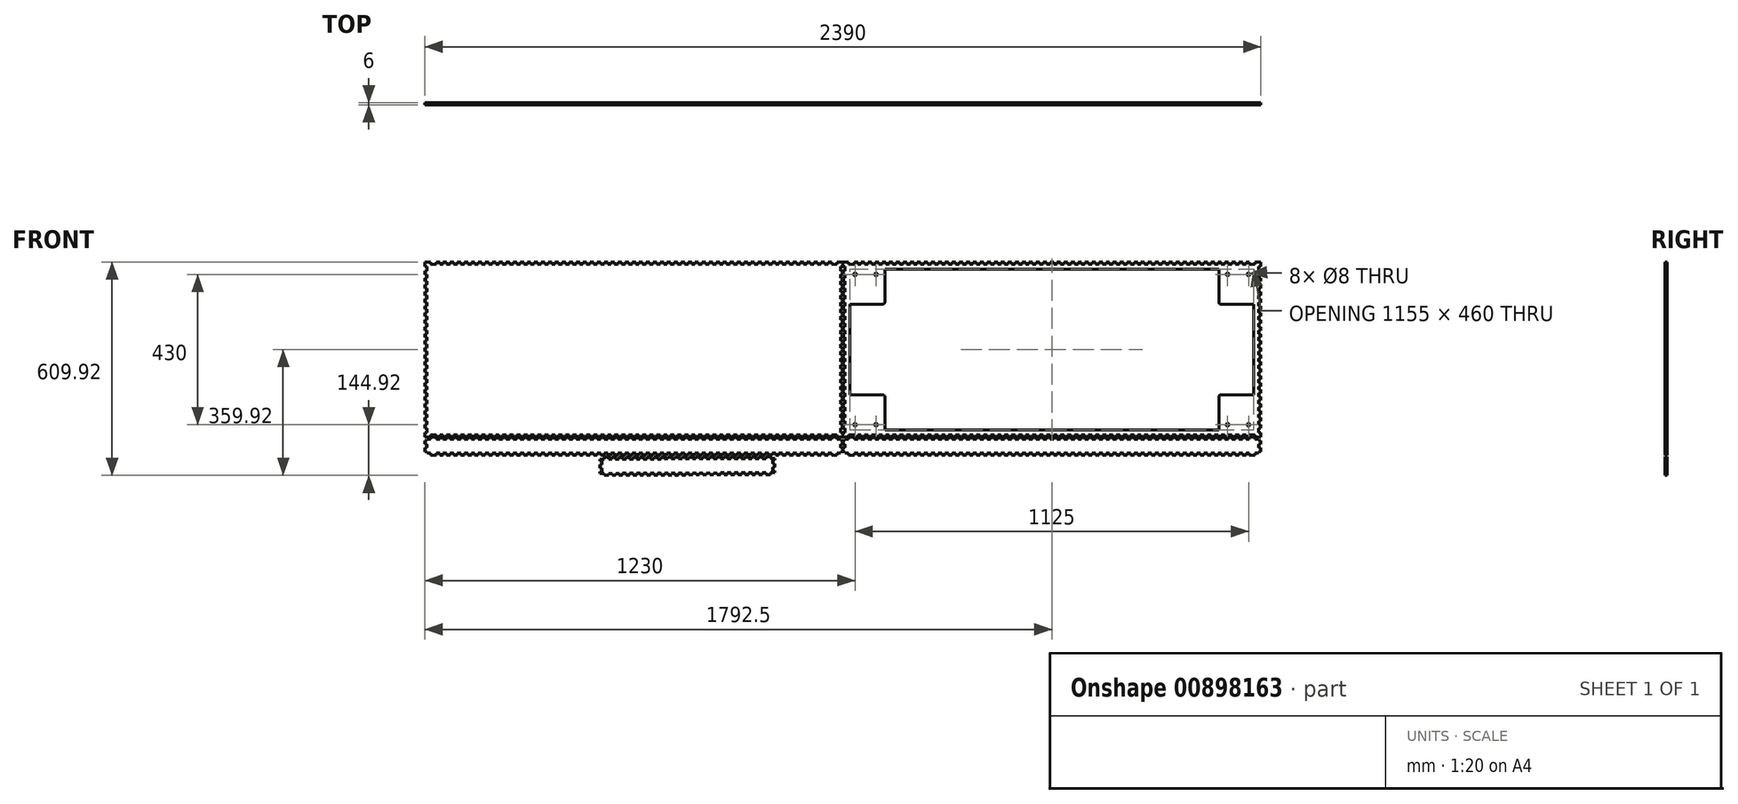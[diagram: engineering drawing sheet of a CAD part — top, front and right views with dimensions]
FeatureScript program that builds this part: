
annotation { "Feature Type Name" : "Feature", "Feature Type Description" : "" }
export const myFeature = defineFeature(function(context is Context, id is Id, definition is map)
    precondition{}
    {
        {
            var Q0;
            Q0=qCreatedBy(makeId("Front.planeOp"),FACE);
            var sketch = newSketch(context, id + "F0", { "sketchPlane" : qUnion([Q0])});
            skLineSegment(sketch, "E0", {"start": v(-1195, 306.06) * mm, "end": v(-1178.75, 306.06) * mm});
            skLineSegment(sketch, "E1", {"start": v(-1178.75, 306.06) * mm, "end": v(-1178.75, 300.06) * mm});
            skLineSegment(sketch, "E2", {"start": v(-1178.75, 300.06) * mm, "end": v(-1162.5, 300.06) * mm});
            skLineSegment(sketch, "E3", {"start": v(-1162.5, 300.06) * mm, "end": v(-1162.5, 306.06) * mm});
            skLineSegment(sketch, "E4", {"start": v(-1162.5, 306.06) * mm, "end": v(-1152.5, 306.06) * mm});
            skLineSegment(sketch, "E5", {"start": v(-1152.5, 306.06) * mm, "end": v(-1152.5, 300.06) * mm});
            skLineSegment(sketch, "E6", {"start": v(-1152.5, 300.06) * mm, "end": v(-1142.5, 300.06) * mm});
            skLineSegment(sketch, "E7", {"start": v(-1142.5, 300.06) * mm, "end": v(-1142.5, 306.06) * mm});
            skLineSegment(sketch, "E8", {"start": v(-1142.5, 306.06) * mm, "end": v(-1132.5, 306.06) * mm});
            skLineSegment(sketch, "E9", {"start": v(-1132.5, 306.06) * mm, "end": v(-1132.5, 300.06) * mm});
            skLineSegment(sketch, "E10", {"start": v(-1132.5, 300.06) * mm, "end": v(-1122.5, 300.06) * mm});
            skLineSegment(sketch, "E11", {"start": v(-1122.5, 300.06) * mm, "end": v(-1122.5, 306.06) * mm});
            skLineSegment(sketch, "E12", {"start": v(-1122.5, 306.06) * mm, "end": v(-1112.5, 306.06) * mm});
            skLineSegment(sketch, "E13", {"start": v(-1112.5, 306.06) * mm, "end": v(-1112.5, 300.06) * mm});
            skLineSegment(sketch, "E14", {"start": v(-1112.5, 300.06) * mm, "end": v(-1102.5, 300.06) * mm});
            skLineSegment(sketch, "E15", {"start": v(-1102.5, 300.06) * mm, "end": v(-1102.5, 306.06) * mm});
            skLineSegment(sketch, "E16", {"start": v(-1102.5, 306.06) * mm, "end": v(-1092.5, 306.06) * mm});
            skLineSegment(sketch, "E17", {"start": v(-1092.5, 306.06) * mm, "end": v(-1092.5, 300.06) * mm});
            skLineSegment(sketch, "E18", {"start": v(-1092.5, 300.06) * mm, "end": v(-1082.5, 300.06) * mm});
            skLineSegment(sketch, "E19", {"start": v(-1082.5, 300.06) * mm, "end": v(-1082.5, 306.06) * mm});
            skLineSegment(sketch, "E20", {"start": v(-1082.5, 306.06) * mm, "end": v(-1072.5, 306.06) * mm});
            skLineSegment(sketch, "E21", {"start": v(-1072.5, 306.06) * mm, "end": v(-1072.5, 300.06) * mm});
            skLineSegment(sketch, "E22", {"start": v(-1072.5, 300.06) * mm, "end": v(-1062.5, 300.06) * mm});
            skLineSegment(sketch, "E23", {"start": v(-1062.5, 300.06) * mm, "end": v(-1062.5, 306.06) * mm});
            skLineSegment(sketch, "E24", {"start": v(-1062.5, 306.06) * mm, "end": v(-1052.5, 306.06) * mm});
            skLineSegment(sketch, "E25", {"start": v(-1052.5, 306.06) * mm, "end": v(-1052.5, 300.06) * mm});
            skLineSegment(sketch, "E26", {"start": v(-1052.5, 300.06) * mm, "end": v(-1042.5, 300.06) * mm});
            skLineSegment(sketch, "E27", {"start": v(-1042.5, 300.06) * mm, "end": v(-1042.5, 306.06) * mm});
            skLineSegment(sketch, "E28", {"start": v(-1042.5, 306.06) * mm, "end": v(-1032.5, 306.06) * mm});
            skLineSegment(sketch, "E29", {"start": v(-1032.5, 306.06) * mm, "end": v(-1032.5, 300.06) * mm});
            skLineSegment(sketch, "E30", {"start": v(-1032.5, 300.06) * mm, "end": v(-1022.5, 300.06) * mm});
            skLineSegment(sketch, "E31", {"start": v(-1022.5, 300.06) * mm, "end": v(-1022.5, 306.06) * mm});
            skLineSegment(sketch, "E32", {"start": v(-1022.5, 306.06) * mm, "end": v(-1012.5, 306.06) * mm});
            skLineSegment(sketch, "E33", {"start": v(-1012.5, 306.06) * mm, "end": v(-1012.5, 300.06) * mm});
            skLineSegment(sketch, "E34", {"start": v(-1012.5, 300.06) * mm, "end": v(-1002.5, 300.06) * mm});
            skLineSegment(sketch, "E35", {"start": v(-1002.5, 300.06) * mm, "end": v(-1002.5, 306.06) * mm});
            skLineSegment(sketch, "E36", {"start": v(-1002.5, 306.06) * mm, "end": v(-992.5, 306.06) * mm});
            skLineSegment(sketch, "E37", {"start": v(-992.5, 306.06) * mm, "end": v(-992.5, 300.06) * mm});
            skLineSegment(sketch, "E38", {"start": v(-992.5, 300.06) * mm, "end": v(-982.5, 300.06) * mm});
            skLineSegment(sketch, "E39", {"start": v(-982.5, 300.06) * mm, "end": v(-982.5, 306.06) * mm});
            skLineSegment(sketch, "E40", {"start": v(-982.5, 306.06) * mm, "end": v(-972.5, 306.06) * mm});
            skLineSegment(sketch, "E41", {"start": v(-972.5, 306.06) * mm, "end": v(-972.5, 300.06) * mm});
            skLineSegment(sketch, "E42", {"start": v(-972.5, 300.06) * mm, "end": v(-962.5, 300.06) * mm});
            skLineSegment(sketch, "E43", {"start": v(-962.5, 300.06) * mm, "end": v(-962.5, 306.06) * mm});
            skLineSegment(sketch, "E44", {"start": v(-962.5, 306.06) * mm, "end": v(-952.5, 306.06) * mm});
            skLineSegment(sketch, "E45", {"start": v(-952.5, 306.06) * mm, "end": v(-952.5, 300.06) * mm});
            skLineSegment(sketch, "E46", {"start": v(-952.5, 300.06) * mm, "end": v(-942.5, 300.06) * mm});
            skLineSegment(sketch, "E47", {"start": v(-942.5, 300.06) * mm, "end": v(-942.5, 306.06) * mm});
            skLineSegment(sketch, "E48", {"start": v(-942.5, 306.06) * mm, "end": v(-932.5, 306.06) * mm});
            skLineSegment(sketch, "E49", {"start": v(-932.5, 306.06) * mm, "end": v(-932.5, 300.06) * mm});
            skLineSegment(sketch, "E50", {"start": v(-932.5, 300.06) * mm, "end": v(-922.5, 300.06) * mm});
            skLineSegment(sketch, "E51", {"start": v(-922.5, 300.06) * mm, "end": v(-922.5, 306.06) * mm});
            skLineSegment(sketch, "E52", {"start": v(-922.5, 306.06) * mm, "end": v(-912.5, 306.06) * mm});
            skLineSegment(sketch, "E53", {"start": v(-912.5, 306.06) * mm, "end": v(-912.5, 300.06) * mm});
            skLineSegment(sketch, "E54", {"start": v(-912.5, 300.06) * mm, "end": v(-902.5, 300.06) * mm});
            skLineSegment(sketch, "E55", {"start": v(-902.5, 300.06) * mm, "end": v(-902.5, 306.06) * mm});
            skLineSegment(sketch, "E56", {"start": v(-902.5, 306.06) * mm, "end": v(-892.5, 306.06) * mm});
            skLineSegment(sketch, "E57", {"start": v(-892.5, 306.06) * mm, "end": v(-892.5, 300.06) * mm});
            skLineSegment(sketch, "E58", {"start": v(-892.5, 300.06) * mm, "end": v(-882.5, 300.06) * mm});
            skLineSegment(sketch, "E59", {"start": v(-882.5, 300.06) * mm, "end": v(-882.5, 306.06) * mm});
            skLineSegment(sketch, "E60", {"start": v(-882.5, 306.06) * mm, "end": v(-872.5, 306.06) * mm});
            skLineSegment(sketch, "E61", {"start": v(-872.5, 306.06) * mm, "end": v(-872.5, 300.06) * mm});
            skLineSegment(sketch, "E62", {"start": v(-872.5, 300.06) * mm, "end": v(-862.5, 300.06) * mm});
            skLineSegment(sketch, "E63", {"start": v(-862.5, 300.06) * mm, "end": v(-862.5, 306.06) * mm});
            skLineSegment(sketch, "E64", {"start": v(-862.5, 306.06) * mm, "end": v(-852.5, 306.06) * mm});
            skLineSegment(sketch, "E65", {"start": v(-852.5, 306.06) * mm, "end": v(-852.5, 300.06) * mm});
            skLineSegment(sketch, "E66", {"start": v(-852.5, 300.06) * mm, "end": v(-842.5, 300.06) * mm});
            skLineSegment(sketch, "E67", {"start": v(-842.5, 300.06) * mm, "end": v(-842.5, 306.06) * mm});
            skLineSegment(sketch, "E68", {"start": v(-842.5, 306.06) * mm, "end": v(-832.5, 306.06) * mm});
            skLineSegment(sketch, "E69", {"start": v(-832.5, 306.06) * mm, "end": v(-832.5, 300.06) * mm});
            skLineSegment(sketch, "E70", {"start": v(-832.5, 300.06) * mm, "end": v(-822.5, 300.06) * mm});
            skLineSegment(sketch, "E71", {"start": v(-822.5, 300.06) * mm, "end": v(-822.5, 306.06) * mm});
            skLineSegment(sketch, "E72", {"start": v(-822.5, 306.06) * mm, "end": v(-812.5, 306.06) * mm});
            skLineSegment(sketch, "E73", {"start": v(-812.5, 306.06) * mm, "end": v(-812.5, 300.06) * mm});
            skLineSegment(sketch, "E74", {"start": v(-812.5, 300.06) * mm, "end": v(-802.5, 300.06) * mm});
            skLineSegment(sketch, "E75", {"start": v(-802.5, 300.06) * mm, "end": v(-802.5, 306.06) * mm});
            skLineSegment(sketch, "E76", {"start": v(-802.5, 306.06) * mm, "end": v(-792.5, 306.06) * mm});
            skLineSegment(sketch, "E77", {"start": v(-792.5, 306.06) * mm, "end": v(-792.5, 300.06) * mm});
            skLineSegment(sketch, "E78", {"start": v(-792.5, 300.06) * mm, "end": v(-782.5, 300.06) * mm});
            skLineSegment(sketch, "E79", {"start": v(-782.5, 300.06) * mm, "end": v(-782.5, 306.06) * mm});
            skLineSegment(sketch, "E80", {"start": v(-782.5, 306.06) * mm, "end": v(-772.5, 306.06) * mm});
            skLineSegment(sketch, "E81", {"start": v(-772.5, 306.06) * mm, "end": v(-772.5, 300.06) * mm});
            skLineSegment(sketch, "E82", {"start": v(-772.5, 300.06) * mm, "end": v(-762.5, 300.06) * mm});
            skLineSegment(sketch, "E83", {"start": v(-762.5, 300.06) * mm, "end": v(-762.5, 306.06) * mm});
            skLineSegment(sketch, "E84", {"start": v(-762.5, 306.06) * mm, "end": v(-752.5, 306.06) * mm});
            skLineSegment(sketch, "E85", {"start": v(-752.5, 306.06) * mm, "end": v(-752.5, 300.06) * mm});
            skLineSegment(sketch, "E86", {"start": v(-752.5, 300.06) * mm, "end": v(-742.5, 300.06) * mm});
            skLineSegment(sketch, "E87", {"start": v(-742.5, 300.06) * mm, "end": v(-742.5, 306.06) * mm});
            skLineSegment(sketch, "E88", {"start": v(-742.5, 306.06) * mm, "end": v(-732.5, 306.06) * mm});
            skLineSegment(sketch, "E89", {"start": v(-732.5, 306.06) * mm, "end": v(-732.5, 300.06) * mm});
            skLineSegment(sketch, "E90", {"start": v(-732.5, 300.06) * mm, "end": v(-722.5, 300.06) * mm});
            skLineSegment(sketch, "E91", {"start": v(-722.5, 300.06) * mm, "end": v(-722.5, 306.06) * mm});
            skLineSegment(sketch, "E92", {"start": v(-722.5, 306.06) * mm, "end": v(-712.5, 306.06) * mm});
            skLineSegment(sketch, "E93", {"start": v(-712.5, 306.06) * mm, "end": v(-712.5, 300.06) * mm});
            skLineSegment(sketch, "E94", {"start": v(-712.5, 300.06) * mm, "end": v(-702.5, 300.06) * mm});
            skLineSegment(sketch, "E95", {"start": v(-702.5, 300.06) * mm, "end": v(-702.5, 306.06) * mm});
            skLineSegment(sketch, "E96", {"start": v(-702.5, 306.06) * mm, "end": v(-692.5, 306.06) * mm});
            skLineSegment(sketch, "E97", {"start": v(-692.5, 306.06) * mm, "end": v(-692.5, 300.06) * mm});
            skLineSegment(sketch, "E98", {"start": v(-692.5, 300.06) * mm, "end": v(-682.5, 300.06) * mm});
            skLineSegment(sketch, "E99", {"start": v(-682.5, 300.06) * mm, "end": v(-682.5, 306.06) * mm});
            skLineSegment(sketch, "E100", {"start": v(-682.5, 306.06) * mm, "end": v(-672.5, 306.06) * mm});
            skLineSegment(sketch, "E101", {"start": v(-672.5, 306.06) * mm, "end": v(-672.5, 300.06) * mm});
            skLineSegment(sketch, "E102", {"start": v(-672.5, 300.06) * mm, "end": v(-662.5, 300.06) * mm});
            skLineSegment(sketch, "E103", {"start": v(-662.5, 300.06) * mm, "end": v(-662.5, 306.06) * mm});
            skLineSegment(sketch, "E104", {"start": v(-662.5, 306.06) * mm, "end": v(-652.5, 306.06) * mm});
            skLineSegment(sketch, "E105", {"start": v(-652.5, 306.06) * mm, "end": v(-652.5, 300.06) * mm});
            skLineSegment(sketch, "E106", {"start": v(-652.5, 300.06) * mm, "end": v(-642.5, 300.06) * mm});
            skLineSegment(sketch, "E107", {"start": v(-642.5, 300.06) * mm, "end": v(-642.5, 306.06) * mm});
            skLineSegment(sketch, "E108", {"start": v(-642.5, 306.06) * mm, "end": v(-632.5, 306.06) * mm});
            skLineSegment(sketch, "E109", {"start": v(-632.5, 306.06) * mm, "end": v(-632.5, 300.06) * mm});
            skLineSegment(sketch, "E110", {"start": v(-632.5, 300.06) * mm, "end": v(-622.5, 300.06) * mm});
            skLineSegment(sketch, "E111", {"start": v(-622.5, 300.06) * mm, "end": v(-622.5, 306.06) * mm});
            skLineSegment(sketch, "E112", {"start": v(-622.5, 306.06) * mm, "end": v(-612.5, 306.06) * mm});
            skLineSegment(sketch, "E113", {"start": v(-612.5, 306.06) * mm, "end": v(-612.5, 300.06) * mm});
            skLineSegment(sketch, "E114", {"start": v(-612.5, 300.06) * mm, "end": v(-602.5, 300.06) * mm});
            skLineSegment(sketch, "E115", {"start": v(-602.5, 300.06) * mm, "end": v(-602.5, 306.06) * mm});
            skLineSegment(sketch, "E116", {"start": v(-602.5, 306.06) * mm, "end": v(-592.5, 306.06) * mm});
            skLineSegment(sketch, "E117", {"start": v(-592.5, 306.06) * mm, "end": v(-592.5, 300.06) * mm});
            skLineSegment(sketch, "E118", {"start": v(-592.5, 300.06) * mm, "end": v(-582.5, 300.06) * mm});
            skLineSegment(sketch, "E119", {"start": v(-582.5, 300.06) * mm, "end": v(-582.5, 306.06) * mm});
            skLineSegment(sketch, "E120", {"start": v(-582.5, 306.06) * mm, "end": v(-572.5, 306.06) * mm});
            skLineSegment(sketch, "E121", {"start": v(-572.5, 306.06) * mm, "end": v(-572.5, 300.06) * mm});
            skLineSegment(sketch, "E122", {"start": v(-572.5, 300.06) * mm, "end": v(-562.5, 300.06) * mm});
            skLineSegment(sketch, "E123", {"start": v(-562.5, 300.06) * mm, "end": v(-562.5, 306.06) * mm});
            skLineSegment(sketch, "E124", {"start": v(-562.5, 306.06) * mm, "end": v(-552.5, 306.06) * mm});
            skLineSegment(sketch, "E125", {"start": v(-552.5, 306.06) * mm, "end": v(-552.5, 300.06) * mm});
            skLineSegment(sketch, "E126", {"start": v(-552.5, 300.06) * mm, "end": v(-542.5, 300.06) * mm});
            skLineSegment(sketch, "E127", {"start": v(-542.5, 300.06) * mm, "end": v(-542.5, 306.06) * mm});
            skLineSegment(sketch, "E128", {"start": v(-542.5, 306.06) * mm, "end": v(-532.5, 306.06) * mm});
            skLineSegment(sketch, "E129", {"start": v(-532.5, 306.06) * mm, "end": v(-532.5, 300.06) * mm});
            skLineSegment(sketch, "E130", {"start": v(-532.5, 300.06) * mm, "end": v(-522.5, 300.06) * mm});
            skLineSegment(sketch, "E131", {"start": v(-522.5, 300.06) * mm, "end": v(-522.5, 306.06) * mm});
            skLineSegment(sketch, "E132", {"start": v(-522.5, 306.06) * mm, "end": v(-512.5, 306.06) * mm});
            skLineSegment(sketch, "E133", {"start": v(-512.5, 306.06) * mm, "end": v(-512.5, 300.06) * mm});
            skLineSegment(sketch, "E134", {"start": v(-512.5, 300.06) * mm, "end": v(-502.5, 300.06) * mm});
            skLineSegment(sketch, "E135", {"start": v(-502.5, 300.06) * mm, "end": v(-502.5, 306.06) * mm});
            skLineSegment(sketch, "E136", {"start": v(-502.5, 306.06) * mm, "end": v(-492.5, 306.06) * mm});
            skLineSegment(sketch, "E137", {"start": v(-492.5, 306.06) * mm, "end": v(-492.5, 300.06) * mm});
            skLineSegment(sketch, "E138", {"start": v(-492.5, 300.06) * mm, "end": v(-482.5, 300.06) * mm});
            skLineSegment(sketch, "E139", {"start": v(-482.5, 300.06) * mm, "end": v(-482.5, 306.06) * mm});
            skLineSegment(sketch, "E140", {"start": v(-482.5, 306.06) * mm, "end": v(-472.5, 306.06) * mm});
            skLineSegment(sketch, "E141", {"start": v(-472.5, 306.06) * mm, "end": v(-472.5, 300.06) * mm});
            skLineSegment(sketch, "E142", {"start": v(-472.5, 300.06) * mm, "end": v(-462.5, 300.06) * mm});
            skLineSegment(sketch, "E143", {"start": v(-462.5, 300.06) * mm, "end": v(-462.5, 306.06) * mm});
            skLineSegment(sketch, "E144", {"start": v(-462.5, 306.06) * mm, "end": v(-452.5, 306.06) * mm});
            skLineSegment(sketch, "E145", {"start": v(-452.5, 306.06) * mm, "end": v(-452.5, 300.06) * mm});
            skLineSegment(sketch, "E146", {"start": v(-452.5, 300.06) * mm, "end": v(-442.5, 300.06) * mm});
            skLineSegment(sketch, "E147", {"start": v(-442.5, 300.06) * mm, "end": v(-442.5, 306.06) * mm});
            skLineSegment(sketch, "E148", {"start": v(-442.5, 306.06) * mm, "end": v(-432.5, 306.06) * mm});
            skLineSegment(sketch, "E149", {"start": v(-432.5, 306.06) * mm, "end": v(-432.5, 300.06) * mm});
            skLineSegment(sketch, "E150", {"start": v(-432.5, 300.06) * mm, "end": v(-422.5, 300.06) * mm});
            skLineSegment(sketch, "E151", {"start": v(-422.5, 300.06) * mm, "end": v(-422.5, 306.06) * mm});
            skLineSegment(sketch, "E152", {"start": v(-422.5, 306.06) * mm, "end": v(-412.5, 306.06) * mm});
            skLineSegment(sketch, "E153", {"start": v(-412.5, 306.06) * mm, "end": v(-412.5, 300.06) * mm});
            skLineSegment(sketch, "E154", {"start": v(-412.5, 300.06) * mm, "end": v(-402.5, 300.06) * mm});
            skLineSegment(sketch, "E155", {"start": v(-402.5, 300.06) * mm, "end": v(-402.5, 306.06) * mm});
            skLineSegment(sketch, "E156", {"start": v(-402.5, 306.06) * mm, "end": v(-392.5, 306.06) * mm});
            skLineSegment(sketch, "E157", {"start": v(-392.5, 306.06) * mm, "end": v(-392.5, 300.06) * mm});
            skLineSegment(sketch, "E158", {"start": v(-392.5, 300.06) * mm, "end": v(-382.5, 300.06) * mm});
            skLineSegment(sketch, "E159", {"start": v(-382.5, 300.06) * mm, "end": v(-382.5, 306.06) * mm});
            skLineSegment(sketch, "E160", {"start": v(-382.5, 306.06) * mm, "end": v(-372.5, 306.06) * mm});
            skLineSegment(sketch, "E161", {"start": v(-372.5, 306.06) * mm, "end": v(-372.5, 300.06) * mm});
            skLineSegment(sketch, "E162", {"start": v(-372.5, 300.06) * mm, "end": v(-362.5, 300.06) * mm});
            skLineSegment(sketch, "E163", {"start": v(-362.5, 300.06) * mm, "end": v(-362.5, 306.06) * mm});
            skLineSegment(sketch, "E164", {"start": v(-362.5, 306.06) * mm, "end": v(-352.5, 306.06) * mm});
            skLineSegment(sketch, "E165", {"start": v(-352.5, 306.06) * mm, "end": v(-352.5, 300.06) * mm});
            skLineSegment(sketch, "E166", {"start": v(-352.5, 300.06) * mm, "end": v(-342.5, 300.06) * mm});
            skLineSegment(sketch, "E167", {"start": v(-342.5, 300.06) * mm, "end": v(-342.5, 306.06) * mm});
            skLineSegment(sketch, "E168", {"start": v(-342.5, 306.06) * mm, "end": v(-332.5, 306.06) * mm});
            skLineSegment(sketch, "E169", {"start": v(-332.5, 306.06) * mm, "end": v(-332.5, 300.06) * mm});
            skLineSegment(sketch, "E170", {"start": v(-332.5, 300.06) * mm, "end": v(-322.5, 300.06) * mm});
            skLineSegment(sketch, "E171", {"start": v(-322.5, 300.06) * mm, "end": v(-322.5, 306.06) * mm});
            skLineSegment(sketch, "E172", {"start": v(-322.5, 306.06) * mm, "end": v(-312.5, 306.06) * mm});
            skLineSegment(sketch, "E173", {"start": v(-312.5, 306.06) * mm, "end": v(-312.5, 300.06) * mm});
            skLineSegment(sketch, "E174", {"start": v(-312.5, 300.06) * mm, "end": v(-302.5, 300.06) * mm});
            skLineSegment(sketch, "E175", {"start": v(-302.5, 300.06) * mm, "end": v(-302.5, 306.06) * mm});
            skLineSegment(sketch, "E176", {"start": v(-302.5, 306.06) * mm, "end": v(-292.5, 306.06) * mm});
            skLineSegment(sketch, "E177", {"start": v(-292.5, 306.06) * mm, "end": v(-292.5, 300.06) * mm});
            skLineSegment(sketch, "E178", {"start": v(-292.5, 300.06) * mm, "end": v(-282.5, 300.06) * mm});
            skLineSegment(sketch, "E179", {"start": v(-282.5, 300.06) * mm, "end": v(-282.5, 306.06) * mm});
            skLineSegment(sketch, "E180", {"start": v(-282.5, 306.06) * mm, "end": v(-272.5, 306.06) * mm});
            skLineSegment(sketch, "E181", {"start": v(-272.5, 306.06) * mm, "end": v(-272.5, 300.06) * mm});
            skLineSegment(sketch, "E182", {"start": v(-272.5, 300.06) * mm, "end": v(-262.5, 300.06) * mm});
            skLineSegment(sketch, "E183", {"start": v(-262.5, 300.06) * mm, "end": v(-262.5, 306.06) * mm});
            skLineSegment(sketch, "E184", {"start": v(-262.5, 306.06) * mm, "end": v(-252.5, 306.06) * mm});
            skLineSegment(sketch, "E185", {"start": v(-252.5, 306.06) * mm, "end": v(-252.5, 300.06) * mm});
            skLineSegment(sketch, "E186", {"start": v(-252.5, 300.06) * mm, "end": v(-242.5, 300.06) * mm});
            skLineSegment(sketch, "E187", {"start": v(-242.5, 300.06) * mm, "end": v(-242.5, 306.06) * mm});
            skLineSegment(sketch, "E188", {"start": v(-242.5, 306.06) * mm, "end": v(-232.5, 306.06) * mm});
            skLineSegment(sketch, "E189", {"start": v(-232.5, 306.06) * mm, "end": v(-232.5, 300.06) * mm});
            skLineSegment(sketch, "E190", {"start": v(-232.5, 300.06) * mm, "end": v(-222.5, 300.06) * mm});
            skLineSegment(sketch, "E191", {"start": v(-222.5, 300.06) * mm, "end": v(-222.5, 306.06) * mm});
            skLineSegment(sketch, "E192", {"start": v(-222.5, 306.06) * mm, "end": v(-212.5, 306.06) * mm});
            skLineSegment(sketch, "E193", {"start": v(-212.5, 306.06) * mm, "end": v(-212.5, 300.06) * mm});
            skLineSegment(sketch, "E194", {"start": v(-212.5, 300.06) * mm, "end": v(-202.5, 300.06) * mm});
            skLineSegment(sketch, "E195", {"start": v(-202.5, 300.06) * mm, "end": v(-202.5, 306.06) * mm});
            skLineSegment(sketch, "E196", {"start": v(-202.5, 306.06) * mm, "end": v(-192.5, 306.06) * mm});
            skLineSegment(sketch, "E197", {"start": v(-192.5, 306.06) * mm, "end": v(-192.5, 300.06) * mm});
            skLineSegment(sketch, "E198", {"start": v(-192.5, 300.06) * mm, "end": v(-182.5, 300.06) * mm});
            skLineSegment(sketch, "E199", {"start": v(-182.5, 300.06) * mm, "end": v(-182.5, 306.06) * mm});
            skLineSegment(sketch, "E200", {"start": v(-182.5, 306.06) * mm, "end": v(-172.5, 306.06) * mm});
            skLineSegment(sketch, "E201", {"start": v(-172.5, 306.06) * mm, "end": v(-172.5, 300.06) * mm});
            skLineSegment(sketch, "E202", {"start": v(-172.5, 300.06) * mm, "end": v(-162.5, 300.06) * mm});
            skLineSegment(sketch, "E203", {"start": v(-162.5, 300.06) * mm, "end": v(-162.5, 306.06) * mm});
            skLineSegment(sketch, "E204", {"start": v(-162.5, 306.06) * mm, "end": v(-152.5, 306.06) * mm});
            skLineSegment(sketch, "E205", {"start": v(-152.5, 306.06) * mm, "end": v(-152.5, 300.06) * mm});
            skLineSegment(sketch, "E206", {"start": v(-152.5, 300.06) * mm, "end": v(-142.5, 300.06) * mm});
            skLineSegment(sketch, "E207", {"start": v(-142.5, 300.06) * mm, "end": v(-142.5, 306.06) * mm});
            skLineSegment(sketch, "E208", {"start": v(-142.5, 306.06) * mm, "end": v(-132.5, 306.06) * mm});
            skLineSegment(sketch, "E209", {"start": v(-132.5, 306.06) * mm, "end": v(-132.5, 300.06) * mm});
            skLineSegment(sketch, "E210", {"start": v(-132.5, 300.06) * mm, "end": v(-122.5, 300.06) * mm});
            skLineSegment(sketch, "E211", {"start": v(-122.5, 300.06) * mm, "end": v(-122.5, 306.06) * mm});
            skLineSegment(sketch, "E212", {"start": v(-122.5, 306.06) * mm, "end": v(-112.5, 306.06) * mm});
            skLineSegment(sketch, "E213", {"start": v(-112.5, 306.06) * mm, "end": v(-112.5, 300.06) * mm});
            skLineSegment(sketch, "E214", {"start": v(-112.5, 300.06) * mm, "end": v(-102.5, 300.06) * mm});
            skLineSegment(sketch, "E215", {"start": v(-102.5, 300.06) * mm, "end": v(-102.5, 306.06) * mm});
            skLineSegment(sketch, "E216", {"start": v(-102.5, 306.06) * mm, "end": v(-92.5, 306.06) * mm});
            skLineSegment(sketch, "E217", {"start": v(-92.5, 306.06) * mm, "end": v(-92.5, 300.06) * mm});
            skLineSegment(sketch, "E218", {"start": v(-92.5, 300.06) * mm, "end": v(-82.5, 300.06) * mm});
            skLineSegment(sketch, "E219", {"start": v(-82.5, 300.06) * mm, "end": v(-82.5, 306.06) * mm});
            skLineSegment(sketch, "E220", {"start": v(-82.5, 306.06) * mm, "end": v(-72.5, 306.06) * mm});
            skLineSegment(sketch, "E221", {"start": v(-72.5, 306.06) * mm, "end": v(-72.5, 300.06) * mm});
            skLineSegment(sketch, "E222", {"start": v(-72.5, 300.06) * mm, "end": v(-62.5, 300.06) * mm});
            skLineSegment(sketch, "E223", {"start": v(-62.5, 300.06) * mm, "end": v(-62.5, 306.06) * mm});
            skLineSegment(sketch, "E224", {"start": v(-62.5, 306.06) * mm, "end": v(-52.5, 306.06) * mm});
            skLineSegment(sketch, "E225", {"start": v(-52.5, 306.06) * mm, "end": v(-52.5, 300.06) * mm});
            skLineSegment(sketch, "E226", {"start": v(-52.5, 300.06) * mm, "end": v(-42.5, 300.06) * mm});
            skLineSegment(sketch, "E227", {"start": v(-42.5, 300.06) * mm, "end": v(-42.5, 306.06) * mm});
            skLineSegment(sketch, "E228", {"start": v(-42.5, 306.06) * mm, "end": v(-32.5, 306.06) * mm});
            skLineSegment(sketch, "E229", {"start": v(-32.5, 306.06) * mm, "end": v(-32.5, 300.06) * mm});
            skLineSegment(sketch, "E230", {"start": v(-32.5, 300.06) * mm, "end": v(-16.25, 300.06) * mm});
            skLineSegment(sketch, "E231", {"start": v(-16.25, 300.06) * mm, "end": v(-16.25, 306.06) * mm});
            skLineSegment(sketch, "E232", {"start": v(-16.25, 306.06) * mm, "end": v(0, 306.06) * mm});
            skLineSegment(sketch, "E233", {"start": v(0, 306.06) * mm, "end": v(0, 293.56) * mm});
            skLineSegment(sketch, "E234", {"start": v(0, 293.56) * mm, "end": v(-6, 293.56) * mm});
            skLineSegment(sketch, "E235", {"start": v(-6, 293.56) * mm, "end": v(-6, 281.06) * mm});
            skLineSegment(sketch, "E236", {"start": v(-6, 281.06) * mm, "end": v(0, 281.06) * mm});
            skLineSegment(sketch, "E237", {"start": v(0, 281.06) * mm, "end": v(0, 271.06) * mm});
            skLineSegment(sketch, "E238", {"start": v(0, 271.06) * mm, "end": v(-6, 271.06) * mm});
            skLineSegment(sketch, "E239", {"start": v(-6, 271.06) * mm, "end": v(-6, 261.06) * mm});
            skLineSegment(sketch, "E240", {"start": v(-6, 261.06) * mm, "end": v(0, 261.06) * mm});
            skLineSegment(sketch, "E241", {"start": v(0, 261.06) * mm, "end": v(0, 251.06) * mm});
            skLineSegment(sketch, "E242", {"start": v(0, 251.06) * mm, "end": v(-6, 251.06) * mm});
            skLineSegment(sketch, "E243", {"start": v(-6, 251.06) * mm, "end": v(-6, 241.06) * mm});
            skLineSegment(sketch, "E244", {"start": v(-6, 241.06) * mm, "end": v(0, 241.06) * mm});
            skLineSegment(sketch, "E245", {"start": v(0, 241.06) * mm, "end": v(0, 231.06) * mm});
            skLineSegment(sketch, "E246", {"start": v(0, 231.06) * mm, "end": v(-6, 231.06) * mm});
            skLineSegment(sketch, "E247", {"start": v(-6, 231.06) * mm, "end": v(-6, 221.06) * mm});
            skLineSegment(sketch, "E248", {"start": v(-6, 221.06) * mm, "end": v(0, 221.06) * mm});
            skLineSegment(sketch, "E249", {"start": v(0, 221.06) * mm, "end": v(0, 211.06) * mm});
            skLineSegment(sketch, "E250", {"start": v(0, 211.06) * mm, "end": v(-6, 211.06) * mm});
            skLineSegment(sketch, "E251", {"start": v(-6, 211.06) * mm, "end": v(-6, 201.06) * mm});
            skLineSegment(sketch, "E252", {"start": v(-6, 201.06) * mm, "end": v(0, 201.06) * mm});
            skLineSegment(sketch, "E253", {"start": v(0, 201.06) * mm, "end": v(0, 191.06) * mm});
            skLineSegment(sketch, "E254", {"start": v(0, 191.06) * mm, "end": v(-6, 191.06) * mm});
            skLineSegment(sketch, "E255", {"start": v(-6, 191.06) * mm, "end": v(-6, 181.06) * mm});
            skLineSegment(sketch, "E256", {"start": v(-6, 181.06) * mm, "end": v(0, 181.06) * mm});
            skLineSegment(sketch, "E257", {"start": v(0, 181.06) * mm, "end": v(0, 171.06) * mm});
            skLineSegment(sketch, "E258", {"start": v(0, 171.06) * mm, "end": v(-6, 171.06) * mm});
            skLineSegment(sketch, "E259", {"start": v(-6, 171.06) * mm, "end": v(-6, 161.06) * mm});
            skLineSegment(sketch, "E260", {"start": v(-6, 161.06) * mm, "end": v(0, 161.06) * mm});
            skLineSegment(sketch, "E261", {"start": v(0, 161.06) * mm, "end": v(0, 151.06) * mm});
            skLineSegment(sketch, "E262", {"start": v(0, 151.06) * mm, "end": v(-6, 151.06) * mm});
            skLineSegment(sketch, "E263", {"start": v(-6, 151.06) * mm, "end": v(-6, 141.06) * mm});
            skLineSegment(sketch, "E264", {"start": v(-6, 141.06) * mm, "end": v(0, 141.06) * mm});
            skLineSegment(sketch, "E265", {"start": v(0, 141.06) * mm, "end": v(0, 131.06) * mm});
            skLineSegment(sketch, "E266", {"start": v(0, 131.06) * mm, "end": v(-6, 131.06) * mm});
            skLineSegment(sketch, "E267", {"start": v(-6, 131.06) * mm, "end": v(-6, 121.06) * mm});
            skLineSegment(sketch, "E268", {"start": v(-6, 121.06) * mm, "end": v(0, 121.06) * mm});
            skLineSegment(sketch, "E269", {"start": v(0, 121.06) * mm, "end": v(0, 111.06) * mm});
            skLineSegment(sketch, "E270", {"start": v(0, 111.06) * mm, "end": v(-6, 111.06) * mm});
            skLineSegment(sketch, "E271", {"start": v(-6, 111.06) * mm, "end": v(-6, 101.06) * mm});
            skLineSegment(sketch, "E272", {"start": v(-6, 101.06) * mm, "end": v(0, 101.06) * mm});
            skLineSegment(sketch, "E273", {"start": v(0, 101.06) * mm, "end": v(0, 91.06) * mm});
            skLineSegment(sketch, "E274", {"start": v(0, 91.06) * mm, "end": v(-6, 91.06) * mm});
            skLineSegment(sketch, "E275", {"start": v(-6, 91.06) * mm, "end": v(-6, 81.06) * mm});
            skLineSegment(sketch, "E276", {"start": v(-6, 81.06) * mm, "end": v(0, 81.06) * mm});
            skLineSegment(sketch, "E277", {"start": v(0, 81.06) * mm, "end": v(0, 71.06) * mm});
            skLineSegment(sketch, "E278", {"start": v(0, 71.06) * mm, "end": v(-6, 71.06) * mm});
            skLineSegment(sketch, "E279", {"start": v(-6, 71.06) * mm, "end": v(-6, 61.06) * mm});
            skLineSegment(sketch, "E280", {"start": v(-6, 61.06) * mm, "end": v(0, 61.06) * mm});
            skLineSegment(sketch, "E281", {"start": v(0, 61.06) * mm, "end": v(0, 51.06) * mm});
            skLineSegment(sketch, "E282", {"start": v(0, 51.06) * mm, "end": v(-6, 51.06) * mm});
            skLineSegment(sketch, "E283", {"start": v(-6, 51.06) * mm, "end": v(-6, 41.06) * mm});
            skLineSegment(sketch, "E284", {"start": v(-6, 41.06) * mm, "end": v(0, 41.06) * mm});
            skLineSegment(sketch, "E285", {"start": v(0, 41.06) * mm, "end": v(0, 31.06) * mm});
            skLineSegment(sketch, "E286", {"start": v(0, 31.06) * mm, "end": v(-6, 31.06) * mm});
            skLineSegment(sketch, "E287", {"start": v(-6, 31.06) * mm, "end": v(-6, 21.06) * mm});
            skLineSegment(sketch, "E288", {"start": v(-6, 21.06) * mm, "end": v(0, 21.06) * mm});
            skLineSegment(sketch, "E289", {"start": v(0, 21.06) * mm, "end": v(0, 11.06) * mm});
            skLineSegment(sketch, "E290", {"start": v(0, 11.06) * mm, "end": v(-6, 11.06) * mm});
            skLineSegment(sketch, "E291", {"start": v(-6, 11.06) * mm, "end": v(-6, 1.06) * mm});
            skLineSegment(sketch, "E292", {"start": v(-6, 1.06) * mm, "end": v(0, 1.06) * mm});
            skLineSegment(sketch, "E293", {"start": v(0, 1.06) * mm, "end": v(0, -8.94) * mm});
            skLineSegment(sketch, "E294", {"start": v(0, -8.94) * mm, "end": v(-6, -8.94) * mm});
            skLineSegment(sketch, "E295", {"start": v(-6, -8.94) * mm, "end": v(-6, -18.94) * mm});
            skLineSegment(sketch, "E296", {"start": v(-6, -18.94) * mm, "end": v(0, -18.94) * mm});
            skLineSegment(sketch, "E297", {"start": v(0, -18.94) * mm, "end": v(0, -28.94) * mm});
            skLineSegment(sketch, "E298", {"start": v(0, -28.94) * mm, "end": v(-6, -28.94) * mm});
            skLineSegment(sketch, "E299", {"start": v(-6, -28.94) * mm, "end": v(-6, -38.94) * mm});
            skLineSegment(sketch, "E300", {"start": v(-6, -38.94) * mm, "end": v(0, -38.94) * mm});
            skLineSegment(sketch, "E301", {"start": v(0, -38.94) * mm, "end": v(0, -48.94) * mm});
            skLineSegment(sketch, "E302", {"start": v(0, -48.94) * mm, "end": v(-6, -48.94) * mm});
            skLineSegment(sketch, "E303", {"start": v(-6, -48.94) * mm, "end": v(-6, -58.94) * mm});
            skLineSegment(sketch, "E304", {"start": v(-6, -58.94) * mm, "end": v(0, -58.94) * mm});
            skLineSegment(sketch, "E305", {"start": v(0, -58.94) * mm, "end": v(0, -68.94) * mm});
            skLineSegment(sketch, "E306", {"start": v(0, -68.94) * mm, "end": v(-6, -68.94) * mm});
            skLineSegment(sketch, "E307", {"start": v(-6, -68.94) * mm, "end": v(-6, -78.94) * mm});
            skLineSegment(sketch, "E308", {"start": v(-6, -78.94) * mm, "end": v(0, -78.94) * mm});
            skLineSegment(sketch, "E309", {"start": v(0, -78.94) * mm, "end": v(0, -88.94) * mm});
            skLineSegment(sketch, "E310", {"start": v(0, -88.94) * mm, "end": v(-6, -88.94) * mm});
            skLineSegment(sketch, "E311", {"start": v(-6, -88.94) * mm, "end": v(-6, -98.94) * mm});
            skLineSegment(sketch, "E312", {"start": v(-6, -98.94) * mm, "end": v(0, -98.94) * mm});
            skLineSegment(sketch, "E313", {"start": v(0, -98.94) * mm, "end": v(0, -108.94) * mm});
            skLineSegment(sketch, "E314", {"start": v(0, -108.94) * mm, "end": v(-6, -108.94) * mm});
            skLineSegment(sketch, "E315", {"start": v(-6, -108.94) * mm, "end": v(-6, -118.94) * mm});
            skLineSegment(sketch, "E316", {"start": v(-6, -118.94) * mm, "end": v(0, -118.94) * mm});
            skLineSegment(sketch, "E317", {"start": v(0, -118.94) * mm, "end": v(0, -128.94) * mm});
            skLineSegment(sketch, "E318", {"start": v(0, -128.94) * mm, "end": v(-6, -128.94) * mm});
            skLineSegment(sketch, "E319", {"start": v(-6, -128.94) * mm, "end": v(-6, -138.94) * mm});
            skLineSegment(sketch, "E320", {"start": v(-6, -138.94) * mm, "end": v(0, -138.94) * mm});
            skLineSegment(sketch, "E321", {"start": v(0, -138.94) * mm, "end": v(0, -148.94) * mm});
            skLineSegment(sketch, "E322", {"start": v(0, -148.94) * mm, "end": v(-6, -148.94) * mm});
            skLineSegment(sketch, "E323", {"start": v(-6, -148.94) * mm, "end": v(-6, -158.94) * mm});
            skLineSegment(sketch, "E324", {"start": v(-6, -158.94) * mm, "end": v(0, -158.94) * mm});
            skLineSegment(sketch, "E325", {"start": v(0, -158.94) * mm, "end": v(0, -168.94) * mm});
            skLineSegment(sketch, "E326", {"start": v(0, -168.94) * mm, "end": v(-6, -168.94) * mm});
            skLineSegment(sketch, "E327", {"start": v(-6, -168.94) * mm, "end": v(-6, -181.44) * mm});
            skLineSegment(sketch, "E328", {"start": v(-6, -181.44) * mm, "end": v(0, -181.44) * mm});
            skLineSegment(sketch, "E329", {"start": v(0, -181.44) * mm, "end": v(0, -193.94) * mm});
            skLineSegment(sketch, "E330", {"start": v(0, -193.94) * mm, "end": v(-16.25, -193.94) * mm});
            skLineSegment(sketch, "E331", {"start": v(-16.25, -193.94) * mm, "end": v(-16.25, -187.94) * mm});
            skLineSegment(sketch, "E332", {"start": v(-16.25, -187.94) * mm, "end": v(-32.5, -187.94) * mm});
            skLineSegment(sketch, "E333", {"start": v(-32.5, -187.94) * mm, "end": v(-32.5, -193.94) * mm});
            skLineSegment(sketch, "E334", {"start": v(-32.5, -193.94) * mm, "end": v(-42.5, -193.94) * mm});
            skLineSegment(sketch, "E335", {"start": v(-42.5, -193.94) * mm, "end": v(-42.5, -187.94) * mm});
            skLineSegment(sketch, "E336", {"start": v(-42.5, -187.94) * mm, "end": v(-52.5, -187.94) * mm});
            skLineSegment(sketch, "E337", {"start": v(-52.5, -187.94) * mm, "end": v(-52.5, -193.94) * mm});
            skLineSegment(sketch, "E338", {"start": v(-52.5, -193.94) * mm, "end": v(-62.5, -193.94) * mm});
            skLineSegment(sketch, "E339", {"start": v(-62.5, -193.94) * mm, "end": v(-62.5, -187.94) * mm});
            skLineSegment(sketch, "E340", {"start": v(-62.5, -187.94) * mm, "end": v(-72.5, -187.94) * mm});
            skLineSegment(sketch, "E341", {"start": v(-72.5, -187.94) * mm, "end": v(-72.5, -193.94) * mm});
            skLineSegment(sketch, "E342", {"start": v(-72.5, -193.94) * mm, "end": v(-82.5, -193.94) * mm});
            skLineSegment(sketch, "E343", {"start": v(-82.5, -193.94) * mm, "end": v(-82.5, -187.94) * mm});
            skLineSegment(sketch, "E344", {"start": v(-82.5, -187.94) * mm, "end": v(-92.5, -187.94) * mm});
            skLineSegment(sketch, "E345", {"start": v(-92.5, -187.94) * mm, "end": v(-92.5, -193.94) * mm});
            skLineSegment(sketch, "E346", {"start": v(-92.5, -193.94) * mm, "end": v(-102.5, -193.94) * mm});
            skLineSegment(sketch, "E347", {"start": v(-102.5, -193.94) * mm, "end": v(-102.5, -187.94) * mm});
            skLineSegment(sketch, "E348", {"start": v(-102.5, -187.94) * mm, "end": v(-112.5, -187.94) * mm});
            skLineSegment(sketch, "E349", {"start": v(-112.5, -187.94) * mm, "end": v(-112.5, -193.94) * mm});
            skLineSegment(sketch, "E350", {"start": v(-112.5, -193.94) * mm, "end": v(-122.5, -193.94) * mm});
            skLineSegment(sketch, "E351", {"start": v(-122.5, -193.94) * mm, "end": v(-122.5, -187.94) * mm});
            skLineSegment(sketch, "E352", {"start": v(-122.5, -187.94) * mm, "end": v(-132.5, -187.94) * mm});
            skLineSegment(sketch, "E353", {"start": v(-132.5, -187.94) * mm, "end": v(-132.5, -193.94) * mm});
            skLineSegment(sketch, "E354", {"start": v(-132.5, -193.94) * mm, "end": v(-142.5, -193.94) * mm});
            skLineSegment(sketch, "E355", {"start": v(-142.5, -193.94) * mm, "end": v(-142.5, -187.94) * mm});
            skLineSegment(sketch, "E356", {"start": v(-142.5, -187.94) * mm, "end": v(-152.5, -187.94) * mm});
            skLineSegment(sketch, "E357", {"start": v(-152.5, -187.94) * mm, "end": v(-152.5, -193.94) * mm});
            skLineSegment(sketch, "E358", {"start": v(-152.5, -193.94) * mm, "end": v(-162.5, -193.94) * mm});
            skLineSegment(sketch, "E359", {"start": v(-162.5, -193.94) * mm, "end": v(-162.5, -187.94) * mm});
            skLineSegment(sketch, "E360", {"start": v(-162.5, -187.94) * mm, "end": v(-172.5, -187.94) * mm});
            skLineSegment(sketch, "E361", {"start": v(-172.5, -187.94) * mm, "end": v(-172.5, -193.94) * mm});
            skLineSegment(sketch, "E362", {"start": v(-172.5, -193.94) * mm, "end": v(-182.5, -193.94) * mm});
            skLineSegment(sketch, "E363", {"start": v(-182.5, -193.94) * mm, "end": v(-182.5, -187.94) * mm});
            skLineSegment(sketch, "E364", {"start": v(-182.5, -187.94) * mm, "end": v(-192.5, -187.94) * mm});
            skLineSegment(sketch, "E365", {"start": v(-192.5, -187.94) * mm, "end": v(-192.5, -193.94) * mm});
            skLineSegment(sketch, "E366", {"start": v(-192.5, -193.94) * mm, "end": v(-202.5, -193.94) * mm});
            skLineSegment(sketch, "E367", {"start": v(-202.5, -193.94) * mm, "end": v(-202.5, -187.94) * mm});
            skLineSegment(sketch, "E368", {"start": v(-202.5, -187.94) * mm, "end": v(-212.5, -187.94) * mm});
            skLineSegment(sketch, "E369", {"start": v(-212.5, -187.94) * mm, "end": v(-212.5, -193.94) * mm});
            skLineSegment(sketch, "E370", {"start": v(-212.5, -193.94) * mm, "end": v(-222.5, -193.94) * mm});
            skLineSegment(sketch, "E371", {"start": v(-222.5, -193.94) * mm, "end": v(-222.5, -187.94) * mm});
            skLineSegment(sketch, "E372", {"start": v(-222.5, -187.94) * mm, "end": v(-232.5, -187.94) * mm});
            skLineSegment(sketch, "E373", {"start": v(-232.5, -187.94) * mm, "end": v(-232.5, -193.94) * mm});
            skLineSegment(sketch, "E374", {"start": v(-232.5, -193.94) * mm, "end": v(-242.5, -193.94) * mm});
            skLineSegment(sketch, "E375", {"start": v(-242.5, -193.94) * mm, "end": v(-242.5, -187.94) * mm});
            skLineSegment(sketch, "E376", {"start": v(-242.5, -187.94) * mm, "end": v(-252.5, -187.94) * mm});
            skLineSegment(sketch, "E377", {"start": v(-252.5, -187.94) * mm, "end": v(-252.5, -193.94) * mm});
            skLineSegment(sketch, "E378", {"start": v(-252.5, -193.94) * mm, "end": v(-262.5, -193.94) * mm});
            skLineSegment(sketch, "E379", {"start": v(-262.5, -193.94) * mm, "end": v(-262.5, -187.94) * mm});
            skLineSegment(sketch, "E380", {"start": v(-262.5, -187.94) * mm, "end": v(-272.5, -187.94) * mm});
            skLineSegment(sketch, "E381", {"start": v(-272.5, -187.94) * mm, "end": v(-272.5, -193.94) * mm});
            skLineSegment(sketch, "E382", {"start": v(-272.5, -193.94) * mm, "end": v(-282.5, -193.94) * mm});
            skLineSegment(sketch, "E383", {"start": v(-282.5, -193.94) * mm, "end": v(-282.5, -187.94) * mm});
            skLineSegment(sketch, "E384", {"start": v(-282.5, -187.94) * mm, "end": v(-292.5, -187.94) * mm});
            skLineSegment(sketch, "E385", {"start": v(-292.5, -187.94) * mm, "end": v(-292.5, -193.94) * mm});
            skLineSegment(sketch, "E386", {"start": v(-292.5, -193.94) * mm, "end": v(-302.5, -193.94) * mm});
            skLineSegment(sketch, "E387", {"start": v(-302.5, -193.94) * mm, "end": v(-302.5, -187.94) * mm});
            skLineSegment(sketch, "E388", {"start": v(-302.5, -187.94) * mm, "end": v(-312.5, -187.94) * mm});
            skLineSegment(sketch, "E389", {"start": v(-312.5, -187.94) * mm, "end": v(-312.5, -193.94) * mm});
            skLineSegment(sketch, "E390", {"start": v(-312.5, -193.94) * mm, "end": v(-322.5, -193.94) * mm});
            skLineSegment(sketch, "E391", {"start": v(-322.5, -193.94) * mm, "end": v(-322.5, -187.94) * mm});
            skLineSegment(sketch, "E392", {"start": v(-322.5, -187.94) * mm, "end": v(-332.5, -187.94) * mm});
            skLineSegment(sketch, "E393", {"start": v(-332.5, -187.94) * mm, "end": v(-332.5, -193.94) * mm});
            skLineSegment(sketch, "E394", {"start": v(-332.5, -193.94) * mm, "end": v(-342.5, -193.94) * mm});
            skLineSegment(sketch, "E395", {"start": v(-342.5, -193.94) * mm, "end": v(-342.5, -187.94) * mm});
            skLineSegment(sketch, "E396", {"start": v(-342.5, -187.94) * mm, "end": v(-352.5, -187.94) * mm});
            skLineSegment(sketch, "E397", {"start": v(-352.5, -187.94) * mm, "end": v(-352.5, -193.94) * mm});
            skLineSegment(sketch, "E398", {"start": v(-352.5, -193.94) * mm, "end": v(-362.5, -193.94) * mm});
            skLineSegment(sketch, "E399", {"start": v(-362.5, -193.94) * mm, "end": v(-362.5, -187.94) * mm});
            skLineSegment(sketch, "E400", {"start": v(-362.5, -187.94) * mm, "end": v(-372.5, -187.94) * mm});
            skLineSegment(sketch, "E401", {"start": v(-372.5, -187.94) * mm, "end": v(-372.5, -193.94) * mm});
            skLineSegment(sketch, "E402", {"start": v(-372.5, -193.94) * mm, "end": v(-382.5, -193.94) * mm});
            skLineSegment(sketch, "E403", {"start": v(-382.5, -193.94) * mm, "end": v(-382.5, -187.94) * mm});
            skLineSegment(sketch, "E404", {"start": v(-382.5, -187.94) * mm, "end": v(-392.5, -187.94) * mm});
            skLineSegment(sketch, "E405", {"start": v(-392.5, -187.94) * mm, "end": v(-392.5, -193.94) * mm});
            skLineSegment(sketch, "E406", {"start": v(-392.5, -193.94) * mm, "end": v(-402.5, -193.94) * mm});
            skLineSegment(sketch, "E407", {"start": v(-402.5, -193.94) * mm, "end": v(-402.5, -187.94) * mm});
            skLineSegment(sketch, "E408", {"start": v(-402.5, -187.94) * mm, "end": v(-412.5, -187.94) * mm});
            skLineSegment(sketch, "E409", {"start": v(-412.5, -187.94) * mm, "end": v(-412.5, -193.94) * mm});
            skLineSegment(sketch, "E410", {"start": v(-412.5, -193.94) * mm, "end": v(-422.5, -193.94) * mm});
            skLineSegment(sketch, "E411", {"start": v(-422.5, -193.94) * mm, "end": v(-422.5, -187.94) * mm});
            skLineSegment(sketch, "E412", {"start": v(-422.5, -187.94) * mm, "end": v(-432.5, -187.94) * mm});
            skLineSegment(sketch, "E413", {"start": v(-432.5, -187.94) * mm, "end": v(-432.5, -193.94) * mm});
            skLineSegment(sketch, "E414", {"start": v(-432.5, -193.94) * mm, "end": v(-442.5, -193.94) * mm});
            skLineSegment(sketch, "E415", {"start": v(-442.5, -193.94) * mm, "end": v(-442.5, -187.94) * mm});
            skLineSegment(sketch, "E416", {"start": v(-442.5, -187.94) * mm, "end": v(-452.5, -187.94) * mm});
            skLineSegment(sketch, "E417", {"start": v(-452.5, -187.94) * mm, "end": v(-452.5, -193.94) * mm});
            skLineSegment(sketch, "E418", {"start": v(-452.5, -193.94) * mm, "end": v(-462.5, -193.94) * mm});
            skLineSegment(sketch, "E419", {"start": v(-462.5, -193.94) * mm, "end": v(-462.5, -187.94) * mm});
            skLineSegment(sketch, "E420", {"start": v(-462.5, -187.94) * mm, "end": v(-472.5, -187.94) * mm});
            skLineSegment(sketch, "E421", {"start": v(-472.5, -187.94) * mm, "end": v(-472.5, -193.94) * mm});
            skLineSegment(sketch, "E422", {"start": v(-472.5, -193.94) * mm, "end": v(-482.5, -193.94) * mm});
            skLineSegment(sketch, "E423", {"start": v(-482.5, -193.94) * mm, "end": v(-482.5, -187.94) * mm});
            skLineSegment(sketch, "E424", {"start": v(-482.5, -187.94) * mm, "end": v(-492.5, -187.94) * mm});
            skLineSegment(sketch, "E425", {"start": v(-492.5, -187.94) * mm, "end": v(-492.5, -193.94) * mm});
            skLineSegment(sketch, "E426", {"start": v(-492.5, -193.94) * mm, "end": v(-502.5, -193.94) * mm});
            skLineSegment(sketch, "E427", {"start": v(-502.5, -193.94) * mm, "end": v(-502.5, -187.94) * mm});
            skLineSegment(sketch, "E428", {"start": v(-502.5, -187.94) * mm, "end": v(-512.5, -187.94) * mm});
            skLineSegment(sketch, "E429", {"start": v(-512.5, -187.94) * mm, "end": v(-512.5, -193.94) * mm});
            skLineSegment(sketch, "E430", {"start": v(-512.5, -193.94) * mm, "end": v(-522.5, -193.94) * mm});
            skLineSegment(sketch, "E431", {"start": v(-522.5, -193.94) * mm, "end": v(-522.5, -187.94) * mm});
            skLineSegment(sketch, "E432", {"start": v(-522.5, -187.94) * mm, "end": v(-532.5, -187.94) * mm});
            skLineSegment(sketch, "E433", {"start": v(-532.5, -187.94) * mm, "end": v(-532.5, -193.94) * mm});
            skLineSegment(sketch, "E434", {"start": v(-532.5, -193.94) * mm, "end": v(-542.5, -193.94) * mm});
            skLineSegment(sketch, "E435", {"start": v(-542.5, -193.94) * mm, "end": v(-542.5, -187.94) * mm});
            skLineSegment(sketch, "E436", {"start": v(-542.5, -187.94) * mm, "end": v(-552.5, -187.94) * mm});
            skLineSegment(sketch, "E437", {"start": v(-552.5, -187.94) * mm, "end": v(-552.5, -193.94) * mm});
            skLineSegment(sketch, "E438", {"start": v(-552.5, -193.94) * mm, "end": v(-562.5, -193.94) * mm});
            skLineSegment(sketch, "E439", {"start": v(-562.5, -193.94) * mm, "end": v(-562.5, -187.94) * mm});
            skLineSegment(sketch, "E440", {"start": v(-562.5, -187.94) * mm, "end": v(-572.5, -187.94) * mm});
            skLineSegment(sketch, "E441", {"start": v(-572.5, -187.94) * mm, "end": v(-572.5, -193.94) * mm});
            skLineSegment(sketch, "E442", {"start": v(-572.5, -193.94) * mm, "end": v(-582.5, -193.94) * mm});
            skLineSegment(sketch, "E443", {"start": v(-582.5, -193.94) * mm, "end": v(-582.5, -187.94) * mm});
            skLineSegment(sketch, "E444", {"start": v(-582.5, -187.94) * mm, "end": v(-592.5, -187.94) * mm});
            skLineSegment(sketch, "E445", {"start": v(-592.5, -187.94) * mm, "end": v(-592.5, -193.94) * mm});
            skLineSegment(sketch, "E446", {"start": v(-592.5, -193.94) * mm, "end": v(-602.5, -193.94) * mm});
            skLineSegment(sketch, "E447", {"start": v(-602.5, -193.94) * mm, "end": v(-602.5, -187.94) * mm});
            skLineSegment(sketch, "E448", {"start": v(-602.5, -187.94) * mm, "end": v(-612.5, -187.94) * mm});
            skLineSegment(sketch, "E449", {"start": v(-612.5, -187.94) * mm, "end": v(-612.5, -193.94) * mm});
            skLineSegment(sketch, "E450", {"start": v(-612.5, -193.94) * mm, "end": v(-622.5, -193.94) * mm});
            skLineSegment(sketch, "E451", {"start": v(-622.5, -193.94) * mm, "end": v(-622.5, -187.94) * mm});
            skLineSegment(sketch, "E452", {"start": v(-622.5, -187.94) * mm, "end": v(-632.5, -187.94) * mm});
            skLineSegment(sketch, "E453", {"start": v(-632.5, -187.94) * mm, "end": v(-632.5, -193.94) * mm});
            skLineSegment(sketch, "E454", {"start": v(-632.5, -193.94) * mm, "end": v(-642.5, -193.94) * mm});
            skLineSegment(sketch, "E455", {"start": v(-642.5, -193.94) * mm, "end": v(-642.5, -187.94) * mm});
            skLineSegment(sketch, "E456", {"start": v(-642.5, -187.94) * mm, "end": v(-652.5, -187.94) * mm});
            skLineSegment(sketch, "E457", {"start": v(-652.5, -187.94) * mm, "end": v(-652.5, -193.94) * mm});
            skLineSegment(sketch, "E458", {"start": v(-652.5, -193.94) * mm, "end": v(-662.5, -193.94) * mm});
            skLineSegment(sketch, "E459", {"start": v(-662.5, -193.94) * mm, "end": v(-662.5, -187.94) * mm});
            skLineSegment(sketch, "E460", {"start": v(-662.5, -187.94) * mm, "end": v(-672.5, -187.94) * mm});
            skLineSegment(sketch, "E461", {"start": v(-672.5, -187.94) * mm, "end": v(-672.5, -193.94) * mm});
            skLineSegment(sketch, "E462", {"start": v(-672.5, -193.94) * mm, "end": v(-682.5, -193.94) * mm});
            skLineSegment(sketch, "E463", {"start": v(-682.5, -193.94) * mm, "end": v(-682.5, -187.94) * mm});
            skLineSegment(sketch, "E464", {"start": v(-682.5, -187.94) * mm, "end": v(-692.5, -187.94) * mm});
            skLineSegment(sketch, "E465", {"start": v(-692.5, -187.94) * mm, "end": v(-692.5, -193.94) * mm});
            skLineSegment(sketch, "E466", {"start": v(-692.5, -193.94) * mm, "end": v(-702.5, -193.94) * mm});
            skLineSegment(sketch, "E467", {"start": v(-702.5, -193.94) * mm, "end": v(-702.5, -187.94) * mm});
            skLineSegment(sketch, "E468", {"start": v(-702.5, -187.94) * mm, "end": v(-712.5, -187.94) * mm});
            skLineSegment(sketch, "E469", {"start": v(-712.5, -187.94) * mm, "end": v(-712.5, -193.94) * mm});
            skLineSegment(sketch, "E470", {"start": v(-712.5, -193.94) * mm, "end": v(-722.5, -193.94) * mm});
            skLineSegment(sketch, "E471", {"start": v(-722.5, -193.94) * mm, "end": v(-722.5, -187.94) * mm});
            skLineSegment(sketch, "E472", {"start": v(-722.5, -187.94) * mm, "end": v(-732.5, -187.94) * mm});
            skLineSegment(sketch, "E473", {"start": v(-732.5, -187.94) * mm, "end": v(-732.5, -193.94) * mm});
            skLineSegment(sketch, "E474", {"start": v(-732.5, -193.94) * mm, "end": v(-742.5, -193.94) * mm});
            skLineSegment(sketch, "E475", {"start": v(-742.5, -193.94) * mm, "end": v(-742.5, -187.94) * mm});
            skLineSegment(sketch, "E476", {"start": v(-742.5, -187.94) * mm, "end": v(-752.5, -187.94) * mm});
            skLineSegment(sketch, "E477", {"start": v(-752.5, -187.94) * mm, "end": v(-752.5, -193.94) * mm});
            skLineSegment(sketch, "E478", {"start": v(-752.5, -193.94) * mm, "end": v(-762.5, -193.94) * mm});
            skLineSegment(sketch, "E479", {"start": v(-762.5, -193.94) * mm, "end": v(-762.5, -187.94) * mm});
            skLineSegment(sketch, "E480", {"start": v(-762.5, -187.94) * mm, "end": v(-772.5, -187.94) * mm});
            skLineSegment(sketch, "E481", {"start": v(-772.5, -187.94) * mm, "end": v(-772.5, -193.94) * mm});
            skLineSegment(sketch, "E482", {"start": v(-772.5, -193.94) * mm, "end": v(-782.5, -193.94) * mm});
            skLineSegment(sketch, "E483", {"start": v(-782.5, -193.94) * mm, "end": v(-782.5, -187.94) * mm});
            skLineSegment(sketch, "E484", {"start": v(-782.5, -187.94) * mm, "end": v(-792.5, -187.94) * mm});
            skLineSegment(sketch, "E485", {"start": v(-792.5, -187.94) * mm, "end": v(-792.5, -193.94) * mm});
            skLineSegment(sketch, "E486", {"start": v(-792.5, -193.94) * mm, "end": v(-802.5, -193.94) * mm});
            skLineSegment(sketch, "E487", {"start": v(-802.5, -193.94) * mm, "end": v(-802.5, -187.94) * mm});
            skLineSegment(sketch, "E488", {"start": v(-802.5, -187.94) * mm, "end": v(-812.5, -187.94) * mm});
            skLineSegment(sketch, "E489", {"start": v(-812.5, -187.94) * mm, "end": v(-812.5, -193.94) * mm});
            skLineSegment(sketch, "E490", {"start": v(-812.5, -193.94) * mm, "end": v(-822.5, -193.94) * mm});
            skLineSegment(sketch, "E491", {"start": v(-822.5, -193.94) * mm, "end": v(-822.5, -187.94) * mm});
            skLineSegment(sketch, "E492", {"start": v(-822.5, -187.94) * mm, "end": v(-832.5, -187.94) * mm});
            skLineSegment(sketch, "E493", {"start": v(-832.5, -187.94) * mm, "end": v(-832.5, -193.94) * mm});
            skLineSegment(sketch, "E494", {"start": v(-832.5, -193.94) * mm, "end": v(-842.5, -193.94) * mm});
            skLineSegment(sketch, "E495", {"start": v(-842.5, -193.94) * mm, "end": v(-842.5, -187.94) * mm});
            skLineSegment(sketch, "E496", {"start": v(-842.5, -187.94) * mm, "end": v(-852.5, -187.94) * mm});
            skLineSegment(sketch, "E497", {"start": v(-852.5, -187.94) * mm, "end": v(-852.5, -193.94) * mm});
            skLineSegment(sketch, "E498", {"start": v(-852.5, -193.94) * mm, "end": v(-862.5, -193.94) * mm});
            skLineSegment(sketch, "E499", {"start": v(-862.5, -193.94) * mm, "end": v(-862.5, -187.94) * mm});
            skLineSegment(sketch, "E500", {"start": v(-862.5, -187.94) * mm, "end": v(-872.5, -187.94) * mm});
            skLineSegment(sketch, "E501", {"start": v(-872.5, -187.94) * mm, "end": v(-872.5, -193.94) * mm});
            skLineSegment(sketch, "E502", {"start": v(-872.5, -193.94) * mm, "end": v(-882.5, -193.94) * mm});
            skLineSegment(sketch, "E503", {"start": v(-882.5, -193.94) * mm, "end": v(-882.5, -187.94) * mm});
            skLineSegment(sketch, "E504", {"start": v(-882.5, -187.94) * mm, "end": v(-892.5, -187.94) * mm});
            skLineSegment(sketch, "E505", {"start": v(-892.5, -187.94) * mm, "end": v(-892.5, -193.94) * mm});
            skLineSegment(sketch, "E506", {"start": v(-892.5, -193.94) * mm, "end": v(-902.5, -193.94) * mm});
            skLineSegment(sketch, "E507", {"start": v(-902.5, -193.94) * mm, "end": v(-902.5, -187.94) * mm});
            skLineSegment(sketch, "E508", {"start": v(-902.5, -187.94) * mm, "end": v(-912.5, -187.94) * mm});
            skLineSegment(sketch, "E509", {"start": v(-912.5, -187.94) * mm, "end": v(-912.5, -193.94) * mm});
            skLineSegment(sketch, "E510", {"start": v(-912.5, -193.94) * mm, "end": v(-922.5, -193.94) * mm});
            skLineSegment(sketch, "E511", {"start": v(-922.5, -193.94) * mm, "end": v(-922.5, -187.94) * mm});
            skLineSegment(sketch, "E512", {"start": v(-922.5, -187.94) * mm, "end": v(-932.5, -187.94) * mm});
            skLineSegment(sketch, "E513", {"start": v(-932.5, -187.94) * mm, "end": v(-932.5, -193.94) * mm});
            skLineSegment(sketch, "E514", {"start": v(-932.5, -193.94) * mm, "end": v(-942.5, -193.94) * mm});
            skLineSegment(sketch, "E515", {"start": v(-942.5, -193.94) * mm, "end": v(-942.5, -187.94) * mm});
            skLineSegment(sketch, "E516", {"start": v(-942.5, -187.94) * mm, "end": v(-952.5, -187.94) * mm});
            skLineSegment(sketch, "E517", {"start": v(-952.5, -187.94) * mm, "end": v(-952.5, -193.94) * mm});
            skLineSegment(sketch, "E518", {"start": v(-952.5, -193.94) * mm, "end": v(-962.5, -193.94) * mm});
            skLineSegment(sketch, "E519", {"start": v(-962.5, -193.94) * mm, "end": v(-962.5, -187.94) * mm});
            skLineSegment(sketch, "E520", {"start": v(-962.5, -187.94) * mm, "end": v(-972.5, -187.94) * mm});
            skLineSegment(sketch, "E521", {"start": v(-972.5, -187.94) * mm, "end": v(-972.5, -193.94) * mm});
            skLineSegment(sketch, "E522", {"start": v(-972.5, -193.94) * mm, "end": v(-982.5, -193.94) * mm});
            skLineSegment(sketch, "E523", {"start": v(-982.5, -193.94) * mm, "end": v(-982.5, -187.94) * mm});
            skLineSegment(sketch, "E524", {"start": v(-982.5, -187.94) * mm, "end": v(-992.5, -187.94) * mm});
            skLineSegment(sketch, "E525", {"start": v(-992.5, -187.94) * mm, "end": v(-992.5, -193.94) * mm});
            skLineSegment(sketch, "E526", {"start": v(-992.5, -193.94) * mm, "end": v(-1002.5, -193.94) * mm});
            skLineSegment(sketch, "E527", {"start": v(-1002.5, -193.94) * mm, "end": v(-1002.5, -187.94) * mm});
            skLineSegment(sketch, "E528", {"start": v(-1002.5, -187.94) * mm, "end": v(-1012.5, -187.94) * mm});
            skLineSegment(sketch, "E529", {"start": v(-1012.5, -187.94) * mm, "end": v(-1012.5, -193.94) * mm});
            skLineSegment(sketch, "E530", {"start": v(-1012.5, -193.94) * mm, "end": v(-1022.5, -193.94) * mm});
            skLineSegment(sketch, "E531", {"start": v(-1022.5, -193.94) * mm, "end": v(-1022.5, -187.94) * mm});
            skLineSegment(sketch, "E532", {"start": v(-1022.5, -187.94) * mm, "end": v(-1032.5, -187.94) * mm});
            skLineSegment(sketch, "E533", {"start": v(-1032.5, -187.94) * mm, "end": v(-1032.5, -193.94) * mm});
            skLineSegment(sketch, "E534", {"start": v(-1032.5, -193.94) * mm, "end": v(-1042.5, -193.94) * mm});
            skLineSegment(sketch, "E535", {"start": v(-1042.5, -193.94) * mm, "end": v(-1042.5, -187.94) * mm});
            skLineSegment(sketch, "E536", {"start": v(-1042.5, -187.94) * mm, "end": v(-1052.5, -187.94) * mm});
            skLineSegment(sketch, "E537", {"start": v(-1052.5, -187.94) * mm, "end": v(-1052.5, -193.94) * mm});
            skLineSegment(sketch, "E538", {"start": v(-1052.5, -193.94) * mm, "end": v(-1062.5, -193.94) * mm});
            skLineSegment(sketch, "E539", {"start": v(-1062.5, -193.94) * mm, "end": v(-1062.5, -187.94) * mm});
            skLineSegment(sketch, "E540", {"start": v(-1062.5, -187.94) * mm, "end": v(-1072.5, -187.94) * mm});
            skLineSegment(sketch, "E541", {"start": v(-1072.5, -187.94) * mm, "end": v(-1072.5, -193.94) * mm});
            skLineSegment(sketch, "E542", {"start": v(-1072.5, -193.94) * mm, "end": v(-1082.5, -193.94) * mm});
            skLineSegment(sketch, "E543", {"start": v(-1082.5, -193.94) * mm, "end": v(-1082.5, -187.94) * mm});
            skLineSegment(sketch, "E544", {"start": v(-1082.5, -187.94) * mm, "end": v(-1092.5, -187.94) * mm});
            skLineSegment(sketch, "E545", {"start": v(-1092.5, -187.94) * mm, "end": v(-1092.5, -193.94) * mm});
            skLineSegment(sketch, "E546", {"start": v(-1092.5, -193.94) * mm, "end": v(-1102.5, -193.94) * mm});
            skLineSegment(sketch, "E547", {"start": v(-1102.5, -193.94) * mm, "end": v(-1102.5, -187.94) * mm});
            skLineSegment(sketch, "E548", {"start": v(-1102.5, -187.94) * mm, "end": v(-1112.5, -187.94) * mm});
            skLineSegment(sketch, "E549", {"start": v(-1112.5, -187.94) * mm, "end": v(-1112.5, -193.94) * mm});
            skLineSegment(sketch, "E550", {"start": v(-1112.5, -193.94) * mm, "end": v(-1122.5, -193.94) * mm});
            skLineSegment(sketch, "E551", {"start": v(-1122.5, -193.94) * mm, "end": v(-1122.5, -187.94) * mm});
            skLineSegment(sketch, "E552", {"start": v(-1122.5, -187.94) * mm, "end": v(-1132.5, -187.94) * mm});
            skLineSegment(sketch, "E553", {"start": v(-1132.5, -187.94) * mm, "end": v(-1132.5, -193.94) * mm});
            skLineSegment(sketch, "E554", {"start": v(-1132.5, -193.94) * mm, "end": v(-1142.5, -193.94) * mm});
            skLineSegment(sketch, "E555", {"start": v(-1142.5, -193.94) * mm, "end": v(-1142.5, -187.94) * mm});
            skLineSegment(sketch, "E556", {"start": v(-1142.5, -187.94) * mm, "end": v(-1152.5, -187.94) * mm});
            skLineSegment(sketch, "E557", {"start": v(-1152.5, -187.94) * mm, "end": v(-1152.5, -193.94) * mm});
            skLineSegment(sketch, "E558", {"start": v(-1152.5, -193.94) * mm, "end": v(-1162.5, -193.94) * mm});
            skLineSegment(sketch, "E559", {"start": v(-1162.5, -193.94) * mm, "end": v(-1162.5, -187.94) * mm});
            skLineSegment(sketch, "E560", {"start": v(-1162.5, -187.94) * mm, "end": v(-1178.75, -187.94) * mm});
            skLineSegment(sketch, "E561", {"start": v(-1178.75, -187.94) * mm, "end": v(-1178.75, -193.94) * mm});
            skLineSegment(sketch, "E562", {"start": v(-1178.75, -193.94) * mm, "end": v(-1195, -193.94) * mm});
            skLineSegment(sketch, "E563", {"start": v(-1195, -193.94) * mm, "end": v(-1195, -181.44) * mm});
            skLineSegment(sketch, "E564", {"start": v(-1195, -181.44) * mm, "end": v(-1189, -181.44) * mm});
            skLineSegment(sketch, "E565", {"start": v(-1189, -181.44) * mm, "end": v(-1189, -168.94) * mm});
            skLineSegment(sketch, "E566", {"start": v(-1189, -168.94) * mm, "end": v(-1195, -168.94) * mm});
            skLineSegment(sketch, "E567", {"start": v(-1195, -168.94) * mm, "end": v(-1195, -158.94) * mm});
            skLineSegment(sketch, "E568", {"start": v(-1195, -158.94) * mm, "end": v(-1189, -158.94) * mm});
            skLineSegment(sketch, "E569", {"start": v(-1189, -158.94) * mm, "end": v(-1189, -148.94) * mm});
            skLineSegment(sketch, "E570", {"start": v(-1189, -148.94) * mm, "end": v(-1195, -148.94) * mm});
            skLineSegment(sketch, "E571", {"start": v(-1195, -148.94) * mm, "end": v(-1195, -138.94) * mm});
            skLineSegment(sketch, "E572", {"start": v(-1195, -138.94) * mm, "end": v(-1189, -138.94) * mm});
            skLineSegment(sketch, "E573", {"start": v(-1189, -138.94) * mm, "end": v(-1189, -128.94) * mm});
            skLineSegment(sketch, "E574", {"start": v(-1189, -128.94) * mm, "end": v(-1195, -128.94) * mm});
            skLineSegment(sketch, "E575", {"start": v(-1195, -128.94) * mm, "end": v(-1195, -118.94) * mm});
            skLineSegment(sketch, "E576", {"start": v(-1195, -118.94) * mm, "end": v(-1189, -118.94) * mm});
            skLineSegment(sketch, "E577", {"start": v(-1189, -118.94) * mm, "end": v(-1189, -108.94) * mm});
            skLineSegment(sketch, "E578", {"start": v(-1189, -108.94) * mm, "end": v(-1195, -108.94) * mm});
            skLineSegment(sketch, "E579", {"start": v(-1195, -108.94) * mm, "end": v(-1195, -98.94) * mm});
            skLineSegment(sketch, "E580", {"start": v(-1195, -98.94) * mm, "end": v(-1189, -98.94) * mm});
            skLineSegment(sketch, "E581", {"start": v(-1189, -98.94) * mm, "end": v(-1189, -88.94) * mm});
            skLineSegment(sketch, "E582", {"start": v(-1189, -88.94) * mm, "end": v(-1195, -88.94) * mm});
            skLineSegment(sketch, "E583", {"start": v(-1195, -88.94) * mm, "end": v(-1195, -78.94) * mm});
            skLineSegment(sketch, "E584", {"start": v(-1195, -78.94) * mm, "end": v(-1189, -78.94) * mm});
            skLineSegment(sketch, "E585", {"start": v(-1189, -78.94) * mm, "end": v(-1189, -68.94) * mm});
            skLineSegment(sketch, "E586", {"start": v(-1189, -68.94) * mm, "end": v(-1195, -68.94) * mm});
            skLineSegment(sketch, "E587", {"start": v(-1195, -68.94) * mm, "end": v(-1195, -58.94) * mm});
            skLineSegment(sketch, "E588", {"start": v(-1195, -58.94) * mm, "end": v(-1189, -58.94) * mm});
            skLineSegment(sketch, "E589", {"start": v(-1189, -58.94) * mm, "end": v(-1189, -48.94) * mm});
            skLineSegment(sketch, "E590", {"start": v(-1189, -48.94) * mm, "end": v(-1195, -48.94) * mm});
            skLineSegment(sketch, "E591", {"start": v(-1195, -48.94) * mm, "end": v(-1195, -38.94) * mm});
            skLineSegment(sketch, "E592", {"start": v(-1195, -38.94) * mm, "end": v(-1189, -38.94) * mm});
            skLineSegment(sketch, "E593", {"start": v(-1189, -38.94) * mm, "end": v(-1189, -28.94) * mm});
            skLineSegment(sketch, "E594", {"start": v(-1189, -28.94) * mm, "end": v(-1195, -28.94) * mm});
            skLineSegment(sketch, "E595", {"start": v(-1195, -28.94) * mm, "end": v(-1195, -18.94) * mm});
            skLineSegment(sketch, "E596", {"start": v(-1195, -18.94) * mm, "end": v(-1189, -18.94) * mm});
            skLineSegment(sketch, "E597", {"start": v(-1189, -18.94) * mm, "end": v(-1189, -8.94) * mm});
            skLineSegment(sketch, "E598", {"start": v(-1189, -8.94) * mm, "end": v(-1195, -8.94) * mm});
            skLineSegment(sketch, "E599", {"start": v(-1195, -8.94) * mm, "end": v(-1195, 1.06) * mm});
            skLineSegment(sketch, "E600", {"start": v(-1195, 1.06) * mm, "end": v(-1189, 1.06) * mm});
            skLineSegment(sketch, "E601", {"start": v(-1189, 1.06) * mm, "end": v(-1189, 11.06) * mm});
            skLineSegment(sketch, "E602", {"start": v(-1189, 11.06) * mm, "end": v(-1195, 11.06) * mm});
            skLineSegment(sketch, "E603", {"start": v(-1195, 11.06) * mm, "end": v(-1195, 21.06) * mm});
            skLineSegment(sketch, "E604", {"start": v(-1195, 21.06) * mm, "end": v(-1189, 21.06) * mm});
            skLineSegment(sketch, "E605", {"start": v(-1189, 21.06) * mm, "end": v(-1189, 31.06) * mm});
            skLineSegment(sketch, "E606", {"start": v(-1189, 31.06) * mm, "end": v(-1195, 31.06) * mm});
            skLineSegment(sketch, "E607", {"start": v(-1195, 31.06) * mm, "end": v(-1195, 41.06) * mm});
            skLineSegment(sketch, "E608", {"start": v(-1195, 41.06) * mm, "end": v(-1189, 41.06) * mm});
            skLineSegment(sketch, "E609", {"start": v(-1189, 41.06) * mm, "end": v(-1189, 51.06) * mm});
            skLineSegment(sketch, "E610", {"start": v(-1189, 51.06) * mm, "end": v(-1195, 51.06) * mm});
            skLineSegment(sketch, "E611", {"start": v(-1195, 51.06) * mm, "end": v(-1195, 61.06) * mm});
            skLineSegment(sketch, "E612", {"start": v(-1195, 61.06) * mm, "end": v(-1189, 61.06) * mm});
            skLineSegment(sketch, "E613", {"start": v(-1189, 61.06) * mm, "end": v(-1189, 71.06) * mm});
            skLineSegment(sketch, "E614", {"start": v(-1189, 71.06) * mm, "end": v(-1195, 71.06) * mm});
            skLineSegment(sketch, "E615", {"start": v(-1195, 71.06) * mm, "end": v(-1195, 81.06) * mm});
            skLineSegment(sketch, "E616", {"start": v(-1195, 81.06) * mm, "end": v(-1189, 81.06) * mm});
            skLineSegment(sketch, "E617", {"start": v(-1189, 81.06) * mm, "end": v(-1189, 91.06) * mm});
            skLineSegment(sketch, "E618", {"start": v(-1189, 91.06) * mm, "end": v(-1195, 91.06) * mm});
            skLineSegment(sketch, "E619", {"start": v(-1195, 91.06) * mm, "end": v(-1195, 101.06) * mm});
            skLineSegment(sketch, "E620", {"start": v(-1195, 101.06) * mm, "end": v(-1189, 101.06) * mm});
            skLineSegment(sketch, "E621", {"start": v(-1189, 101.06) * mm, "end": v(-1189, 111.06) * mm});
            skLineSegment(sketch, "E622", {"start": v(-1189, 111.06) * mm, "end": v(-1195, 111.06) * mm});
            skLineSegment(sketch, "E623", {"start": v(-1195, 111.06) * mm, "end": v(-1195, 121.06) * mm});
            skLineSegment(sketch, "E624", {"start": v(-1195, 121.06) * mm, "end": v(-1189, 121.06) * mm});
            skLineSegment(sketch, "E625", {"start": v(-1189, 121.06) * mm, "end": v(-1189, 131.06) * mm});
            skLineSegment(sketch, "E626", {"start": v(-1189, 131.06) * mm, "end": v(-1195, 131.06) * mm});
            skLineSegment(sketch, "E627", {"start": v(-1195, 131.06) * mm, "end": v(-1195, 141.06) * mm});
            skLineSegment(sketch, "E628", {"start": v(-1195, 141.06) * mm, "end": v(-1189, 141.06) * mm});
            skLineSegment(sketch, "E629", {"start": v(-1189, 141.06) * mm, "end": v(-1189, 151.06) * mm});
            skLineSegment(sketch, "E630", {"start": v(-1189, 151.06) * mm, "end": v(-1195, 151.06) * mm});
            skLineSegment(sketch, "E631", {"start": v(-1195, 151.06) * mm, "end": v(-1195, 161.06) * mm});
            skLineSegment(sketch, "E632", {"start": v(-1195, 161.06) * mm, "end": v(-1189, 161.06) * mm});
            skLineSegment(sketch, "E633", {"start": v(-1189, 161.06) * mm, "end": v(-1189, 171.06) * mm});
            skLineSegment(sketch, "E634", {"start": v(-1189, 171.06) * mm, "end": v(-1195, 171.06) * mm});
            skLineSegment(sketch, "E635", {"start": v(-1195, 171.06) * mm, "end": v(-1195, 181.06) * mm});
            skLineSegment(sketch, "E636", {"start": v(-1195, 181.06) * mm, "end": v(-1189, 181.06) * mm});
            skLineSegment(sketch, "E637", {"start": v(-1189, 181.06) * mm, "end": v(-1189, 191.06) * mm});
            skLineSegment(sketch, "E638", {"start": v(-1189, 191.06) * mm, "end": v(-1195, 191.06) * mm});
            skLineSegment(sketch, "E639", {"start": v(-1195, 191.06) * mm, "end": v(-1195, 201.06) * mm});
            skLineSegment(sketch, "E640", {"start": v(-1195, 201.06) * mm, "end": v(-1189, 201.06) * mm});
            skLineSegment(sketch, "E641", {"start": v(-1189, 201.06) * mm, "end": v(-1189, 211.06) * mm});
            skLineSegment(sketch, "E642", {"start": v(-1189, 211.06) * mm, "end": v(-1195, 211.06) * mm});
            skLineSegment(sketch, "E643", {"start": v(-1195, 211.06) * mm, "end": v(-1195, 221.06) * mm});
            skLineSegment(sketch, "E644", {"start": v(-1195, 221.06) * mm, "end": v(-1189, 221.06) * mm});
            skLineSegment(sketch, "E645", {"start": v(-1189, 221.06) * mm, "end": v(-1189, 231.06) * mm});
            skLineSegment(sketch, "E646", {"start": v(-1189, 231.06) * mm, "end": v(-1195, 231.06) * mm});
            skLineSegment(sketch, "E647", {"start": v(-1195, 231.06) * mm, "end": v(-1195, 241.06) * mm});
            skLineSegment(sketch, "E648", {"start": v(-1195, 241.06) * mm, "end": v(-1189, 241.06) * mm});
            skLineSegment(sketch, "E649", {"start": v(-1189, 241.06) * mm, "end": v(-1189, 251.06) * mm});
            skLineSegment(sketch, "E650", {"start": v(-1189, 251.06) * mm, "end": v(-1195, 251.06) * mm});
            skLineSegment(sketch, "E651", {"start": v(-1195, 251.06) * mm, "end": v(-1195, 261.06) * mm});
            skLineSegment(sketch, "E652", {"start": v(-1195, 261.06) * mm, "end": v(-1189, 261.06) * mm});
            skLineSegment(sketch, "E653", {"start": v(-1189, 261.06) * mm, "end": v(-1189, 271.06) * mm});
            skLineSegment(sketch, "E654", {"start": v(-1189, 271.06) * mm, "end": v(-1195, 271.06) * mm});
            skLineSegment(sketch, "E655", {"start": v(-1195, 271.06) * mm, "end": v(-1195, 281.06) * mm});
            skLineSegment(sketch, "E656", {"start": v(-1195, 281.06) * mm, "end": v(-1189, 281.06) * mm});
            skLineSegment(sketch, "E657", {"start": v(-1189, 281.06) * mm, "end": v(-1189, 293.56) * mm});
            skLineSegment(sketch, "E658", {"start": v(-1189, 293.56) * mm, "end": v(-1195, 293.56) * mm});
            skLineSegment(sketch, "E659", {"start": v(-1195, 293.56) * mm, "end": v(-1195, 306.06) * mm});
            skLineSegment(sketch, "E660", {"start": v(0, 306.06) * mm, "end": v(16.25, 306.06) * mm});
            skLineSegment(sketch, "E661", {"start": v(16.25, 306.06) * mm, "end": v(16.25, 300.06) * mm});
            skLineSegment(sketch, "E662", {"start": v(16.25, 300.06) * mm, "end": v(32.5, 300.06) * mm});
            skLineSegment(sketch, "E663", {"start": v(32.5, 300.06) * mm, "end": v(32.5, 306.06) * mm});
            skLineSegment(sketch, "E664", {"start": v(32.5, 306.06) * mm, "end": v(42.5, 306.06) * mm});
            skLineSegment(sketch, "E665", {"start": v(42.5, 306.06) * mm, "end": v(42.5, 300.06) * mm});
            skLineSegment(sketch, "E666", {"start": v(42.5, 300.06) * mm, "end": v(52.5, 300.06) * mm});
            skLineSegment(sketch, "E667", {"start": v(52.5, 300.06) * mm, "end": v(52.5, 306.06) * mm});
            skLineSegment(sketch, "E668", {"start": v(52.5, 306.06) * mm, "end": v(62.5, 306.06) * mm});
            skLineSegment(sketch, "E669", {"start": v(62.5, 306.06) * mm, "end": v(62.5, 300.06) * mm});
            skLineSegment(sketch, "E670", {"start": v(62.5, 300.06) * mm, "end": v(72.5, 300.06) * mm});
            skLineSegment(sketch, "E671", {"start": v(72.5, 300.06) * mm, "end": v(72.5, 306.06) * mm});
            skLineSegment(sketch, "E672", {"start": v(72.5, 306.06) * mm, "end": v(82.5, 306.06) * mm});
            skLineSegment(sketch, "E673", {"start": v(82.5, 306.06) * mm, "end": v(82.5, 300.06) * mm});
            skLineSegment(sketch, "E674", {"start": v(82.5, 300.06) * mm, "end": v(92.5, 300.06) * mm});
            skLineSegment(sketch, "E675", {"start": v(92.5, 300.06) * mm, "end": v(92.5, 306.06) * mm});
            skLineSegment(sketch, "E676", {"start": v(92.5, 306.06) * mm, "end": v(102.5, 306.06) * mm});
            skLineSegment(sketch, "E677", {"start": v(102.5, 306.06) * mm, "end": v(102.5, 300.06) * mm});
            skLineSegment(sketch, "E678", {"start": v(102.5, 300.06) * mm, "end": v(112.5, 300.06) * mm});
            skLineSegment(sketch, "E679", {"start": v(112.5, 300.06) * mm, "end": v(112.5, 306.06) * mm});
            skLineSegment(sketch, "E680", {"start": v(112.5, 306.06) * mm, "end": v(122.5, 306.06) * mm});
            skLineSegment(sketch, "E681", {"start": v(122.5, 306.06) * mm, "end": v(122.5, 300.06) * mm});
            skLineSegment(sketch, "E682", {"start": v(122.5, 300.06) * mm, "end": v(132.5, 300.06) * mm});
            skLineSegment(sketch, "E683", {"start": v(132.5, 300.06) * mm, "end": v(132.5, 306.06) * mm});
            skLineSegment(sketch, "E684", {"start": v(132.5, 306.06) * mm, "end": v(142.5, 306.06) * mm});
            skLineSegment(sketch, "E685", {"start": v(142.5, 306.06) * mm, "end": v(142.5, 300.06) * mm});
            skLineSegment(sketch, "E686", {"start": v(142.5, 300.06) * mm, "end": v(152.5, 300.06) * mm});
            skLineSegment(sketch, "E687", {"start": v(152.5, 300.06) * mm, "end": v(152.5, 306.06) * mm});
            skLineSegment(sketch, "E688", {"start": v(152.5, 306.06) * mm, "end": v(162.5, 306.06) * mm});
            skLineSegment(sketch, "E689", {"start": v(162.5, 306.06) * mm, "end": v(162.5, 300.06) * mm});
            skLineSegment(sketch, "E690", {"start": v(162.5, 300.06) * mm, "end": v(172.5, 300.06) * mm});
            skLineSegment(sketch, "E691", {"start": v(172.5, 300.06) * mm, "end": v(172.5, 306.06) * mm});
            skLineSegment(sketch, "E692", {"start": v(172.5, 306.06) * mm, "end": v(182.5, 306.06) * mm});
            skLineSegment(sketch, "E693", {"start": v(182.5, 306.06) * mm, "end": v(182.5, 300.06) * mm});
            skLineSegment(sketch, "E694", {"start": v(182.5, 300.06) * mm, "end": v(192.5, 300.06) * mm});
            skLineSegment(sketch, "E695", {"start": v(192.5, 300.06) * mm, "end": v(192.5, 306.06) * mm});
            skLineSegment(sketch, "E696", {"start": v(192.5, 306.06) * mm, "end": v(202.5, 306.06) * mm});
            skLineSegment(sketch, "E697", {"start": v(202.5, 306.06) * mm, "end": v(202.5, 300.06) * mm});
            skLineSegment(sketch, "E698", {"start": v(202.5, 300.06) * mm, "end": v(212.5, 300.06) * mm});
            skLineSegment(sketch, "E699", {"start": v(212.5, 300.06) * mm, "end": v(212.5, 306.06) * mm});
            skLineSegment(sketch, "E700", {"start": v(212.5, 306.06) * mm, "end": v(222.5, 306.06) * mm});
            skLineSegment(sketch, "E701", {"start": v(222.5, 306.06) * mm, "end": v(222.5, 300.06) * mm});
            skLineSegment(sketch, "E702", {"start": v(222.5, 300.06) * mm, "end": v(232.5, 300.06) * mm});
            skLineSegment(sketch, "E703", {"start": v(232.5, 300.06) * mm, "end": v(232.5, 306.06) * mm});
            skLineSegment(sketch, "E704", {"start": v(232.5, 306.06) * mm, "end": v(242.5, 306.06) * mm});
            skLineSegment(sketch, "E705", {"start": v(242.5, 306.06) * mm, "end": v(242.5, 300.06) * mm});
            skLineSegment(sketch, "E706", {"start": v(242.5, 300.06) * mm, "end": v(252.5, 300.06) * mm});
            skLineSegment(sketch, "E707", {"start": v(252.5, 300.06) * mm, "end": v(252.5, 306.06) * mm});
            skLineSegment(sketch, "E708", {"start": v(252.5, 306.06) * mm, "end": v(262.5, 306.06) * mm});
            skLineSegment(sketch, "E709", {"start": v(262.5, 306.06) * mm, "end": v(262.5, 300.06) * mm});
            skLineSegment(sketch, "E710", {"start": v(262.5, 300.06) * mm, "end": v(272.5, 300.06) * mm});
            skLineSegment(sketch, "E711", {"start": v(272.5, 300.06) * mm, "end": v(272.5, 306.06) * mm});
            skLineSegment(sketch, "E712", {"start": v(272.5, 306.06) * mm, "end": v(282.5, 306.06) * mm});
            skLineSegment(sketch, "E713", {"start": v(282.5, 306.06) * mm, "end": v(282.5, 300.06) * mm});
            skLineSegment(sketch, "E714", {"start": v(282.5, 300.06) * mm, "end": v(292.5, 300.06) * mm});
            skLineSegment(sketch, "E715", {"start": v(292.5, 300.06) * mm, "end": v(292.5, 306.06) * mm});
            skLineSegment(sketch, "E716", {"start": v(292.5, 306.06) * mm, "end": v(302.5, 306.06) * mm});
            skLineSegment(sketch, "E717", {"start": v(302.5, 306.06) * mm, "end": v(302.5, 300.06) * mm});
            skLineSegment(sketch, "E718", {"start": v(302.5, 300.06) * mm, "end": v(312.5, 300.06) * mm});
            skLineSegment(sketch, "E719", {"start": v(312.5, 300.06) * mm, "end": v(312.5, 306.06) * mm});
            skLineSegment(sketch, "E720", {"start": v(312.5, 306.06) * mm, "end": v(322.5, 306.06) * mm});
            skLineSegment(sketch, "E721", {"start": v(322.5, 306.06) * mm, "end": v(322.5, 300.06) * mm});
            skLineSegment(sketch, "E722", {"start": v(322.5, 300.06) * mm, "end": v(332.5, 300.06) * mm});
            skLineSegment(sketch, "E723", {"start": v(332.5, 300.06) * mm, "end": v(332.5, 306.06) * mm});
            skLineSegment(sketch, "E724", {"start": v(332.5, 306.06) * mm, "end": v(342.5, 306.06) * mm});
            skLineSegment(sketch, "E725", {"start": v(342.5, 306.06) * mm, "end": v(342.5, 300.06) * mm});
            skLineSegment(sketch, "E726", {"start": v(342.5, 300.06) * mm, "end": v(352.5, 300.06) * mm});
            skLineSegment(sketch, "E727", {"start": v(352.5, 300.06) * mm, "end": v(352.5, 306.06) * mm});
            skLineSegment(sketch, "E728", {"start": v(352.5, 306.06) * mm, "end": v(362.5, 306.06) * mm});
            skLineSegment(sketch, "E729", {"start": v(362.5, 306.06) * mm, "end": v(362.5, 300.06) * mm});
            skLineSegment(sketch, "E730", {"start": v(362.5, 300.06) * mm, "end": v(372.5, 300.06) * mm});
            skLineSegment(sketch, "E731", {"start": v(372.5, 300.06) * mm, "end": v(372.5, 306.06) * mm});
            skLineSegment(sketch, "E732", {"start": v(372.5, 306.06) * mm, "end": v(382.5, 306.06) * mm});
            skLineSegment(sketch, "E733", {"start": v(382.5, 306.06) * mm, "end": v(382.5, 300.06) * mm});
            skLineSegment(sketch, "E734", {"start": v(382.5, 300.06) * mm, "end": v(392.5, 300.06) * mm});
            skLineSegment(sketch, "E735", {"start": v(392.5, 300.06) * mm, "end": v(392.5, 306.06) * mm});
            skLineSegment(sketch, "E736", {"start": v(392.5, 306.06) * mm, "end": v(402.5, 306.06) * mm});
            skLineSegment(sketch, "E737", {"start": v(402.5, 306.06) * mm, "end": v(402.5, 300.06) * mm});
            skLineSegment(sketch, "E738", {"start": v(402.5, 300.06) * mm, "end": v(412.5, 300.06) * mm});
            skLineSegment(sketch, "E739", {"start": v(412.5, 300.06) * mm, "end": v(412.5, 306.06) * mm});
            skLineSegment(sketch, "E740", {"start": v(412.5, 306.06) * mm, "end": v(422.5, 306.06) * mm});
            skLineSegment(sketch, "E741", {"start": v(422.5, 306.06) * mm, "end": v(422.5, 300.06) * mm});
            skLineSegment(sketch, "E742", {"start": v(422.5, 300.06) * mm, "end": v(432.5, 300.06) * mm});
            skLineSegment(sketch, "E743", {"start": v(432.5, 300.06) * mm, "end": v(432.5, 306.06) * mm});
            skLineSegment(sketch, "E744", {"start": v(432.5, 306.06) * mm, "end": v(442.5, 306.06) * mm});
            skLineSegment(sketch, "E745", {"start": v(442.5, 306.06) * mm, "end": v(442.5, 300.06) * mm});
            skLineSegment(sketch, "E746", {"start": v(442.5, 300.06) * mm, "end": v(452.5, 300.06) * mm});
            skLineSegment(sketch, "E747", {"start": v(452.5, 300.06) * mm, "end": v(452.5, 306.06) * mm});
            skLineSegment(sketch, "E748", {"start": v(452.5, 306.06) * mm, "end": v(462.5, 306.06) * mm});
            skLineSegment(sketch, "E749", {"start": v(462.5, 306.06) * mm, "end": v(462.5, 300.06) * mm});
            skLineSegment(sketch, "E750", {"start": v(462.5, 300.06) * mm, "end": v(472.5, 300.06) * mm});
            skLineSegment(sketch, "E751", {"start": v(472.5, 300.06) * mm, "end": v(472.5, 306.06) * mm});
            skLineSegment(sketch, "E752", {"start": v(472.5, 306.06) * mm, "end": v(482.5, 306.06) * mm});
            skLineSegment(sketch, "E753", {"start": v(482.5, 306.06) * mm, "end": v(482.5, 300.06) * mm});
            skLineSegment(sketch, "E754", {"start": v(482.5, 300.06) * mm, "end": v(492.5, 300.06) * mm});
            skLineSegment(sketch, "E755", {"start": v(492.5, 300.06) * mm, "end": v(492.5, 306.06) * mm});
            skLineSegment(sketch, "E756", {"start": v(492.5, 306.06) * mm, "end": v(502.5, 306.06) * mm});
            skLineSegment(sketch, "E757", {"start": v(502.5, 306.06) * mm, "end": v(502.5, 300.06) * mm});
            skLineSegment(sketch, "E758", {"start": v(502.5, 300.06) * mm, "end": v(512.5, 300.06) * mm});
            skLineSegment(sketch, "E759", {"start": v(512.5, 300.06) * mm, "end": v(512.5, 306.06) * mm});
            skLineSegment(sketch, "E760", {"start": v(512.5, 306.06) * mm, "end": v(522.5, 306.06) * mm});
            skLineSegment(sketch, "E761", {"start": v(522.5, 306.06) * mm, "end": v(522.5, 300.06) * mm});
            skLineSegment(sketch, "E762", {"start": v(522.5, 300.06) * mm, "end": v(532.5, 300.06) * mm});
            skLineSegment(sketch, "E763", {"start": v(532.5, 300.06) * mm, "end": v(532.5, 306.06) * mm});
            skLineSegment(sketch, "E764", {"start": v(532.5, 306.06) * mm, "end": v(542.5, 306.06) * mm});
            skLineSegment(sketch, "E765", {"start": v(542.5, 306.06) * mm, "end": v(542.5, 300.06) * mm});
            skLineSegment(sketch, "E766", {"start": v(542.5, 300.06) * mm, "end": v(552.5, 300.06) * mm});
            skLineSegment(sketch, "E767", {"start": v(552.5, 300.06) * mm, "end": v(552.5, 306.06) * mm});
            skLineSegment(sketch, "E768", {"start": v(552.5, 306.06) * mm, "end": v(562.5, 306.06) * mm});
            skLineSegment(sketch, "E769", {"start": v(562.5, 306.06) * mm, "end": v(562.5, 300.06) * mm});
            skLineSegment(sketch, "E770", {"start": v(562.5, 300.06) * mm, "end": v(572.5, 300.06) * mm});
            skLineSegment(sketch, "E771", {"start": v(572.5, 300.06) * mm, "end": v(572.5, 306.06) * mm});
            skLineSegment(sketch, "E772", {"start": v(572.5, 306.06) * mm, "end": v(582.5, 306.06) * mm});
            skLineSegment(sketch, "E773", {"start": v(582.5, 306.06) * mm, "end": v(582.5, 300.06) * mm});
            skLineSegment(sketch, "E774", {"start": v(582.5, 300.06) * mm, "end": v(592.5, 300.06) * mm});
            skLineSegment(sketch, "E775", {"start": v(592.5, 300.06) * mm, "end": v(592.5, 306.06) * mm});
            skLineSegment(sketch, "E776", {"start": v(592.5, 306.06) * mm, "end": v(602.5, 306.06) * mm});
            skLineSegment(sketch, "E777", {"start": v(602.5, 306.06) * mm, "end": v(602.5, 300.06) * mm});
            skLineSegment(sketch, "E778", {"start": v(602.5, 300.06) * mm, "end": v(612.5, 300.06) * mm});
            skLineSegment(sketch, "E779", {"start": v(612.5, 300.06) * mm, "end": v(612.5, 306.06) * mm});
            skLineSegment(sketch, "E780", {"start": v(612.5, 306.06) * mm, "end": v(622.5, 306.06) * mm});
            skLineSegment(sketch, "E781", {"start": v(622.5, 306.06) * mm, "end": v(622.5, 300.06) * mm});
            skLineSegment(sketch, "E782", {"start": v(622.5, 300.06) * mm, "end": v(632.5, 300.06) * mm});
            skLineSegment(sketch, "E783", {"start": v(632.5, 300.06) * mm, "end": v(632.5, 306.06) * mm});
            skLineSegment(sketch, "E784", {"start": v(632.5, 306.06) * mm, "end": v(642.5, 306.06) * mm});
            skLineSegment(sketch, "E785", {"start": v(642.5, 306.06) * mm, "end": v(642.5, 300.06) * mm});
            skLineSegment(sketch, "E786", {"start": v(642.5, 300.06) * mm, "end": v(652.5, 300.06) * mm});
            skLineSegment(sketch, "E787", {"start": v(652.5, 300.06) * mm, "end": v(652.5, 306.06) * mm});
            skLineSegment(sketch, "E788", {"start": v(652.5, 306.06) * mm, "end": v(662.5, 306.06) * mm});
            skLineSegment(sketch, "E789", {"start": v(662.5, 306.06) * mm, "end": v(662.5, 300.06) * mm});
            skLineSegment(sketch, "E790", {"start": v(662.5, 300.06) * mm, "end": v(672.5, 300.06) * mm});
            skLineSegment(sketch, "E791", {"start": v(672.5, 300.06) * mm, "end": v(672.5, 306.06) * mm});
            skLineSegment(sketch, "E792", {"start": v(672.5, 306.06) * mm, "end": v(682.5, 306.06) * mm});
            skLineSegment(sketch, "E793", {"start": v(682.5, 306.06) * mm, "end": v(682.5, 300.06) * mm});
            skLineSegment(sketch, "E794", {"start": v(682.5, 300.06) * mm, "end": v(692.5, 300.06) * mm});
            skLineSegment(sketch, "E795", {"start": v(692.5, 300.06) * mm, "end": v(692.5, 306.06) * mm});
            skLineSegment(sketch, "E796", {"start": v(692.5, 306.06) * mm, "end": v(702.5, 306.06) * mm});
            skLineSegment(sketch, "E797", {"start": v(702.5, 306.06) * mm, "end": v(702.5, 300.06) * mm});
            skLineSegment(sketch, "E798", {"start": v(702.5, 300.06) * mm, "end": v(712.5, 300.06) * mm});
            skLineSegment(sketch, "E799", {"start": v(712.5, 300.06) * mm, "end": v(712.5, 306.06) * mm});
            skLineSegment(sketch, "E800", {"start": v(712.5, 306.06) * mm, "end": v(722.5, 306.06) * mm});
            skLineSegment(sketch, "E801", {"start": v(722.5, 306.06) * mm, "end": v(722.5, 300.06) * mm});
            skLineSegment(sketch, "E802", {"start": v(722.5, 300.06) * mm, "end": v(732.5, 300.06) * mm});
            skLineSegment(sketch, "E803", {"start": v(732.5, 300.06) * mm, "end": v(732.5, 306.06) * mm});
            skLineSegment(sketch, "E804", {"start": v(732.5, 306.06) * mm, "end": v(742.5, 306.06) * mm});
            skLineSegment(sketch, "E805", {"start": v(742.5, 306.06) * mm, "end": v(742.5, 300.06) * mm});
            skLineSegment(sketch, "E806", {"start": v(742.5, 300.06) * mm, "end": v(752.5, 300.06) * mm});
            skLineSegment(sketch, "E807", {"start": v(752.5, 300.06) * mm, "end": v(752.5, 306.06) * mm});
            skLineSegment(sketch, "E808", {"start": v(752.5, 306.06) * mm, "end": v(762.5, 306.06) * mm});
            skLineSegment(sketch, "E809", {"start": v(762.5, 306.06) * mm, "end": v(762.5, 300.06) * mm});
            skLineSegment(sketch, "E810", {"start": v(762.5, 300.06) * mm, "end": v(772.5, 300.06) * mm});
            skLineSegment(sketch, "E811", {"start": v(772.5, 300.06) * mm, "end": v(772.5, 306.06) * mm});
            skLineSegment(sketch, "E812", {"start": v(772.5, 306.06) * mm, "end": v(782.5, 306.06) * mm});
            skLineSegment(sketch, "E813", {"start": v(782.5, 306.06) * mm, "end": v(782.5, 300.06) * mm});
            skLineSegment(sketch, "E814", {"start": v(782.5, 300.06) * mm, "end": v(792.5, 300.06) * mm});
            skLineSegment(sketch, "E815", {"start": v(792.5, 300.06) * mm, "end": v(792.5, 306.06) * mm});
            skLineSegment(sketch, "E816", {"start": v(792.5, 306.06) * mm, "end": v(802.5, 306.06) * mm});
            skLineSegment(sketch, "E817", {"start": v(802.5, 306.06) * mm, "end": v(802.5, 300.06) * mm});
            skLineSegment(sketch, "E818", {"start": v(802.5, 300.06) * mm, "end": v(812.5, 300.06) * mm});
            skLineSegment(sketch, "E819", {"start": v(812.5, 300.06) * mm, "end": v(812.5, 306.06) * mm});
            skLineSegment(sketch, "E820", {"start": v(812.5, 306.06) * mm, "end": v(822.5, 306.06) * mm});
            skLineSegment(sketch, "E821", {"start": v(822.5, 306.06) * mm, "end": v(822.5, 300.06) * mm});
            skLineSegment(sketch, "E822", {"start": v(822.5, 300.06) * mm, "end": v(832.5, 300.06) * mm});
            skLineSegment(sketch, "E823", {"start": v(832.5, 300.06) * mm, "end": v(832.5, 306.06) * mm});
            skLineSegment(sketch, "E824", {"start": v(832.5, 306.06) * mm, "end": v(842.5, 306.06) * mm});
            skLineSegment(sketch, "E825", {"start": v(842.5, 306.06) * mm, "end": v(842.5, 300.06) * mm});
            skLineSegment(sketch, "E826", {"start": v(842.5, 300.06) * mm, "end": v(852.5, 300.06) * mm});
            skLineSegment(sketch, "E827", {"start": v(852.5, 300.06) * mm, "end": v(852.5, 306.06) * mm});
            skLineSegment(sketch, "E828", {"start": v(852.5, 306.06) * mm, "end": v(862.5, 306.06) * mm});
            skLineSegment(sketch, "E829", {"start": v(862.5, 306.06) * mm, "end": v(862.5, 300.06) * mm});
            skLineSegment(sketch, "E830", {"start": v(862.5, 300.06) * mm, "end": v(872.5, 300.06) * mm});
            skLineSegment(sketch, "E831", {"start": v(872.5, 300.06) * mm, "end": v(872.5, 306.06) * mm});
            skLineSegment(sketch, "E832", {"start": v(872.5, 306.06) * mm, "end": v(882.5, 306.06) * mm});
            skLineSegment(sketch, "E833", {"start": v(882.5, 306.06) * mm, "end": v(882.5, 300.06) * mm});
            skLineSegment(sketch, "E834", {"start": v(882.5, 300.06) * mm, "end": v(892.5, 300.06) * mm});
            skLineSegment(sketch, "E835", {"start": v(892.5, 300.06) * mm, "end": v(892.5, 306.06) * mm});
            skLineSegment(sketch, "E836", {"start": v(892.5, 306.06) * mm, "end": v(902.5, 306.06) * mm});
            skLineSegment(sketch, "E837", {"start": v(902.5, 306.06) * mm, "end": v(902.5, 300.06) * mm});
            skLineSegment(sketch, "E838", {"start": v(902.5, 300.06) * mm, "end": v(912.5, 300.06) * mm});
            skLineSegment(sketch, "E839", {"start": v(912.5, 300.06) * mm, "end": v(912.5, 306.06) * mm});
            skLineSegment(sketch, "E840", {"start": v(912.5, 306.06) * mm, "end": v(922.5, 306.06) * mm});
            skLineSegment(sketch, "E841", {"start": v(922.5, 306.06) * mm, "end": v(922.5, 300.06) * mm});
            skLineSegment(sketch, "E842", {"start": v(922.5, 300.06) * mm, "end": v(932.5, 300.06) * mm});
            skLineSegment(sketch, "E843", {"start": v(932.5, 300.06) * mm, "end": v(932.5, 306.06) * mm});
            skLineSegment(sketch, "E844", {"start": v(932.5, 306.06) * mm, "end": v(942.5, 306.06) * mm});
            skLineSegment(sketch, "E845", {"start": v(942.5, 306.06) * mm, "end": v(942.5, 300.06) * mm});
            skLineSegment(sketch, "E846", {"start": v(942.5, 300.06) * mm, "end": v(952.5, 300.06) * mm});
            skLineSegment(sketch, "E847", {"start": v(952.5, 300.06) * mm, "end": v(952.5, 306.06) * mm});
            skLineSegment(sketch, "E848", {"start": v(952.5, 306.06) * mm, "end": v(962.5, 306.06) * mm});
            skLineSegment(sketch, "E849", {"start": v(962.5, 306.06) * mm, "end": v(962.5, 300.06) * mm});
            skLineSegment(sketch, "E850", {"start": v(962.5, 300.06) * mm, "end": v(972.5, 300.06) * mm});
            skLineSegment(sketch, "E851", {"start": v(972.5, 300.06) * mm, "end": v(972.5, 306.06) * mm});
            skLineSegment(sketch, "E852", {"start": v(972.5, 306.06) * mm, "end": v(982.5, 306.06) * mm});
            skLineSegment(sketch, "E853", {"start": v(982.5, 306.06) * mm, "end": v(982.5, 300.06) * mm});
            skLineSegment(sketch, "E854", {"start": v(982.5, 300.06) * mm, "end": v(992.5, 300.06) * mm});
            skLineSegment(sketch, "E855", {"start": v(992.5, 300.06) * mm, "end": v(992.5, 306.06) * mm});
            skLineSegment(sketch, "E856", {"start": v(992.5, 306.06) * mm, "end": v(1002.5, 306.06) * mm});
            skLineSegment(sketch, "E857", {"start": v(1002.5, 306.06) * mm, "end": v(1002.5, 300.06) * mm});
            skLineSegment(sketch, "E858", {"start": v(1002.5, 300.06) * mm, "end": v(1012.5, 300.06) * mm});
            skLineSegment(sketch, "E859", {"start": v(1012.5, 300.06) * mm, "end": v(1012.5, 306.06) * mm});
            skLineSegment(sketch, "E860", {"start": v(1012.5, 306.06) * mm, "end": v(1022.5, 306.06) * mm});
            skLineSegment(sketch, "E861", {"start": v(1022.5, 306.06) * mm, "end": v(1022.5, 300.06) * mm});
            skLineSegment(sketch, "E862", {"start": v(1022.5, 300.06) * mm, "end": v(1032.5, 300.06) * mm});
            skLineSegment(sketch, "E863", {"start": v(1032.5, 300.06) * mm, "end": v(1032.5, 306.06) * mm});
            skLineSegment(sketch, "E864", {"start": v(1032.5, 306.06) * mm, "end": v(1042.5, 306.06) * mm});
            skLineSegment(sketch, "E865", {"start": v(1042.5, 306.06) * mm, "end": v(1042.5, 300.06) * mm});
            skLineSegment(sketch, "E866", {"start": v(1042.5, 300.06) * mm, "end": v(1052.5, 300.06) * mm});
            skLineSegment(sketch, "E867", {"start": v(1052.5, 300.06) * mm, "end": v(1052.5, 306.06) * mm});
            skLineSegment(sketch, "E868", {"start": v(1052.5, 306.06) * mm, "end": v(1062.5, 306.06) * mm});
            skLineSegment(sketch, "E869", {"start": v(1062.5, 306.06) * mm, "end": v(1062.5, 300.06) * mm});
            skLineSegment(sketch, "E870", {"start": v(1062.5, 300.06) * mm, "end": v(1072.5, 300.06) * mm});
            skLineSegment(sketch, "E871", {"start": v(1072.5, 300.06) * mm, "end": v(1072.5, 306.06) * mm});
            skLineSegment(sketch, "E872", {"start": v(1072.5, 306.06) * mm, "end": v(1082.5, 306.06) * mm});
            skLineSegment(sketch, "E873", {"start": v(1082.5, 306.06) * mm, "end": v(1082.5, 300.06) * mm});
            skLineSegment(sketch, "E874", {"start": v(1082.5, 300.06) * mm, "end": v(1092.5, 300.06) * mm});
            skLineSegment(sketch, "E875", {"start": v(1092.5, 300.06) * mm, "end": v(1092.5, 306.06) * mm});
            skLineSegment(sketch, "E876", {"start": v(1092.5, 306.06) * mm, "end": v(1102.5, 306.06) * mm});
            skLineSegment(sketch, "E877", {"start": v(1102.5, 306.06) * mm, "end": v(1102.5, 300.06) * mm});
            skLineSegment(sketch, "E878", {"start": v(1102.5, 300.06) * mm, "end": v(1112.5, 300.06) * mm});
            skLineSegment(sketch, "E879", {"start": v(1112.5, 300.06) * mm, "end": v(1112.5, 306.06) * mm});
            skLineSegment(sketch, "E880", {"start": v(1112.5, 306.06) * mm, "end": v(1122.5, 306.06) * mm});
            skLineSegment(sketch, "E881", {"start": v(1122.5, 306.06) * mm, "end": v(1122.5, 300.06) * mm});
            skLineSegment(sketch, "E882", {"start": v(1122.5, 300.06) * mm, "end": v(1132.5, 300.06) * mm});
            skLineSegment(sketch, "E883", {"start": v(1132.5, 300.06) * mm, "end": v(1132.5, 306.06) * mm});
            skLineSegment(sketch, "E884", {"start": v(1132.5, 306.06) * mm, "end": v(1142.5, 306.06) * mm});
            skLineSegment(sketch, "E885", {"start": v(1142.5, 306.06) * mm, "end": v(1142.5, 300.06) * mm});
            skLineSegment(sketch, "E886", {"start": v(1142.5, 300.06) * mm, "end": v(1152.5, 300.06) * mm});
            skLineSegment(sketch, "E887", {"start": v(1152.5, 300.06) * mm, "end": v(1152.5, 306.06) * mm});
            skLineSegment(sketch, "E888", {"start": v(1152.5, 306.06) * mm, "end": v(1162.5, 306.06) * mm});
            skLineSegment(sketch, "E889", {"start": v(1162.5, 306.06) * mm, "end": v(1162.5, 300.06) * mm});
            skLineSegment(sketch, "E890", {"start": v(1162.5, 300.06) * mm, "end": v(1178.75, 300.06) * mm});
            skLineSegment(sketch, "E891", {"start": v(1178.75, 300.06) * mm, "end": v(1178.75, 306.06) * mm});
            skLineSegment(sketch, "E892", {"start": v(1178.75, 306.06) * mm, "end": v(1195, 306.06) * mm});
            skLineSegment(sketch, "E893", {"start": v(1195, 306.06) * mm, "end": v(1195, 293.56) * mm});
            skLineSegment(sketch, "E894", {"start": v(1195, 293.56) * mm, "end": v(1189, 293.56) * mm});
            skLineSegment(sketch, "E895", {"start": v(1189, 293.56) * mm, "end": v(1189, 281.06) * mm});
            skLineSegment(sketch, "E896", {"start": v(1189, 281.06) * mm, "end": v(1195, 281.06) * mm});
            skLineSegment(sketch, "E897", {"start": v(1195, 281.06) * mm, "end": v(1195, 271.06) * mm});
            skLineSegment(sketch, "E898", {"start": v(1195, 271.06) * mm, "end": v(1189, 271.06) * mm});
            skLineSegment(sketch, "E899", {"start": v(1189, 271.06) * mm, "end": v(1189, 261.06) * mm});
            skLineSegment(sketch, "E900", {"start": v(1189, 261.06) * mm, "end": v(1195, 261.06) * mm});
            skLineSegment(sketch, "E901", {"start": v(1195, 261.06) * mm, "end": v(1195, 251.06) * mm});
            skLineSegment(sketch, "E902", {"start": v(1195, 251.06) * mm, "end": v(1189, 251.06) * mm});
            skLineSegment(sketch, "E903", {"start": v(1189, 251.06) * mm, "end": v(1189, 241.06) * mm});
            skLineSegment(sketch, "E904", {"start": v(1189, 241.06) * mm, "end": v(1195, 241.06) * mm});
            skLineSegment(sketch, "E905", {"start": v(1195, 241.06) * mm, "end": v(1195, 231.06) * mm});
            skLineSegment(sketch, "E906", {"start": v(1195, 231.06) * mm, "end": v(1189, 231.06) * mm});
            skLineSegment(sketch, "E907", {"start": v(1189, 231.06) * mm, "end": v(1189, 221.06) * mm});
            skLineSegment(sketch, "E908", {"start": v(1189, 221.06) * mm, "end": v(1195, 221.06) * mm});
            skLineSegment(sketch, "E909", {"start": v(1195, 221.06) * mm, "end": v(1195, 211.06) * mm});
            skLineSegment(sketch, "E910", {"start": v(1195, 211.06) * mm, "end": v(1189, 211.06) * mm});
            skLineSegment(sketch, "E911", {"start": v(1189, 211.06) * mm, "end": v(1189, 201.06) * mm});
            skLineSegment(sketch, "E912", {"start": v(1189, 201.06) * mm, "end": v(1195, 201.06) * mm});
            skLineSegment(sketch, "E913", {"start": v(1195, 201.06) * mm, "end": v(1195, 191.06) * mm});
            skLineSegment(sketch, "E914", {"start": v(1195, 191.06) * mm, "end": v(1189, 191.06) * mm});
            skLineSegment(sketch, "E915", {"start": v(1189, 191.06) * mm, "end": v(1189, 181.06) * mm});
            skLineSegment(sketch, "E916", {"start": v(1189, 181.06) * mm, "end": v(1195, 181.06) * mm});
            skLineSegment(sketch, "E917", {"start": v(1195, 181.06) * mm, "end": v(1195, 171.06) * mm});
            skLineSegment(sketch, "E918", {"start": v(1195, 171.06) * mm, "end": v(1189, 171.06) * mm});
            skLineSegment(sketch, "E919", {"start": v(1189, 171.06) * mm, "end": v(1189, 161.06) * mm});
            skLineSegment(sketch, "E920", {"start": v(1189, 161.06) * mm, "end": v(1195, 161.06) * mm});
            skLineSegment(sketch, "E921", {"start": v(1195, 161.06) * mm, "end": v(1195, 151.06) * mm});
            skLineSegment(sketch, "E922", {"start": v(1195, 151.06) * mm, "end": v(1189, 151.06) * mm});
            skLineSegment(sketch, "E923", {"start": v(1189, 151.06) * mm, "end": v(1189, 141.06) * mm});
            skLineSegment(sketch, "E924", {"start": v(1189, 141.06) * mm, "end": v(1195, 141.06) * mm});
            skLineSegment(sketch, "E925", {"start": v(1195, 141.06) * mm, "end": v(1195, 131.06) * mm});
            skLineSegment(sketch, "E926", {"start": v(1195, 131.06) * mm, "end": v(1189, 131.06) * mm});
            skLineSegment(sketch, "E927", {"start": v(1189, 131.06) * mm, "end": v(1189, 121.06) * mm});
            skLineSegment(sketch, "E928", {"start": v(1189, 121.06) * mm, "end": v(1195, 121.06) * mm});
            skLineSegment(sketch, "E929", {"start": v(1195, 121.06) * mm, "end": v(1195, 111.06) * mm});
            skLineSegment(sketch, "E930", {"start": v(1195, 111.06) * mm, "end": v(1189, 111.06) * mm});
            skLineSegment(sketch, "E931", {"start": v(1189, 111.06) * mm, "end": v(1189, 101.06) * mm});
            skLineSegment(sketch, "E932", {"start": v(1189, 101.06) * mm, "end": v(1195, 101.06) * mm});
            skLineSegment(sketch, "E933", {"start": v(1195, 101.06) * mm, "end": v(1195, 91.06) * mm});
            skLineSegment(sketch, "E934", {"start": v(1195, 91.06) * mm, "end": v(1189, 91.06) * mm});
            skLineSegment(sketch, "E935", {"start": v(1189, 91.06) * mm, "end": v(1189, 81.06) * mm});
            skLineSegment(sketch, "E936", {"start": v(1189, 81.06) * mm, "end": v(1195, 81.06) * mm});
            skLineSegment(sketch, "E937", {"start": v(1195, 81.06) * mm, "end": v(1195, 71.06) * mm});
            skLineSegment(sketch, "E938", {"start": v(1195, 71.06) * mm, "end": v(1189, 71.06) * mm});
            skLineSegment(sketch, "E939", {"start": v(1189, 71.06) * mm, "end": v(1189, 61.06) * mm});
            skLineSegment(sketch, "E940", {"start": v(1189, 61.06) * mm, "end": v(1195, 61.06) * mm});
            skLineSegment(sketch, "E941", {"start": v(1195, 61.06) * mm, "end": v(1195, 51.06) * mm});
            skLineSegment(sketch, "E942", {"start": v(1195, 51.06) * mm, "end": v(1189, 51.06) * mm});
            skLineSegment(sketch, "E943", {"start": v(1189, 51.06) * mm, "end": v(1189, 41.06) * mm});
            skLineSegment(sketch, "E944", {"start": v(1189, 41.06) * mm, "end": v(1195, 41.06) * mm});
            skLineSegment(sketch, "E945", {"start": v(1195, 41.06) * mm, "end": v(1195, 31.06) * mm});
            skLineSegment(sketch, "E946", {"start": v(1195, 31.06) * mm, "end": v(1189, 31.06) * mm});
            skLineSegment(sketch, "E947", {"start": v(1189, 31.06) * mm, "end": v(1189, 21.06) * mm});
            skLineSegment(sketch, "E948", {"start": v(1189, 21.06) * mm, "end": v(1195, 21.06) * mm});
            skLineSegment(sketch, "E949", {"start": v(1195, 21.06) * mm, "end": v(1195, 11.06) * mm});
            skLineSegment(sketch, "E950", {"start": v(1195, 11.06) * mm, "end": v(1189, 11.06) * mm});
            skLineSegment(sketch, "E951", {"start": v(1189, 11.06) * mm, "end": v(1189, 1.06) * mm});
            skLineSegment(sketch, "E952", {"start": v(1189, 1.06) * mm, "end": v(1195, 1.06) * mm});
            skLineSegment(sketch, "E953", {"start": v(1195, 1.06) * mm, "end": v(1195, -8.94) * mm});
            skLineSegment(sketch, "E954", {"start": v(1195, -8.94) * mm, "end": v(1189, -8.94) * mm});
            skLineSegment(sketch, "E955", {"start": v(1189, -8.94) * mm, "end": v(1189, -18.94) * mm});
            skLineSegment(sketch, "E956", {"start": v(1189, -18.94) * mm, "end": v(1195, -18.94) * mm});
            skLineSegment(sketch, "E957", {"start": v(1195, -18.94) * mm, "end": v(1195, -28.94) * mm});
            skLineSegment(sketch, "E958", {"start": v(1195, -28.94) * mm, "end": v(1189, -28.94) * mm});
            skLineSegment(sketch, "E959", {"start": v(1189, -28.94) * mm, "end": v(1189, -38.94) * mm});
            skLineSegment(sketch, "E960", {"start": v(1189, -38.94) * mm, "end": v(1195, -38.94) * mm});
            skLineSegment(sketch, "E961", {"start": v(1195, -38.94) * mm, "end": v(1195, -48.94) * mm});
            skLineSegment(sketch, "E962", {"start": v(1195, -48.94) * mm, "end": v(1189, -48.94) * mm});
            skLineSegment(sketch, "E963", {"start": v(1189, -48.94) * mm, "end": v(1189, -58.94) * mm});
            skLineSegment(sketch, "E964", {"start": v(1189, -58.94) * mm, "end": v(1195, -58.94) * mm});
            skLineSegment(sketch, "E965", {"start": v(1195, -58.94) * mm, "end": v(1195, -68.94) * mm});
            skLineSegment(sketch, "E966", {"start": v(1195, -68.94) * mm, "end": v(1189, -68.94) * mm});
            skLineSegment(sketch, "E967", {"start": v(1189, -68.94) * mm, "end": v(1189, -78.94) * mm});
            skLineSegment(sketch, "E968", {"start": v(1189, -78.94) * mm, "end": v(1195, -78.94) * mm});
            skLineSegment(sketch, "E969", {"start": v(1195, -78.94) * mm, "end": v(1195, -88.94) * mm});
            skLineSegment(sketch, "E970", {"start": v(1195, -88.94) * mm, "end": v(1189, -88.94) * mm});
            skLineSegment(sketch, "E971", {"start": v(1189, -88.94) * mm, "end": v(1189, -98.94) * mm});
            skLineSegment(sketch, "E972", {"start": v(1189, -98.94) * mm, "end": v(1195, -98.94) * mm});
            skLineSegment(sketch, "E973", {"start": v(1195, -98.94) * mm, "end": v(1195, -108.94) * mm});
            skLineSegment(sketch, "E974", {"start": v(1195, -108.94) * mm, "end": v(1189, -108.94) * mm});
            skLineSegment(sketch, "E975", {"start": v(1189, -108.94) * mm, "end": v(1189, -118.94) * mm});
            skLineSegment(sketch, "E976", {"start": v(1189, -118.94) * mm, "end": v(1195, -118.94) * mm});
            skLineSegment(sketch, "E977", {"start": v(1195, -118.94) * mm, "end": v(1195, -128.94) * mm});
            skLineSegment(sketch, "E978", {"start": v(1195, -128.94) * mm, "end": v(1189, -128.94) * mm});
            skLineSegment(sketch, "E979", {"start": v(1189, -128.94) * mm, "end": v(1189, -138.94) * mm});
            skLineSegment(sketch, "E980", {"start": v(1189, -138.94) * mm, "end": v(1195, -138.94) * mm});
            skLineSegment(sketch, "E981", {"start": v(1195, -138.94) * mm, "end": v(1195, -148.94) * mm});
            skLineSegment(sketch, "E982", {"start": v(1195, -148.94) * mm, "end": v(1189, -148.94) * mm});
            skLineSegment(sketch, "E983", {"start": v(1189, -148.94) * mm, "end": v(1189, -158.94) * mm});
            skLineSegment(sketch, "E984", {"start": v(1189, -158.94) * mm, "end": v(1195, -158.94) * mm});
            skLineSegment(sketch, "E985", {"start": v(1195, -158.94) * mm, "end": v(1195, -168.94) * mm});
            skLineSegment(sketch, "E986", {"start": v(1195, -168.94) * mm, "end": v(1189, -168.94) * mm});
            skLineSegment(sketch, "E987", {"start": v(1189, -168.94) * mm, "end": v(1189, -181.44) * mm});
            skLineSegment(sketch, "E988", {"start": v(1189, -181.44) * mm, "end": v(1195, -181.44) * mm});
            skLineSegment(sketch, "E989", {"start": v(1195, -181.44) * mm, "end": v(1195, -193.94) * mm});
            skLineSegment(sketch, "E990", {"start": v(1195, -193.94) * mm, "end": v(1178.75, -193.94) * mm});
            skLineSegment(sketch, "E991", {"start": v(1178.75, -193.94) * mm, "end": v(1178.75, -187.94) * mm});
            skLineSegment(sketch, "E992", {"start": v(1178.75, -187.94) * mm, "end": v(1162.5, -187.94) * mm});
            skLineSegment(sketch, "E993", {"start": v(1162.5, -187.94) * mm, "end": v(1162.5, -193.94) * mm});
            skLineSegment(sketch, "E994", {"start": v(1162.5, -193.94) * mm, "end": v(1152.5, -193.94) * mm});
            skLineSegment(sketch, "E995", {"start": v(1152.5, -193.94) * mm, "end": v(1152.5, -187.94) * mm});
            skLineSegment(sketch, "E996", {"start": v(1152.5, -187.94) * mm, "end": v(1142.5, -187.94) * mm});
            skLineSegment(sketch, "E997", {"start": v(1142.5, -187.94) * mm, "end": v(1142.5, -193.94) * mm});
            skLineSegment(sketch, "E998", {"start": v(1142.5, -193.94) * mm, "end": v(1132.5, -193.94) * mm});
            skLineSegment(sketch, "E999", {"start": v(1132.5, -193.94) * mm, "end": v(1132.5, -187.94) * mm});
            skLineSegment(sketch, "E1000", {"start": v(1132.5, -187.94) * mm, "end": v(1122.5, -187.94) * mm});
            skLineSegment(sketch, "E1001", {"start": v(1122.5, -187.94) * mm, "end": v(1122.5, -193.94) * mm});
            skLineSegment(sketch, "E1002", {"start": v(1122.5, -193.94) * mm, "end": v(1112.5, -193.94) * mm});
            skLineSegment(sketch, "E1003", {"start": v(1112.5, -193.94) * mm, "end": v(1112.5, -187.94) * mm});
            skLineSegment(sketch, "E1004", {"start": v(1112.5, -187.94) * mm, "end": v(1102.5, -187.94) * mm});
            skLineSegment(sketch, "E1005", {"start": v(1102.5, -187.94) * mm, "end": v(1102.5, -193.94) * mm});
            skLineSegment(sketch, "E1006", {"start": v(1102.5, -193.94) * mm, "end": v(1092.5, -193.94) * mm});
            skLineSegment(sketch, "E1007", {"start": v(1092.5, -193.94) * mm, "end": v(1092.5, -187.94) * mm});
            skLineSegment(sketch, "E1008", {"start": v(1092.5, -187.94) * mm, "end": v(1082.5, -187.94) * mm});
            skLineSegment(sketch, "E1009", {"start": v(1082.5, -187.94) * mm, "end": v(1082.5, -193.94) * mm});
            skLineSegment(sketch, "E1010", {"start": v(1082.5, -193.94) * mm, "end": v(1072.5, -193.94) * mm});
            skLineSegment(sketch, "E1011", {"start": v(1072.5, -193.94) * mm, "end": v(1072.5, -187.94) * mm});
            skLineSegment(sketch, "E1012", {"start": v(1072.5, -187.94) * mm, "end": v(1062.5, -187.94) * mm});
            skLineSegment(sketch, "E1013", {"start": v(1062.5, -187.94) * mm, "end": v(1062.5, -193.94) * mm});
            skLineSegment(sketch, "E1014", {"start": v(1062.5, -193.94) * mm, "end": v(1052.5, -193.94) * mm});
            skLineSegment(sketch, "E1015", {"start": v(1052.5, -193.94) * mm, "end": v(1052.5, -187.94) * mm});
            skLineSegment(sketch, "E1016", {"start": v(1052.5, -187.94) * mm, "end": v(1042.5, -187.94) * mm});
            skLineSegment(sketch, "E1017", {"start": v(1042.5, -187.94) * mm, "end": v(1042.5, -193.94) * mm});
            skLineSegment(sketch, "E1018", {"start": v(1042.5, -193.94) * mm, "end": v(1032.5, -193.94) * mm});
            skLineSegment(sketch, "E1019", {"start": v(1032.5, -193.94) * mm, "end": v(1032.5, -187.94) * mm});
            skLineSegment(sketch, "E1020", {"start": v(1032.5, -187.94) * mm, "end": v(1022.5, -187.94) * mm});
            skLineSegment(sketch, "E1021", {"start": v(1022.5, -187.94) * mm, "end": v(1022.5, -193.94) * mm});
            skLineSegment(sketch, "E1022", {"start": v(1022.5, -193.94) * mm, "end": v(1012.5, -193.94) * mm});
            skLineSegment(sketch, "E1023", {"start": v(1012.5, -193.94) * mm, "end": v(1012.5, -187.94) * mm});
            skLineSegment(sketch, "E1024", {"start": v(1012.5, -187.94) * mm, "end": v(1002.5, -187.94) * mm});
            skLineSegment(sketch, "E1025", {"start": v(1002.5, -187.94) * mm, "end": v(1002.5, -193.94) * mm});
            skLineSegment(sketch, "E1026", {"start": v(1002.5, -193.94) * mm, "end": v(992.5, -193.94) * mm});
            skLineSegment(sketch, "E1027", {"start": v(992.5, -193.94) * mm, "end": v(992.5, -187.94) * mm});
            skLineSegment(sketch, "E1028", {"start": v(992.5, -187.94) * mm, "end": v(982.5, -187.94) * mm});
            skLineSegment(sketch, "E1029", {"start": v(982.5, -187.94) * mm, "end": v(982.5, -193.94) * mm});
            skLineSegment(sketch, "E1030", {"start": v(982.5, -193.94) * mm, "end": v(972.5, -193.94) * mm});
            skLineSegment(sketch, "E1031", {"start": v(972.5, -193.94) * mm, "end": v(972.5, -187.94) * mm});
            skLineSegment(sketch, "E1032", {"start": v(972.5, -187.94) * mm, "end": v(962.5, -187.94) * mm});
            skLineSegment(sketch, "E1033", {"start": v(962.5, -187.94) * mm, "end": v(962.5, -193.94) * mm});
            skLineSegment(sketch, "E1034", {"start": v(962.5, -193.94) * mm, "end": v(952.5, -193.94) * mm});
            skLineSegment(sketch, "E1035", {"start": v(952.5, -193.94) * mm, "end": v(952.5, -187.94) * mm});
            skLineSegment(sketch, "E1036", {"start": v(952.5, -187.94) * mm, "end": v(942.5, -187.94) * mm});
            skLineSegment(sketch, "E1037", {"start": v(942.5, -187.94) * mm, "end": v(942.5, -193.94) * mm});
            skLineSegment(sketch, "E1038", {"start": v(942.5, -193.94) * mm, "end": v(932.5, -193.94) * mm});
            skLineSegment(sketch, "E1039", {"start": v(932.5, -193.94) * mm, "end": v(932.5, -187.94) * mm});
            skLineSegment(sketch, "E1040", {"start": v(932.5, -187.94) * mm, "end": v(922.5, -187.94) * mm});
            skLineSegment(sketch, "E1041", {"start": v(922.5, -187.94) * mm, "end": v(922.5, -193.94) * mm});
            skLineSegment(sketch, "E1042", {"start": v(922.5, -193.94) * mm, "end": v(912.5, -193.94) * mm});
            skLineSegment(sketch, "E1043", {"start": v(912.5, -193.94) * mm, "end": v(912.5, -187.94) * mm});
            skLineSegment(sketch, "E1044", {"start": v(912.5, -187.94) * mm, "end": v(902.5, -187.94) * mm});
            skLineSegment(sketch, "E1045", {"start": v(902.5, -187.94) * mm, "end": v(902.5, -193.94) * mm});
            skLineSegment(sketch, "E1046", {"start": v(902.5, -193.94) * mm, "end": v(892.5, -193.94) * mm});
            skLineSegment(sketch, "E1047", {"start": v(892.5, -193.94) * mm, "end": v(892.5, -187.94) * mm});
            skLineSegment(sketch, "E1048", {"start": v(892.5, -187.94) * mm, "end": v(882.5, -187.94) * mm});
            skLineSegment(sketch, "E1049", {"start": v(882.5, -187.94) * mm, "end": v(882.5, -193.94) * mm});
            skLineSegment(sketch, "E1050", {"start": v(882.5, -193.94) * mm, "end": v(872.5, -193.94) * mm});
            skLineSegment(sketch, "E1051", {"start": v(872.5, -193.94) * mm, "end": v(872.5, -187.94) * mm});
            skLineSegment(sketch, "E1052", {"start": v(872.5, -187.94) * mm, "end": v(862.5, -187.94) * mm});
            skLineSegment(sketch, "E1053", {"start": v(862.5, -187.94) * mm, "end": v(862.5, -193.94) * mm});
            skLineSegment(sketch, "E1054", {"start": v(862.5, -193.94) * mm, "end": v(852.5, -193.94) * mm});
            skLineSegment(sketch, "E1055", {"start": v(852.5, -193.94) * mm, "end": v(852.5, -187.94) * mm});
            skLineSegment(sketch, "E1056", {"start": v(852.5, -187.94) * mm, "end": v(842.5, -187.94) * mm});
            skLineSegment(sketch, "E1057", {"start": v(842.5, -187.94) * mm, "end": v(842.5, -193.94) * mm});
            skLineSegment(sketch, "E1058", {"start": v(842.5, -193.94) * mm, "end": v(832.5, -193.94) * mm});
            skLineSegment(sketch, "E1059", {"start": v(832.5, -193.94) * mm, "end": v(832.5, -187.94) * mm});
            skLineSegment(sketch, "E1060", {"start": v(832.5, -187.94) * mm, "end": v(822.5, -187.94) * mm});
            skLineSegment(sketch, "E1061", {"start": v(822.5, -187.94) * mm, "end": v(822.5, -193.94) * mm});
            skLineSegment(sketch, "E1062", {"start": v(822.5, -193.94) * mm, "end": v(812.5, -193.94) * mm});
            skLineSegment(sketch, "E1063", {"start": v(812.5, -193.94) * mm, "end": v(812.5, -187.94) * mm});
            skLineSegment(sketch, "E1064", {"start": v(812.5, -187.94) * mm, "end": v(802.5, -187.94) * mm});
            skLineSegment(sketch, "E1065", {"start": v(802.5, -187.94) * mm, "end": v(802.5, -193.94) * mm});
            skLineSegment(sketch, "E1066", {"start": v(802.5, -193.94) * mm, "end": v(792.5, -193.94) * mm});
            skLineSegment(sketch, "E1067", {"start": v(792.5, -193.94) * mm, "end": v(792.5, -187.94) * mm});
            skLineSegment(sketch, "E1068", {"start": v(792.5, -187.94) * mm, "end": v(782.5, -187.94) * mm});
            skLineSegment(sketch, "E1069", {"start": v(782.5, -187.94) * mm, "end": v(782.5, -193.94) * mm});
            skLineSegment(sketch, "E1070", {"start": v(782.5, -193.94) * mm, "end": v(772.5, -193.94) * mm});
            skLineSegment(sketch, "E1071", {"start": v(772.5, -193.94) * mm, "end": v(772.5, -187.94) * mm});
            skLineSegment(sketch, "E1072", {"start": v(772.5, -187.94) * mm, "end": v(762.5, -187.94) * mm});
            skLineSegment(sketch, "E1073", {"start": v(762.5, -187.94) * mm, "end": v(762.5, -193.94) * mm});
            skLineSegment(sketch, "E1074", {"start": v(762.5, -193.94) * mm, "end": v(752.5, -193.94) * mm});
            skLineSegment(sketch, "E1075", {"start": v(752.5, -193.94) * mm, "end": v(752.5, -187.94) * mm});
            skLineSegment(sketch, "E1076", {"start": v(752.5, -187.94) * mm, "end": v(742.5, -187.94) * mm});
            skLineSegment(sketch, "E1077", {"start": v(742.5, -187.94) * mm, "end": v(742.5, -193.94) * mm});
            skLineSegment(sketch, "E1078", {"start": v(742.5, -193.94) * mm, "end": v(732.5, -193.94) * mm});
            skLineSegment(sketch, "E1079", {"start": v(732.5, -193.94) * mm, "end": v(732.5, -187.94) * mm});
            skLineSegment(sketch, "E1080", {"start": v(732.5, -187.94) * mm, "end": v(722.5, -187.94) * mm});
            skLineSegment(sketch, "E1081", {"start": v(722.5, -187.94) * mm, "end": v(722.5, -193.94) * mm});
            skLineSegment(sketch, "E1082", {"start": v(722.5, -193.94) * mm, "end": v(712.5, -193.94) * mm});
            skLineSegment(sketch, "E1083", {"start": v(712.5, -193.94) * mm, "end": v(712.5, -187.94) * mm});
            skLineSegment(sketch, "E1084", {"start": v(712.5, -187.94) * mm, "end": v(702.5, -187.94) * mm});
            skLineSegment(sketch, "E1085", {"start": v(702.5, -187.94) * mm, "end": v(702.5, -193.94) * mm});
            skLineSegment(sketch, "E1086", {"start": v(702.5, -193.94) * mm, "end": v(692.5, -193.94) * mm});
            skLineSegment(sketch, "E1087", {"start": v(692.5, -193.94) * mm, "end": v(692.5, -187.94) * mm});
            skLineSegment(sketch, "E1088", {"start": v(692.5, -187.94) * mm, "end": v(682.5, -187.94) * mm});
            skLineSegment(sketch, "E1089", {"start": v(682.5, -187.94) * mm, "end": v(682.5, -193.94) * mm});
            skLineSegment(sketch, "E1090", {"start": v(682.5, -193.94) * mm, "end": v(672.5, -193.94) * mm});
            skLineSegment(sketch, "E1091", {"start": v(672.5, -193.94) * mm, "end": v(672.5, -187.94) * mm});
            skLineSegment(sketch, "E1092", {"start": v(672.5, -187.94) * mm, "end": v(662.5, -187.94) * mm});
            skLineSegment(sketch, "E1093", {"start": v(662.5, -187.94) * mm, "end": v(662.5, -193.94) * mm});
            skLineSegment(sketch, "E1094", {"start": v(662.5, -193.94) * mm, "end": v(652.5, -193.94) * mm});
            skLineSegment(sketch, "E1095", {"start": v(652.5, -193.94) * mm, "end": v(652.5, -187.94) * mm});
            skLineSegment(sketch, "E1096", {"start": v(652.5, -187.94) * mm, "end": v(642.5, -187.94) * mm});
            skLineSegment(sketch, "E1097", {"start": v(642.5, -187.94) * mm, "end": v(642.5, -193.94) * mm});
            skLineSegment(sketch, "E1098", {"start": v(642.5, -193.94) * mm, "end": v(632.5, -193.94) * mm});
            skLineSegment(sketch, "E1099", {"start": v(632.5, -193.94) * mm, "end": v(632.5, -187.94) * mm});
            skLineSegment(sketch, "E1100", {"start": v(632.5, -187.94) * mm, "end": v(622.5, -187.94) * mm});
            skLineSegment(sketch, "E1101", {"start": v(622.5, -187.94) * mm, "end": v(622.5, -193.94) * mm});
            skLineSegment(sketch, "E1102", {"start": v(622.5, -193.94) * mm, "end": v(612.5, -193.94) * mm});
            skLineSegment(sketch, "E1103", {"start": v(612.5, -193.94) * mm, "end": v(612.5, -187.94) * mm});
            skLineSegment(sketch, "E1104", {"start": v(612.5, -187.94) * mm, "end": v(602.5, -187.94) * mm});
            skLineSegment(sketch, "E1105", {"start": v(602.5, -187.94) * mm, "end": v(602.5, -193.94) * mm});
            skLineSegment(sketch, "E1106", {"start": v(602.5, -193.94) * mm, "end": v(592.5, -193.94) * mm});
            skLineSegment(sketch, "E1107", {"start": v(592.5, -193.94) * mm, "end": v(592.5, -187.94) * mm});
            skLineSegment(sketch, "E1108", {"start": v(592.5, -187.94) * mm, "end": v(582.5, -187.94) * mm});
            skLineSegment(sketch, "E1109", {"start": v(582.5, -187.94) * mm, "end": v(582.5, -193.94) * mm});
            skLineSegment(sketch, "E1110", {"start": v(582.5, -193.94) * mm, "end": v(572.5, -193.94) * mm});
            skLineSegment(sketch, "E1111", {"start": v(572.5, -193.94) * mm, "end": v(572.5, -187.94) * mm});
            skLineSegment(sketch, "E1112", {"start": v(572.5, -187.94) * mm, "end": v(562.5, -187.94) * mm});
            skLineSegment(sketch, "E1113", {"start": v(562.5, -187.94) * mm, "end": v(562.5, -193.94) * mm});
            skLineSegment(sketch, "E1114", {"start": v(562.5, -193.94) * mm, "end": v(552.5, -193.94) * mm});
            skLineSegment(sketch, "E1115", {"start": v(552.5, -193.94) * mm, "end": v(552.5, -187.94) * mm});
            skLineSegment(sketch, "E1116", {"start": v(552.5, -187.94) * mm, "end": v(542.5, -187.94) * mm});
            skLineSegment(sketch, "E1117", {"start": v(542.5, -187.94) * mm, "end": v(542.5, -193.94) * mm});
            skLineSegment(sketch, "E1118", {"start": v(542.5, -193.94) * mm, "end": v(532.5, -193.94) * mm});
            skLineSegment(sketch, "E1119", {"start": v(532.5, -193.94) * mm, "end": v(532.5, -187.94) * mm});
            skLineSegment(sketch, "E1120", {"start": v(532.5, -187.94) * mm, "end": v(522.5, -187.94) * mm});
            skLineSegment(sketch, "E1121", {"start": v(522.5, -187.94) * mm, "end": v(522.5, -193.94) * mm});
            skLineSegment(sketch, "E1122", {"start": v(522.5, -193.94) * mm, "end": v(512.5, -193.94) * mm});
            skLineSegment(sketch, "E1123", {"start": v(512.5, -193.94) * mm, "end": v(512.5, -187.94) * mm});
            skLineSegment(sketch, "E1124", {"start": v(512.5, -187.94) * mm, "end": v(502.5, -187.94) * mm});
            skLineSegment(sketch, "E1125", {"start": v(502.5, -187.94) * mm, "end": v(502.5, -193.94) * mm});
            skLineSegment(sketch, "E1126", {"start": v(502.5, -193.94) * mm, "end": v(492.5, -193.94) * mm});
            skLineSegment(sketch, "E1127", {"start": v(492.5, -193.94) * mm, "end": v(492.5, -187.94) * mm});
            skLineSegment(sketch, "E1128", {"start": v(492.5, -187.94) * mm, "end": v(482.5, -187.94) * mm});
            skLineSegment(sketch, "E1129", {"start": v(482.5, -187.94) * mm, "end": v(482.5, -193.94) * mm});
            skLineSegment(sketch, "E1130", {"start": v(482.5, -193.94) * mm, "end": v(472.5, -193.94) * mm});
            skLineSegment(sketch, "E1131", {"start": v(472.5, -193.94) * mm, "end": v(472.5, -187.94) * mm});
            skLineSegment(sketch, "E1132", {"start": v(472.5, -187.94) * mm, "end": v(462.5, -187.94) * mm});
            skLineSegment(sketch, "E1133", {"start": v(462.5, -187.94) * mm, "end": v(462.5, -193.94) * mm});
            skLineSegment(sketch, "E1134", {"start": v(462.5, -193.94) * mm, "end": v(452.5, -193.94) * mm});
            skLineSegment(sketch, "E1135", {"start": v(452.5, -193.94) * mm, "end": v(452.5, -187.94) * mm});
            skLineSegment(sketch, "E1136", {"start": v(452.5, -187.94) * mm, "end": v(442.5, -187.94) * mm});
            skLineSegment(sketch, "E1137", {"start": v(442.5, -187.94) * mm, "end": v(442.5, -193.94) * mm});
            skLineSegment(sketch, "E1138", {"start": v(442.5, -193.94) * mm, "end": v(432.5, -193.94) * mm});
            skLineSegment(sketch, "E1139", {"start": v(432.5, -193.94) * mm, "end": v(432.5, -187.94) * mm});
            skLineSegment(sketch, "E1140", {"start": v(432.5, -187.94) * mm, "end": v(422.5, -187.94) * mm});
            skLineSegment(sketch, "E1141", {"start": v(422.5, -187.94) * mm, "end": v(422.5, -193.94) * mm});
            skLineSegment(sketch, "E1142", {"start": v(422.5, -193.94) * mm, "end": v(412.5, -193.94) * mm});
            skLineSegment(sketch, "E1143", {"start": v(412.5, -193.94) * mm, "end": v(412.5, -187.94) * mm});
            skLineSegment(sketch, "E1144", {"start": v(412.5, -187.94) * mm, "end": v(402.5, -187.94) * mm});
            skLineSegment(sketch, "E1145", {"start": v(402.5, -187.94) * mm, "end": v(402.5, -193.94) * mm});
            skLineSegment(sketch, "E1146", {"start": v(402.5, -193.94) * mm, "end": v(392.5, -193.94) * mm});
            skLineSegment(sketch, "E1147", {"start": v(392.5, -193.94) * mm, "end": v(392.5, -187.94) * mm});
            skLineSegment(sketch, "E1148", {"start": v(392.5, -187.94) * mm, "end": v(382.5, -187.94) * mm});
            skLineSegment(sketch, "E1149", {"start": v(382.5, -187.94) * mm, "end": v(382.5, -193.94) * mm});
            skLineSegment(sketch, "E1150", {"start": v(382.5, -193.94) * mm, "end": v(372.5, -193.94) * mm});
            skLineSegment(sketch, "E1151", {"start": v(372.5, -193.94) * mm, "end": v(372.5, -187.94) * mm});
            skLineSegment(sketch, "E1152", {"start": v(372.5, -187.94) * mm, "end": v(362.5, -187.94) * mm});
            skLineSegment(sketch, "E1153", {"start": v(362.5, -187.94) * mm, "end": v(362.5, -193.94) * mm});
            skLineSegment(sketch, "E1154", {"start": v(362.5, -193.94) * mm, "end": v(352.5, -193.94) * mm});
            skLineSegment(sketch, "E1155", {"start": v(352.5, -193.94) * mm, "end": v(352.5, -187.94) * mm});
            skLineSegment(sketch, "E1156", {"start": v(352.5, -187.94) * mm, "end": v(342.5, -187.94) * mm});
            skLineSegment(sketch, "E1157", {"start": v(342.5, -187.94) * mm, "end": v(342.5, -193.94) * mm});
            skLineSegment(sketch, "E1158", {"start": v(342.5, -193.94) * mm, "end": v(332.5, -193.94) * mm});
            skLineSegment(sketch, "E1159", {"start": v(332.5, -193.94) * mm, "end": v(332.5, -187.94) * mm});
            skLineSegment(sketch, "E1160", {"start": v(332.5, -187.94) * mm, "end": v(322.5, -187.94) * mm});
            skLineSegment(sketch, "E1161", {"start": v(322.5, -187.94) * mm, "end": v(322.5, -193.94) * mm});
            skLineSegment(sketch, "E1162", {"start": v(322.5, -193.94) * mm, "end": v(312.5, -193.94) * mm});
            skLineSegment(sketch, "E1163", {"start": v(312.5, -193.94) * mm, "end": v(312.5, -187.94) * mm});
            skLineSegment(sketch, "E1164", {"start": v(312.5, -187.94) * mm, "end": v(302.5, -187.94) * mm});
            skLineSegment(sketch, "E1165", {"start": v(302.5, -187.94) * mm, "end": v(302.5, -193.94) * mm});
            skLineSegment(sketch, "E1166", {"start": v(302.5, -193.94) * mm, "end": v(292.5, -193.94) * mm});
            skLineSegment(sketch, "E1167", {"start": v(292.5, -193.94) * mm, "end": v(292.5, -187.94) * mm});
            skLineSegment(sketch, "E1168", {"start": v(292.5, -187.94) * mm, "end": v(282.5, -187.94) * mm});
            skLineSegment(sketch, "E1169", {"start": v(282.5, -187.94) * mm, "end": v(282.5, -193.94) * mm});
            skLineSegment(sketch, "E1170", {"start": v(282.5, -193.94) * mm, "end": v(272.5, -193.94) * mm});
            skLineSegment(sketch, "E1171", {"start": v(272.5, -193.94) * mm, "end": v(272.5, -187.94) * mm});
            skLineSegment(sketch, "E1172", {"start": v(272.5, -187.94) * mm, "end": v(262.5, -187.94) * mm});
            skLineSegment(sketch, "E1173", {"start": v(262.5, -187.94) * mm, "end": v(262.5, -193.94) * mm});
            skLineSegment(sketch, "E1174", {"start": v(262.5, -193.94) * mm, "end": v(252.5, -193.94) * mm});
            skLineSegment(sketch, "E1175", {"start": v(252.5, -193.94) * mm, "end": v(252.5, -187.94) * mm});
            skLineSegment(sketch, "E1176", {"start": v(252.5, -187.94) * mm, "end": v(242.5, -187.94) * mm});
            skLineSegment(sketch, "E1177", {"start": v(242.5, -187.94) * mm, "end": v(242.5, -193.94) * mm});
            skLineSegment(sketch, "E1178", {"start": v(242.5, -193.94) * mm, "end": v(232.5, -193.94) * mm});
            skLineSegment(sketch, "E1179", {"start": v(232.5, -193.94) * mm, "end": v(232.5, -187.94) * mm});
            skLineSegment(sketch, "E1180", {"start": v(232.5, -187.94) * mm, "end": v(222.5, -187.94) * mm});
            skLineSegment(sketch, "E1181", {"start": v(222.5, -187.94) * mm, "end": v(222.5, -193.94) * mm});
            skLineSegment(sketch, "E1182", {"start": v(222.5, -193.94) * mm, "end": v(212.5, -193.94) * mm});
            skLineSegment(sketch, "E1183", {"start": v(212.5, -193.94) * mm, "end": v(212.5, -187.94) * mm});
            skLineSegment(sketch, "E1184", {"start": v(212.5, -187.94) * mm, "end": v(202.5, -187.94) * mm});
            skLineSegment(sketch, "E1185", {"start": v(202.5, -187.94) * mm, "end": v(202.5, -193.94) * mm});
            skLineSegment(sketch, "E1186", {"start": v(202.5, -193.94) * mm, "end": v(192.5, -193.94) * mm});
            skLineSegment(sketch, "E1187", {"start": v(192.5, -193.94) * mm, "end": v(192.5, -187.94) * mm});
            skLineSegment(sketch, "E1188", {"start": v(192.5, -187.94) * mm, "end": v(182.5, -187.94) * mm});
            skLineSegment(sketch, "E1189", {"start": v(182.5, -187.94) * mm, "end": v(182.5, -193.94) * mm});
            skLineSegment(sketch, "E1190", {"start": v(182.5, -193.94) * mm, "end": v(172.5, -193.94) * mm});
            skLineSegment(sketch, "E1191", {"start": v(172.5, -193.94) * mm, "end": v(172.5, -187.94) * mm});
            skLineSegment(sketch, "E1192", {"start": v(172.5, -187.94) * mm, "end": v(162.5, -187.94) * mm});
            skLineSegment(sketch, "E1193", {"start": v(162.5, -187.94) * mm, "end": v(162.5, -193.94) * mm});
            skLineSegment(sketch, "E1194", {"start": v(162.5, -193.94) * mm, "end": v(152.5, -193.94) * mm});
            skLineSegment(sketch, "E1195", {"start": v(152.5, -193.94) * mm, "end": v(152.5, -187.94) * mm});
            skLineSegment(sketch, "E1196", {"start": v(152.5, -187.94) * mm, "end": v(142.5, -187.94) * mm});
            skLineSegment(sketch, "E1197", {"start": v(142.5, -187.94) * mm, "end": v(142.5, -193.94) * mm});
            skLineSegment(sketch, "E1198", {"start": v(142.5, -193.94) * mm, "end": v(132.5, -193.94) * mm});
            skLineSegment(sketch, "E1199", {"start": v(132.5, -193.94) * mm, "end": v(132.5, -187.94) * mm});
            skLineSegment(sketch, "E1200", {"start": v(132.5, -187.94) * mm, "end": v(122.5, -187.94) * mm});
            skLineSegment(sketch, "E1201", {"start": v(122.5, -187.94) * mm, "end": v(122.5, -193.94) * mm});
            skLineSegment(sketch, "E1202", {"start": v(122.5, -193.94) * mm, "end": v(112.5, -193.94) * mm});
            skLineSegment(sketch, "E1203", {"start": v(112.5, -193.94) * mm, "end": v(112.5, -187.94) * mm});
            skLineSegment(sketch, "E1204", {"start": v(112.5, -187.94) * mm, "end": v(102.5, -187.94) * mm});
            skLineSegment(sketch, "E1205", {"start": v(102.5, -187.94) * mm, "end": v(102.5, -193.94) * mm});
            skLineSegment(sketch, "E1206", {"start": v(102.5, -193.94) * mm, "end": v(92.5, -193.94) * mm});
            skLineSegment(sketch, "E1207", {"start": v(92.5, -193.94) * mm, "end": v(92.5, -187.94) * mm});
            skLineSegment(sketch, "E1208", {"start": v(92.5, -187.94) * mm, "end": v(82.5, -187.94) * mm});
            skLineSegment(sketch, "E1209", {"start": v(82.5, -187.94) * mm, "end": v(82.5, -193.94) * mm});
            skLineSegment(sketch, "E1210", {"start": v(82.5, -193.94) * mm, "end": v(72.5, -193.94) * mm});
            skLineSegment(sketch, "E1211", {"start": v(72.5, -193.94) * mm, "end": v(72.5, -187.94) * mm});
            skLineSegment(sketch, "E1212", {"start": v(72.5, -187.94) * mm, "end": v(62.5, -187.94) * mm});
            skLineSegment(sketch, "E1213", {"start": v(62.5, -187.94) * mm, "end": v(62.5, -193.94) * mm});
            skLineSegment(sketch, "E1214", {"start": v(62.5, -193.94) * mm, "end": v(52.5, -193.94) * mm});
            skLineSegment(sketch, "E1215", {"start": v(52.5, -193.94) * mm, "end": v(52.5, -187.94) * mm});
            skLineSegment(sketch, "E1216", {"start": v(52.5, -187.94) * mm, "end": v(42.5, -187.94) * mm});
            skLineSegment(sketch, "E1217", {"start": v(42.5, -187.94) * mm, "end": v(42.5, -193.94) * mm});
            skLineSegment(sketch, "E1218", {"start": v(42.5, -193.94) * mm, "end": v(32.5, -193.94) * mm});
            skLineSegment(sketch, "E1219", {"start": v(32.5, -193.94) * mm, "end": v(32.5, -187.94) * mm});
            skLineSegment(sketch, "E1220", {"start": v(32.5, -187.94) * mm, "end": v(16.25, -187.94) * mm});
            skLineSegment(sketch, "E1221", {"start": v(16.25, -187.94) * mm, "end": v(16.25, -193.94) * mm});
            skLineSegment(sketch, "E1222", {"start": v(16.25, -193.94) * mm, "end": v(0, -193.94) * mm});
            skLineSegment(sketch, "E1223", {"start": v(0, -193.94) * mm, "end": v(0, -181.44) * mm});
            skLineSegment(sketch, "E1224", {"start": v(0, -181.44) * mm, "end": v(6, -181.44) * mm});
            skLineSegment(sketch, "E1225", {"start": v(6, -181.44) * mm, "end": v(6, -168.94) * mm});
            skLineSegment(sketch, "E1226", {"start": v(6, -168.94) * mm, "end": v(0, -168.94) * mm});
            skLineSegment(sketch, "E1227", {"start": v(0, -168.94) * mm, "end": v(0, -158.94) * mm});
            skLineSegment(sketch, "E1228", {"start": v(0, -158.94) * mm, "end": v(6, -158.94) * mm});
            skLineSegment(sketch, "E1229", {"start": v(6, -158.94) * mm, "end": v(6, -148.94) * mm});
            skLineSegment(sketch, "E1230", {"start": v(6, -148.94) * mm, "end": v(0, -148.94) * mm});
            skLineSegment(sketch, "E1231", {"start": v(0, -148.94) * mm, "end": v(0, -138.94) * mm});
            skLineSegment(sketch, "E1232", {"start": v(0, -138.94) * mm, "end": v(6, -138.94) * mm});
            skLineSegment(sketch, "E1233", {"start": v(6, -138.94) * mm, "end": v(6, -128.94) * mm});
            skLineSegment(sketch, "E1234", {"start": v(6, -128.94) * mm, "end": v(0, -128.94) * mm});
            skLineSegment(sketch, "E1235", {"start": v(0, -128.94) * mm, "end": v(0, -118.94) * mm});
            skLineSegment(sketch, "E1236", {"start": v(0, -118.94) * mm, "end": v(6, -118.94) * mm});
            skLineSegment(sketch, "E1237", {"start": v(6, -118.94) * mm, "end": v(6, -108.94) * mm});
            skLineSegment(sketch, "E1238", {"start": v(6, -108.94) * mm, "end": v(0, -108.94) * mm});
            skLineSegment(sketch, "E1239", {"start": v(0, -108.94) * mm, "end": v(0, -98.94) * mm});
            skLineSegment(sketch, "E1240", {"start": v(0, -98.94) * mm, "end": v(6, -98.94) * mm});
            skLineSegment(sketch, "E1241", {"start": v(6, -98.94) * mm, "end": v(6, -88.94) * mm});
            skLineSegment(sketch, "E1242", {"start": v(6, -88.94) * mm, "end": v(0, -88.94) * mm});
            skLineSegment(sketch, "E1243", {"start": v(0, -88.94) * mm, "end": v(0, -78.94) * mm});
            skLineSegment(sketch, "E1244", {"start": v(0, -78.94) * mm, "end": v(6, -78.94) * mm});
            skLineSegment(sketch, "E1245", {"start": v(6, -78.94) * mm, "end": v(6, -68.94) * mm});
            skLineSegment(sketch, "E1246", {"start": v(6, -68.94) * mm, "end": v(0, -68.94) * mm});
            skLineSegment(sketch, "E1247", {"start": v(0, -68.94) * mm, "end": v(0, -58.94) * mm});
            skLineSegment(sketch, "E1248", {"start": v(0, -58.94) * mm, "end": v(6, -58.94) * mm});
            skLineSegment(sketch, "E1249", {"start": v(6, -58.94) * mm, "end": v(6, -48.94) * mm});
            skLineSegment(sketch, "E1250", {"start": v(6, -48.94) * mm, "end": v(0, -48.94) * mm});
            skLineSegment(sketch, "E1251", {"start": v(0, -48.94) * mm, "end": v(0, -38.94) * mm});
            skLineSegment(sketch, "E1252", {"start": v(0, -38.94) * mm, "end": v(6, -38.94) * mm});
            skLineSegment(sketch, "E1253", {"start": v(6, -38.94) * mm, "end": v(6, -28.94) * mm});
            skLineSegment(sketch, "E1254", {"start": v(6, -28.94) * mm, "end": v(0, -28.94) * mm});
            skLineSegment(sketch, "E1255", {"start": v(0, -28.94) * mm, "end": v(0, -18.94) * mm});
            skLineSegment(sketch, "E1256", {"start": v(0, -18.94) * mm, "end": v(6, -18.94) * mm});
            skLineSegment(sketch, "E1257", {"start": v(6, -18.94) * mm, "end": v(6, -8.94) * mm});
            skLineSegment(sketch, "E1258", {"start": v(6, -8.94) * mm, "end": v(0, -8.94) * mm});
            skLineSegment(sketch, "E1259", {"start": v(0, -8.94) * mm, "end": v(0, 1.06) * mm});
            skLineSegment(sketch, "E1260", {"start": v(0, 1.06) * mm, "end": v(6, 1.06) * mm});
            skLineSegment(sketch, "E1261", {"start": v(6, 1.06) * mm, "end": v(6, 11.06) * mm});
            skLineSegment(sketch, "E1262", {"start": v(6, 11.06) * mm, "end": v(0, 11.06) * mm});
            skLineSegment(sketch, "E1263", {"start": v(0, 11.06) * mm, "end": v(0, 21.06) * mm});
            skLineSegment(sketch, "E1264", {"start": v(0, 21.06) * mm, "end": v(6, 21.06) * mm});
            skLineSegment(sketch, "E1265", {"start": v(6, 21.06) * mm, "end": v(6, 31.06) * mm});
            skLineSegment(sketch, "E1266", {"start": v(6, 31.06) * mm, "end": v(0, 31.06) * mm});
            skLineSegment(sketch, "E1267", {"start": v(0, 31.06) * mm, "end": v(0, 41.06) * mm});
            skLineSegment(sketch, "E1268", {"start": v(0, 41.06) * mm, "end": v(6, 41.06) * mm});
            skLineSegment(sketch, "E1269", {"start": v(6, 41.06) * mm, "end": v(6, 51.06) * mm});
            skLineSegment(sketch, "E1270", {"start": v(6, 51.06) * mm, "end": v(0, 51.06) * mm});
            skLineSegment(sketch, "E1271", {"start": v(0, 51.06) * mm, "end": v(0, 61.06) * mm});
            skLineSegment(sketch, "E1272", {"start": v(0, 61.06) * mm, "end": v(6, 61.06) * mm});
            skLineSegment(sketch, "E1273", {"start": v(6, 61.06) * mm, "end": v(6, 71.06) * mm});
            skLineSegment(sketch, "E1274", {"start": v(6, 71.06) * mm, "end": v(0, 71.06) * mm});
            skLineSegment(sketch, "E1275", {"start": v(0, 71.06) * mm, "end": v(0, 81.06) * mm});
            skLineSegment(sketch, "E1276", {"start": v(0, 81.06) * mm, "end": v(6, 81.06) * mm});
            skLineSegment(sketch, "E1277", {"start": v(6, 81.06) * mm, "end": v(6, 91.06) * mm});
            skLineSegment(sketch, "E1278", {"start": v(6, 91.06) * mm, "end": v(0, 91.06) * mm});
            skLineSegment(sketch, "E1279", {"start": v(0, 91.06) * mm, "end": v(0, 101.06) * mm});
            skLineSegment(sketch, "E1280", {"start": v(0, 101.06) * mm, "end": v(6, 101.06) * mm});
            skLineSegment(sketch, "E1281", {"start": v(6, 101.06) * mm, "end": v(6, 111.06) * mm});
            skLineSegment(sketch, "E1282", {"start": v(6, 111.06) * mm, "end": v(0, 111.06) * mm});
            skLineSegment(sketch, "E1283", {"start": v(0, 111.06) * mm, "end": v(0, 121.06) * mm});
            skLineSegment(sketch, "E1284", {"start": v(0, 121.06) * mm, "end": v(6, 121.06) * mm});
            skLineSegment(sketch, "E1285", {"start": v(6, 121.06) * mm, "end": v(6, 131.06) * mm});
            skLineSegment(sketch, "E1286", {"start": v(6, 131.06) * mm, "end": v(0, 131.06) * mm});
            skLineSegment(sketch, "E1287", {"start": v(0, 131.06) * mm, "end": v(0, 141.06) * mm});
            skLineSegment(sketch, "E1288", {"start": v(0, 141.06) * mm, "end": v(6, 141.06) * mm});
            skLineSegment(sketch, "E1289", {"start": v(6, 141.06) * mm, "end": v(6, 151.06) * mm});
            skLineSegment(sketch, "E1290", {"start": v(6, 151.06) * mm, "end": v(0, 151.06) * mm});
            skLineSegment(sketch, "E1291", {"start": v(0, 151.06) * mm, "end": v(0, 161.06) * mm});
            skLineSegment(sketch, "E1292", {"start": v(0, 161.06) * mm, "end": v(6, 161.06) * mm});
            skLineSegment(sketch, "E1293", {"start": v(6, 161.06) * mm, "end": v(6, 171.06) * mm});
            skLineSegment(sketch, "E1294", {"start": v(6, 171.06) * mm, "end": v(0, 171.06) * mm});
            skLineSegment(sketch, "E1295", {"start": v(0, 171.06) * mm, "end": v(0, 181.06) * mm});
            skLineSegment(sketch, "E1296", {"start": v(0, 181.06) * mm, "end": v(6, 181.06) * mm});
            skLineSegment(sketch, "E1297", {"start": v(6, 181.06) * mm, "end": v(6, 191.06) * mm});
            skLineSegment(sketch, "E1298", {"start": v(6, 191.06) * mm, "end": v(0, 191.06) * mm});
            skLineSegment(sketch, "E1299", {"start": v(0, 191.06) * mm, "end": v(0, 201.06) * mm});
            skLineSegment(sketch, "E1300", {"start": v(0, 201.06) * mm, "end": v(6, 201.06) * mm});
            skLineSegment(sketch, "E1301", {"start": v(6, 201.06) * mm, "end": v(6, 211.06) * mm});
            skLineSegment(sketch, "E1302", {"start": v(6, 211.06) * mm, "end": v(0, 211.06) * mm});
            skLineSegment(sketch, "E1303", {"start": v(0, 211.06) * mm, "end": v(0, 221.06) * mm});
            skLineSegment(sketch, "E1304", {"start": v(0, 221.06) * mm, "end": v(6, 221.06) * mm});
            skLineSegment(sketch, "E1305", {"start": v(6, 221.06) * mm, "end": v(6, 231.06) * mm});
            skLineSegment(sketch, "E1306", {"start": v(6, 231.06) * mm, "end": v(0, 231.06) * mm});
            skLineSegment(sketch, "E1307", {"start": v(0, 231.06) * mm, "end": v(0, 241.06) * mm});
            skLineSegment(sketch, "E1308", {"start": v(0, 241.06) * mm, "end": v(6, 241.06) * mm});
            skLineSegment(sketch, "E1309", {"start": v(6, 241.06) * mm, "end": v(6, 251.06) * mm});
            skLineSegment(sketch, "E1310", {"start": v(6, 251.06) * mm, "end": v(0, 251.06) * mm});
            skLineSegment(sketch, "E1311", {"start": v(0, 251.06) * mm, "end": v(0, 261.06) * mm});
            skLineSegment(sketch, "E1312", {"start": v(0, 261.06) * mm, "end": v(6, 261.06) * mm});
            skLineSegment(sketch, "E1313", {"start": v(6, 261.06) * mm, "end": v(6, 271.06) * mm});
            skLineSegment(sketch, "E1314", {"start": v(6, 271.06) * mm, "end": v(0, 271.06) * mm});
            skLineSegment(sketch, "E1315", {"start": v(0, 271.06) * mm, "end": v(0, 281.06) * mm});
            skLineSegment(sketch, "E1316", {"start": v(0, 281.06) * mm, "end": v(6, 281.06) * mm});
            skLineSegment(sketch, "E1317", {"start": v(6, 281.06) * mm, "end": v(6, 293.56) * mm});
            skLineSegment(sketch, "E1318", {"start": v(6, 293.56) * mm, "end": v(0, 293.56) * mm});
            skLineSegment(sketch, "E1319", {"start": v(0, 293.56) * mm, "end": v(0, 306.06) * mm});
            skLineSegment(sketch, "E1320", {"start": v(-194.95, -255.72) * mm, "end": v(-194.93, -260.12) * mm});
            skLineSegment(sketch, "E1321", {"start": v(-194.93, -260.12) * mm, "end": v(-200.93, -260.15) * mm});
            skLineSegment(sketch, "E1322", {"start": v(-200.93, -260.15) * mm, "end": v(-200.89, -270.55) * mm});
            skLineSegment(sketch, "E1323", {"start": v(-200.89, -270.55) * mm, "end": v(-194.89, -270.52) * mm});
            skLineSegment(sketch, "E1324", {"start": v(-194.89, -270.52) * mm, "end": v(-194.84, -280.92) * mm});
            skLineSegment(sketch, "E1325", {"start": v(-194.84, -280.92) * mm, "end": v(-200.84, -280.95) * mm});
            skLineSegment(sketch, "E1326", {"start": v(-200.84, -280.95) * mm, "end": v(-200.8, -291.35) * mm});
            skLineSegment(sketch, "E1327", {"start": v(-200.8, -291.35) * mm, "end": v(-194.8, -291.32) * mm});
            skLineSegment(sketch, "E1328", {"start": v(-194.8, -291.32) * mm, "end": v(-194.78, -295.72) * mm});
            skLineSegment(sketch, "E1329", {"start": v(-194.78, -295.72) * mm, "end": v(-207.28, -295.78) * mm});
            skLineSegment(sketch, "E1330", {"start": v(-207.28, -295.78) * mm, "end": v(-207.25, -301.78) * mm});
            skLineSegment(sketch, "E1331", {"start": v(-207.25, -301.78) * mm, "end": v(-219.75, -301.83) * mm});
            skLineSegment(sketch, "E1332", {"start": v(-219.75, -301.83) * mm, "end": v(-219.78, -295.83) * mm});
            skLineSegment(sketch, "E1333", {"start": v(-219.78, -295.83) * mm, "end": v(-229.78, -295.88) * mm});
            skLineSegment(sketch, "E1334", {"start": v(-229.78, -295.88) * mm, "end": v(-229.75, -301.88) * mm});
            skLineSegment(sketch, "E1335", {"start": v(-229.75, -301.88) * mm, "end": v(-239.75, -301.92) * mm});
            skLineSegment(sketch, "E1336", {"start": v(-239.75, -301.92) * mm, "end": v(-239.78, -295.92) * mm});
            skLineSegment(sketch, "E1337", {"start": v(-239.78, -295.92) * mm, "end": v(-249.78, -295.97) * mm});
            skLineSegment(sketch, "E1338", {"start": v(-249.78, -295.97) * mm, "end": v(-249.75, -301.97) * mm});
            skLineSegment(sketch, "E1339", {"start": v(-249.75, -301.97) * mm, "end": v(-259.75, -302) * mm});
            skLineSegment(sketch, "E1340", {"start": v(-259.75, -302) * mm, "end": v(-259.78, -296) * mm});
            skLineSegment(sketch, "E1341", {"start": v(-259.78, -296) * mm, "end": v(-269.77, -296.05) * mm});
            skLineSegment(sketch, "E1342", {"start": v(-269.77, -296.05) * mm, "end": v(-269.75, -302.05) * mm});
            skLineSegment(sketch, "E1343", {"start": v(-269.75, -302.05) * mm, "end": v(-279.75, -302.1) * mm});
            skLineSegment(sketch, "E1344", {"start": v(-279.75, -302.1) * mm, "end": v(-279.77, -296.1) * mm});
            skLineSegment(sketch, "E1345", {"start": v(-279.77, -296.1) * mm, "end": v(-289.77, -296.14) * mm});
            skLineSegment(sketch, "E1346", {"start": v(-289.77, -296.14) * mm, "end": v(-289.75, -302.14) * mm});
            skLineSegment(sketch, "E1347", {"start": v(-289.75, -302.14) * mm, "end": v(-299.75, -302.19) * mm});
            skLineSegment(sketch, "E1348", {"start": v(-299.75, -302.19) * mm, "end": v(-299.77, -296.19) * mm});
            skLineSegment(sketch, "E1349", {"start": v(-299.77, -296.19) * mm, "end": v(-309.77, -296.23) * mm});
            skLineSegment(sketch, "E1350", {"start": v(-309.77, -296.23) * mm, "end": v(-309.75, -302.23) * mm});
            skLineSegment(sketch, "E1351", {"start": v(-309.75, -302.23) * mm, "end": v(-319.75, -302.27) * mm});
            skLineSegment(sketch, "E1352", {"start": v(-319.75, -302.27) * mm, "end": v(-319.77, -296.27) * mm});
            skLineSegment(sketch, "E1353", {"start": v(-319.77, -296.27) * mm, "end": v(-329.77, -296.32) * mm});
            skLineSegment(sketch, "E1354", {"start": v(-329.77, -296.32) * mm, "end": v(-329.75, -302.32) * mm});
            skLineSegment(sketch, "E1355", {"start": v(-329.75, -302.32) * mm, "end": v(-339.75, -302.36) * mm});
            skLineSegment(sketch, "E1356", {"start": v(-339.75, -302.36) * mm, "end": v(-339.77, -296.36) * mm});
            skLineSegment(sketch, "E1357", {"start": v(-339.77, -296.36) * mm, "end": v(-349.77, -296.4) * mm});
            skLineSegment(sketch, "E1358", {"start": v(-349.77, -296.4) * mm, "end": v(-349.75, -302.4) * mm});
            skLineSegment(sketch, "E1359", {"start": v(-349.75, -302.4) * mm, "end": v(-359.75, -302.45) * mm});
            skLineSegment(sketch, "E1360", {"start": v(-359.75, -302.45) * mm, "end": v(-359.77, -296.45) * mm});
            skLineSegment(sketch, "E1361", {"start": v(-359.77, -296.45) * mm, "end": v(-369.77, -296.5) * mm});
            skLineSegment(sketch, "E1362", {"start": v(-369.77, -296.5) * mm, "end": v(-369.75, -302.5) * mm});
            skLineSegment(sketch, "E1363", {"start": v(-369.75, -302.5) * mm, "end": v(-379.75, -302.54) * mm});
            skLineSegment(sketch, "E1364", {"start": v(-379.75, -302.54) * mm, "end": v(-379.77, -296.54) * mm});
            skLineSegment(sketch, "E1365", {"start": v(-379.77, -296.54) * mm, "end": v(-389.77, -296.58) * mm});
            skLineSegment(sketch, "E1366", {"start": v(-389.77, -296.58) * mm, "end": v(-389.75, -302.58) * mm});
            skLineSegment(sketch, "E1367", {"start": v(-389.75, -302.58) * mm, "end": v(-399.75, -302.62) * mm});
            skLineSegment(sketch, "E1368", {"start": v(-399.75, -302.62) * mm, "end": v(-399.77, -296.62) * mm});
            skLineSegment(sketch, "E1369", {"start": v(-399.77, -296.62) * mm, "end": v(-409.77, -296.67) * mm});
            skLineSegment(sketch, "E1370", {"start": v(-409.77, -296.67) * mm, "end": v(-409.75, -302.67) * mm});
            skLineSegment(sketch, "E1371", {"start": v(-409.75, -302.67) * mm, "end": v(-419.75, -302.71) * mm});
            skLineSegment(sketch, "E1372", {"start": v(-419.75, -302.71) * mm, "end": v(-419.77, -296.71) * mm});
            skLineSegment(sketch, "E1373", {"start": v(-419.77, -296.71) * mm, "end": v(-429.77, -296.76) * mm});
            skLineSegment(sketch, "E1374", {"start": v(-429.77, -296.76) * mm, "end": v(-429.75, -302.76) * mm});
            skLineSegment(sketch, "E1375", {"start": v(-429.75, -302.76) * mm, "end": v(-439.75, -302.8) * mm});
            skLineSegment(sketch, "E1376", {"start": v(-439.75, -302.8) * mm, "end": v(-439.77, -296.8) * mm});
            skLineSegment(sketch, "E1377", {"start": v(-439.77, -296.8) * mm, "end": v(-449.77, -296.84) * mm});
            skLineSegment(sketch, "E1378", {"start": v(-449.77, -296.84) * mm, "end": v(-449.75, -302.84) * mm});
            skLineSegment(sketch, "E1379", {"start": v(-449.75, -302.84) * mm, "end": v(-459.75, -302.89) * mm});
            skLineSegment(sketch, "E1380", {"start": v(-459.75, -302.89) * mm, "end": v(-459.77, -296.89) * mm});
            skLineSegment(sketch, "E1381", {"start": v(-459.77, -296.89) * mm, "end": v(-469.77, -296.93) * mm});
            skLineSegment(sketch, "E1382", {"start": v(-469.77, -296.93) * mm, "end": v(-469.75, -302.93) * mm});
            skLineSegment(sketch, "E1383", {"start": v(-469.75, -302.93) * mm, "end": v(-479.75, -302.98) * mm});
            skLineSegment(sketch, "E1384", {"start": v(-479.75, -302.98) * mm, "end": v(-479.77, -296.98) * mm});
            skLineSegment(sketch, "E1385", {"start": v(-479.77, -296.98) * mm, "end": v(-489.77, -297.02) * mm});
            skLineSegment(sketch, "E1386", {"start": v(-489.77, -297.02) * mm, "end": v(-489.75, -303.02) * mm});
            skLineSegment(sketch, "E1387", {"start": v(-489.75, -303.02) * mm, "end": v(-499.75, -303.06) * mm});
            skLineSegment(sketch, "E1388", {"start": v(-499.75, -303.06) * mm, "end": v(-499.77, -297.06) * mm});
            skLineSegment(sketch, "E1389", {"start": v(-499.77, -297.06) * mm, "end": v(-509.77, -297.1) * mm});
            skLineSegment(sketch, "E1390", {"start": v(-509.77, -297.1) * mm, "end": v(-509.75, -303.1) * mm});
            skLineSegment(sketch, "E1391", {"start": v(-509.75, -303.1) * mm, "end": v(-519.75, -303.15) * mm});
            skLineSegment(sketch, "E1392", {"start": v(-519.75, -303.15) * mm, "end": v(-519.77, -297.15) * mm});
            skLineSegment(sketch, "E1393", {"start": v(-519.77, -297.15) * mm, "end": v(-529.77, -297.2) * mm});
            skLineSegment(sketch, "E1394", {"start": v(-529.77, -297.2) * mm, "end": v(-529.75, -303.2) * mm});
            skLineSegment(sketch, "E1395", {"start": v(-529.75, -303.2) * mm, "end": v(-539.75, -303.24) * mm});
            skLineSegment(sketch, "E1396", {"start": v(-539.75, -303.24) * mm, "end": v(-539.77, -297.24) * mm});
            skLineSegment(sketch, "E1397", {"start": v(-539.77, -297.24) * mm, "end": v(-549.77, -297.28) * mm});
            skLineSegment(sketch, "E1398", {"start": v(-549.77, -297.28) * mm, "end": v(-549.75, -303.28) * mm});
            skLineSegment(sketch, "E1399", {"start": v(-549.75, -303.28) * mm, "end": v(-559.75, -303.33) * mm});
            skLineSegment(sketch, "E1400", {"start": v(-559.75, -303.33) * mm, "end": v(-559.77, -297.33) * mm});
            skLineSegment(sketch, "E1401", {"start": v(-559.77, -297.33) * mm, "end": v(-569.77, -297.37) * mm});
            skLineSegment(sketch, "E1402", {"start": v(-569.77, -297.37) * mm, "end": v(-569.75, -303.37) * mm});
            skLineSegment(sketch, "E1403", {"start": v(-569.75, -303.37) * mm, "end": v(-579.75, -303.41) * mm});
            skLineSegment(sketch, "E1404", {"start": v(-579.75, -303.41) * mm, "end": v(-579.77, -297.41) * mm});
            skLineSegment(sketch, "E1405", {"start": v(-579.77, -297.41) * mm, "end": v(-589.77, -297.46) * mm});
            skLineSegment(sketch, "E1406", {"start": v(-589.77, -297.46) * mm, "end": v(-589.75, -303.46) * mm});
            skLineSegment(sketch, "E1407", {"start": v(-589.75, -303.46) * mm, "end": v(-599.75, -303.5) * mm});
            skLineSegment(sketch, "E1408", {"start": v(-599.75, -303.5) * mm, "end": v(-599.77, -297.5) * mm});
            skLineSegment(sketch, "E1409", {"start": v(-599.77, -297.5) * mm, "end": v(-609.77, -297.55) * mm});
            skLineSegment(sketch, "E1410", {"start": v(-609.77, -297.55) * mm, "end": v(-609.75, -303.55) * mm});
            skLineSegment(sketch, "E1411", {"start": v(-609.75, -303.55) * mm, "end": v(-619.75, -303.6) * mm});
            skLineSegment(sketch, "E1412", {"start": v(-619.75, -303.6) * mm, "end": v(-619.77, -297.6) * mm});
            skLineSegment(sketch, "E1413", {"start": v(-619.77, -297.6) * mm, "end": v(-629.77, -297.63) * mm});
            skLineSegment(sketch, "E1414", {"start": v(-629.77, -297.63) * mm, "end": v(-629.75, -303.63) * mm});
            skLineSegment(sketch, "E1415", {"start": v(-629.75, -303.63) * mm, "end": v(-639.75, -303.68) * mm});
            skLineSegment(sketch, "E1416", {"start": v(-639.75, -303.68) * mm, "end": v(-639.77, -297.68) * mm});
            skLineSegment(sketch, "E1417", {"start": v(-639.77, -297.68) * mm, "end": v(-649.77, -297.72) * mm});
            skLineSegment(sketch, "E1418", {"start": v(-649.77, -297.72) * mm, "end": v(-649.75, -303.72) * mm});
            skLineSegment(sketch, "E1419", {"start": v(-649.75, -303.72) * mm, "end": v(-659.75, -303.77) * mm});
            skLineSegment(sketch, "E1420", {"start": v(-659.75, -303.77) * mm, "end": v(-659.77, -297.77) * mm});
            skLineSegment(sketch, "E1421", {"start": v(-659.77, -297.77) * mm, "end": v(-669.77, -297.8) * mm});
            skLineSegment(sketch, "E1422", {"start": v(-669.77, -297.8) * mm, "end": v(-669.75, -303.8) * mm});
            skLineSegment(sketch, "E1423", {"start": v(-669.75, -303.8) * mm, "end": v(-682.24, -303.86) * mm});
            skLineSegment(sketch, "E1424", {"start": v(-682.24, -303.86) * mm, "end": v(-682.27, -297.86) * mm});
            skLineSegment(sketch, "E1425", {"start": v(-682.27, -297.86) * mm, "end": v(-694.77, -297.92) * mm});
            skLineSegment(sketch, "E1426", {"start": v(-694.77, -297.92) * mm, "end": v(-694.8, -293.52) * mm});
            skLineSegment(sketch, "E1427", {"start": v(-694.8, -293.52) * mm, "end": v(-688.8, -293.5) * mm});
            skLineSegment(sketch, "E1428", {"start": v(-688.8, -293.5) * mm, "end": v(-688.84, -283.1) * mm});
            skLineSegment(sketch, "E1429", {"start": v(-688.84, -283.1) * mm, "end": v(-694.84, -283.12) * mm});
            skLineSegment(sketch, "E1430", {"start": v(-694.84, -283.12) * mm, "end": v(-694.88, -272.72) * mm});
            skLineSegment(sketch, "E1431", {"start": v(-694.88, -272.72) * mm, "end": v(-688.88, -272.7) * mm});
            skLineSegment(sketch, "E1432", {"start": v(-688.88, -272.7) * mm, "end": v(-688.93, -262.3) * mm});
            skLineSegment(sketch, "E1433", {"start": v(-688.93, -262.3) * mm, "end": v(-694.93, -262.32) * mm});
            skLineSegment(sketch, "E1434", {"start": v(-694.93, -262.32) * mm, "end": v(-694.95, -257.92) * mm});
            skLineSegment(sketch, "E1435", {"start": v(-694.95, -257.92) * mm, "end": v(-682.45, -257.87) * mm});
            skLineSegment(sketch, "E1436", {"start": v(-682.45, -257.87) * mm, "end": v(-682.47, -251.87) * mm});
            skLineSegment(sketch, "E1437", {"start": v(-682.47, -251.87) * mm, "end": v(-669.97, -251.81) * mm});
            skLineSegment(sketch, "E1438", {"start": v(-669.97, -251.81) * mm, "end": v(-669.95, -257.81) * mm});
            skLineSegment(sketch, "E1439", {"start": v(-669.95, -257.81) * mm, "end": v(-659.95, -257.77) * mm});
            skLineSegment(sketch, "E1440", {"start": v(-659.95, -257.77) * mm, "end": v(-659.97, -251.77) * mm});
            skLineSegment(sketch, "E1441", {"start": v(-659.97, -251.77) * mm, "end": v(-649.97, -251.72) * mm});
            skLineSegment(sketch, "E1442", {"start": v(-649.97, -251.72) * mm, "end": v(-649.95, -257.72) * mm});
            skLineSegment(sketch, "E1443", {"start": v(-649.95, -257.72) * mm, "end": v(-639.95, -257.68) * mm});
            skLineSegment(sketch, "E1444", {"start": v(-639.95, -257.68) * mm, "end": v(-639.97, -251.68) * mm});
            skLineSegment(sketch, "E1445", {"start": v(-639.97, -251.68) * mm, "end": v(-629.97, -251.63) * mm});
            skLineSegment(sketch, "E1446", {"start": v(-629.97, -251.63) * mm, "end": v(-629.95, -257.63) * mm});
            skLineSegment(sketch, "E1447", {"start": v(-629.95, -257.63) * mm, "end": v(-619.95, -257.6) * mm});
            skLineSegment(sketch, "E1448", {"start": v(-619.95, -257.6) * mm, "end": v(-619.97, -251.6) * mm});
            skLineSegment(sketch, "E1449", {"start": v(-619.97, -251.6) * mm, "end": v(-609.97, -251.55) * mm});
            skLineSegment(sketch, "E1450", {"start": v(-609.97, -251.55) * mm, "end": v(-609.95, -257.55) * mm});
            skLineSegment(sketch, "E1451", {"start": v(-609.95, -257.55) * mm, "end": v(-599.95, -257.5) * mm});
            skLineSegment(sketch, "E1452", {"start": v(-599.95, -257.5) * mm, "end": v(-599.97, -251.5) * mm});
            skLineSegment(sketch, "E1453", {"start": v(-599.97, -251.5) * mm, "end": v(-589.97, -251.46) * mm});
            skLineSegment(sketch, "E1454", {"start": v(-589.97, -251.46) * mm, "end": v(-589.95, -257.46) * mm});
            skLineSegment(sketch, "E1455", {"start": v(-589.95, -257.46) * mm, "end": v(-579.95, -257.42) * mm});
            skLineSegment(sketch, "E1456", {"start": v(-579.95, -257.42) * mm, "end": v(-579.97, -251.42) * mm});
            skLineSegment(sketch, "E1457", {"start": v(-579.97, -251.42) * mm, "end": v(-569.97, -251.37) * mm});
            skLineSegment(sketch, "E1458", {"start": v(-569.97, -251.37) * mm, "end": v(-569.95, -257.37) * mm});
            skLineSegment(sketch, "E1459", {"start": v(-569.95, -257.37) * mm, "end": v(-559.95, -257.33) * mm});
            skLineSegment(sketch, "E1460", {"start": v(-559.95, -257.33) * mm, "end": v(-559.97, -251.33) * mm});
            skLineSegment(sketch, "E1461", {"start": v(-559.97, -251.33) * mm, "end": v(-549.97, -251.28) * mm});
            skLineSegment(sketch, "E1462", {"start": v(-549.97, -251.28) * mm, "end": v(-549.95, -257.28) * mm});
            skLineSegment(sketch, "E1463", {"start": v(-549.95, -257.28) * mm, "end": v(-539.95, -257.24) * mm});
            skLineSegment(sketch, "E1464", {"start": v(-539.95, -257.24) * mm, "end": v(-539.97, -251.24) * mm});
            skLineSegment(sketch, "E1465", {"start": v(-539.97, -251.24) * mm, "end": v(-529.97, -251.2) * mm});
            skLineSegment(sketch, "E1466", {"start": v(-529.97, -251.2) * mm, "end": v(-529.95, -257.2) * mm});
            skLineSegment(sketch, "E1467", {"start": v(-529.95, -257.2) * mm, "end": v(-519.95, -257.15) * mm});
            skLineSegment(sketch, "E1468", {"start": v(-519.95, -257.15) * mm, "end": v(-519.97, -251.15) * mm});
            skLineSegment(sketch, "E1469", {"start": v(-519.97, -251.15) * mm, "end": v(-509.97, -251.1) * mm});
            skLineSegment(sketch, "E1470", {"start": v(-509.97, -251.1) * mm, "end": v(-509.95, -257.1) * mm});
            skLineSegment(sketch, "E1471", {"start": v(-509.95, -257.1) * mm, "end": v(-499.95, -257.06) * mm});
            skLineSegment(sketch, "E1472", {"start": v(-499.95, -257.06) * mm, "end": v(-499.97, -251.06) * mm});
            skLineSegment(sketch, "E1473", {"start": v(-499.97, -251.06) * mm, "end": v(-489.97, -251.02) * mm});
            skLineSegment(sketch, "E1474", {"start": v(-489.97, -251.02) * mm, "end": v(-489.95, -257.02) * mm});
            skLineSegment(sketch, "E1475", {"start": v(-489.95, -257.02) * mm, "end": v(-479.95, -256.98) * mm});
            skLineSegment(sketch, "E1476", {"start": v(-479.95, -256.98) * mm, "end": v(-479.98, -250.98) * mm});
            skLineSegment(sketch, "E1477", {"start": v(-479.98, -250.98) * mm, "end": v(-469.98, -250.93) * mm});
            skLineSegment(sketch, "E1478", {"start": v(-469.98, -250.93) * mm, "end": v(-469.95, -256.93) * mm});
            skLineSegment(sketch, "E1479", {"start": v(-469.95, -256.93) * mm, "end": v(-459.95, -256.89) * mm});
            skLineSegment(sketch, "E1480", {"start": v(-459.95, -256.89) * mm, "end": v(-459.98, -250.89) * mm});
            skLineSegment(sketch, "E1481", {"start": v(-459.98, -250.89) * mm, "end": v(-449.98, -250.84) * mm});
            skLineSegment(sketch, "E1482", {"start": v(-449.98, -250.84) * mm, "end": v(-449.95, -256.84) * mm});
            skLineSegment(sketch, "E1483", {"start": v(-449.95, -256.84) * mm, "end": v(-439.95, -256.8) * mm});
            skLineSegment(sketch, "E1484", {"start": v(-439.95, -256.8) * mm, "end": v(-439.98, -250.8) * mm});
            skLineSegment(sketch, "E1485", {"start": v(-439.98, -250.8) * mm, "end": v(-429.98, -250.76) * mm});
            skLineSegment(sketch, "E1486", {"start": v(-429.98, -250.76) * mm, "end": v(-429.95, -256.76) * mm});
            skLineSegment(sketch, "E1487", {"start": v(-429.95, -256.76) * mm, "end": v(-419.95, -256.71) * mm});
            skLineSegment(sketch, "E1488", {"start": v(-419.95, -256.71) * mm, "end": v(-419.98, -250.71) * mm});
            skLineSegment(sketch, "E1489", {"start": v(-419.98, -250.71) * mm, "end": v(-409.98, -250.67) * mm});
            skLineSegment(sketch, "E1490", {"start": v(-409.98, -250.67) * mm, "end": v(-409.95, -256.67) * mm});
            skLineSegment(sketch, "E1491", {"start": v(-409.95, -256.67) * mm, "end": v(-399.95, -256.62) * mm});
            skLineSegment(sketch, "E1492", {"start": v(-399.95, -256.62) * mm, "end": v(-399.98, -250.62) * mm});
            skLineSegment(sketch, "E1493", {"start": v(-399.98, -250.62) * mm, "end": v(-389.98, -250.58) * mm});
            skLineSegment(sketch, "E1494", {"start": v(-389.98, -250.58) * mm, "end": v(-389.95, -256.58) * mm});
            skLineSegment(sketch, "E1495", {"start": v(-389.95, -256.58) * mm, "end": v(-379.95, -256.54) * mm});
            skLineSegment(sketch, "E1496", {"start": v(-379.95, -256.54) * mm, "end": v(-379.98, -250.54) * mm});
            skLineSegment(sketch, "E1497", {"start": v(-379.98, -250.54) * mm, "end": v(-369.98, -250.5) * mm});
            skLineSegment(sketch, "E1498", {"start": v(-369.98, -250.5) * mm, "end": v(-369.95, -256.5) * mm});
            skLineSegment(sketch, "E1499", {"start": v(-369.95, -256.5) * mm, "end": v(-359.95, -256.45) * mm});
            skLineSegment(sketch, "E1500", {"start": v(-359.95, -256.45) * mm, "end": v(-359.98, -250.45) * mm});
            skLineSegment(sketch, "E1501", {"start": v(-359.98, -250.45) * mm, "end": v(-349.98, -250.4) * mm});
            skLineSegment(sketch, "E1502", {"start": v(-349.98, -250.4) * mm, "end": v(-349.95, -256.4) * mm});
            skLineSegment(sketch, "E1503", {"start": v(-349.95, -256.4) * mm, "end": v(-339.95, -256.36) * mm});
            skLineSegment(sketch, "E1504", {"start": v(-339.95, -256.36) * mm, "end": v(-339.98, -250.36) * mm});
            skLineSegment(sketch, "E1505", {"start": v(-339.98, -250.36) * mm, "end": v(-329.98, -250.32) * mm});
            skLineSegment(sketch, "E1506", {"start": v(-329.98, -250.32) * mm, "end": v(-329.95, -256.32) * mm});
            skLineSegment(sketch, "E1507", {"start": v(-329.95, -256.32) * mm, "end": v(-319.95, -256.27) * mm});
            skLineSegment(sketch, "E1508", {"start": v(-319.95, -256.27) * mm, "end": v(-319.98, -250.27) * mm});
            skLineSegment(sketch, "E1509", {"start": v(-319.98, -250.27) * mm, "end": v(-309.98, -250.23) * mm});
            skLineSegment(sketch, "E1510", {"start": v(-309.98, -250.23) * mm, "end": v(-309.95, -256.23) * mm});
            skLineSegment(sketch, "E1511", {"start": v(-309.95, -256.23) * mm, "end": v(-299.95, -256.19) * mm});
            skLineSegment(sketch, "E1512", {"start": v(-299.95, -256.19) * mm, "end": v(-299.98, -250.19) * mm});
            skLineSegment(sketch, "E1513", {"start": v(-299.98, -250.19) * mm, "end": v(-289.98, -250.14) * mm});
            skLineSegment(sketch, "E1514", {"start": v(-289.98, -250.14) * mm, "end": v(-289.95, -256.14) * mm});
            skLineSegment(sketch, "E1515", {"start": v(-289.95, -256.14) * mm, "end": v(-279.95, -256.1) * mm});
            skLineSegment(sketch, "E1516", {"start": v(-279.95, -256.1) * mm, "end": v(-279.98, -250.1) * mm});
            skLineSegment(sketch, "E1517", {"start": v(-279.98, -250.1) * mm, "end": v(-269.98, -250.05) * mm});
            skLineSegment(sketch, "E1518", {"start": v(-269.98, -250.05) * mm, "end": v(-269.95, -256.05) * mm});
            skLineSegment(sketch, "E1519", {"start": v(-269.95, -256.05) * mm, "end": v(-259.95, -256.01) * mm});
            skLineSegment(sketch, "E1520", {"start": v(-259.95, -256.01) * mm, "end": v(-259.98, -250.01) * mm});
            skLineSegment(sketch, "E1521", {"start": v(-259.98, -250.01) * mm, "end": v(-249.98, -249.97) * mm});
            skLineSegment(sketch, "E1522", {"start": v(-249.98, -249.97) * mm, "end": v(-249.95, -255.97) * mm});
            skLineSegment(sketch, "E1523", {"start": v(-249.95, -255.97) * mm, "end": v(-239.95, -255.92) * mm});
            skLineSegment(sketch, "E1524", {"start": v(-239.95, -255.92) * mm, "end": v(-239.98, -249.92) * mm});
            skLineSegment(sketch, "E1525", {"start": v(-239.98, -249.92) * mm, "end": v(-229.98, -249.88) * mm});
            skLineSegment(sketch, "E1526", {"start": v(-229.98, -249.88) * mm, "end": v(-229.95, -255.88) * mm});
            skLineSegment(sketch, "E1527", {"start": v(-229.95, -255.88) * mm, "end": v(-219.95, -255.83) * mm});
            skLineSegment(sketch, "E1528", {"start": v(-219.95, -255.83) * mm, "end": v(-219.98, -249.83) * mm});
            skLineSegment(sketch, "E1529", {"start": v(-219.98, -249.83) * mm, "end": v(-207.48, -249.78) * mm});
            skLineSegment(sketch, "E1530", {"start": v(-207.48, -249.78) * mm, "end": v(-207.45, -255.78) * mm});
            skLineSegment(sketch, "E1531", {"start": v(-207.45, -255.78) * mm, "end": v(-194.95, -255.72) * mm});
            skLineSegment(sketch, "E1532", {"start": v(-694.95, -257.92) * mm, "end": v(-694.93, -262.32) * mm});
            skLineSegment(sketch, "E1533", {"start": v(-694.93, -262.32) * mm, "end": v(-700.93, -262.35) * mm});
            skLineSegment(sketch, "E1534", {"start": v(-700.93, -262.35) * mm, "end": v(-700.88, -272.75) * mm});
            skLineSegment(sketch, "E1535", {"start": v(-700.88, -272.75) * mm, "end": v(-694.88, -272.72) * mm});
            skLineSegment(sketch, "E1536", {"start": v(-694.88, -272.72) * mm, "end": v(-694.84, -283.12) * mm});
            skLineSegment(sketch, "E1537", {"start": v(-694.84, -283.12) * mm, "end": v(-700.84, -283.15) * mm});
            skLineSegment(sketch, "E1538", {"start": v(-700.84, -283.15) * mm, "end": v(-700.8, -293.55) * mm});
            skLineSegment(sketch, "E1539", {"start": v(-700.8, -293.55) * mm, "end": v(-694.8, -293.52) * mm});
            skLineSegment(sketch, "E1540", {"start": v(-694.8, -293.52) * mm, "end": v(-694.77, -297.92) * mm});
            skLineSegment(sketch, "E1541", {"start": v(-694.77, -297.92) * mm, "end": v(-707.27, -297.97) * mm});
            skLineSegment(sketch, "E1542", {"start": v(-707.27, -297.97) * mm, "end": v(-707.24, -303.97) * mm});
            skLineSegment(sketch, "E1543", {"start": v(-707.24, -303.97) * mm, "end": v(-719.74, -304.03) * mm});
            skLineSegment(sketch, "E1544", {"start": v(-719.74, -304.03) * mm, "end": v(-719.77, -298.03) * mm});
            skLineSegment(sketch, "E1545", {"start": v(-719.77, -298.03) * mm, "end": v(-729.77, -298.07) * mm});
            skLineSegment(sketch, "E1546", {"start": v(-729.77, -298.07) * mm, "end": v(-729.74, -304.07) * mm});
            skLineSegment(sketch, "E1547", {"start": v(-729.74, -304.07) * mm, "end": v(-739.74, -304.12) * mm});
            skLineSegment(sketch, "E1548", {"start": v(-739.74, -304.12) * mm, "end": v(-739.77, -298.12) * mm});
            skLineSegment(sketch, "E1549", {"start": v(-739.77, -298.12) * mm, "end": v(-749.77, -298.16) * mm});
            skLineSegment(sketch, "E1550", {"start": v(-749.77, -298.16) * mm, "end": v(-749.74, -304.16) * mm});
            skLineSegment(sketch, "E1551", {"start": v(-749.74, -304.16) * mm, "end": v(-759.74, -304.2) * mm});
            skLineSegment(sketch, "E1552", {"start": v(-759.74, -304.2) * mm, "end": v(-759.77, -298.2) * mm});
            skLineSegment(sketch, "E1553", {"start": v(-759.77, -298.2) * mm, "end": v(-769.77, -298.25) * mm});
            skLineSegment(sketch, "E1554", {"start": v(-769.77, -298.25) * mm, "end": v(-769.74, -304.25) * mm});
            skLineSegment(sketch, "E1555", {"start": v(-769.74, -304.25) * mm, "end": v(-779.74, -304.3) * mm});
            skLineSegment(sketch, "E1556", {"start": v(-779.74, -304.3) * mm, "end": v(-779.77, -298.3) * mm});
            skLineSegment(sketch, "E1557", {"start": v(-779.77, -298.3) * mm, "end": v(-789.77, -298.34) * mm});
            skLineSegment(sketch, "E1558", {"start": v(-789.77, -298.34) * mm, "end": v(-789.74, -304.34) * mm});
            skLineSegment(sketch, "E1559", {"start": v(-789.74, -304.34) * mm, "end": v(-799.74, -304.38) * mm});
            skLineSegment(sketch, "E1560", {"start": v(-799.74, -304.38) * mm, "end": v(-799.77, -298.38) * mm});
            skLineSegment(sketch, "E1561", {"start": v(-799.77, -298.38) * mm, "end": v(-809.77, -298.42) * mm});
            skLineSegment(sketch, "E1562", {"start": v(-809.77, -298.42) * mm, "end": v(-809.74, -304.42) * mm});
            skLineSegment(sketch, "E1563", {"start": v(-809.74, -304.42) * mm, "end": v(-819.74, -304.47) * mm});
            skLineSegment(sketch, "E1564", {"start": v(-819.74, -304.47) * mm, "end": v(-819.77, -298.47) * mm});
            skLineSegment(sketch, "E1565", {"start": v(-819.77, -298.47) * mm, "end": v(-829.77, -298.51) * mm});
            skLineSegment(sketch, "E1566", {"start": v(-829.77, -298.51) * mm, "end": v(-829.74, -304.51) * mm});
            skLineSegment(sketch, "E1567", {"start": v(-829.74, -304.51) * mm, "end": v(-839.74, -304.56) * mm});
            skLineSegment(sketch, "E1568", {"start": v(-839.74, -304.56) * mm, "end": v(-839.77, -298.56) * mm});
            skLineSegment(sketch, "E1569", {"start": v(-839.77, -298.56) * mm, "end": v(-849.77, -298.6) * mm});
            skLineSegment(sketch, "E1570", {"start": v(-849.77, -298.6) * mm, "end": v(-849.74, -304.6) * mm});
            skLineSegment(sketch, "E1571", {"start": v(-849.74, -304.6) * mm, "end": v(-859.74, -304.64) * mm});
            skLineSegment(sketch, "E1572", {"start": v(-859.74, -304.64) * mm, "end": v(-859.77, -298.64) * mm});
            skLineSegment(sketch, "E1573", {"start": v(-859.77, -298.64) * mm, "end": v(-869.77, -298.69) * mm});
            skLineSegment(sketch, "E1574", {"start": v(-869.77, -298.69) * mm, "end": v(-869.74, -304.69) * mm});
            skLineSegment(sketch, "E1575", {"start": v(-869.74, -304.69) * mm, "end": v(-879.74, -304.73) * mm});
            skLineSegment(sketch, "E1576", {"start": v(-879.74, -304.73) * mm, "end": v(-879.77, -298.73) * mm});
            skLineSegment(sketch, "E1577", {"start": v(-879.77, -298.73) * mm, "end": v(-889.77, -298.78) * mm});
            skLineSegment(sketch, "E1578", {"start": v(-889.77, -298.78) * mm, "end": v(-889.74, -304.78) * mm});
            skLineSegment(sketch, "E1579", {"start": v(-889.74, -304.78) * mm, "end": v(-899.74, -304.82) * mm});
            skLineSegment(sketch, "E1580", {"start": v(-899.74, -304.82) * mm, "end": v(-899.77, -298.82) * mm});
            skLineSegment(sketch, "E1581", {"start": v(-899.77, -298.82) * mm, "end": v(-909.77, -298.86) * mm});
            skLineSegment(sketch, "E1582", {"start": v(-909.77, -298.86) * mm, "end": v(-909.74, -304.86) * mm});
            skLineSegment(sketch, "E1583", {"start": v(-909.74, -304.86) * mm, "end": v(-919.74, -304.9) * mm});
            skLineSegment(sketch, "E1584", {"start": v(-919.74, -304.9) * mm, "end": v(-919.77, -298.9) * mm});
            skLineSegment(sketch, "E1585", {"start": v(-919.77, -298.9) * mm, "end": v(-929.77, -298.95) * mm});
            skLineSegment(sketch, "E1586", {"start": v(-929.77, -298.95) * mm, "end": v(-929.74, -304.95) * mm});
            skLineSegment(sketch, "E1587", {"start": v(-929.74, -304.95) * mm, "end": v(-939.74, -305) * mm});
            skLineSegment(sketch, "E1588", {"start": v(-939.74, -305) * mm, "end": v(-939.77, -299) * mm});
            skLineSegment(sketch, "E1589", {"start": v(-939.77, -299) * mm, "end": v(-949.77, -299.04) * mm});
            skLineSegment(sketch, "E1590", {"start": v(-949.77, -299.04) * mm, "end": v(-949.74, -305.04) * mm});
            skLineSegment(sketch, "E1591", {"start": v(-949.74, -305.04) * mm, "end": v(-959.74, -305.08) * mm});
            skLineSegment(sketch, "E1592", {"start": v(-959.74, -305.08) * mm, "end": v(-959.77, -299.08) * mm});
            skLineSegment(sketch, "E1593", {"start": v(-959.77, -299.08) * mm, "end": v(-969.77, -299.13) * mm});
            skLineSegment(sketch, "E1594", {"start": v(-969.77, -299.13) * mm, "end": v(-969.74, -305.13) * mm});
            skLineSegment(sketch, "E1595", {"start": v(-969.74, -305.13) * mm, "end": v(-979.74, -305.17) * mm});
            skLineSegment(sketch, "E1596", {"start": v(-979.74, -305.17) * mm, "end": v(-979.77, -299.17) * mm});
            skLineSegment(sketch, "E1597", {"start": v(-979.77, -299.17) * mm, "end": v(-989.77, -299.21) * mm});
            skLineSegment(sketch, "E1598", {"start": v(-989.77, -299.21) * mm, "end": v(-989.74, -305.21) * mm});
            skLineSegment(sketch, "E1599", {"start": v(-989.74, -305.21) * mm, "end": v(-999.74, -305.26) * mm});
            skLineSegment(sketch, "E1600", {"start": v(-999.74, -305.26) * mm, "end": v(-999.77, -299.26) * mm});
            skLineSegment(sketch, "E1601", {"start": v(-999.77, -299.26) * mm, "end": v(-1009.77, -299.3) * mm});
            skLineSegment(sketch, "E1602", {"start": v(-1009.77, -299.3) * mm, "end": v(-1009.74, -305.3) * mm});
            skLineSegment(sketch, "E1603", {"start": v(-1009.74, -305.3) * mm, "end": v(-1019.74, -305.35) * mm});
            skLineSegment(sketch, "E1604", {"start": v(-1019.74, -305.35) * mm, "end": v(-1019.77, -299.35) * mm});
            skLineSegment(sketch, "E1605", {"start": v(-1019.77, -299.35) * mm, "end": v(-1029.77, -299.4) * mm});
            skLineSegment(sketch, "E1606", {"start": v(-1029.77, -299.4) * mm, "end": v(-1029.74, -305.4) * mm});
            skLineSegment(sketch, "E1607", {"start": v(-1029.74, -305.4) * mm, "end": v(-1039.74, -305.43) * mm});
            skLineSegment(sketch, "E1608", {"start": v(-1039.74, -305.43) * mm, "end": v(-1039.77, -299.43) * mm});
            skLineSegment(sketch, "E1609", {"start": v(-1039.77, -299.43) * mm, "end": v(-1049.77, -299.48) * mm});
            skLineSegment(sketch, "E1610", {"start": v(-1049.77, -299.48) * mm, "end": v(-1049.74, -305.48) * mm});
            skLineSegment(sketch, "E1611", {"start": v(-1049.74, -305.48) * mm, "end": v(-1059.74, -305.52) * mm});
            skLineSegment(sketch, "E1612", {"start": v(-1059.74, -305.52) * mm, "end": v(-1059.77, -299.52) * mm});
            skLineSegment(sketch, "E1613", {"start": v(-1059.77, -299.52) * mm, "end": v(-1069.77, -299.57) * mm});
            skLineSegment(sketch, "E1614", {"start": v(-1069.77, -299.57) * mm, "end": v(-1069.74, -305.57) * mm});
            skLineSegment(sketch, "E1615", {"start": v(-1069.74, -305.57) * mm, "end": v(-1079.74, -305.61) * mm});
            skLineSegment(sketch, "E1616", {"start": v(-1079.74, -305.61) * mm, "end": v(-1079.77, -299.61) * mm});
            skLineSegment(sketch, "E1617", {"start": v(-1079.77, -299.61) * mm, "end": v(-1089.77, -299.65) * mm});
            skLineSegment(sketch, "E1618", {"start": v(-1089.77, -299.65) * mm, "end": v(-1089.74, -305.65) * mm});
            skLineSegment(sketch, "E1619", {"start": v(-1089.74, -305.65) * mm, "end": v(-1099.74, -305.7) * mm});
            skLineSegment(sketch, "E1620", {"start": v(-1099.74, -305.7) * mm, "end": v(-1099.77, -299.7) * mm});
            skLineSegment(sketch, "E1621", {"start": v(-1099.77, -299.7) * mm, "end": v(-1109.77, -299.74) * mm});
            skLineSegment(sketch, "E1622", {"start": v(-1109.77, -299.74) * mm, "end": v(-1109.74, -305.74) * mm});
            skLineSegment(sketch, "E1623", {"start": v(-1109.74, -305.74) * mm, "end": v(-1119.74, -305.79) * mm});
            skLineSegment(sketch, "E1624", {"start": v(-1119.74, -305.79) * mm, "end": v(-1119.77, -299.79) * mm});
            skLineSegment(sketch, "E1625", {"start": v(-1119.77, -299.79) * mm, "end": v(-1129.77, -299.83) * mm});
            skLineSegment(sketch, "E1626", {"start": v(-1129.77, -299.83) * mm, "end": v(-1129.74, -305.83) * mm});
            skLineSegment(sketch, "E1627", {"start": v(-1129.74, -305.83) * mm, "end": v(-1139.74, -305.87) * mm});
            skLineSegment(sketch, "E1628", {"start": v(-1139.74, -305.87) * mm, "end": v(-1139.77, -299.87) * mm});
            skLineSegment(sketch, "E1629", {"start": v(-1139.77, -299.87) * mm, "end": v(-1149.77, -299.92) * mm});
            skLineSegment(sketch, "E1630", {"start": v(-1149.77, -299.92) * mm, "end": v(-1149.74, -305.92) * mm});
            skLineSegment(sketch, "E1631", {"start": v(-1149.74, -305.92) * mm, "end": v(-1159.74, -305.96) * mm});
            skLineSegment(sketch, "E1632", {"start": v(-1159.74, -305.96) * mm, "end": v(-1159.77, -299.96) * mm});
            skLineSegment(sketch, "E1633", {"start": v(-1159.77, -299.96) * mm, "end": v(-1169.77, -300) * mm});
            skLineSegment(sketch, "E1634", {"start": v(-1169.77, -300) * mm, "end": v(-1169.74, -306) * mm});
            skLineSegment(sketch, "E1635", {"start": v(-1169.74, -306) * mm, "end": v(-1182.24, -306.06) * mm});
            skLineSegment(sketch, "E1636", {"start": v(-1182.24, -306.06) * mm, "end": v(-1182.27, -300.06) * mm});
            skLineSegment(sketch, "E1637", {"start": v(-1182.27, -300.06) * mm, "end": v(-1194.77, -300.12) * mm});
            skLineSegment(sketch, "E1638", {"start": v(-1194.77, -300.12) * mm, "end": v(-1194.79, -295.72) * mm});
            skLineSegment(sketch, "E1639", {"start": v(-1194.79, -295.72) * mm, "end": v(-1188.79, -295.69) * mm});
            skLineSegment(sketch, "E1640", {"start": v(-1188.79, -295.69) * mm, "end": v(-1188.83, -285.29) * mm});
            skLineSegment(sketch, "E1641", {"start": v(-1188.83, -285.29) * mm, "end": v(-1194.83, -285.32) * mm});
            skLineSegment(sketch, "E1642", {"start": v(-1194.83, -285.32) * mm, "end": v(-1194.88, -274.92) * mm});
            skLineSegment(sketch, "E1643", {"start": v(-1194.88, -274.92) * mm, "end": v(-1188.88, -274.89) * mm});
            skLineSegment(sketch, "E1644", {"start": v(-1188.88, -274.89) * mm, "end": v(-1188.92, -264.49) * mm});
            skLineSegment(sketch, "E1645", {"start": v(-1188.92, -264.49) * mm, "end": v(-1194.92, -264.52) * mm});
            skLineSegment(sketch, "E1646", {"start": v(-1194.92, -264.52) * mm, "end": v(-1194.94, -260.12) * mm});
            skLineSegment(sketch, "E1647", {"start": v(-1194.94, -260.12) * mm, "end": v(-1182.44, -260.06) * mm});
            skLineSegment(sketch, "E1648", {"start": v(-1182.44, -260.06) * mm, "end": v(-1182.47, -254.06) * mm});
            skLineSegment(sketch, "E1649", {"start": v(-1182.47, -254.06) * mm, "end": v(-1169.97, -254) * mm});
            skLineSegment(sketch, "E1650", {"start": v(-1169.97, -254) * mm, "end": v(-1169.94, -260) * mm});
            skLineSegment(sketch, "E1651", {"start": v(-1169.94, -260) * mm, "end": v(-1159.94, -259.96) * mm});
            skLineSegment(sketch, "E1652", {"start": v(-1159.94, -259.96) * mm, "end": v(-1159.97, -253.96) * mm});
            skLineSegment(sketch, "E1653", {"start": v(-1159.97, -253.96) * mm, "end": v(-1149.97, -253.92) * mm});
            skLineSegment(sketch, "E1654", {"start": v(-1149.97, -253.92) * mm, "end": v(-1149.94, -259.92) * mm});
            skLineSegment(sketch, "E1655", {"start": v(-1149.94, -259.92) * mm, "end": v(-1139.94, -259.87) * mm});
            skLineSegment(sketch, "E1656", {"start": v(-1139.94, -259.87) * mm, "end": v(-1139.97, -253.87) * mm});
            skLineSegment(sketch, "E1657", {"start": v(-1139.97, -253.87) * mm, "end": v(-1129.97, -253.83) * mm});
            skLineSegment(sketch, "E1658", {"start": v(-1129.97, -253.83) * mm, "end": v(-1129.94, -259.83) * mm});
            skLineSegment(sketch, "E1659", {"start": v(-1129.94, -259.83) * mm, "end": v(-1119.94, -259.79) * mm});
            skLineSegment(sketch, "E1660", {"start": v(-1119.94, -259.79) * mm, "end": v(-1119.97, -253.79) * mm});
            skLineSegment(sketch, "E1661", {"start": v(-1119.97, -253.79) * mm, "end": v(-1109.97, -253.74) * mm});
            skLineSegment(sketch, "E1662", {"start": v(-1109.97, -253.74) * mm, "end": v(-1109.94, -259.74) * mm});
            skLineSegment(sketch, "E1663", {"start": v(-1109.94, -259.74) * mm, "end": v(-1099.94, -259.7) * mm});
            skLineSegment(sketch, "E1664", {"start": v(-1099.94, -259.7) * mm, "end": v(-1099.97, -253.7) * mm});
            skLineSegment(sketch, "E1665", {"start": v(-1099.97, -253.7) * mm, "end": v(-1089.97, -253.65) * mm});
            skLineSegment(sketch, "E1666", {"start": v(-1089.97, -253.65) * mm, "end": v(-1089.94, -259.65) * mm});
            skLineSegment(sketch, "E1667", {"start": v(-1089.94, -259.65) * mm, "end": v(-1079.94, -259.61) * mm});
            skLineSegment(sketch, "E1668", {"start": v(-1079.94, -259.61) * mm, "end": v(-1079.97, -253.61) * mm});
            skLineSegment(sketch, "E1669", {"start": v(-1079.97, -253.61) * mm, "end": v(-1069.97, -253.57) * mm});
            skLineSegment(sketch, "E1670", {"start": v(-1069.97, -253.57) * mm, "end": v(-1069.94, -259.57) * mm});
            skLineSegment(sketch, "E1671", {"start": v(-1069.94, -259.57) * mm, "end": v(-1059.94, -259.52) * mm});
            skLineSegment(sketch, "E1672", {"start": v(-1059.94, -259.52) * mm, "end": v(-1059.97, -253.52) * mm});
            skLineSegment(sketch, "E1673", {"start": v(-1059.97, -253.52) * mm, "end": v(-1049.97, -253.48) * mm});
            skLineSegment(sketch, "E1674", {"start": v(-1049.97, -253.48) * mm, "end": v(-1049.94, -259.48) * mm});
            skLineSegment(sketch, "E1675", {"start": v(-1049.94, -259.48) * mm, "end": v(-1039.94, -259.43) * mm});
            skLineSegment(sketch, "E1676", {"start": v(-1039.94, -259.43) * mm, "end": v(-1039.97, -253.43) * mm});
            skLineSegment(sketch, "E1677", {"start": v(-1039.97, -253.43) * mm, "end": v(-1029.97, -253.4) * mm});
            skLineSegment(sketch, "E1678", {"start": v(-1029.97, -253.4) * mm, "end": v(-1029.94, -259.4) * mm});
            skLineSegment(sketch, "E1679", {"start": v(-1029.94, -259.4) * mm, "end": v(-1019.94, -259.35) * mm});
            skLineSegment(sketch, "E1680", {"start": v(-1019.94, -259.35) * mm, "end": v(-1019.97, -253.35) * mm});
            skLineSegment(sketch, "E1681", {"start": v(-1019.97, -253.35) * mm, "end": v(-1009.97, -253.3) * mm});
            skLineSegment(sketch, "E1682", {"start": v(-1009.97, -253.3) * mm, "end": v(-1009.94, -259.3) * mm});
            skLineSegment(sketch, "E1683", {"start": v(-1009.94, -259.3) * mm, "end": v(-999.94, -259.26) * mm});
            skLineSegment(sketch, "E1684", {"start": v(-999.94, -259.26) * mm, "end": v(-999.97, -253.26) * mm});
            skLineSegment(sketch, "E1685", {"start": v(-999.97, -253.26) * mm, "end": v(-989.97, -253.22) * mm});
            skLineSegment(sketch, "E1686", {"start": v(-989.97, -253.22) * mm, "end": v(-989.94, -259.22) * mm});
            skLineSegment(sketch, "E1687", {"start": v(-989.94, -259.22) * mm, "end": v(-979.94, -259.17) * mm});
            skLineSegment(sketch, "E1688", {"start": v(-979.94, -259.17) * mm, "end": v(-979.97, -253.17) * mm});
            skLineSegment(sketch, "E1689", {"start": v(-979.97, -253.17) * mm, "end": v(-969.97, -253.13) * mm});
            skLineSegment(sketch, "E1690", {"start": v(-969.97, -253.13) * mm, "end": v(-969.94, -259.13) * mm});
            skLineSegment(sketch, "E1691", {"start": v(-969.94, -259.13) * mm, "end": v(-959.94, -259.08) * mm});
            skLineSegment(sketch, "E1692", {"start": v(-959.94, -259.08) * mm, "end": v(-959.97, -253.08) * mm});
            skLineSegment(sketch, "E1693", {"start": v(-959.97, -253.08) * mm, "end": v(-949.97, -253.04) * mm});
            skLineSegment(sketch, "E1694", {"start": v(-949.97, -253.04) * mm, "end": v(-949.94, -259.04) * mm});
            skLineSegment(sketch, "E1695", {"start": v(-949.94, -259.04) * mm, "end": v(-939.94, -259) * mm});
            skLineSegment(sketch, "E1696", {"start": v(-939.94, -259) * mm, "end": v(-939.97, -253) * mm});
            skLineSegment(sketch, "E1697", {"start": v(-939.97, -253) * mm, "end": v(-929.97, -252.95) * mm});
            skLineSegment(sketch, "E1698", {"start": v(-929.97, -252.95) * mm, "end": v(-929.94, -258.95) * mm});
            skLineSegment(sketch, "E1699", {"start": v(-929.94, -258.95) * mm, "end": v(-919.94, -258.9) * mm});
            skLineSegment(sketch, "E1700", {"start": v(-919.94, -258.9) * mm, "end": v(-919.97, -252.9) * mm});
            skLineSegment(sketch, "E1701", {"start": v(-919.97, -252.9) * mm, "end": v(-909.97, -252.86) * mm});
            skLineSegment(sketch, "E1702", {"start": v(-909.97, -252.86) * mm, "end": v(-909.94, -258.86) * mm});
            skLineSegment(sketch, "E1703", {"start": v(-909.94, -258.86) * mm, "end": v(-899.94, -258.82) * mm});
            skLineSegment(sketch, "E1704", {"start": v(-899.94, -258.82) * mm, "end": v(-899.97, -252.82) * mm});
            skLineSegment(sketch, "E1705", {"start": v(-899.97, -252.82) * mm, "end": v(-889.97, -252.78) * mm});
            skLineSegment(sketch, "E1706", {"start": v(-889.97, -252.78) * mm, "end": v(-889.94, -258.78) * mm});
            skLineSegment(sketch, "E1707", {"start": v(-889.94, -258.78) * mm, "end": v(-879.95, -258.73) * mm});
            skLineSegment(sketch, "E1708", {"start": v(-879.95, -258.73) * mm, "end": v(-879.97, -252.73) * mm});
            skLineSegment(sketch, "E1709", {"start": v(-879.97, -252.73) * mm, "end": v(-869.97, -252.69) * mm});
            skLineSegment(sketch, "E1710", {"start": v(-869.97, -252.69) * mm, "end": v(-869.95, -258.69) * mm});
            skLineSegment(sketch, "E1711", {"start": v(-869.95, -258.69) * mm, "end": v(-859.95, -258.64) * mm});
            skLineSegment(sketch, "E1712", {"start": v(-859.95, -258.64) * mm, "end": v(-859.97, -252.64) * mm});
            skLineSegment(sketch, "E1713", {"start": v(-859.97, -252.64) * mm, "end": v(-849.97, -252.6) * mm});
            skLineSegment(sketch, "E1714", {"start": v(-849.97, -252.6) * mm, "end": v(-849.95, -258.6) * mm});
            skLineSegment(sketch, "E1715", {"start": v(-849.95, -258.6) * mm, "end": v(-839.95, -258.56) * mm});
            skLineSegment(sketch, "E1716", {"start": v(-839.95, -258.56) * mm, "end": v(-839.97, -252.56) * mm});
            skLineSegment(sketch, "E1717", {"start": v(-839.97, -252.56) * mm, "end": v(-829.97, -252.51) * mm});
            skLineSegment(sketch, "E1718", {"start": v(-829.97, -252.51) * mm, "end": v(-829.95, -258.51) * mm});
            skLineSegment(sketch, "E1719", {"start": v(-829.95, -258.51) * mm, "end": v(-819.95, -258.47) * mm});
            skLineSegment(sketch, "E1720", {"start": v(-819.95, -258.47) * mm, "end": v(-819.97, -252.47) * mm});
            skLineSegment(sketch, "E1721", {"start": v(-819.97, -252.47) * mm, "end": v(-809.97, -252.43) * mm});
            skLineSegment(sketch, "E1722", {"start": v(-809.97, -252.43) * mm, "end": v(-809.95, -258.42) * mm});
            skLineSegment(sketch, "E1723", {"start": v(-809.95, -258.42) * mm, "end": v(-799.95, -258.38) * mm});
            skLineSegment(sketch, "E1724", {"start": v(-799.95, -258.38) * mm, "end": v(-799.97, -252.38) * mm});
            skLineSegment(sketch, "E1725", {"start": v(-799.97, -252.38) * mm, "end": v(-789.97, -252.34) * mm});
            skLineSegment(sketch, "E1726", {"start": v(-789.97, -252.34) * mm, "end": v(-789.95, -258.34) * mm});
            skLineSegment(sketch, "E1727", {"start": v(-789.95, -258.34) * mm, "end": v(-779.95, -258.3) * mm});
            skLineSegment(sketch, "E1728", {"start": v(-779.95, -258.3) * mm, "end": v(-779.97, -252.3) * mm});
            skLineSegment(sketch, "E1729", {"start": v(-779.97, -252.3) * mm, "end": v(-769.97, -252.25) * mm});
            skLineSegment(sketch, "E1730", {"start": v(-769.97, -252.25) * mm, "end": v(-769.95, -258.25) * mm});
            skLineSegment(sketch, "E1731", {"start": v(-769.95, -258.25) * mm, "end": v(-759.95, -258.2) * mm});
            skLineSegment(sketch, "E1732", {"start": v(-759.95, -258.2) * mm, "end": v(-759.97, -252.2) * mm});
            skLineSegment(sketch, "E1733", {"start": v(-759.97, -252.2) * mm, "end": v(-749.97, -252.16) * mm});
            skLineSegment(sketch, "E1734", {"start": v(-749.97, -252.16) * mm, "end": v(-749.95, -258.16) * mm});
            skLineSegment(sketch, "E1735", {"start": v(-749.95, -258.16) * mm, "end": v(-739.95, -258.12) * mm});
            skLineSegment(sketch, "E1736", {"start": v(-739.95, -258.12) * mm, "end": v(-739.97, -252.12) * mm});
            skLineSegment(sketch, "E1737", {"start": v(-739.97, -252.12) * mm, "end": v(-729.97, -252.07) * mm});
            skLineSegment(sketch, "E1738", {"start": v(-729.97, -252.07) * mm, "end": v(-729.95, -258.07) * mm});
            skLineSegment(sketch, "E1739", {"start": v(-729.95, -258.07) * mm, "end": v(-719.95, -258.03) * mm});
            skLineSegment(sketch, "E1740", {"start": v(-719.95, -258.03) * mm, "end": v(-719.97, -252.03) * mm});
            skLineSegment(sketch, "E1741", {"start": v(-719.97, -252.03) * mm, "end": v(-707.47, -251.97) * mm});
            skLineSegment(sketch, "E1742", {"start": v(-707.47, -251.97) * mm, "end": v(-707.45, -257.97) * mm});
            skLineSegment(sketch, "E1743", {"start": v(-707.45, -257.97) * mm, "end": v(-694.95, -257.92) * mm});
            skLineSegment(sketch, "E1744", {"start": v(-1189, -199.94) * mm, "end": v(-1178.75, -199.94) * mm});
            skLineSegment(sketch, "E1745", {"start": v(-1178.75, -199.94) * mm, "end": v(-1178.75, -193.94) * mm});
            skLineSegment(sketch, "E1746", {"start": v(-1178.75, -193.94) * mm, "end": v(-1162.5, -193.94) * mm});
            skLineSegment(sketch, "E1747", {"start": v(-1162.5, -193.94) * mm, "end": v(-1162.5, -199.94) * mm});
            skLineSegment(sketch, "E1748", {"start": v(-1162.5, -199.94) * mm, "end": v(-1152.5, -199.94) * mm});
            skLineSegment(sketch, "E1749", {"start": v(-1152.5, -199.94) * mm, "end": v(-1152.5, -193.94) * mm});
            skLineSegment(sketch, "E1750", {"start": v(-1152.5, -193.94) * mm, "end": v(-1142.5, -193.94) * mm});
            skLineSegment(sketch, "E1751", {"start": v(-1142.5, -193.94) * mm, "end": v(-1142.5, -199.94) * mm});
            skLineSegment(sketch, "E1752", {"start": v(-1142.5, -199.94) * mm, "end": v(-1132.5, -199.94) * mm});
            skLineSegment(sketch, "E1753", {"start": v(-1132.5, -199.94) * mm, "end": v(-1132.5, -193.94) * mm});
            skLineSegment(sketch, "E1754", {"start": v(-1132.5, -193.94) * mm, "end": v(-1122.5, -193.94) * mm});
            skLineSegment(sketch, "E1755", {"start": v(-1122.5, -193.94) * mm, "end": v(-1122.5, -199.94) * mm});
            skLineSegment(sketch, "E1756", {"start": v(-1122.5, -199.94) * mm, "end": v(-1112.5, -199.94) * mm});
            skLineSegment(sketch, "E1757", {"start": v(-1112.5, -199.94) * mm, "end": v(-1112.5, -193.94) * mm});
            skLineSegment(sketch, "E1758", {"start": v(-1112.5, -193.94) * mm, "end": v(-1102.5, -193.94) * mm});
            skLineSegment(sketch, "E1759", {"start": v(-1102.5, -193.94) * mm, "end": v(-1102.5, -199.94) * mm});
            skLineSegment(sketch, "E1760", {"start": v(-1102.5, -199.94) * mm, "end": v(-1092.5, -199.94) * mm});
            skLineSegment(sketch, "E1761", {"start": v(-1092.5, -199.94) * mm, "end": v(-1092.5, -193.94) * mm});
            skLineSegment(sketch, "E1762", {"start": v(-1092.5, -193.94) * mm, "end": v(-1082.5, -193.94) * mm});
            skLineSegment(sketch, "E1763", {"start": v(-1082.5, -193.94) * mm, "end": v(-1082.5, -199.94) * mm});
            skLineSegment(sketch, "E1764", {"start": v(-1082.5, -199.94) * mm, "end": v(-1072.5, -199.94) * mm});
            skLineSegment(sketch, "E1765", {"start": v(-1072.5, -199.94) * mm, "end": v(-1072.5, -193.94) * mm});
            skLineSegment(sketch, "E1766", {"start": v(-1072.5, -193.94) * mm, "end": v(-1062.5, -193.94) * mm});
            skLineSegment(sketch, "E1767", {"start": v(-1062.5, -193.94) * mm, "end": v(-1062.5, -199.94) * mm});
            skLineSegment(sketch, "E1768", {"start": v(-1062.5, -199.94) * mm, "end": v(-1052.5, -199.94) * mm});
            skLineSegment(sketch, "E1769", {"start": v(-1052.5, -199.94) * mm, "end": v(-1052.5, -193.94) * mm});
            skLineSegment(sketch, "E1770", {"start": v(-1052.5, -193.94) * mm, "end": v(-1042.5, -193.94) * mm});
            skLineSegment(sketch, "E1771", {"start": v(-1042.5, -193.94) * mm, "end": v(-1042.5, -199.94) * mm});
            skLineSegment(sketch, "E1772", {"start": v(-1042.5, -199.94) * mm, "end": v(-1032.5, -199.94) * mm});
            skLineSegment(sketch, "E1773", {"start": v(-1032.5, -199.94) * mm, "end": v(-1032.5, -193.94) * mm});
            skLineSegment(sketch, "E1774", {"start": v(-1032.5, -193.94) * mm, "end": v(-1022.5, -193.94) * mm});
            skLineSegment(sketch, "E1775", {"start": v(-1022.5, -193.94) * mm, "end": v(-1022.5, -199.94) * mm});
            skLineSegment(sketch, "E1776", {"start": v(-1022.5, -199.94) * mm, "end": v(-1012.5, -199.94) * mm});
            skLineSegment(sketch, "E1777", {"start": v(-1012.5, -199.94) * mm, "end": v(-1012.5, -193.94) * mm});
            skLineSegment(sketch, "E1778", {"start": v(-1012.5, -193.94) * mm, "end": v(-1002.5, -193.94) * mm});
            skLineSegment(sketch, "E1779", {"start": v(-1002.5, -193.94) * mm, "end": v(-1002.5, -199.94) * mm});
            skLineSegment(sketch, "E1780", {"start": v(-1002.5, -199.94) * mm, "end": v(-992.5, -199.94) * mm});
            skLineSegment(sketch, "E1781", {"start": v(-992.5, -199.94) * mm, "end": v(-992.5, -193.94) * mm});
            skLineSegment(sketch, "E1782", {"start": v(-992.5, -193.94) * mm, "end": v(-982.5, -193.94) * mm});
            skLineSegment(sketch, "E1783", {"start": v(-982.5, -193.94) * mm, "end": v(-982.5, -199.94) * mm});
            skLineSegment(sketch, "E1784", {"start": v(-982.5, -199.94) * mm, "end": v(-972.5, -199.94) * mm});
            skLineSegment(sketch, "E1785", {"start": v(-972.5, -199.94) * mm, "end": v(-972.5, -193.94) * mm});
            skLineSegment(sketch, "E1786", {"start": v(-972.5, -193.94) * mm, "end": v(-962.5, -193.94) * mm});
            skLineSegment(sketch, "E1787", {"start": v(-962.5, -193.94) * mm, "end": v(-962.5, -199.94) * mm});
            skLineSegment(sketch, "E1788", {"start": v(-962.5, -199.94) * mm, "end": v(-952.5, -199.94) * mm});
            skLineSegment(sketch, "E1789", {"start": v(-952.5, -199.94) * mm, "end": v(-952.5, -193.94) * mm});
            skLineSegment(sketch, "E1790", {"start": v(-952.5, -193.94) * mm, "end": v(-942.5, -193.94) * mm});
            skLineSegment(sketch, "E1791", {"start": v(-942.5, -193.94) * mm, "end": v(-942.5, -199.94) * mm});
            skLineSegment(sketch, "E1792", {"start": v(-942.5, -199.94) * mm, "end": v(-932.5, -199.94) * mm});
            skLineSegment(sketch, "E1793", {"start": v(-932.5, -199.94) * mm, "end": v(-932.5, -193.94) * mm});
            skLineSegment(sketch, "E1794", {"start": v(-932.5, -193.94) * mm, "end": v(-922.5, -193.94) * mm});
            skLineSegment(sketch, "E1795", {"start": v(-922.5, -193.94) * mm, "end": v(-922.5, -199.94) * mm});
            skLineSegment(sketch, "E1796", {"start": v(-922.5, -199.94) * mm, "end": v(-912.5, -199.94) * mm});
            skLineSegment(sketch, "E1797", {"start": v(-912.5, -199.94) * mm, "end": v(-912.5, -193.94) * mm});
            skLineSegment(sketch, "E1798", {"start": v(-912.5, -193.94) * mm, "end": v(-902.5, -193.94) * mm});
            skLineSegment(sketch, "E1799", {"start": v(-902.5, -193.94) * mm, "end": v(-902.5, -199.94) * mm});
            skLineSegment(sketch, "E1800", {"start": v(-902.5, -199.94) * mm, "end": v(-892.5, -199.94) * mm});
            skLineSegment(sketch, "E1801", {"start": v(-892.5, -199.94) * mm, "end": v(-892.5, -193.94) * mm});
            skLineSegment(sketch, "E1802", {"start": v(-892.5, -193.94) * mm, "end": v(-882.5, -193.94) * mm});
            skLineSegment(sketch, "E1803", {"start": v(-882.5, -193.94) * mm, "end": v(-882.5, -199.94) * mm});
            skLineSegment(sketch, "E1804", {"start": v(-882.5, -199.94) * mm, "end": v(-872.5, -199.94) * mm});
            skLineSegment(sketch, "E1805", {"start": v(-872.5, -199.94) * mm, "end": v(-872.5, -193.94) * mm});
            skLineSegment(sketch, "E1806", {"start": v(-872.5, -193.94) * mm, "end": v(-862.5, -193.94) * mm});
            skLineSegment(sketch, "E1807", {"start": v(-862.5, -193.94) * mm, "end": v(-862.5, -199.94) * mm});
            skLineSegment(sketch, "E1808", {"start": v(-862.5, -199.94) * mm, "end": v(-852.5, -199.94) * mm});
            skLineSegment(sketch, "E1809", {"start": v(-852.5, -199.94) * mm, "end": v(-852.5, -193.94) * mm});
            skLineSegment(sketch, "E1810", {"start": v(-852.5, -193.94) * mm, "end": v(-842.5, -193.94) * mm});
            skLineSegment(sketch, "E1811", {"start": v(-842.5, -193.94) * mm, "end": v(-842.5, -199.94) * mm});
            skLineSegment(sketch, "E1812", {"start": v(-842.5, -199.94) * mm, "end": v(-832.5, -199.94) * mm});
            skLineSegment(sketch, "E1813", {"start": v(-832.5, -199.94) * mm, "end": v(-832.5, -193.94) * mm});
            skLineSegment(sketch, "E1814", {"start": v(-832.5, -193.94) * mm, "end": v(-822.5, -193.94) * mm});
            skLineSegment(sketch, "E1815", {"start": v(-822.5, -193.94) * mm, "end": v(-822.5, -199.94) * mm});
            skLineSegment(sketch, "E1816", {"start": v(-822.5, -199.94) * mm, "end": v(-812.5, -199.94) * mm});
            skLineSegment(sketch, "E1817", {"start": v(-812.5, -199.94) * mm, "end": v(-812.5, -193.94) * mm});
            skLineSegment(sketch, "E1818", {"start": v(-812.5, -193.94) * mm, "end": v(-802.5, -193.94) * mm});
            skLineSegment(sketch, "E1819", {"start": v(-802.5, -193.94) * mm, "end": v(-802.5, -199.94) * mm});
            skLineSegment(sketch, "E1820", {"start": v(-802.5, -199.94) * mm, "end": v(-792.5, -199.94) * mm});
            skLineSegment(sketch, "E1821", {"start": v(-792.5, -199.94) * mm, "end": v(-792.5, -193.94) * mm});
            skLineSegment(sketch, "E1822", {"start": v(-792.5, -193.94) * mm, "end": v(-782.5, -193.94) * mm});
            skLineSegment(sketch, "E1823", {"start": v(-782.5, -193.94) * mm, "end": v(-782.5, -199.94) * mm});
            skLineSegment(sketch, "E1824", {"start": v(-782.5, -199.94) * mm, "end": v(-772.5, -199.94) * mm});
            skLineSegment(sketch, "E1825", {"start": v(-772.5, -199.94) * mm, "end": v(-772.5, -193.94) * mm});
            skLineSegment(sketch, "E1826", {"start": v(-772.5, -193.94) * mm, "end": v(-762.5, -193.94) * mm});
            skLineSegment(sketch, "E1827", {"start": v(-762.5, -193.94) * mm, "end": v(-762.5, -199.94) * mm});
            skLineSegment(sketch, "E1828", {"start": v(-762.5, -199.94) * mm, "end": v(-752.5, -199.94) * mm});
            skLineSegment(sketch, "E1829", {"start": v(-752.5, -199.94) * mm, "end": v(-752.5, -193.94) * mm});
            skLineSegment(sketch, "E1830", {"start": v(-752.5, -193.94) * mm, "end": v(-742.5, -193.94) * mm});
            skLineSegment(sketch, "E1831", {"start": v(-742.5, -193.94) * mm, "end": v(-742.5, -199.94) * mm});
            skLineSegment(sketch, "E1832", {"start": v(-742.5, -199.94) * mm, "end": v(-732.5, -199.94) * mm});
            skLineSegment(sketch, "E1833", {"start": v(-732.5, -199.94) * mm, "end": v(-732.5, -193.94) * mm});
            skLineSegment(sketch, "E1834", {"start": v(-732.5, -193.94) * mm, "end": v(-722.5, -193.94) * mm});
            skLineSegment(sketch, "E1835", {"start": v(-722.5, -193.94) * mm, "end": v(-722.5, -199.94) * mm});
            skLineSegment(sketch, "E1836", {"start": v(-722.5, -199.94) * mm, "end": v(-712.5, -199.94) * mm});
            skLineSegment(sketch, "E1837", {"start": v(-712.5, -199.94) * mm, "end": v(-712.5, -193.94) * mm});
            skLineSegment(sketch, "E1838", {"start": v(-712.5, -193.94) * mm, "end": v(-702.5, -193.94) * mm});
            skLineSegment(sketch, "E1839", {"start": v(-702.5, -193.94) * mm, "end": v(-702.5, -199.94) * mm});
            skLineSegment(sketch, "E1840", {"start": v(-702.5, -199.94) * mm, "end": v(-692.5, -199.94) * mm});
            skLineSegment(sketch, "E1841", {"start": v(-692.5, -199.94) * mm, "end": v(-692.5, -193.94) * mm});
            skLineSegment(sketch, "E1842", {"start": v(-692.5, -193.94) * mm, "end": v(-682.5, -193.94) * mm});
            skLineSegment(sketch, "E1843", {"start": v(-682.5, -193.94) * mm, "end": v(-682.5, -199.94) * mm});
            skLineSegment(sketch, "E1844", {"start": v(-682.5, -199.94) * mm, "end": v(-672.5, -199.94) * mm});
            skLineSegment(sketch, "E1845", {"start": v(-672.5, -199.94) * mm, "end": v(-672.5, -193.94) * mm});
            skLineSegment(sketch, "E1846", {"start": v(-672.5, -193.94) * mm, "end": v(-662.5, -193.94) * mm});
            skLineSegment(sketch, "E1847", {"start": v(-662.5, -193.94) * mm, "end": v(-662.5, -199.94) * mm});
            skLineSegment(sketch, "E1848", {"start": v(-662.5, -199.94) * mm, "end": v(-652.5, -199.94) * mm});
            skLineSegment(sketch, "E1849", {"start": v(-652.5, -199.94) * mm, "end": v(-652.5, -193.94) * mm});
            skLineSegment(sketch, "E1850", {"start": v(-652.5, -193.94) * mm, "end": v(-642.5, -193.94) * mm});
            skLineSegment(sketch, "E1851", {"start": v(-642.5, -193.94) * mm, "end": v(-642.5, -199.94) * mm});
            skLineSegment(sketch, "E1852", {"start": v(-642.5, -199.94) * mm, "end": v(-632.5, -199.94) * mm});
            skLineSegment(sketch, "E1853", {"start": v(-632.5, -199.94) * mm, "end": v(-632.5, -193.94) * mm});
            skLineSegment(sketch, "E1854", {"start": v(-632.5, -193.94) * mm, "end": v(-622.5, -193.94) * mm});
            skLineSegment(sketch, "E1855", {"start": v(-622.5, -193.94) * mm, "end": v(-622.5, -199.94) * mm});
            skLineSegment(sketch, "E1856", {"start": v(-622.5, -199.94) * mm, "end": v(-612.5, -199.94) * mm});
            skLineSegment(sketch, "E1857", {"start": v(-612.5, -199.94) * mm, "end": v(-612.5, -193.94) * mm});
            skLineSegment(sketch, "E1858", {"start": v(-612.5, -193.94) * mm, "end": v(-602.5, -193.94) * mm});
            skLineSegment(sketch, "E1859", {"start": v(-602.5, -193.94) * mm, "end": v(-602.5, -199.94) * mm});
            skLineSegment(sketch, "E1860", {"start": v(-602.5, -199.94) * mm, "end": v(-592.5, -199.94) * mm});
            skLineSegment(sketch, "E1861", {"start": v(-592.5, -199.94) * mm, "end": v(-592.5, -193.94) * mm});
            skLineSegment(sketch, "E1862", {"start": v(-592.5, -193.94) * mm, "end": v(-582.5, -193.94) * mm});
            skLineSegment(sketch, "E1863", {"start": v(-582.5, -193.94) * mm, "end": v(-582.5, -199.94) * mm});
            skLineSegment(sketch, "E1864", {"start": v(-582.5, -199.94) * mm, "end": v(-572.5, -199.94) * mm});
            skLineSegment(sketch, "E1865", {"start": v(-572.5, -199.94) * mm, "end": v(-572.5, -193.94) * mm});
            skLineSegment(sketch, "E1866", {"start": v(-572.5, -193.94) * mm, "end": v(-562.5, -193.94) * mm});
            skLineSegment(sketch, "E1867", {"start": v(-562.5, -193.94) * mm, "end": v(-562.5, -199.94) * mm});
            skLineSegment(sketch, "E1868", {"start": v(-562.5, -199.94) * mm, "end": v(-552.5, -199.94) * mm});
            skLineSegment(sketch, "E1869", {"start": v(-552.5, -199.94) * mm, "end": v(-552.5, -193.94) * mm});
            skLineSegment(sketch, "E1870", {"start": v(-552.5, -193.94) * mm, "end": v(-542.5, -193.94) * mm});
            skLineSegment(sketch, "E1871", {"start": v(-542.5, -193.94) * mm, "end": v(-542.5, -199.94) * mm});
            skLineSegment(sketch, "E1872", {"start": v(-542.5, -199.94) * mm, "end": v(-532.5, -199.94) * mm});
            skLineSegment(sketch, "E1873", {"start": v(-532.5, -199.94) * mm, "end": v(-532.5, -193.94) * mm});
            skLineSegment(sketch, "E1874", {"start": v(-532.5, -193.94) * mm, "end": v(-522.5, -193.94) * mm});
            skLineSegment(sketch, "E1875", {"start": v(-522.5, -193.94) * mm, "end": v(-522.5, -199.94) * mm});
            skLineSegment(sketch, "E1876", {"start": v(-522.5, -199.94) * mm, "end": v(-512.5, -199.94) * mm});
            skLineSegment(sketch, "E1877", {"start": v(-512.5, -199.94) * mm, "end": v(-512.5, -193.94) * mm});
            skLineSegment(sketch, "E1878", {"start": v(-512.5, -193.94) * mm, "end": v(-502.5, -193.94) * mm});
            skLineSegment(sketch, "E1879", {"start": v(-502.5, -193.94) * mm, "end": v(-502.5, -199.94) * mm});
            skLineSegment(sketch, "E1880", {"start": v(-502.5, -199.94) * mm, "end": v(-492.5, -199.94) * mm});
            skLineSegment(sketch, "E1881", {"start": v(-492.5, -199.94) * mm, "end": v(-492.5, -193.94) * mm});
            skLineSegment(sketch, "E1882", {"start": v(-492.5, -193.94) * mm, "end": v(-482.5, -193.94) * mm});
            skLineSegment(sketch, "E1883", {"start": v(-482.5, -193.94) * mm, "end": v(-482.5, -199.94) * mm});
            skLineSegment(sketch, "E1884", {"start": v(-482.5, -199.94) * mm, "end": v(-472.5, -199.94) * mm});
            skLineSegment(sketch, "E1885", {"start": v(-472.5, -199.94) * mm, "end": v(-472.5, -193.94) * mm});
            skLineSegment(sketch, "E1886", {"start": v(-472.5, -193.94) * mm, "end": v(-462.5, -193.94) * mm});
            skLineSegment(sketch, "E1887", {"start": v(-462.5, -193.94) * mm, "end": v(-462.5, -199.94) * mm});
            skLineSegment(sketch, "E1888", {"start": v(-462.5, -199.94) * mm, "end": v(-452.5, -199.94) * mm});
            skLineSegment(sketch, "E1889", {"start": v(-452.5, -199.94) * mm, "end": v(-452.5, -193.94) * mm});
            skLineSegment(sketch, "E1890", {"start": v(-452.5, -193.94) * mm, "end": v(-442.5, -193.94) * mm});
            skLineSegment(sketch, "E1891", {"start": v(-442.5, -193.94) * mm, "end": v(-442.5, -199.94) * mm});
            skLineSegment(sketch, "E1892", {"start": v(-442.5, -199.94) * mm, "end": v(-432.5, -199.94) * mm});
            skLineSegment(sketch, "E1893", {"start": v(-432.5, -199.94) * mm, "end": v(-432.5, -193.94) * mm});
            skLineSegment(sketch, "E1894", {"start": v(-432.5, -193.94) * mm, "end": v(-422.5, -193.94) * mm});
            skLineSegment(sketch, "E1895", {"start": v(-422.5, -193.94) * mm, "end": v(-422.5, -199.94) * mm});
            skLineSegment(sketch, "E1896", {"start": v(-422.5, -199.94) * mm, "end": v(-412.5, -199.94) * mm});
            skLineSegment(sketch, "E1897", {"start": v(-412.5, -199.94) * mm, "end": v(-412.5, -193.94) * mm});
            skLineSegment(sketch, "E1898", {"start": v(-412.5, -193.94) * mm, "end": v(-402.5, -193.94) * mm});
            skLineSegment(sketch, "E1899", {"start": v(-402.5, -193.94) * mm, "end": v(-402.5, -199.94) * mm});
            skLineSegment(sketch, "E1900", {"start": v(-402.5, -199.94) * mm, "end": v(-392.5, -199.94) * mm});
            skLineSegment(sketch, "E1901", {"start": v(-392.5, -199.94) * mm, "end": v(-392.5, -193.94) * mm});
            skLineSegment(sketch, "E1902", {"start": v(-392.5, -193.94) * mm, "end": v(-382.5, -193.94) * mm});
            skLineSegment(sketch, "E1903", {"start": v(-382.5, -193.94) * mm, "end": v(-382.5, -199.94) * mm});
            skLineSegment(sketch, "E1904", {"start": v(-382.5, -199.94) * mm, "end": v(-372.5, -199.94) * mm});
            skLineSegment(sketch, "E1905", {"start": v(-372.5, -199.94) * mm, "end": v(-372.5, -193.94) * mm});
            skLineSegment(sketch, "E1906", {"start": v(-372.5, -193.94) * mm, "end": v(-362.5, -193.94) * mm});
            skLineSegment(sketch, "E1907", {"start": v(-362.5, -193.94) * mm, "end": v(-362.5, -199.94) * mm});
            skLineSegment(sketch, "E1908", {"start": v(-362.5, -199.94) * mm, "end": v(-352.5, -199.94) * mm});
            skLineSegment(sketch, "E1909", {"start": v(-352.5, -199.94) * mm, "end": v(-352.5, -193.94) * mm});
            skLineSegment(sketch, "E1910", {"start": v(-352.5, -193.94) * mm, "end": v(-342.5, -193.94) * mm});
            skLineSegment(sketch, "E1911", {"start": v(-342.5, -193.94) * mm, "end": v(-342.5, -199.94) * mm});
            skLineSegment(sketch, "E1912", {"start": v(-342.5, -199.94) * mm, "end": v(-332.5, -199.94) * mm});
            skLineSegment(sketch, "E1913", {"start": v(-332.5, -199.94) * mm, "end": v(-332.5, -193.94) * mm});
            skLineSegment(sketch, "E1914", {"start": v(-332.5, -193.94) * mm, "end": v(-322.5, -193.94) * mm});
            skLineSegment(sketch, "E1915", {"start": v(-322.5, -193.94) * mm, "end": v(-322.5, -199.94) * mm});
            skLineSegment(sketch, "E1916", {"start": v(-322.5, -199.94) * mm, "end": v(-312.5, -199.94) * mm});
            skLineSegment(sketch, "E1917", {"start": v(-312.5, -199.94) * mm, "end": v(-312.5, -193.94) * mm});
            skLineSegment(sketch, "E1918", {"start": v(-312.5, -193.94) * mm, "end": v(-302.5, -193.94) * mm});
            skLineSegment(sketch, "E1919", {"start": v(-302.5, -193.94) * mm, "end": v(-302.5, -199.94) * mm});
            skLineSegment(sketch, "E1920", {"start": v(-302.5, -199.94) * mm, "end": v(-292.5, -199.94) * mm});
            skLineSegment(sketch, "E1921", {"start": v(-292.5, -199.94) * mm, "end": v(-292.5, -193.94) * mm});
            skLineSegment(sketch, "E1922", {"start": v(-292.5, -193.94) * mm, "end": v(-282.5, -193.94) * mm});
            skLineSegment(sketch, "E1923", {"start": v(-282.5, -193.94) * mm, "end": v(-282.5, -199.94) * mm});
            skLineSegment(sketch, "E1924", {"start": v(-282.5, -199.94) * mm, "end": v(-272.5, -199.94) * mm});
            skLineSegment(sketch, "E1925", {"start": v(-272.5, -199.94) * mm, "end": v(-272.5, -193.94) * mm});
            skLineSegment(sketch, "E1926", {"start": v(-272.5, -193.94) * mm, "end": v(-262.5, -193.94) * mm});
            skLineSegment(sketch, "E1927", {"start": v(-262.5, -193.94) * mm, "end": v(-262.5, -199.94) * mm});
            skLineSegment(sketch, "E1928", {"start": v(-262.5, -199.94) * mm, "end": v(-252.5, -199.94) * mm});
            skLineSegment(sketch, "E1929", {"start": v(-252.5, -199.94) * mm, "end": v(-252.5, -193.94) * mm});
            skLineSegment(sketch, "E1930", {"start": v(-252.5, -193.94) * mm, "end": v(-242.5, -193.94) * mm});
            skLineSegment(sketch, "E1931", {"start": v(-242.5, -193.94) * mm, "end": v(-242.5, -199.94) * mm});
            skLineSegment(sketch, "E1932", {"start": v(-242.5, -199.94) * mm, "end": v(-232.5, -199.94) * mm});
            skLineSegment(sketch, "E1933", {"start": v(-232.5, -199.94) * mm, "end": v(-232.5, -193.94) * mm});
            skLineSegment(sketch, "E1934", {"start": v(-232.5, -193.94) * mm, "end": v(-222.5, -193.94) * mm});
            skLineSegment(sketch, "E1935", {"start": v(-222.5, -193.94) * mm, "end": v(-222.5, -199.94) * mm});
            skLineSegment(sketch, "E1936", {"start": v(-222.5, -199.94) * mm, "end": v(-212.5, -199.94) * mm});
            skLineSegment(sketch, "E1937", {"start": v(-212.5, -199.94) * mm, "end": v(-212.5, -193.94) * mm});
            skLineSegment(sketch, "E1938", {"start": v(-212.5, -193.94) * mm, "end": v(-202.5, -193.94) * mm});
            skLineSegment(sketch, "E1939", {"start": v(-202.5, -193.94) * mm, "end": v(-202.5, -199.94) * mm});
            skLineSegment(sketch, "E1940", {"start": v(-202.5, -199.94) * mm, "end": v(-192.5, -199.94) * mm});
            skLineSegment(sketch, "E1941", {"start": v(-192.5, -199.94) * mm, "end": v(-192.5, -193.94) * mm});
            skLineSegment(sketch, "E1942", {"start": v(-192.5, -193.94) * mm, "end": v(-182.5, -193.94) * mm});
            skLineSegment(sketch, "E1943", {"start": v(-182.5, -193.94) * mm, "end": v(-182.5, -199.94) * mm});
            skLineSegment(sketch, "E1944", {"start": v(-182.5, -199.94) * mm, "end": v(-172.5, -199.94) * mm});
            skLineSegment(sketch, "E1945", {"start": v(-172.5, -199.94) * mm, "end": v(-172.5, -193.94) * mm});
            skLineSegment(sketch, "E1946", {"start": v(-172.5, -193.94) * mm, "end": v(-162.5, -193.94) * mm});
            skLineSegment(sketch, "E1947", {"start": v(-162.5, -193.94) * mm, "end": v(-162.5, -199.94) * mm});
            skLineSegment(sketch, "E1948", {"start": v(-162.5, -199.94) * mm, "end": v(-152.5, -199.94) * mm});
            skLineSegment(sketch, "E1949", {"start": v(-152.5, -199.94) * mm, "end": v(-152.5, -193.94) * mm});
            skLineSegment(sketch, "E1950", {"start": v(-152.5, -193.94) * mm, "end": v(-142.5, -193.94) * mm});
            skLineSegment(sketch, "E1951", {"start": v(-142.5, -193.94) * mm, "end": v(-142.5, -199.94) * mm});
            skLineSegment(sketch, "E1952", {"start": v(-142.5, -199.94) * mm, "end": v(-132.5, -199.94) * mm});
            skLineSegment(sketch, "E1953", {"start": v(-132.5, -199.94) * mm, "end": v(-132.5, -193.94) * mm});
            skLineSegment(sketch, "E1954", {"start": v(-132.5, -193.94) * mm, "end": v(-122.5, -193.94) * mm});
            skLineSegment(sketch, "E1955", {"start": v(-122.5, -193.94) * mm, "end": v(-122.5, -199.94) * mm});
            skLineSegment(sketch, "E1956", {"start": v(-122.5, -199.94) * mm, "end": v(-112.5, -199.94) * mm});
            skLineSegment(sketch, "E1957", {"start": v(-112.5, -199.94) * mm, "end": v(-112.5, -193.94) * mm});
            skLineSegment(sketch, "E1958", {"start": v(-112.5, -193.94) * mm, "end": v(-102.5, -193.94) * mm});
            skLineSegment(sketch, "E1959", {"start": v(-102.5, -193.94) * mm, "end": v(-102.5, -199.94) * mm});
            skLineSegment(sketch, "E1960", {"start": v(-102.5, -199.94) * mm, "end": v(-92.5, -199.94) * mm});
            skLineSegment(sketch, "E1961", {"start": v(-92.5, -199.94) * mm, "end": v(-92.5, -193.94) * mm});
            skLineSegment(sketch, "E1962", {"start": v(-92.5, -193.94) * mm, "end": v(-82.5, -193.94) * mm});
            skLineSegment(sketch, "E1963", {"start": v(-82.5, -193.94) * mm, "end": v(-82.5, -199.94) * mm});
            skLineSegment(sketch, "E1964", {"start": v(-82.5, -199.94) * mm, "end": v(-72.5, -199.94) * mm});
            skLineSegment(sketch, "E1965", {"start": v(-72.5, -199.94) * mm, "end": v(-72.5, -193.94) * mm});
            skLineSegment(sketch, "E1966", {"start": v(-72.5, -193.94) * mm, "end": v(-62.5, -193.94) * mm});
            skLineSegment(sketch, "E1967", {"start": v(-62.5, -193.94) * mm, "end": v(-62.5, -199.94) * mm});
            skLineSegment(sketch, "E1968", {"start": v(-62.5, -199.94) * mm, "end": v(-52.5, -199.94) * mm});
            skLineSegment(sketch, "E1969", {"start": v(-52.5, -199.94) * mm, "end": v(-52.5, -193.94) * mm});
            skLineSegment(sketch, "E1970", {"start": v(-52.5, -193.94) * mm, "end": v(-42.5, -193.94) * mm});
            skLineSegment(sketch, "E1971", {"start": v(-42.5, -193.94) * mm, "end": v(-42.5, -199.94) * mm});
            skLineSegment(sketch, "E1972", {"start": v(-42.5, -199.94) * mm, "end": v(-32.5, -199.94) * mm});
            skLineSegment(sketch, "E1973", {"start": v(-32.5, -199.94) * mm, "end": v(-32.5, -193.94) * mm});
            skLineSegment(sketch, "E1974", {"start": v(-32.5, -193.94) * mm, "end": v(-16.25, -193.94) * mm});
            skLineSegment(sketch, "E1975", {"start": v(-16.25, -193.94) * mm, "end": v(-16.25, -199.94) * mm});
            skLineSegment(sketch, "E1976", {"start": v(-16.25, -199.94) * mm, "end": v(-6, -199.94) * mm});
            skLineSegment(sketch, "E1977", {"start": v(-6, -199.94) * mm, "end": v(-6, -204.34) * mm});
            skLineSegment(sketch, "E1978", {"start": v(-6, -204.34) * mm, "end": v(0, -204.34) * mm});
            skLineSegment(sketch, "E1979", {"start": v(0, -204.34) * mm, "end": v(0, -214.74) * mm});
            skLineSegment(sketch, "E1980", {"start": v(0, -214.74) * mm, "end": v(-6, -214.74) * mm});
            skLineSegment(sketch, "E1981", {"start": v(-6, -214.74) * mm, "end": v(-6, -225.14) * mm});
            skLineSegment(sketch, "E1982", {"start": v(-6, -225.14) * mm, "end": v(0, -225.14) * mm});
            skLineSegment(sketch, "E1983", {"start": v(0, -225.14) * mm, "end": v(0, -235.54) * mm});
            skLineSegment(sketch, "E1984", {"start": v(0, -235.54) * mm, "end": v(-6, -235.54) * mm});
            skLineSegment(sketch, "E1985", {"start": v(-6, -235.54) * mm, "end": v(-6, -239.94) * mm});
            skLineSegment(sketch, "E1986", {"start": v(-6, -239.94) * mm, "end": v(-16.25, -239.94) * mm});
            skLineSegment(sketch, "E1987", {"start": v(-16.25, -239.94) * mm, "end": v(-16.25, -245.94) * mm});
            skLineSegment(sketch, "E1988", {"start": v(-16.25, -245.94) * mm, "end": v(-32.5, -245.94) * mm});
            skLineSegment(sketch, "E1989", {"start": v(-32.5, -245.94) * mm, "end": v(-32.5, -239.94) * mm});
            skLineSegment(sketch, "E1990", {"start": v(-32.5, -239.94) * mm, "end": v(-42.5, -239.94) * mm});
            skLineSegment(sketch, "E1991", {"start": v(-42.5, -239.94) * mm, "end": v(-42.5, -245.94) * mm});
            skLineSegment(sketch, "E1992", {"start": v(-42.5, -245.94) * mm, "end": v(-52.5, -245.94) * mm});
            skLineSegment(sketch, "E1993", {"start": v(-52.5, -245.94) * mm, "end": v(-52.5, -239.94) * mm});
            skLineSegment(sketch, "E1994", {"start": v(-52.5, -239.94) * mm, "end": v(-62.5, -239.94) * mm});
            skLineSegment(sketch, "E1995", {"start": v(-62.5, -239.94) * mm, "end": v(-62.5, -245.94) * mm});
            skLineSegment(sketch, "E1996", {"start": v(-62.5, -245.94) * mm, "end": v(-72.5, -245.94) * mm});
            skLineSegment(sketch, "E1997", {"start": v(-72.5, -245.94) * mm, "end": v(-72.5, -239.94) * mm});
            skLineSegment(sketch, "E1998", {"start": v(-72.5, -239.94) * mm, "end": v(-82.5, -239.94) * mm});
            skLineSegment(sketch, "E1999", {"start": v(-82.5, -239.94) * mm, "end": v(-82.5, -245.94) * mm});
            skLineSegment(sketch, "E2000", {"start": v(-82.5, -245.94) * mm, "end": v(-92.5, -245.94) * mm});
            skLineSegment(sketch, "E2001", {"start": v(-92.5, -245.94) * mm, "end": v(-92.5, -239.94) * mm});
            skLineSegment(sketch, "E2002", {"start": v(-92.5, -239.94) * mm, "end": v(-102.5, -239.94) * mm});
            skLineSegment(sketch, "E2003", {"start": v(-102.5, -239.94) * mm, "end": v(-102.5, -245.94) * mm});
            skLineSegment(sketch, "E2004", {"start": v(-102.5, -245.94) * mm, "end": v(-112.5, -245.94) * mm});
            skLineSegment(sketch, "E2005", {"start": v(-112.5, -245.94) * mm, "end": v(-112.5, -239.94) * mm});
            skLineSegment(sketch, "E2006", {"start": v(-112.5, -239.94) * mm, "end": v(-122.5, -239.94) * mm});
            skLineSegment(sketch, "E2007", {"start": v(-122.5, -239.94) * mm, "end": v(-122.5, -245.94) * mm});
            skLineSegment(sketch, "E2008", {"start": v(-122.5, -245.94) * mm, "end": v(-132.5, -245.94) * mm});
            skLineSegment(sketch, "E2009", {"start": v(-132.5, -245.94) * mm, "end": v(-132.5, -239.94) * mm});
            skLineSegment(sketch, "E2010", {"start": v(-132.5, -239.94) * mm, "end": v(-142.5, -239.94) * mm});
            skLineSegment(sketch, "E2011", {"start": v(-142.5, -239.94) * mm, "end": v(-142.5, -245.94) * mm});
            skLineSegment(sketch, "E2012", {"start": v(-142.5, -245.94) * mm, "end": v(-152.5, -245.94) * mm});
            skLineSegment(sketch, "E2013", {"start": v(-152.5, -245.94) * mm, "end": v(-152.5, -239.94) * mm});
            skLineSegment(sketch, "E2014", {"start": v(-152.5, -239.94) * mm, "end": v(-162.5, -239.94) * mm});
            skLineSegment(sketch, "E2015", {"start": v(-162.5, -239.94) * mm, "end": v(-162.5, -245.94) * mm});
            skLineSegment(sketch, "E2016", {"start": v(-162.5, -245.94) * mm, "end": v(-172.5, -245.94) * mm});
            skLineSegment(sketch, "E2017", {"start": v(-172.5, -245.94) * mm, "end": v(-172.5, -239.94) * mm});
            skLineSegment(sketch, "E2018", {"start": v(-172.5, -239.94) * mm, "end": v(-182.5, -239.94) * mm});
            skLineSegment(sketch, "E2019", {"start": v(-182.5, -239.94) * mm, "end": v(-182.5, -245.94) * mm});
            skLineSegment(sketch, "E2020", {"start": v(-182.5, -245.94) * mm, "end": v(-192.5, -245.94) * mm});
            skLineSegment(sketch, "E2021", {"start": v(-192.5, -245.94) * mm, "end": v(-192.5, -239.94) * mm});
            skLineSegment(sketch, "E2022", {"start": v(-192.5, -239.94) * mm, "end": v(-202.5, -239.94) * mm});
            skLineSegment(sketch, "E2023", {"start": v(-202.5, -239.94) * mm, "end": v(-202.5, -245.94) * mm});
            skLineSegment(sketch, "E2024", {"start": v(-202.5, -245.94) * mm, "end": v(-212.5, -245.94) * mm});
            skLineSegment(sketch, "E2025", {"start": v(-212.5, -245.94) * mm, "end": v(-212.5, -239.94) * mm});
            skLineSegment(sketch, "E2026", {"start": v(-212.5, -239.94) * mm, "end": v(-222.5, -239.94) * mm});
            skLineSegment(sketch, "E2027", {"start": v(-222.5, -239.94) * mm, "end": v(-222.5, -245.94) * mm});
            skLineSegment(sketch, "E2028", {"start": v(-222.5, -245.94) * mm, "end": v(-232.5, -245.94) * mm});
            skLineSegment(sketch, "E2029", {"start": v(-232.5, -245.94) * mm, "end": v(-232.5, -239.94) * mm});
            skLineSegment(sketch, "E2030", {"start": v(-232.5, -239.94) * mm, "end": v(-242.5, -239.94) * mm});
            skLineSegment(sketch, "E2031", {"start": v(-242.5, -239.94) * mm, "end": v(-242.5, -245.94) * mm});
            skLineSegment(sketch, "E2032", {"start": v(-242.5, -245.94) * mm, "end": v(-252.5, -245.94) * mm});
            skLineSegment(sketch, "E2033", {"start": v(-252.5, -245.94) * mm, "end": v(-252.5, -239.94) * mm});
            skLineSegment(sketch, "E2034", {"start": v(-252.5, -239.94) * mm, "end": v(-262.5, -239.94) * mm});
            skLineSegment(sketch, "E2035", {"start": v(-262.5, -239.94) * mm, "end": v(-262.5, -245.94) * mm});
            skLineSegment(sketch, "E2036", {"start": v(-262.5, -245.94) * mm, "end": v(-272.5, -245.94) * mm});
            skLineSegment(sketch, "E2037", {"start": v(-272.5, -245.94) * mm, "end": v(-272.5, -239.94) * mm});
            skLineSegment(sketch, "E2038", {"start": v(-272.5, -239.94) * mm, "end": v(-282.5, -239.94) * mm});
            skLineSegment(sketch, "E2039", {"start": v(-282.5, -239.94) * mm, "end": v(-282.5, -245.94) * mm});
            skLineSegment(sketch, "E2040", {"start": v(-282.5, -245.94) * mm, "end": v(-292.5, -245.94) * mm});
            skLineSegment(sketch, "E2041", {"start": v(-292.5, -245.94) * mm, "end": v(-292.5, -239.94) * mm});
            skLineSegment(sketch, "E2042", {"start": v(-292.5, -239.94) * mm, "end": v(-302.5, -239.94) * mm});
            skLineSegment(sketch, "E2043", {"start": v(-302.5, -239.94) * mm, "end": v(-302.5, -245.94) * mm});
            skLineSegment(sketch, "E2044", {"start": v(-302.5, -245.94) * mm, "end": v(-312.5, -245.94) * mm});
            skLineSegment(sketch, "E2045", {"start": v(-312.5, -245.94) * mm, "end": v(-312.5, -239.94) * mm});
            skLineSegment(sketch, "E2046", {"start": v(-312.5, -239.94) * mm, "end": v(-322.5, -239.94) * mm});
            skLineSegment(sketch, "E2047", {"start": v(-322.5, -239.94) * mm, "end": v(-322.5, -245.94) * mm});
            skLineSegment(sketch, "E2048", {"start": v(-322.5, -245.94) * mm, "end": v(-332.5, -245.94) * mm});
            skLineSegment(sketch, "E2049", {"start": v(-332.5, -245.94) * mm, "end": v(-332.5, -239.94) * mm});
            skLineSegment(sketch, "E2050", {"start": v(-332.5, -239.94) * mm, "end": v(-342.5, -239.94) * mm});
            skLineSegment(sketch, "E2051", {"start": v(-342.5, -239.94) * mm, "end": v(-342.5, -245.94) * mm});
            skLineSegment(sketch, "E2052", {"start": v(-342.5, -245.94) * mm, "end": v(-352.5, -245.94) * mm});
            skLineSegment(sketch, "E2053", {"start": v(-352.5, -245.94) * mm, "end": v(-352.5, -239.94) * mm});
            skLineSegment(sketch, "E2054", {"start": v(-352.5, -239.94) * mm, "end": v(-362.5, -239.94) * mm});
            skLineSegment(sketch, "E2055", {"start": v(-362.5, -239.94) * mm, "end": v(-362.5, -245.94) * mm});
            skLineSegment(sketch, "E2056", {"start": v(-362.5, -245.94) * mm, "end": v(-372.5, -245.94) * mm});
            skLineSegment(sketch, "E2057", {"start": v(-372.5, -245.94) * mm, "end": v(-372.5, -239.94) * mm});
            skLineSegment(sketch, "E2058", {"start": v(-372.5, -239.94) * mm, "end": v(-382.5, -239.94) * mm});
            skLineSegment(sketch, "E2059", {"start": v(-382.5, -239.94) * mm, "end": v(-382.5, -245.94) * mm});
            skLineSegment(sketch, "E2060", {"start": v(-382.5, -245.94) * mm, "end": v(-392.5, -245.94) * mm});
            skLineSegment(sketch, "E2061", {"start": v(-392.5, -245.94) * mm, "end": v(-392.5, -239.94) * mm});
            skLineSegment(sketch, "E2062", {"start": v(-392.5, -239.94) * mm, "end": v(-402.5, -239.94) * mm});
            skLineSegment(sketch, "E2063", {"start": v(-402.5, -239.94) * mm, "end": v(-402.5, -245.94) * mm});
            skLineSegment(sketch, "E2064", {"start": v(-402.5, -245.94) * mm, "end": v(-412.5, -245.94) * mm});
            skLineSegment(sketch, "E2065", {"start": v(-412.5, -245.94) * mm, "end": v(-412.5, -239.94) * mm});
            skLineSegment(sketch, "E2066", {"start": v(-412.5, -239.94) * mm, "end": v(-422.5, -239.94) * mm});
            skLineSegment(sketch, "E2067", {"start": v(-422.5, -239.94) * mm, "end": v(-422.5, -245.94) * mm});
            skLineSegment(sketch, "E2068", {"start": v(-422.5, -245.94) * mm, "end": v(-432.5, -245.94) * mm});
            skLineSegment(sketch, "E2069", {"start": v(-432.5, -245.94) * mm, "end": v(-432.5, -239.94) * mm});
            skLineSegment(sketch, "E2070", {"start": v(-432.5, -239.94) * mm, "end": v(-442.5, -239.94) * mm});
            skLineSegment(sketch, "E2071", {"start": v(-442.5, -239.94) * mm, "end": v(-442.5, -245.94) * mm});
            skLineSegment(sketch, "E2072", {"start": v(-442.5, -245.94) * mm, "end": v(-452.5, -245.94) * mm});
            skLineSegment(sketch, "E2073", {"start": v(-452.5, -245.94) * mm, "end": v(-452.5, -239.94) * mm});
            skLineSegment(sketch, "E2074", {"start": v(-452.5, -239.94) * mm, "end": v(-462.5, -239.94) * mm});
            skLineSegment(sketch, "E2075", {"start": v(-462.5, -239.94) * mm, "end": v(-462.5, -245.94) * mm});
            skLineSegment(sketch, "E2076", {"start": v(-462.5, -245.94) * mm, "end": v(-472.5, -245.94) * mm});
            skLineSegment(sketch, "E2077", {"start": v(-472.5, -245.94) * mm, "end": v(-472.5, -239.94) * mm});
            skLineSegment(sketch, "E2078", {"start": v(-472.5, -239.94) * mm, "end": v(-482.5, -239.94) * mm});
            skLineSegment(sketch, "E2079", {"start": v(-482.5, -239.94) * mm, "end": v(-482.5, -245.94) * mm});
            skLineSegment(sketch, "E2080", {"start": v(-482.5, -245.94) * mm, "end": v(-492.5, -245.94) * mm});
            skLineSegment(sketch, "E2081", {"start": v(-492.5, -245.94) * mm, "end": v(-492.5, -239.94) * mm});
            skLineSegment(sketch, "E2082", {"start": v(-492.5, -239.94) * mm, "end": v(-502.5, -239.94) * mm});
            skLineSegment(sketch, "E2083", {"start": v(-502.5, -239.94) * mm, "end": v(-502.5, -245.94) * mm});
            skLineSegment(sketch, "E2084", {"start": v(-502.5, -245.94) * mm, "end": v(-512.5, -245.94) * mm});
            skLineSegment(sketch, "E2085", {"start": v(-512.5, -245.94) * mm, "end": v(-512.5, -239.94) * mm});
            skLineSegment(sketch, "E2086", {"start": v(-512.5, -239.94) * mm, "end": v(-522.5, -239.94) * mm});
            skLineSegment(sketch, "E2087", {"start": v(-522.5, -239.94) * mm, "end": v(-522.5, -245.94) * mm});
            skLineSegment(sketch, "E2088", {"start": v(-522.5, -245.94) * mm, "end": v(-532.5, -245.94) * mm});
            skLineSegment(sketch, "E2089", {"start": v(-532.5, -245.94) * mm, "end": v(-532.5, -239.94) * mm});
            skLineSegment(sketch, "E2090", {"start": v(-532.5, -239.94) * mm, "end": v(-542.5, -239.94) * mm});
            skLineSegment(sketch, "E2091", {"start": v(-542.5, -239.94) * mm, "end": v(-542.5, -245.94) * mm});
            skLineSegment(sketch, "E2092", {"start": v(-542.5, -245.94) * mm, "end": v(-552.5, -245.94) * mm});
            skLineSegment(sketch, "E2093", {"start": v(-552.5, -245.94) * mm, "end": v(-552.5, -239.94) * mm});
            skLineSegment(sketch, "E2094", {"start": v(-552.5, -239.94) * mm, "end": v(-562.5, -239.94) * mm});
            skLineSegment(sketch, "E2095", {"start": v(-562.5, -239.94) * mm, "end": v(-562.5, -245.94) * mm});
            skLineSegment(sketch, "E2096", {"start": v(-562.5, -245.94) * mm, "end": v(-572.5, -245.94) * mm});
            skLineSegment(sketch, "E2097", {"start": v(-572.5, -245.94) * mm, "end": v(-572.5, -239.94) * mm});
            skLineSegment(sketch, "E2098", {"start": v(-572.5, -239.94) * mm, "end": v(-582.5, -239.94) * mm});
            skLineSegment(sketch, "E2099", {"start": v(-582.5, -239.94) * mm, "end": v(-582.5, -245.94) * mm});
            skLineSegment(sketch, "E2100", {"start": v(-582.5, -245.94) * mm, "end": v(-592.5, -245.94) * mm});
            skLineSegment(sketch, "E2101", {"start": v(-592.5, -245.94) * mm, "end": v(-592.5, -239.94) * mm});
            skLineSegment(sketch, "E2102", {"start": v(-592.5, -239.94) * mm, "end": v(-602.5, -239.94) * mm});
            skLineSegment(sketch, "E2103", {"start": v(-602.5, -239.94) * mm, "end": v(-602.5, -245.94) * mm});
            skLineSegment(sketch, "E2104", {"start": v(-602.5, -245.94) * mm, "end": v(-612.5, -245.94) * mm});
            skLineSegment(sketch, "E2105", {"start": v(-612.5, -245.94) * mm, "end": v(-612.5, -239.94) * mm});
            skLineSegment(sketch, "E2106", {"start": v(-612.5, -239.94) * mm, "end": v(-622.5, -239.94) * mm});
            skLineSegment(sketch, "E2107", {"start": v(-622.5, -239.94) * mm, "end": v(-622.5, -245.94) * mm});
            skLineSegment(sketch, "E2108", {"start": v(-622.5, -245.94) * mm, "end": v(-632.5, -245.94) * mm});
            skLineSegment(sketch, "E2109", {"start": v(-632.5, -245.94) * mm, "end": v(-632.5, -239.94) * mm});
            skLineSegment(sketch, "E2110", {"start": v(-632.5, -239.94) * mm, "end": v(-642.5, -239.94) * mm});
            skLineSegment(sketch, "E2111", {"start": v(-642.5, -239.94) * mm, "end": v(-642.5, -245.94) * mm});
            skLineSegment(sketch, "E2112", {"start": v(-642.5, -245.94) * mm, "end": v(-652.5, -245.94) * mm});
            skLineSegment(sketch, "E2113", {"start": v(-652.5, -245.94) * mm, "end": v(-652.5, -239.94) * mm});
            skLineSegment(sketch, "E2114", {"start": v(-652.5, -239.94) * mm, "end": v(-662.5, -239.94) * mm});
            skLineSegment(sketch, "E2115", {"start": v(-662.5, -239.94) * mm, "end": v(-662.5, -245.94) * mm});
            skLineSegment(sketch, "E2116", {"start": v(-662.5, -245.94) * mm, "end": v(-672.5, -245.94) * mm});
            skLineSegment(sketch, "E2117", {"start": v(-672.5, -245.94) * mm, "end": v(-672.5, -239.94) * mm});
            skLineSegment(sketch, "E2118", {"start": v(-672.5, -239.94) * mm, "end": v(-682.5, -239.94) * mm});
            skLineSegment(sketch, "E2119", {"start": v(-682.5, -239.94) * mm, "end": v(-682.5, -245.94) * mm});
            skLineSegment(sketch, "E2120", {"start": v(-682.5, -245.94) * mm, "end": v(-692.5, -245.94) * mm});
            skLineSegment(sketch, "E2121", {"start": v(-692.5, -245.94) * mm, "end": v(-692.5, -239.94) * mm});
            skLineSegment(sketch, "E2122", {"start": v(-692.5, -239.94) * mm, "end": v(-702.5, -239.94) * mm});
            skLineSegment(sketch, "E2123", {"start": v(-702.5, -239.94) * mm, "end": v(-702.5, -245.94) * mm});
            skLineSegment(sketch, "E2124", {"start": v(-702.5, -245.94) * mm, "end": v(-712.5, -245.94) * mm});
            skLineSegment(sketch, "E2125", {"start": v(-712.5, -245.94) * mm, "end": v(-712.5, -239.94) * mm});
            skLineSegment(sketch, "E2126", {"start": v(-712.5, -239.94) * mm, "end": v(-722.5, -239.94) * mm});
            skLineSegment(sketch, "E2127", {"start": v(-722.5, -239.94) * mm, "end": v(-722.5, -245.94) * mm});
            skLineSegment(sketch, "E2128", {"start": v(-722.5, -245.94) * mm, "end": v(-732.5, -245.94) * mm});
            skLineSegment(sketch, "E2129", {"start": v(-732.5, -245.94) * mm, "end": v(-732.5, -239.94) * mm});
            skLineSegment(sketch, "E2130", {"start": v(-732.5, -239.94) * mm, "end": v(-742.5, -239.94) * mm});
            skLineSegment(sketch, "E2131", {"start": v(-742.5, -239.94) * mm, "end": v(-742.5, -245.94) * mm});
            skLineSegment(sketch, "E2132", {"start": v(-742.5, -245.94) * mm, "end": v(-752.5, -245.94) * mm});
            skLineSegment(sketch, "E2133", {"start": v(-752.5, -245.94) * mm, "end": v(-752.5, -239.94) * mm});
            skLineSegment(sketch, "E2134", {"start": v(-752.5, -239.94) * mm, "end": v(-762.5, -239.94) * mm});
            skLineSegment(sketch, "E2135", {"start": v(-762.5, -239.94) * mm, "end": v(-762.5, -245.94) * mm});
            skLineSegment(sketch, "E2136", {"start": v(-762.5, -245.94) * mm, "end": v(-772.5, -245.94) * mm});
            skLineSegment(sketch, "E2137", {"start": v(-772.5, -245.94) * mm, "end": v(-772.5, -239.94) * mm});
            skLineSegment(sketch, "E2138", {"start": v(-772.5, -239.94) * mm, "end": v(-782.5, -239.94) * mm});
            skLineSegment(sketch, "E2139", {"start": v(-782.5, -239.94) * mm, "end": v(-782.5, -245.94) * mm});
            skLineSegment(sketch, "E2140", {"start": v(-782.5, -245.94) * mm, "end": v(-792.5, -245.94) * mm});
            skLineSegment(sketch, "E2141", {"start": v(-792.5, -245.94) * mm, "end": v(-792.5, -239.94) * mm});
            skLineSegment(sketch, "E2142", {"start": v(-792.5, -239.94) * mm, "end": v(-802.5, -239.94) * mm});
            skLineSegment(sketch, "E2143", {"start": v(-802.5, -239.94) * mm, "end": v(-802.5, -245.94) * mm});
            skLineSegment(sketch, "E2144", {"start": v(-802.5, -245.94) * mm, "end": v(-812.5, -245.94) * mm});
            skLineSegment(sketch, "E2145", {"start": v(-812.5, -245.94) * mm, "end": v(-812.5, -239.94) * mm});
            skLineSegment(sketch, "E2146", {"start": v(-812.5, -239.94) * mm, "end": v(-822.5, -239.94) * mm});
            skLineSegment(sketch, "E2147", {"start": v(-822.5, -239.94) * mm, "end": v(-822.5, -245.94) * mm});
            skLineSegment(sketch, "E2148", {"start": v(-822.5, -245.94) * mm, "end": v(-832.5, -245.94) * mm});
            skLineSegment(sketch, "E2149", {"start": v(-832.5, -245.94) * mm, "end": v(-832.5, -239.94) * mm});
            skLineSegment(sketch, "E2150", {"start": v(-832.5, -239.94) * mm, "end": v(-842.5, -239.94) * mm});
            skLineSegment(sketch, "E2151", {"start": v(-842.5, -239.94) * mm, "end": v(-842.5, -245.94) * mm});
            skLineSegment(sketch, "E2152", {"start": v(-842.5, -245.94) * mm, "end": v(-852.5, -245.94) * mm});
            skLineSegment(sketch, "E2153", {"start": v(-852.5, -245.94) * mm, "end": v(-852.5, -239.94) * mm});
            skLineSegment(sketch, "E2154", {"start": v(-852.5, -239.94) * mm, "end": v(-862.5, -239.94) * mm});
            skLineSegment(sketch, "E2155", {"start": v(-862.5, -239.94) * mm, "end": v(-862.5, -245.94) * mm});
            skLineSegment(sketch, "E2156", {"start": v(-862.5, -245.94) * mm, "end": v(-872.5, -245.94) * mm});
            skLineSegment(sketch, "E2157", {"start": v(-872.5, -245.94) * mm, "end": v(-872.5, -239.94) * mm});
            skLineSegment(sketch, "E2158", {"start": v(-872.5, -239.94) * mm, "end": v(-882.5, -239.94) * mm});
            skLineSegment(sketch, "E2159", {"start": v(-882.5, -239.94) * mm, "end": v(-882.5, -245.94) * mm});
            skLineSegment(sketch, "E2160", {"start": v(-882.5, -245.94) * mm, "end": v(-892.5, -245.94) * mm});
            skLineSegment(sketch, "E2161", {"start": v(-892.5, -245.94) * mm, "end": v(-892.5, -239.94) * mm});
            skLineSegment(sketch, "E2162", {"start": v(-892.5, -239.94) * mm, "end": v(-902.5, -239.94) * mm});
            skLineSegment(sketch, "E2163", {"start": v(-902.5, -239.94) * mm, "end": v(-902.5, -245.94) * mm});
            skLineSegment(sketch, "E2164", {"start": v(-902.5, -245.94) * mm, "end": v(-912.5, -245.94) * mm});
            skLineSegment(sketch, "E2165", {"start": v(-912.5, -245.94) * mm, "end": v(-912.5, -239.94) * mm});
            skLineSegment(sketch, "E2166", {"start": v(-912.5, -239.94) * mm, "end": v(-922.5, -239.94) * mm});
            skLineSegment(sketch, "E2167", {"start": v(-922.5, -239.94) * mm, "end": v(-922.5, -245.94) * mm});
            skLineSegment(sketch, "E2168", {"start": v(-922.5, -245.94) * mm, "end": v(-932.5, -245.94) * mm});
            skLineSegment(sketch, "E2169", {"start": v(-932.5, -245.94) * mm, "end": v(-932.5, -239.94) * mm});
            skLineSegment(sketch, "E2170", {"start": v(-932.5, -239.94) * mm, "end": v(-942.5, -239.94) * mm});
            skLineSegment(sketch, "E2171", {"start": v(-942.5, -239.94) * mm, "end": v(-942.5, -245.94) * mm});
            skLineSegment(sketch, "E2172", {"start": v(-942.5, -245.94) * mm, "end": v(-952.5, -245.94) * mm});
            skLineSegment(sketch, "E2173", {"start": v(-952.5, -245.94) * mm, "end": v(-952.5, -239.94) * mm});
            skLineSegment(sketch, "E2174", {"start": v(-952.5, -239.94) * mm, "end": v(-962.5, -239.94) * mm});
            skLineSegment(sketch, "E2175", {"start": v(-962.5, -239.94) * mm, "end": v(-962.5, -245.94) * mm});
            skLineSegment(sketch, "E2176", {"start": v(-962.5, -245.94) * mm, "end": v(-972.5, -245.94) * mm});
            skLineSegment(sketch, "E2177", {"start": v(-972.5, -245.94) * mm, "end": v(-972.5, -239.94) * mm});
            skLineSegment(sketch, "E2178", {"start": v(-972.5, -239.94) * mm, "end": v(-982.5, -239.94) * mm});
            skLineSegment(sketch, "E2179", {"start": v(-982.5, -239.94) * mm, "end": v(-982.5, -245.94) * mm});
            skLineSegment(sketch, "E2180", {"start": v(-982.5, -245.94) * mm, "end": v(-992.5, -245.94) * mm});
            skLineSegment(sketch, "E2181", {"start": v(-992.5, -245.94) * mm, "end": v(-992.5, -239.94) * mm});
            skLineSegment(sketch, "E2182", {"start": v(-992.5, -239.94) * mm, "end": v(-1002.5, -239.94) * mm});
            skLineSegment(sketch, "E2183", {"start": v(-1002.5, -239.94) * mm, "end": v(-1002.5, -245.94) * mm});
            skLineSegment(sketch, "E2184", {"start": v(-1002.5, -245.94) * mm, "end": v(-1012.5, -245.94) * mm});
            skLineSegment(sketch, "E2185", {"start": v(-1012.5, -245.94) * mm, "end": v(-1012.5, -239.94) * mm});
            skLineSegment(sketch, "E2186", {"start": v(-1012.5, -239.94) * mm, "end": v(-1022.5, -239.94) * mm});
            skLineSegment(sketch, "E2187", {"start": v(-1022.5, -239.94) * mm, "end": v(-1022.5, -245.94) * mm});
            skLineSegment(sketch, "E2188", {"start": v(-1022.5, -245.94) * mm, "end": v(-1032.5, -245.94) * mm});
            skLineSegment(sketch, "E2189", {"start": v(-1032.5, -245.94) * mm, "end": v(-1032.5, -239.94) * mm});
            skLineSegment(sketch, "E2190", {"start": v(-1032.5, -239.94) * mm, "end": v(-1042.5, -239.94) * mm});
            skLineSegment(sketch, "E2191", {"start": v(-1042.5, -239.94) * mm, "end": v(-1042.5, -245.94) * mm});
            skLineSegment(sketch, "E2192", {"start": v(-1042.5, -245.94) * mm, "end": v(-1052.5, -245.94) * mm});
            skLineSegment(sketch, "E2193", {"start": v(-1052.5, -245.94) * mm, "end": v(-1052.5, -239.94) * mm});
            skLineSegment(sketch, "E2194", {"start": v(-1052.5, -239.94) * mm, "end": v(-1062.5, -239.94) * mm});
            skLineSegment(sketch, "E2195", {"start": v(-1062.5, -239.94) * mm, "end": v(-1062.5, -245.94) * mm});
            skLineSegment(sketch, "E2196", {"start": v(-1062.5, -245.94) * mm, "end": v(-1072.5, -245.94) * mm});
            skLineSegment(sketch, "E2197", {"start": v(-1072.5, -245.94) * mm, "end": v(-1072.5, -239.94) * mm});
            skLineSegment(sketch, "E2198", {"start": v(-1072.5, -239.94) * mm, "end": v(-1082.5, -239.94) * mm});
            skLineSegment(sketch, "E2199", {"start": v(-1082.5, -239.94) * mm, "end": v(-1082.5, -245.94) * mm});
            skLineSegment(sketch, "E2200", {"start": v(-1082.5, -245.94) * mm, "end": v(-1092.5, -245.94) * mm});
            skLineSegment(sketch, "E2201", {"start": v(-1092.5, -245.94) * mm, "end": v(-1092.5, -239.94) * mm});
            skLineSegment(sketch, "E2202", {"start": v(-1092.5, -239.94) * mm, "end": v(-1102.5, -239.94) * mm});
            skLineSegment(sketch, "E2203", {"start": v(-1102.5, -239.94) * mm, "end": v(-1102.5, -245.94) * mm});
            skLineSegment(sketch, "E2204", {"start": v(-1102.5, -245.94) * mm, "end": v(-1112.5, -245.94) * mm});
            skLineSegment(sketch, "E2205", {"start": v(-1112.5, -245.94) * mm, "end": v(-1112.5, -239.94) * mm});
            skLineSegment(sketch, "E2206", {"start": v(-1112.5, -239.94) * mm, "end": v(-1122.5, -239.94) * mm});
            skLineSegment(sketch, "E2207", {"start": v(-1122.5, -239.94) * mm, "end": v(-1122.5, -245.94) * mm});
            skLineSegment(sketch, "E2208", {"start": v(-1122.5, -245.94) * mm, "end": v(-1132.5, -245.94) * mm});
            skLineSegment(sketch, "E2209", {"start": v(-1132.5, -245.94) * mm, "end": v(-1132.5, -239.94) * mm});
            skLineSegment(sketch, "E2210", {"start": v(-1132.5, -239.94) * mm, "end": v(-1142.5, -239.94) * mm});
            skLineSegment(sketch, "E2211", {"start": v(-1142.5, -239.94) * mm, "end": v(-1142.5, -245.94) * mm});
            skLineSegment(sketch, "E2212", {"start": v(-1142.5, -245.94) * mm, "end": v(-1152.5, -245.94) * mm});
            skLineSegment(sketch, "E2213", {"start": v(-1152.5, -245.94) * mm, "end": v(-1152.5, -239.94) * mm});
            skLineSegment(sketch, "E2214", {"start": v(-1152.5, -239.94) * mm, "end": v(-1162.5, -239.94) * mm});
            skLineSegment(sketch, "E2215", {"start": v(-1162.5, -239.94) * mm, "end": v(-1162.5, -245.94) * mm});
            skLineSegment(sketch, "E2216", {"start": v(-1162.5, -245.94) * mm, "end": v(-1178.75, -245.94) * mm});
            skLineSegment(sketch, "E2217", {"start": v(-1178.75, -245.94) * mm, "end": v(-1178.75, -239.94) * mm});
            skLineSegment(sketch, "E2218", {"start": v(-1178.75, -239.94) * mm, "end": v(-1189, -239.94) * mm});
            skLineSegment(sketch, "E2219", {"start": v(-1189, -239.94) * mm, "end": v(-1189, -235.54) * mm});
            skLineSegment(sketch, "E2220", {"start": v(-1189, -235.54) * mm, "end": v(-1195, -235.54) * mm});
            skLineSegment(sketch, "E2221", {"start": v(-1195, -235.54) * mm, "end": v(-1195, -225.14) * mm});
            skLineSegment(sketch, "E2222", {"start": v(-1195, -225.14) * mm, "end": v(-1189, -225.14) * mm});
            skLineSegment(sketch, "E2223", {"start": v(-1189, -225.14) * mm, "end": v(-1189, -214.74) * mm});
            skLineSegment(sketch, "E2224", {"start": v(-1189, -214.74) * mm, "end": v(-1195, -214.74) * mm});
            skLineSegment(sketch, "E2225", {"start": v(-1195, -214.74) * mm, "end": v(-1195, -204.34) * mm});
            skLineSegment(sketch, "E2226", {"start": v(-1195, -204.34) * mm, "end": v(-1189, -204.34) * mm});
            skLineSegment(sketch, "E2227", {"start": v(-1189, -204.34) * mm, "end": v(-1189, -199.94) * mm});
            skLineSegment(sketch, "E2228", {"start": v(6, -199.94) * mm, "end": v(16.25, -199.94) * mm});
            skLineSegment(sketch, "E2229", {"start": v(16.25, -199.94) * mm, "end": v(16.25, -193.94) * mm});
            skLineSegment(sketch, "E2230", {"start": v(16.25, -193.94) * mm, "end": v(32.5, -193.94) * mm});
            skLineSegment(sketch, "E2231", {"start": v(32.5, -193.94) * mm, "end": v(32.5, -199.94) * mm});
            skLineSegment(sketch, "E2232", {"start": v(32.5, -199.94) * mm, "end": v(42.5, -199.94) * mm});
            skLineSegment(sketch, "E2233", {"start": v(42.5, -199.94) * mm, "end": v(42.5, -193.94) * mm});
            skLineSegment(sketch, "E2234", {"start": v(42.5, -193.94) * mm, "end": v(52.5, -193.94) * mm});
            skLineSegment(sketch, "E2235", {"start": v(52.5, -193.94) * mm, "end": v(52.5, -199.94) * mm});
            skLineSegment(sketch, "E2236", {"start": v(52.5, -199.94) * mm, "end": v(62.5, -199.94) * mm});
            skLineSegment(sketch, "E2237", {"start": v(62.5, -199.94) * mm, "end": v(62.5, -193.94) * mm});
            skLineSegment(sketch, "E2238", {"start": v(62.5, -193.94) * mm, "end": v(72.5, -193.94) * mm});
            skLineSegment(sketch, "E2239", {"start": v(72.5, -193.94) * mm, "end": v(72.5, -199.94) * mm});
            skLineSegment(sketch, "E2240", {"start": v(72.5, -199.94) * mm, "end": v(82.5, -199.94) * mm});
            skLineSegment(sketch, "E2241", {"start": v(82.5, -199.94) * mm, "end": v(82.5, -193.94) * mm});
            skLineSegment(sketch, "E2242", {"start": v(82.5, -193.94) * mm, "end": v(92.5, -193.94) * mm});
            skLineSegment(sketch, "E2243", {"start": v(92.5, -193.94) * mm, "end": v(92.5, -199.94) * mm});
            skLineSegment(sketch, "E2244", {"start": v(92.5, -199.94) * mm, "end": v(102.5, -199.94) * mm});
            skLineSegment(sketch, "E2245", {"start": v(102.5, -199.94) * mm, "end": v(102.5, -193.94) * mm});
            skLineSegment(sketch, "E2246", {"start": v(102.5, -193.94) * mm, "end": v(112.5, -193.94) * mm});
            skLineSegment(sketch, "E2247", {"start": v(112.5, -193.94) * mm, "end": v(112.5, -199.94) * mm});
            skLineSegment(sketch, "E2248", {"start": v(112.5, -199.94) * mm, "end": v(122.5, -199.94) * mm});
            skLineSegment(sketch, "E2249", {"start": v(122.5, -199.94) * mm, "end": v(122.5, -193.94) * mm});
            skLineSegment(sketch, "E2250", {"start": v(122.5, -193.94) * mm, "end": v(132.5, -193.94) * mm});
            skLineSegment(sketch, "E2251", {"start": v(132.5, -193.94) * mm, "end": v(132.5, -199.94) * mm});
            skLineSegment(sketch, "E2252", {"start": v(132.5, -199.94) * mm, "end": v(142.5, -199.94) * mm});
            skLineSegment(sketch, "E2253", {"start": v(142.5, -199.94) * mm, "end": v(142.5, -193.94) * mm});
            skLineSegment(sketch, "E2254", {"start": v(142.5, -193.94) * mm, "end": v(152.5, -193.94) * mm});
            skLineSegment(sketch, "E2255", {"start": v(152.5, -193.94) * mm, "end": v(152.5, -199.94) * mm});
            skLineSegment(sketch, "E2256", {"start": v(152.5, -199.94) * mm, "end": v(162.5, -199.94) * mm});
            skLineSegment(sketch, "E2257", {"start": v(162.5, -199.94) * mm, "end": v(162.5, -193.94) * mm});
            skLineSegment(sketch, "E2258", {"start": v(162.5, -193.94) * mm, "end": v(172.5, -193.94) * mm});
            skLineSegment(sketch, "E2259", {"start": v(172.5, -193.94) * mm, "end": v(172.5, -199.94) * mm});
            skLineSegment(sketch, "E2260", {"start": v(172.5, -199.94) * mm, "end": v(182.5, -199.94) * mm});
            skLineSegment(sketch, "E2261", {"start": v(182.5, -199.94) * mm, "end": v(182.5, -193.94) * mm});
            skLineSegment(sketch, "E2262", {"start": v(182.5, -193.94) * mm, "end": v(192.5, -193.94) * mm});
            skLineSegment(sketch, "E2263", {"start": v(192.5, -193.94) * mm, "end": v(192.5, -199.94) * mm});
            skLineSegment(sketch, "E2264", {"start": v(192.5, -199.94) * mm, "end": v(202.5, -199.94) * mm});
            skLineSegment(sketch, "E2265", {"start": v(202.5, -199.94) * mm, "end": v(202.5, -193.94) * mm});
            skLineSegment(sketch, "E2266", {"start": v(202.5, -193.94) * mm, "end": v(212.5, -193.94) * mm});
            skLineSegment(sketch, "E2267", {"start": v(212.5, -193.94) * mm, "end": v(212.5, -199.94) * mm});
            skLineSegment(sketch, "E2268", {"start": v(212.5, -199.94) * mm, "end": v(222.5, -199.94) * mm});
            skLineSegment(sketch, "E2269", {"start": v(222.5, -199.94) * mm, "end": v(222.5, -193.94) * mm});
            skLineSegment(sketch, "E2270", {"start": v(222.5, -193.94) * mm, "end": v(232.5, -193.94) * mm});
            skLineSegment(sketch, "E2271", {"start": v(232.5, -193.94) * mm, "end": v(232.5, -199.94) * mm});
            skLineSegment(sketch, "E2272", {"start": v(232.5, -199.94) * mm, "end": v(242.5, -199.94) * mm});
            skLineSegment(sketch, "E2273", {"start": v(242.5, -199.94) * mm, "end": v(242.5, -193.94) * mm});
            skLineSegment(sketch, "E2274", {"start": v(242.5, -193.94) * mm, "end": v(252.5, -193.94) * mm});
            skLineSegment(sketch, "E2275", {"start": v(252.5, -193.94) * mm, "end": v(252.5, -199.94) * mm});
            skLineSegment(sketch, "E2276", {"start": v(252.5, -199.94) * mm, "end": v(262.5, -199.94) * mm});
            skLineSegment(sketch, "E2277", {"start": v(262.5, -199.94) * mm, "end": v(262.5, -193.94) * mm});
            skLineSegment(sketch, "E2278", {"start": v(262.5, -193.94) * mm, "end": v(272.5, -193.94) * mm});
            skLineSegment(sketch, "E2279", {"start": v(272.5, -193.94) * mm, "end": v(272.5, -199.94) * mm});
            skLineSegment(sketch, "E2280", {"start": v(272.5, -199.94) * mm, "end": v(282.5, -199.94) * mm});
            skLineSegment(sketch, "E2281", {"start": v(282.5, -199.94) * mm, "end": v(282.5, -193.94) * mm});
            skLineSegment(sketch, "E2282", {"start": v(282.5, -193.94) * mm, "end": v(292.5, -193.94) * mm});
            skLineSegment(sketch, "E2283", {"start": v(292.5, -193.94) * mm, "end": v(292.5, -199.94) * mm});
            skLineSegment(sketch, "E2284", {"start": v(292.5, -199.94) * mm, "end": v(302.5, -199.94) * mm});
            skLineSegment(sketch, "E2285", {"start": v(302.5, -199.94) * mm, "end": v(302.5, -193.94) * mm});
            skLineSegment(sketch, "E2286", {"start": v(302.5, -193.94) * mm, "end": v(312.5, -193.94) * mm});
            skLineSegment(sketch, "E2287", {"start": v(312.5, -193.94) * mm, "end": v(312.5, -199.94) * mm});
            skLineSegment(sketch, "E2288", {"start": v(312.5, -199.94) * mm, "end": v(322.5, -199.94) * mm});
            skLineSegment(sketch, "E2289", {"start": v(322.5, -199.94) * mm, "end": v(322.5, -193.94) * mm});
            skLineSegment(sketch, "E2290", {"start": v(322.5, -193.94) * mm, "end": v(332.5, -193.94) * mm});
            skLineSegment(sketch, "E2291", {"start": v(332.5, -193.94) * mm, "end": v(332.5, -199.94) * mm});
            skLineSegment(sketch, "E2292", {"start": v(332.5, -199.94) * mm, "end": v(342.5, -199.94) * mm});
            skLineSegment(sketch, "E2293", {"start": v(342.5, -199.94) * mm, "end": v(342.5, -193.94) * mm});
            skLineSegment(sketch, "E2294", {"start": v(342.5, -193.94) * mm, "end": v(352.5, -193.94) * mm});
            skLineSegment(sketch, "E2295", {"start": v(352.5, -193.94) * mm, "end": v(352.5, -199.94) * mm});
            skLineSegment(sketch, "E2296", {"start": v(352.5, -199.94) * mm, "end": v(362.5, -199.94) * mm});
            skLineSegment(sketch, "E2297", {"start": v(362.5, -199.94) * mm, "end": v(362.5, -193.94) * mm});
            skLineSegment(sketch, "E2298", {"start": v(362.5, -193.94) * mm, "end": v(372.5, -193.94) * mm});
            skLineSegment(sketch, "E2299", {"start": v(372.5, -193.94) * mm, "end": v(372.5, -199.94) * mm});
            skLineSegment(sketch, "E2300", {"start": v(372.5, -199.94) * mm, "end": v(382.5, -199.94) * mm});
            skLineSegment(sketch, "E2301", {"start": v(382.5, -199.94) * mm, "end": v(382.5, -193.94) * mm});
            skLineSegment(sketch, "E2302", {"start": v(382.5, -193.94) * mm, "end": v(392.5, -193.94) * mm});
            skLineSegment(sketch, "E2303", {"start": v(392.5, -193.94) * mm, "end": v(392.5, -199.94) * mm});
            skLineSegment(sketch, "E2304", {"start": v(392.5, -199.94) * mm, "end": v(402.5, -199.94) * mm});
            skLineSegment(sketch, "E2305", {"start": v(402.5, -199.94) * mm, "end": v(402.5, -193.94) * mm});
            skLineSegment(sketch, "E2306", {"start": v(402.5, -193.94) * mm, "end": v(412.5, -193.94) * mm});
            skLineSegment(sketch, "E2307", {"start": v(412.5, -193.94) * mm, "end": v(412.5, -199.94) * mm});
            skLineSegment(sketch, "E2308", {"start": v(412.5, -199.94) * mm, "end": v(422.5, -199.94) * mm});
            skLineSegment(sketch, "E2309", {"start": v(422.5, -199.94) * mm, "end": v(422.5, -193.94) * mm});
            skLineSegment(sketch, "E2310", {"start": v(422.5, -193.94) * mm, "end": v(432.5, -193.94) * mm});
            skLineSegment(sketch, "E2311", {"start": v(432.5, -193.94) * mm, "end": v(432.5, -199.94) * mm});
            skLineSegment(sketch, "E2312", {"start": v(432.5, -199.94) * mm, "end": v(442.5, -199.94) * mm});
            skLineSegment(sketch, "E2313", {"start": v(442.5, -199.94) * mm, "end": v(442.5, -193.94) * mm});
            skLineSegment(sketch, "E2314", {"start": v(442.5, -193.94) * mm, "end": v(452.5, -193.94) * mm});
            skLineSegment(sketch, "E2315", {"start": v(452.5, -193.94) * mm, "end": v(452.5, -199.94) * mm});
            skLineSegment(sketch, "E2316", {"start": v(452.5, -199.94) * mm, "end": v(462.5, -199.94) * mm});
            skLineSegment(sketch, "E2317", {"start": v(462.5, -199.94) * mm, "end": v(462.5, -193.94) * mm});
            skLineSegment(sketch, "E2318", {"start": v(462.5, -193.94) * mm, "end": v(472.5, -193.94) * mm});
            skLineSegment(sketch, "E2319", {"start": v(472.5, -193.94) * mm, "end": v(472.5, -199.94) * mm});
            skLineSegment(sketch, "E2320", {"start": v(472.5, -199.94) * mm, "end": v(482.5, -199.94) * mm});
            skLineSegment(sketch, "E2321", {"start": v(482.5, -199.94) * mm, "end": v(482.5, -193.94) * mm});
            skLineSegment(sketch, "E2322", {"start": v(482.5, -193.94) * mm, "end": v(492.5, -193.94) * mm});
            skLineSegment(sketch, "E2323", {"start": v(492.5, -193.94) * mm, "end": v(492.5, -199.94) * mm});
            skLineSegment(sketch, "E2324", {"start": v(492.5, -199.94) * mm, "end": v(502.5, -199.94) * mm});
            skLineSegment(sketch, "E2325", {"start": v(502.5, -199.94) * mm, "end": v(502.5, -193.94) * mm});
            skLineSegment(sketch, "E2326", {"start": v(502.5, -193.94) * mm, "end": v(512.5, -193.94) * mm});
            skLineSegment(sketch, "E2327", {"start": v(512.5, -193.94) * mm, "end": v(512.5, -199.94) * mm});
            skLineSegment(sketch, "E2328", {"start": v(512.5, -199.94) * mm, "end": v(522.5, -199.94) * mm});
            skLineSegment(sketch, "E2329", {"start": v(522.5, -199.94) * mm, "end": v(522.5, -193.94) * mm});
            skLineSegment(sketch, "E2330", {"start": v(522.5, -193.94) * mm, "end": v(532.5, -193.94) * mm});
            skLineSegment(sketch, "E2331", {"start": v(532.5, -193.94) * mm, "end": v(532.5, -199.94) * mm});
            skLineSegment(sketch, "E2332", {"start": v(532.5, -199.94) * mm, "end": v(542.5, -199.94) * mm});
            skLineSegment(sketch, "E2333", {"start": v(542.5, -199.94) * mm, "end": v(542.5, -193.94) * mm});
            skLineSegment(sketch, "E2334", {"start": v(542.5, -193.94) * mm, "end": v(552.5, -193.94) * mm});
            skLineSegment(sketch, "E2335", {"start": v(552.5, -193.94) * mm, "end": v(552.5, -199.94) * mm});
            skLineSegment(sketch, "E2336", {"start": v(552.5, -199.94) * mm, "end": v(562.5, -199.94) * mm});
            skLineSegment(sketch, "E2337", {"start": v(562.5, -199.94) * mm, "end": v(562.5, -193.94) * mm});
            skLineSegment(sketch, "E2338", {"start": v(562.5, -193.94) * mm, "end": v(572.5, -193.94) * mm});
            skLineSegment(sketch, "E2339", {"start": v(572.5, -193.94) * mm, "end": v(572.5, -199.94) * mm});
            skLineSegment(sketch, "E2340", {"start": v(572.5, -199.94) * mm, "end": v(582.5, -199.94) * mm});
            skLineSegment(sketch, "E2341", {"start": v(582.5, -199.94) * mm, "end": v(582.5, -193.94) * mm});
            skLineSegment(sketch, "E2342", {"start": v(582.5, -193.94) * mm, "end": v(592.5, -193.94) * mm});
            skLineSegment(sketch, "E2343", {"start": v(592.5, -193.94) * mm, "end": v(592.5, -199.94) * mm});
            skLineSegment(sketch, "E2344", {"start": v(592.5, -199.94) * mm, "end": v(602.5, -199.94) * mm});
            skLineSegment(sketch, "E2345", {"start": v(602.5, -199.94) * mm, "end": v(602.5, -193.94) * mm});
            skLineSegment(sketch, "E2346", {"start": v(602.5, -193.94) * mm, "end": v(612.5, -193.94) * mm});
            skLineSegment(sketch, "E2347", {"start": v(612.5, -193.94) * mm, "end": v(612.5, -199.94) * mm});
            skLineSegment(sketch, "E2348", {"start": v(612.5, -199.94) * mm, "end": v(622.5, -199.94) * mm});
            skLineSegment(sketch, "E2349", {"start": v(622.5, -199.94) * mm, "end": v(622.5, -193.94) * mm});
            skLineSegment(sketch, "E2350", {"start": v(622.5, -193.94) * mm, "end": v(632.5, -193.94) * mm});
            skLineSegment(sketch, "E2351", {"start": v(632.5, -193.94) * mm, "end": v(632.5, -199.94) * mm});
            skLineSegment(sketch, "E2352", {"start": v(632.5, -199.94) * mm, "end": v(642.5, -199.94) * mm});
            skLineSegment(sketch, "E2353", {"start": v(642.5, -199.94) * mm, "end": v(642.5, -193.94) * mm});
            skLineSegment(sketch, "E2354", {"start": v(642.5, -193.94) * mm, "end": v(652.5, -193.94) * mm});
            skLineSegment(sketch, "E2355", {"start": v(652.5, -193.94) * mm, "end": v(652.5, -199.94) * mm});
            skLineSegment(sketch, "E2356", {"start": v(652.5, -199.94) * mm, "end": v(662.5, -199.94) * mm});
            skLineSegment(sketch, "E2357", {"start": v(662.5, -199.94) * mm, "end": v(662.5, -193.94) * mm});
            skLineSegment(sketch, "E2358", {"start": v(662.5, -193.94) * mm, "end": v(672.5, -193.94) * mm});
            skLineSegment(sketch, "E2359", {"start": v(672.5, -193.94) * mm, "end": v(672.5, -199.94) * mm});
            skLineSegment(sketch, "E2360", {"start": v(672.5, -199.94) * mm, "end": v(682.5, -199.94) * mm});
            skLineSegment(sketch, "E2361", {"start": v(682.5, -199.94) * mm, "end": v(682.5, -193.94) * mm});
            skLineSegment(sketch, "E2362", {"start": v(682.5, -193.94) * mm, "end": v(692.5, -193.94) * mm});
            skLineSegment(sketch, "E2363", {"start": v(692.5, -193.94) * mm, "end": v(692.5, -199.94) * mm});
            skLineSegment(sketch, "E2364", {"start": v(692.5, -199.94) * mm, "end": v(702.5, -199.94) * mm});
            skLineSegment(sketch, "E2365", {"start": v(702.5, -199.94) * mm, "end": v(702.5, -193.94) * mm});
            skLineSegment(sketch, "E2366", {"start": v(702.5, -193.94) * mm, "end": v(712.5, -193.94) * mm});
            skLineSegment(sketch, "E2367", {"start": v(712.5, -193.94) * mm, "end": v(712.5, -199.94) * mm});
            skLineSegment(sketch, "E2368", {"start": v(712.5, -199.94) * mm, "end": v(722.5, -199.94) * mm});
            skLineSegment(sketch, "E2369", {"start": v(722.5, -199.94) * mm, "end": v(722.5, -193.94) * mm});
            skLineSegment(sketch, "E2370", {"start": v(722.5, -193.94) * mm, "end": v(732.5, -193.94) * mm});
            skLineSegment(sketch, "E2371", {"start": v(732.5, -193.94) * mm, "end": v(732.5, -199.94) * mm});
            skLineSegment(sketch, "E2372", {"start": v(732.5, -199.94) * mm, "end": v(742.5, -199.94) * mm});
            skLineSegment(sketch, "E2373", {"start": v(742.5, -199.94) * mm, "end": v(742.5, -193.94) * mm});
            skLineSegment(sketch, "E2374", {"start": v(742.5, -193.94) * mm, "end": v(752.5, -193.94) * mm});
            skLineSegment(sketch, "E2375", {"start": v(752.5, -193.94) * mm, "end": v(752.5, -199.94) * mm});
            skLineSegment(sketch, "E2376", {"start": v(752.5, -199.94) * mm, "end": v(762.5, -199.94) * mm});
            skLineSegment(sketch, "E2377", {"start": v(762.5, -199.94) * mm, "end": v(762.5, -193.94) * mm});
            skLineSegment(sketch, "E2378", {"start": v(762.5, -193.94) * mm, "end": v(772.5, -193.94) * mm});
            skLineSegment(sketch, "E2379", {"start": v(772.5, -193.94) * mm, "end": v(772.5, -199.94) * mm});
            skLineSegment(sketch, "E2380", {"start": v(772.5, -199.94) * mm, "end": v(782.5, -199.94) * mm});
            skLineSegment(sketch, "E2381", {"start": v(782.5, -199.94) * mm, "end": v(782.5, -193.94) * mm});
            skLineSegment(sketch, "E2382", {"start": v(782.5, -193.94) * mm, "end": v(792.5, -193.94) * mm});
            skLineSegment(sketch, "E2383", {"start": v(792.5, -193.94) * mm, "end": v(792.5, -199.94) * mm});
            skLineSegment(sketch, "E2384", {"start": v(792.5, -199.94) * mm, "end": v(802.5, -199.94) * mm});
            skLineSegment(sketch, "E2385", {"start": v(802.5, -199.94) * mm, "end": v(802.5, -193.94) * mm});
            skLineSegment(sketch, "E2386", {"start": v(802.5, -193.94) * mm, "end": v(812.5, -193.94) * mm});
            skLineSegment(sketch, "E2387", {"start": v(812.5, -193.94) * mm, "end": v(812.5, -199.94) * mm});
            skLineSegment(sketch, "E2388", {"start": v(812.5, -199.94) * mm, "end": v(822.5, -199.94) * mm});
            skLineSegment(sketch, "E2389", {"start": v(822.5, -199.94) * mm, "end": v(822.5, -193.94) * mm});
            skLineSegment(sketch, "E2390", {"start": v(822.5, -193.94) * mm, "end": v(832.5, -193.94) * mm});
            skLineSegment(sketch, "E2391", {"start": v(832.5, -193.94) * mm, "end": v(832.5, -199.94) * mm});
            skLineSegment(sketch, "E2392", {"start": v(832.5, -199.94) * mm, "end": v(842.5, -199.94) * mm});
            skLineSegment(sketch, "E2393", {"start": v(842.5, -199.94) * mm, "end": v(842.5, -193.94) * mm});
            skLineSegment(sketch, "E2394", {"start": v(842.5, -193.94) * mm, "end": v(852.5, -193.94) * mm});
            skLineSegment(sketch, "E2395", {"start": v(852.5, -193.94) * mm, "end": v(852.5, -199.94) * mm});
            skLineSegment(sketch, "E2396", {"start": v(852.5, -199.94) * mm, "end": v(862.5, -199.94) * mm});
            skLineSegment(sketch, "E2397", {"start": v(862.5, -199.94) * mm, "end": v(862.5, -193.94) * mm});
            skLineSegment(sketch, "E2398", {"start": v(862.5, -193.94) * mm, "end": v(872.5, -193.94) * mm});
            skLineSegment(sketch, "E2399", {"start": v(872.5, -193.94) * mm, "end": v(872.5, -199.94) * mm});
            skLineSegment(sketch, "E2400", {"start": v(872.5, -199.94) * mm, "end": v(882.5, -199.94) * mm});
            skLineSegment(sketch, "E2401", {"start": v(882.5, -199.94) * mm, "end": v(882.5, -193.94) * mm});
            skLineSegment(sketch, "E2402", {"start": v(882.5, -193.94) * mm, "end": v(892.5, -193.94) * mm});
            skLineSegment(sketch, "E2403", {"start": v(892.5, -193.94) * mm, "end": v(892.5, -199.94) * mm});
            skLineSegment(sketch, "E2404", {"start": v(892.5, -199.94) * mm, "end": v(902.5, -199.94) * mm});
            skLineSegment(sketch, "E2405", {"start": v(902.5, -199.94) * mm, "end": v(902.5, -193.94) * mm});
            skLineSegment(sketch, "E2406", {"start": v(902.5, -193.94) * mm, "end": v(912.5, -193.94) * mm});
            skLineSegment(sketch, "E2407", {"start": v(912.5, -193.94) * mm, "end": v(912.5, -199.94) * mm});
            skLineSegment(sketch, "E2408", {"start": v(912.5, -199.94) * mm, "end": v(922.5, -199.94) * mm});
            skLineSegment(sketch, "E2409", {"start": v(922.5, -199.94) * mm, "end": v(922.5, -193.94) * mm});
            skLineSegment(sketch, "E2410", {"start": v(922.5, -193.94) * mm, "end": v(932.5, -193.94) * mm});
            skLineSegment(sketch, "E2411", {"start": v(932.5, -193.94) * mm, "end": v(932.5, -199.94) * mm});
            skLineSegment(sketch, "E2412", {"start": v(932.5, -199.94) * mm, "end": v(942.5, -199.94) * mm});
            skLineSegment(sketch, "E2413", {"start": v(942.5, -199.94) * mm, "end": v(942.5, -193.94) * mm});
            skLineSegment(sketch, "E2414", {"start": v(942.5, -193.94) * mm, "end": v(952.5, -193.94) * mm});
            skLineSegment(sketch, "E2415", {"start": v(952.5, -193.94) * mm, "end": v(952.5, -199.94) * mm});
            skLineSegment(sketch, "E2416", {"start": v(952.5, -199.94) * mm, "end": v(962.5, -199.94) * mm});
            skLineSegment(sketch, "E2417", {"start": v(962.5, -199.94) * mm, "end": v(962.5, -193.94) * mm});
            skLineSegment(sketch, "E2418", {"start": v(962.5, -193.94) * mm, "end": v(972.5, -193.94) * mm});
            skLineSegment(sketch, "E2419", {"start": v(972.5, -193.94) * mm, "end": v(972.5, -199.94) * mm});
            skLineSegment(sketch, "E2420", {"start": v(972.5, -199.94) * mm, "end": v(982.5, -199.94) * mm});
            skLineSegment(sketch, "E2421", {"start": v(982.5, -199.94) * mm, "end": v(982.5, -193.94) * mm});
            skLineSegment(sketch, "E2422", {"start": v(982.5, -193.94) * mm, "end": v(992.5, -193.94) * mm});
            skLineSegment(sketch, "E2423", {"start": v(992.5, -193.94) * mm, "end": v(992.5, -199.94) * mm});
            skLineSegment(sketch, "E2424", {"start": v(992.5, -199.94) * mm, "end": v(1002.5, -199.94) * mm});
            skLineSegment(sketch, "E2425", {"start": v(1002.5, -199.94) * mm, "end": v(1002.5, -193.94) * mm});
            skLineSegment(sketch, "E2426", {"start": v(1002.5, -193.94) * mm, "end": v(1012.5, -193.94) * mm});
            skLineSegment(sketch, "E2427", {"start": v(1012.5, -193.94) * mm, "end": v(1012.5, -199.94) * mm});
            skLineSegment(sketch, "E2428", {"start": v(1012.5, -199.94) * mm, "end": v(1022.5, -199.94) * mm});
            skLineSegment(sketch, "E2429", {"start": v(1022.5, -199.94) * mm, "end": v(1022.5, -193.94) * mm});
            skLineSegment(sketch, "E2430", {"start": v(1022.5, -193.94) * mm, "end": v(1032.5, -193.94) * mm});
            skLineSegment(sketch, "E2431", {"start": v(1032.5, -193.94) * mm, "end": v(1032.5, -199.94) * mm});
            skLineSegment(sketch, "E2432", {"start": v(1032.5, -199.94) * mm, "end": v(1042.5, -199.94) * mm});
            skLineSegment(sketch, "E2433", {"start": v(1042.5, -199.94) * mm, "end": v(1042.5, -193.94) * mm});
            skLineSegment(sketch, "E2434", {"start": v(1042.5, -193.94) * mm, "end": v(1052.5, -193.94) * mm});
            skLineSegment(sketch, "E2435", {"start": v(1052.5, -193.94) * mm, "end": v(1052.5, -199.94) * mm});
            skLineSegment(sketch, "E2436", {"start": v(1052.5, -199.94) * mm, "end": v(1062.5, -199.94) * mm});
            skLineSegment(sketch, "E2437", {"start": v(1062.5, -199.94) * mm, "end": v(1062.5, -193.94) * mm});
            skLineSegment(sketch, "E2438", {"start": v(1062.5, -193.94) * mm, "end": v(1072.5, -193.94) * mm});
            skLineSegment(sketch, "E2439", {"start": v(1072.5, -193.94) * mm, "end": v(1072.5, -199.94) * mm});
            skLineSegment(sketch, "E2440", {"start": v(1072.5, -199.94) * mm, "end": v(1082.5, -199.94) * mm});
            skLineSegment(sketch, "E2441", {"start": v(1082.5, -199.94) * mm, "end": v(1082.5, -193.94) * mm});
            skLineSegment(sketch, "E2442", {"start": v(1082.5, -193.94) * mm, "end": v(1092.5, -193.94) * mm});
            skLineSegment(sketch, "E2443", {"start": v(1092.5, -193.94) * mm, "end": v(1092.5, -199.94) * mm});
            skLineSegment(sketch, "E2444", {"start": v(1092.5, -199.94) * mm, "end": v(1102.5, -199.94) * mm});
            skLineSegment(sketch, "E2445", {"start": v(1102.5, -199.94) * mm, "end": v(1102.5, -193.94) * mm});
            skLineSegment(sketch, "E2446", {"start": v(1102.5, -193.94) * mm, "end": v(1112.5, -193.94) * mm});
            skLineSegment(sketch, "E2447", {"start": v(1112.5, -193.94) * mm, "end": v(1112.5, -199.94) * mm});
            skLineSegment(sketch, "E2448", {"start": v(1112.5, -199.94) * mm, "end": v(1122.5, -199.94) * mm});
            skLineSegment(sketch, "E2449", {"start": v(1122.5, -199.94) * mm, "end": v(1122.5, -193.94) * mm});
            skLineSegment(sketch, "E2450", {"start": v(1122.5, -193.94) * mm, "end": v(1132.5, -193.94) * mm});
            skLineSegment(sketch, "E2451", {"start": v(1132.5, -193.94) * mm, "end": v(1132.5, -199.94) * mm});
            skLineSegment(sketch, "E2452", {"start": v(1132.5, -199.94) * mm, "end": v(1142.5, -199.94) * mm});
            skLineSegment(sketch, "E2453", {"start": v(1142.5, -199.94) * mm, "end": v(1142.5, -193.94) * mm});
            skLineSegment(sketch, "E2454", {"start": v(1142.5, -193.94) * mm, "end": v(1152.5, -193.94) * mm});
            skLineSegment(sketch, "E2455", {"start": v(1152.5, -193.94) * mm, "end": v(1152.5, -199.94) * mm});
            skLineSegment(sketch, "E2456", {"start": v(1152.5, -199.94) * mm, "end": v(1162.5, -199.94) * mm});
            skLineSegment(sketch, "E2457", {"start": v(1162.5, -199.94) * mm, "end": v(1162.5, -193.94) * mm});
            skLineSegment(sketch, "E2458", {"start": v(1162.5, -193.94) * mm, "end": v(1178.75, -193.94) * mm});
            skLineSegment(sketch, "E2459", {"start": v(1178.75, -193.94) * mm, "end": v(1178.75, -199.94) * mm});
            skLineSegment(sketch, "E2460", {"start": v(1178.75, -199.94) * mm, "end": v(1189, -199.94) * mm});
            skLineSegment(sketch, "E2461", {"start": v(1189, -199.94) * mm, "end": v(1189, -204.34) * mm});
            skLineSegment(sketch, "E2462", {"start": v(1189, -204.34) * mm, "end": v(1195, -204.34) * mm});
            skLineSegment(sketch, "E2463", {"start": v(1195, -204.34) * mm, "end": v(1195, -214.74) * mm});
            skLineSegment(sketch, "E2464", {"start": v(1195, -214.74) * mm, "end": v(1189, -214.74) * mm});
            skLineSegment(sketch, "E2465", {"start": v(1189, -214.74) * mm, "end": v(1189, -225.14) * mm});
            skLineSegment(sketch, "E2466", {"start": v(1189, -225.14) * mm, "end": v(1195, -225.14) * mm});
            skLineSegment(sketch, "E2467", {"start": v(1195, -225.14) * mm, "end": v(1195, -235.54) * mm});
            skLineSegment(sketch, "E2468", {"start": v(1195, -235.54) * mm, "end": v(1189, -235.54) * mm});
            skLineSegment(sketch, "E2469", {"start": v(1189, -235.54) * mm, "end": v(1189, -239.94) * mm});
            skLineSegment(sketch, "E2470", {"start": v(1189, -239.94) * mm, "end": v(1178.75, -239.94) * mm});
            skLineSegment(sketch, "E2471", {"start": v(1178.75, -239.94) * mm, "end": v(1178.75, -245.94) * mm});
            skLineSegment(sketch, "E2472", {"start": v(1178.75, -245.94) * mm, "end": v(1162.5, -245.94) * mm});
            skLineSegment(sketch, "E2473", {"start": v(1162.5, -245.94) * mm, "end": v(1162.5, -239.94) * mm});
            skLineSegment(sketch, "E2474", {"start": v(1162.5, -239.94) * mm, "end": v(1152.5, -239.94) * mm});
            skLineSegment(sketch, "E2475", {"start": v(1152.5, -239.94) * mm, "end": v(1152.5, -245.94) * mm});
            skLineSegment(sketch, "E2476", {"start": v(1152.5, -245.94) * mm, "end": v(1142.5, -245.94) * mm});
            skLineSegment(sketch, "E2477", {"start": v(1142.5, -245.94) * mm, "end": v(1142.5, -239.94) * mm});
            skLineSegment(sketch, "E2478", {"start": v(1142.5, -239.94) * mm, "end": v(1132.5, -239.94) * mm});
            skLineSegment(sketch, "E2479", {"start": v(1132.5, -239.94) * mm, "end": v(1132.5, -245.94) * mm});
            skLineSegment(sketch, "E2480", {"start": v(1132.5, -245.94) * mm, "end": v(1122.5, -245.94) * mm});
            skLineSegment(sketch, "E2481", {"start": v(1122.5, -245.94) * mm, "end": v(1122.5, -239.94) * mm});
            skLineSegment(sketch, "E2482", {"start": v(1122.5, -239.94) * mm, "end": v(1112.5, -239.94) * mm});
            skLineSegment(sketch, "E2483", {"start": v(1112.5, -239.94) * mm, "end": v(1112.5, -245.94) * mm});
            skLineSegment(sketch, "E2484", {"start": v(1112.5, -245.94) * mm, "end": v(1102.5, -245.94) * mm});
            skLineSegment(sketch, "E2485", {"start": v(1102.5, -245.94) * mm, "end": v(1102.5, -239.94) * mm});
            skLineSegment(sketch, "E2486", {"start": v(1102.5, -239.94) * mm, "end": v(1092.5, -239.94) * mm});
            skLineSegment(sketch, "E2487", {"start": v(1092.5, -239.94) * mm, "end": v(1092.5, -245.94) * mm});
            skLineSegment(sketch, "E2488", {"start": v(1092.5, -245.94) * mm, "end": v(1082.5, -245.94) * mm});
            skLineSegment(sketch, "E2489", {"start": v(1082.5, -245.94) * mm, "end": v(1082.5, -239.94) * mm});
            skLineSegment(sketch, "E2490", {"start": v(1082.5, -239.94) * mm, "end": v(1072.5, -239.94) * mm});
            skLineSegment(sketch, "E2491", {"start": v(1072.5, -239.94) * mm, "end": v(1072.5, -245.94) * mm});
            skLineSegment(sketch, "E2492", {"start": v(1072.5, -245.94) * mm, "end": v(1062.5, -245.94) * mm});
            skLineSegment(sketch, "E2493", {"start": v(1062.5, -245.94) * mm, "end": v(1062.5, -239.94) * mm});
            skLineSegment(sketch, "E2494", {"start": v(1062.5, -239.94) * mm, "end": v(1052.5, -239.94) * mm});
            skLineSegment(sketch, "E2495", {"start": v(1052.5, -239.94) * mm, "end": v(1052.5, -245.94) * mm});
            skLineSegment(sketch, "E2496", {"start": v(1052.5, -245.94) * mm, "end": v(1042.5, -245.94) * mm});
            skLineSegment(sketch, "E2497", {"start": v(1042.5, -245.94) * mm, "end": v(1042.5, -239.94) * mm});
            skLineSegment(sketch, "E2498", {"start": v(1042.5, -239.94) * mm, "end": v(1032.5, -239.94) * mm});
            skLineSegment(sketch, "E2499", {"start": v(1032.5, -239.94) * mm, "end": v(1032.5, -245.94) * mm});
            skLineSegment(sketch, "E2500", {"start": v(1032.5, -245.94) * mm, "end": v(1022.5, -245.94) * mm});
            skLineSegment(sketch, "E2501", {"start": v(1022.5, -245.94) * mm, "end": v(1022.5, -239.94) * mm});
            skLineSegment(sketch, "E2502", {"start": v(1022.5, -239.94) * mm, "end": v(1012.5, -239.94) * mm});
            skLineSegment(sketch, "E2503", {"start": v(1012.5, -239.94) * mm, "end": v(1012.5, -245.94) * mm});
            skLineSegment(sketch, "E2504", {"start": v(1012.5, -245.94) * mm, "end": v(1002.5, -245.94) * mm});
            skLineSegment(sketch, "E2505", {"start": v(1002.5, -245.94) * mm, "end": v(1002.5, -239.94) * mm});
            skLineSegment(sketch, "E2506", {"start": v(1002.5, -239.94) * mm, "end": v(992.5, -239.94) * mm});
            skLineSegment(sketch, "E2507", {"start": v(992.5, -239.94) * mm, "end": v(992.5, -245.94) * mm});
            skLineSegment(sketch, "E2508", {"start": v(992.5, -245.94) * mm, "end": v(982.5, -245.94) * mm});
            skLineSegment(sketch, "E2509", {"start": v(982.5, -245.94) * mm, "end": v(982.5, -239.94) * mm});
            skLineSegment(sketch, "E2510", {"start": v(982.5, -239.94) * mm, "end": v(972.5, -239.94) * mm});
            skLineSegment(sketch, "E2511", {"start": v(972.5, -239.94) * mm, "end": v(972.5, -245.94) * mm});
            skLineSegment(sketch, "E2512", {"start": v(972.5, -245.94) * mm, "end": v(962.5, -245.94) * mm});
            skLineSegment(sketch, "E2513", {"start": v(962.5, -245.94) * mm, "end": v(962.5, -239.94) * mm});
            skLineSegment(sketch, "E2514", {"start": v(962.5, -239.94) * mm, "end": v(952.5, -239.94) * mm});
            skLineSegment(sketch, "E2515", {"start": v(952.5, -239.94) * mm, "end": v(952.5, -245.94) * mm});
            skLineSegment(sketch, "E2516", {"start": v(952.5, -245.94) * mm, "end": v(942.5, -245.94) * mm});
            skLineSegment(sketch, "E2517", {"start": v(942.5, -245.94) * mm, "end": v(942.5, -239.94) * mm});
            skLineSegment(sketch, "E2518", {"start": v(942.5, -239.94) * mm, "end": v(932.5, -239.94) * mm});
            skLineSegment(sketch, "E2519", {"start": v(932.5, -239.94) * mm, "end": v(932.5, -245.94) * mm});
            skLineSegment(sketch, "E2520", {"start": v(932.5, -245.94) * mm, "end": v(922.5, -245.94) * mm});
            skLineSegment(sketch, "E2521", {"start": v(922.5, -245.94) * mm, "end": v(922.5, -239.94) * mm});
            skLineSegment(sketch, "E2522", {"start": v(922.5, -239.94) * mm, "end": v(912.5, -239.94) * mm});
            skLineSegment(sketch, "E2523", {"start": v(912.5, -239.94) * mm, "end": v(912.5, -245.94) * mm});
            skLineSegment(sketch, "E2524", {"start": v(912.5, -245.94) * mm, "end": v(902.5, -245.94) * mm});
            skLineSegment(sketch, "E2525", {"start": v(902.5, -245.94) * mm, "end": v(902.5, -239.94) * mm});
            skLineSegment(sketch, "E2526", {"start": v(902.5, -239.94) * mm, "end": v(892.5, -239.94) * mm});
            skLineSegment(sketch, "E2527", {"start": v(892.5, -239.94) * mm, "end": v(892.5, -245.94) * mm});
            skLineSegment(sketch, "E2528", {"start": v(892.5, -245.94) * mm, "end": v(882.5, -245.94) * mm});
            skLineSegment(sketch, "E2529", {"start": v(882.5, -245.94) * mm, "end": v(882.5, -239.94) * mm});
            skLineSegment(sketch, "E2530", {"start": v(882.5, -239.94) * mm, "end": v(872.5, -239.94) * mm});
            skLineSegment(sketch, "E2531", {"start": v(872.5, -239.94) * mm, "end": v(872.5, -245.94) * mm});
            skLineSegment(sketch, "E2532", {"start": v(872.5, -245.94) * mm, "end": v(862.5, -245.94) * mm});
            skLineSegment(sketch, "E2533", {"start": v(862.5, -245.94) * mm, "end": v(862.5, -239.94) * mm});
            skLineSegment(sketch, "E2534", {"start": v(862.5, -239.94) * mm, "end": v(852.5, -239.94) * mm});
            skLineSegment(sketch, "E2535", {"start": v(852.5, -239.94) * mm, "end": v(852.5, -245.94) * mm});
            skLineSegment(sketch, "E2536", {"start": v(852.5, -245.94) * mm, "end": v(842.5, -245.94) * mm});
            skLineSegment(sketch, "E2537", {"start": v(842.5, -245.94) * mm, "end": v(842.5, -239.94) * mm});
            skLineSegment(sketch, "E2538", {"start": v(842.5, -239.94) * mm, "end": v(832.5, -239.94) * mm});
            skLineSegment(sketch, "E2539", {"start": v(832.5, -239.94) * mm, "end": v(832.5, -245.94) * mm});
            skLineSegment(sketch, "E2540", {"start": v(832.5, -245.94) * mm, "end": v(822.5, -245.94) * mm});
            skLineSegment(sketch, "E2541", {"start": v(822.5, -245.94) * mm, "end": v(822.5, -239.94) * mm});
            skLineSegment(sketch, "E2542", {"start": v(822.5, -239.94) * mm, "end": v(812.5, -239.94) * mm});
            skLineSegment(sketch, "E2543", {"start": v(812.5, -239.94) * mm, "end": v(812.5, -245.94) * mm});
            skLineSegment(sketch, "E2544", {"start": v(812.5, -245.94) * mm, "end": v(802.5, -245.94) * mm});
            skLineSegment(sketch, "E2545", {"start": v(802.5, -245.94) * mm, "end": v(802.5, -239.94) * mm});
            skLineSegment(sketch, "E2546", {"start": v(802.5, -239.94) * mm, "end": v(792.5, -239.94) * mm});
            skLineSegment(sketch, "E2547", {"start": v(792.5, -239.94) * mm, "end": v(792.5, -245.94) * mm});
            skLineSegment(sketch, "E2548", {"start": v(792.5, -245.94) * mm, "end": v(782.5, -245.94) * mm});
            skLineSegment(sketch, "E2549", {"start": v(782.5, -245.94) * mm, "end": v(782.5, -239.94) * mm});
            skLineSegment(sketch, "E2550", {"start": v(782.5, -239.94) * mm, "end": v(772.5, -239.94) * mm});
            skLineSegment(sketch, "E2551", {"start": v(772.5, -239.94) * mm, "end": v(772.5, -245.94) * mm});
            skLineSegment(sketch, "E2552", {"start": v(772.5, -245.94) * mm, "end": v(762.5, -245.94) * mm});
            skLineSegment(sketch, "E2553", {"start": v(762.5, -245.94) * mm, "end": v(762.5, -239.94) * mm});
            skLineSegment(sketch, "E2554", {"start": v(762.5, -239.94) * mm, "end": v(752.5, -239.94) * mm});
            skLineSegment(sketch, "E2555", {"start": v(752.5, -239.94) * mm, "end": v(752.5, -245.94) * mm});
            skLineSegment(sketch, "E2556", {"start": v(752.5, -245.94) * mm, "end": v(742.5, -245.94) * mm});
            skLineSegment(sketch, "E2557", {"start": v(742.5, -245.94) * mm, "end": v(742.5, -239.94) * mm});
            skLineSegment(sketch, "E2558", {"start": v(742.5, -239.94) * mm, "end": v(732.5, -239.94) * mm});
            skLineSegment(sketch, "E2559", {"start": v(732.5, -239.94) * mm, "end": v(732.5, -245.94) * mm});
            skLineSegment(sketch, "E2560", {"start": v(732.5, -245.94) * mm, "end": v(722.5, -245.94) * mm});
            skLineSegment(sketch, "E2561", {"start": v(722.5, -245.94) * mm, "end": v(722.5, -239.94) * mm});
            skLineSegment(sketch, "E2562", {"start": v(722.5, -239.94) * mm, "end": v(712.5, -239.94) * mm});
            skLineSegment(sketch, "E2563", {"start": v(712.5, -239.94) * mm, "end": v(712.5, -245.94) * mm});
            skLineSegment(sketch, "E2564", {"start": v(712.5, -245.94) * mm, "end": v(702.5, -245.94) * mm});
            skLineSegment(sketch, "E2565", {"start": v(702.5, -245.94) * mm, "end": v(702.5, -239.94) * mm});
            skLineSegment(sketch, "E2566", {"start": v(702.5, -239.94) * mm, "end": v(692.5, -239.94) * mm});
            skLineSegment(sketch, "E2567", {"start": v(692.5, -239.94) * mm, "end": v(692.5, -245.94) * mm});
            skLineSegment(sketch, "E2568", {"start": v(692.5, -245.94) * mm, "end": v(682.5, -245.94) * mm});
            skLineSegment(sketch, "E2569", {"start": v(682.5, -245.94) * mm, "end": v(682.5, -239.94) * mm});
            skLineSegment(sketch, "E2570", {"start": v(682.5, -239.94) * mm, "end": v(672.5, -239.94) * mm});
            skLineSegment(sketch, "E2571", {"start": v(672.5, -239.94) * mm, "end": v(672.5, -245.94) * mm});
            skLineSegment(sketch, "E2572", {"start": v(672.5, -245.94) * mm, "end": v(662.5, -245.94) * mm});
            skLineSegment(sketch, "E2573", {"start": v(662.5, -245.94) * mm, "end": v(662.5, -239.94) * mm});
            skLineSegment(sketch, "E2574", {"start": v(662.5, -239.94) * mm, "end": v(652.5, -239.94) * mm});
            skLineSegment(sketch, "E2575", {"start": v(652.5, -239.94) * mm, "end": v(652.5, -245.94) * mm});
            skLineSegment(sketch, "E2576", {"start": v(652.5, -245.94) * mm, "end": v(642.5, -245.94) * mm});
            skLineSegment(sketch, "E2577", {"start": v(642.5, -245.94) * mm, "end": v(642.5, -239.94) * mm});
            skLineSegment(sketch, "E2578", {"start": v(642.5, -239.94) * mm, "end": v(632.5, -239.94) * mm});
            skLineSegment(sketch, "E2579", {"start": v(632.5, -239.94) * mm, "end": v(632.5, -245.94) * mm});
            skLineSegment(sketch, "E2580", {"start": v(632.5, -245.94) * mm, "end": v(622.5, -245.94) * mm});
            skLineSegment(sketch, "E2581", {"start": v(622.5, -245.94) * mm, "end": v(622.5, -239.94) * mm});
            skLineSegment(sketch, "E2582", {"start": v(622.5, -239.94) * mm, "end": v(612.5, -239.94) * mm});
            skLineSegment(sketch, "E2583", {"start": v(612.5, -239.94) * mm, "end": v(612.5, -245.94) * mm});
            skLineSegment(sketch, "E2584", {"start": v(612.5, -245.94) * mm, "end": v(602.5, -245.94) * mm});
            skLineSegment(sketch, "E2585", {"start": v(602.5, -245.94) * mm, "end": v(602.5, -239.94) * mm});
            skLineSegment(sketch, "E2586", {"start": v(602.5, -239.94) * mm, "end": v(592.5, -239.94) * mm});
            skLineSegment(sketch, "E2587", {"start": v(592.5, -239.94) * mm, "end": v(592.5, -245.94) * mm});
            skLineSegment(sketch, "E2588", {"start": v(592.5, -245.94) * mm, "end": v(582.5, -245.94) * mm});
            skLineSegment(sketch, "E2589", {"start": v(582.5, -245.94) * mm, "end": v(582.5, -239.94) * mm});
            skLineSegment(sketch, "E2590", {"start": v(582.5, -239.94) * mm, "end": v(572.5, -239.94) * mm});
            skLineSegment(sketch, "E2591", {"start": v(572.5, -239.94) * mm, "end": v(572.5, -245.94) * mm});
            skLineSegment(sketch, "E2592", {"start": v(572.5, -245.94) * mm, "end": v(562.5, -245.94) * mm});
            skLineSegment(sketch, "E2593", {"start": v(562.5, -245.94) * mm, "end": v(562.5, -239.94) * mm});
            skLineSegment(sketch, "E2594", {"start": v(562.5, -239.94) * mm, "end": v(552.5, -239.94) * mm});
            skLineSegment(sketch, "E2595", {"start": v(552.5, -239.94) * mm, "end": v(552.5, -245.94) * mm});
            skLineSegment(sketch, "E2596", {"start": v(552.5, -245.94) * mm, "end": v(542.5, -245.94) * mm});
            skLineSegment(sketch, "E2597", {"start": v(542.5, -245.94) * mm, "end": v(542.5, -239.94) * mm});
            skLineSegment(sketch, "E2598", {"start": v(542.5, -239.94) * mm, "end": v(532.5, -239.94) * mm});
            skLineSegment(sketch, "E2599", {"start": v(532.5, -239.94) * mm, "end": v(532.5, -245.94) * mm});
            skLineSegment(sketch, "E2600", {"start": v(532.5, -245.94) * mm, "end": v(522.5, -245.94) * mm});
            skLineSegment(sketch, "E2601", {"start": v(522.5, -245.94) * mm, "end": v(522.5, -239.94) * mm});
            skLineSegment(sketch, "E2602", {"start": v(522.5, -239.94) * mm, "end": v(512.5, -239.94) * mm});
            skLineSegment(sketch, "E2603", {"start": v(512.5, -239.94) * mm, "end": v(512.5, -245.94) * mm});
            skLineSegment(sketch, "E2604", {"start": v(512.5, -245.94) * mm, "end": v(502.5, -245.94) * mm});
            skLineSegment(sketch, "E2605", {"start": v(502.5, -245.94) * mm, "end": v(502.5, -239.94) * mm});
            skLineSegment(sketch, "E2606", {"start": v(502.5, -239.94) * mm, "end": v(492.5, -239.94) * mm});
            skLineSegment(sketch, "E2607", {"start": v(492.5, -239.94) * mm, "end": v(492.5, -245.94) * mm});
            skLineSegment(sketch, "E2608", {"start": v(492.5, -245.94) * mm, "end": v(482.5, -245.94) * mm});
            skLineSegment(sketch, "E2609", {"start": v(482.5, -245.94) * mm, "end": v(482.5, -239.94) * mm});
            skLineSegment(sketch, "E2610", {"start": v(482.5, -239.94) * mm, "end": v(472.5, -239.94) * mm});
            skLineSegment(sketch, "E2611", {"start": v(472.5, -239.94) * mm, "end": v(472.5, -245.94) * mm});
            skLineSegment(sketch, "E2612", {"start": v(472.5, -245.94) * mm, "end": v(462.5, -245.94) * mm});
            skLineSegment(sketch, "E2613", {"start": v(462.5, -245.94) * mm, "end": v(462.5, -239.94) * mm});
            skLineSegment(sketch, "E2614", {"start": v(462.5, -239.94) * mm, "end": v(452.5, -239.94) * mm});
            skLineSegment(sketch, "E2615", {"start": v(452.5, -239.94) * mm, "end": v(452.5, -245.94) * mm});
            skLineSegment(sketch, "E2616", {"start": v(452.5, -245.94) * mm, "end": v(442.5, -245.94) * mm});
            skLineSegment(sketch, "E2617", {"start": v(442.5, -245.94) * mm, "end": v(442.5, -239.94) * mm});
            skLineSegment(sketch, "E2618", {"start": v(442.5, -239.94) * mm, "end": v(432.5, -239.94) * mm});
            skLineSegment(sketch, "E2619", {"start": v(432.5, -239.94) * mm, "end": v(432.5, -245.94) * mm});
            skLineSegment(sketch, "E2620", {"start": v(432.5, -245.94) * mm, "end": v(422.5, -245.94) * mm});
            skLineSegment(sketch, "E2621", {"start": v(422.5, -245.94) * mm, "end": v(422.5, -239.94) * mm});
            skLineSegment(sketch, "E2622", {"start": v(422.5, -239.94) * mm, "end": v(412.5, -239.94) * mm});
            skLineSegment(sketch, "E2623", {"start": v(412.5, -239.94) * mm, "end": v(412.5, -245.94) * mm});
            skLineSegment(sketch, "E2624", {"start": v(412.5, -245.94) * mm, "end": v(402.5, -245.94) * mm});
            skLineSegment(sketch, "E2625", {"start": v(402.5, -245.94) * mm, "end": v(402.5, -239.94) * mm});
            skLineSegment(sketch, "E2626", {"start": v(402.5, -239.94) * mm, "end": v(392.5, -239.94) * mm});
            skLineSegment(sketch, "E2627", {"start": v(392.5, -239.94) * mm, "end": v(392.5, -245.94) * mm});
            skLineSegment(sketch, "E2628", {"start": v(392.5, -245.94) * mm, "end": v(382.5, -245.94) * mm});
            skLineSegment(sketch, "E2629", {"start": v(382.5, -245.94) * mm, "end": v(382.5, -239.94) * mm});
            skLineSegment(sketch, "E2630", {"start": v(382.5, -239.94) * mm, "end": v(372.5, -239.94) * mm});
            skLineSegment(sketch, "E2631", {"start": v(372.5, -239.94) * mm, "end": v(372.5, -245.94) * mm});
            skLineSegment(sketch, "E2632", {"start": v(372.5, -245.94) * mm, "end": v(362.5, -245.94) * mm});
            skLineSegment(sketch, "E2633", {"start": v(362.5, -245.94) * mm, "end": v(362.5, -239.94) * mm});
            skLineSegment(sketch, "E2634", {"start": v(362.5, -239.94) * mm, "end": v(352.5, -239.94) * mm});
            skLineSegment(sketch, "E2635", {"start": v(352.5, -239.94) * mm, "end": v(352.5, -245.94) * mm});
            skLineSegment(sketch, "E2636", {"start": v(352.5, -245.94) * mm, "end": v(342.5, -245.94) * mm});
            skLineSegment(sketch, "E2637", {"start": v(342.5, -245.94) * mm, "end": v(342.5, -239.94) * mm});
            skLineSegment(sketch, "E2638", {"start": v(342.5, -239.94) * mm, "end": v(332.5, -239.94) * mm});
            skLineSegment(sketch, "E2639", {"start": v(332.5, -239.94) * mm, "end": v(332.5, -245.94) * mm});
            skLineSegment(sketch, "E2640", {"start": v(332.5, -245.94) * mm, "end": v(322.5, -245.94) * mm});
            skLineSegment(sketch, "E2641", {"start": v(322.5, -245.94) * mm, "end": v(322.5, -239.94) * mm});
            skLineSegment(sketch, "E2642", {"start": v(322.5, -239.94) * mm, "end": v(312.5, -239.94) * mm});
            skLineSegment(sketch, "E2643", {"start": v(312.5, -239.94) * mm, "end": v(312.5, -245.94) * mm});
            skLineSegment(sketch, "E2644", {"start": v(312.5, -245.94) * mm, "end": v(302.5, -245.94) * mm});
            skLineSegment(sketch, "E2645", {"start": v(302.5, -245.94) * mm, "end": v(302.5, -239.94) * mm});
            skLineSegment(sketch, "E2646", {"start": v(302.5, -239.94) * mm, "end": v(292.5, -239.94) * mm});
            skLineSegment(sketch, "E2647", {"start": v(292.5, -239.94) * mm, "end": v(292.5, -245.94) * mm});
            skLineSegment(sketch, "E2648", {"start": v(292.5, -245.94) * mm, "end": v(282.5, -245.94) * mm});
            skLineSegment(sketch, "E2649", {"start": v(282.5, -245.94) * mm, "end": v(282.5, -239.94) * mm});
            skLineSegment(sketch, "E2650", {"start": v(282.5, -239.94) * mm, "end": v(272.5, -239.94) * mm});
            skLineSegment(sketch, "E2651", {"start": v(272.5, -239.94) * mm, "end": v(272.5, -245.94) * mm});
            skLineSegment(sketch, "E2652", {"start": v(272.5, -245.94) * mm, "end": v(262.5, -245.94) * mm});
            skLineSegment(sketch, "E2653", {"start": v(262.5, -245.94) * mm, "end": v(262.5, -239.94) * mm});
            skLineSegment(sketch, "E2654", {"start": v(262.5, -239.94) * mm, "end": v(252.5, -239.94) * mm});
            skLineSegment(sketch, "E2655", {"start": v(252.5, -239.94) * mm, "end": v(252.5, -245.94) * mm});
            skLineSegment(sketch, "E2656", {"start": v(252.5, -245.94) * mm, "end": v(242.5, -245.94) * mm});
            skLineSegment(sketch, "E2657", {"start": v(242.5, -245.94) * mm, "end": v(242.5, -239.94) * mm});
            skLineSegment(sketch, "E2658", {"start": v(242.5, -239.94) * mm, "end": v(232.5, -239.94) * mm});
            skLineSegment(sketch, "E2659", {"start": v(232.5, -239.94) * mm, "end": v(232.5, -245.94) * mm});
            skLineSegment(sketch, "E2660", {"start": v(232.5, -245.94) * mm, "end": v(222.5, -245.94) * mm});
            skLineSegment(sketch, "E2661", {"start": v(222.5, -245.94) * mm, "end": v(222.5, -239.94) * mm});
            skLineSegment(sketch, "E2662", {"start": v(222.5, -239.94) * mm, "end": v(212.5, -239.94) * mm});
            skLineSegment(sketch, "E2663", {"start": v(212.5, -239.94) * mm, "end": v(212.5, -245.94) * mm});
            skLineSegment(sketch, "E2664", {"start": v(212.5, -245.94) * mm, "end": v(202.5, -245.94) * mm});
            skLineSegment(sketch, "E2665", {"start": v(202.5, -245.94) * mm, "end": v(202.5, -239.94) * mm});
            skLineSegment(sketch, "E2666", {"start": v(202.5, -239.94) * mm, "end": v(192.5, -239.94) * mm});
            skLineSegment(sketch, "E2667", {"start": v(192.5, -239.94) * mm, "end": v(192.5, -245.94) * mm});
            skLineSegment(sketch, "E2668", {"start": v(192.5, -245.94) * mm, "end": v(182.5, -245.94) * mm});
            skLineSegment(sketch, "E2669", {"start": v(182.5, -245.94) * mm, "end": v(182.5, -239.94) * mm});
            skLineSegment(sketch, "E2670", {"start": v(182.5, -239.94) * mm, "end": v(172.5, -239.94) * mm});
            skLineSegment(sketch, "E2671", {"start": v(172.5, -239.94) * mm, "end": v(172.5, -245.94) * mm});
            skLineSegment(sketch, "E2672", {"start": v(172.5, -245.94) * mm, "end": v(162.5, -245.94) * mm});
            skLineSegment(sketch, "E2673", {"start": v(162.5, -245.94) * mm, "end": v(162.5, -239.94) * mm});
            skLineSegment(sketch, "E2674", {"start": v(162.5, -239.94) * mm, "end": v(152.5, -239.94) * mm});
            skLineSegment(sketch, "E2675", {"start": v(152.5, -239.94) * mm, "end": v(152.5, -245.94) * mm});
            skLineSegment(sketch, "E2676", {"start": v(152.5, -245.94) * mm, "end": v(142.5, -245.94) * mm});
            skLineSegment(sketch, "E2677", {"start": v(142.5, -245.94) * mm, "end": v(142.5, -239.94) * mm});
            skLineSegment(sketch, "E2678", {"start": v(142.5, -239.94) * mm, "end": v(132.5, -239.94) * mm});
            skLineSegment(sketch, "E2679", {"start": v(132.5, -239.94) * mm, "end": v(132.5, -245.94) * mm});
            skLineSegment(sketch, "E2680", {"start": v(132.5, -245.94) * mm, "end": v(122.5, -245.94) * mm});
            skLineSegment(sketch, "E2681", {"start": v(122.5, -245.94) * mm, "end": v(122.5, -239.94) * mm});
            skLineSegment(sketch, "E2682", {"start": v(122.5, -239.94) * mm, "end": v(112.5, -239.94) * mm});
            skLineSegment(sketch, "E2683", {"start": v(112.5, -239.94) * mm, "end": v(112.5, -245.94) * mm});
            skLineSegment(sketch, "E2684", {"start": v(112.5, -245.94) * mm, "end": v(102.5, -245.94) * mm});
            skLineSegment(sketch, "E2685", {"start": v(102.5, -245.94) * mm, "end": v(102.5, -239.94) * mm});
            skLineSegment(sketch, "E2686", {"start": v(102.5, -239.94) * mm, "end": v(92.5, -239.94) * mm});
            skLineSegment(sketch, "E2687", {"start": v(92.5, -239.94) * mm, "end": v(92.5, -245.94) * mm});
            skLineSegment(sketch, "E2688", {"start": v(92.5, -245.94) * mm, "end": v(82.5, -245.94) * mm});
            skLineSegment(sketch, "E2689", {"start": v(82.5, -245.94) * mm, "end": v(82.5, -239.94) * mm});
            skLineSegment(sketch, "E2690", {"start": v(82.5, -239.94) * mm, "end": v(72.5, -239.94) * mm});
            skLineSegment(sketch, "E2691", {"start": v(72.5, -239.94) * mm, "end": v(72.5, -245.94) * mm});
            skLineSegment(sketch, "E2692", {"start": v(72.5, -245.94) * mm, "end": v(62.5, -245.94) * mm});
            skLineSegment(sketch, "E2693", {"start": v(62.5, -245.94) * mm, "end": v(62.5, -239.94) * mm});
            skLineSegment(sketch, "E2694", {"start": v(62.5, -239.94) * mm, "end": v(52.5, -239.94) * mm});
            skLineSegment(sketch, "E2695", {"start": v(52.5, -239.94) * mm, "end": v(52.5, -245.94) * mm});
            skLineSegment(sketch, "E2696", {"start": v(52.5, -245.94) * mm, "end": v(42.5, -245.94) * mm});
            skLineSegment(sketch, "E2697", {"start": v(42.5, -245.94) * mm, "end": v(42.5, -239.94) * mm});
            skLineSegment(sketch, "E2698", {"start": v(42.5, -239.94) * mm, "end": v(32.5, -239.94) * mm});
            skLineSegment(sketch, "E2699", {"start": v(32.5, -239.94) * mm, "end": v(32.5, -245.94) * mm});
            skLineSegment(sketch, "E2700", {"start": v(32.5, -245.94) * mm, "end": v(16.25, -245.94) * mm});
            skLineSegment(sketch, "E2701", {"start": v(16.25, -245.94) * mm, "end": v(16.25, -239.94) * mm});
            skLineSegment(sketch, "E2702", {"start": v(16.25, -239.94) * mm, "end": v(6, -239.94) * mm});
            skLineSegment(sketch, "E2703", {"start": v(6, -239.94) * mm, "end": v(6, -235.54) * mm});
            skLineSegment(sketch, "E2704", {"start": v(6, -235.54) * mm, "end": v(0, -235.54) * mm});
            skLineSegment(sketch, "E2705", {"start": v(0, -235.54) * mm, "end": v(0, -225.14) * mm});
            skLineSegment(sketch, "E2706", {"start": v(0, -225.14) * mm, "end": v(6, -225.14) * mm});
            skLineSegment(sketch, "E2707", {"start": v(6, -225.14) * mm, "end": v(6, -214.74) * mm});
            skLineSegment(sketch, "E2708", {"start": v(6, -214.74) * mm, "end": v(0, -214.74) * mm});
            skLineSegment(sketch, "E2709", {"start": v(0, -214.74) * mm, "end": v(0, -204.34) * mm});
            skLineSegment(sketch, "E2710", {"start": v(0, -204.34) * mm, "end": v(6, -204.34) * mm});
            skLineSegment(sketch, "E2711", {"start": v(6, -204.34) * mm, "end": v(6, -199.94) * mm});
            skSolve(sketch);
        }
        {
            var Q0;
            Q0=makeQuery(id+"F0.imprint","IMPRINT",FACE,{"disambiguationData":[TD([[makeQuery(id+"F0.imprint","IMPRINT",EDGE,{"derivedFrom":sQuery(id+"F0.wireOp",EDGE,"E660")}),-1.0]])]});
            var Q1;
            Q1=makeQuery(id+"F0.imprint","IMPRINT",FACE,{"disambiguationData":[TD([[makeQuery(id+"F0.imprint","IMPRINT",EDGE,{"derivedFrom":sQuery(id+"F0.wireOp",EDGE,"E0")}),-1.0]])]});
            var Q2;
            Q2=makeQuery(id+"F0.imprint","IMPRINT",FACE,{"disambiguationData":[TD([[makeQuery(id+"F0.imprint","IMPRINT",EDGE,{"derivedFrom":sQuery(id+"F0.wireOp",EDGE,"E2228")}),-1.0]])]});
            var Q3;
            Q3=makeQuery(id+"F0.imprint","IMPRINT",FACE,{"disambiguationData":[TD([[makeQuery(id+"F0.imprint","IMPRINT",EDGE,{"derivedFrom":sQuery(id+"F0.wireOp",EDGE,"E1744")}),-1.0]])]});
            var Q4;
            Q4=makeQuery(id+"F0.imprint","IMPRINT",FACE,{"disambiguationData":[TD([[makeQuery(id+"F0.imprint","IMPRINT",EDGE,{"derivedFrom":sQuery(id+"F0.wireOp",EDGE,"E1320")}),-1.0]])]});
            var Q5;
            Q5=makeQuery(id+"F0.imprint","IMPRINT",FACE,{"disambiguationData":[TD([[makeQuery(id+"F0.imprint","IMPRINT",EDGE,{"derivedFrom":sQuery(id+"F0.wireOp",EDGE,"E1532")}),-1.0]])]});
            extrude(context, id + "F1", {"entities" : qUnion([Q0, Q1, Q2, Q3, Q4, Q5]), "depth" : 6 * mm, "offsetDistance" : 25 * mm});
        }
        {
            var Q0;
            Q0=makeQuery(id+"F1.opExtrude","CAP_FACE",FACE,{"disambiguationData":[OSD([sQuery(id+"F0.wireOp",EDGE,"E0"),sQuery(id+"F0.wireOp",EDGE,"E1"),sQuery(id+"F0.wireOp",EDGE,"E2"),sQuery(id+"F0.wireOp",EDGE,"E3"),sQuery(id+"F0.wireOp",EDGE,"E4"),sQuery(id+"F0.wireOp",EDGE,"E5"),sQuery(id+"F0.wireOp",EDGE,"E6"),sQuery(id+"F0.wireOp",EDGE,"E7"),sQuery(id+"F0.wireOp",EDGE,"E8"),sQuery(id+"F0.wireOp",EDGE,"E9"),sQuery(id+"F0.wireOp",EDGE,"E10"),sQuery(id+"F0.wireOp",EDGE,"E11"),sQuery(id+"F0.wireOp",EDGE,"E12"),sQuery(id+"F0.wireOp",EDGE,"E13"),sQuery(id+"F0.wireOp",EDGE,"E14"),sQuery(id+"F0.wireOp",EDGE,"E15"),sQuery(id+"F0.wireOp",EDGE,"E16"),sQuery(id+"F0.wireOp",EDGE,"E17"),sQuery(id+"F0.wireOp",EDGE,"E18"),sQuery(id+"F0.wireOp",EDGE,"E19"),sQuery(id+"F0.wireOp",EDGE,"E20"),sQuery(id+"F0.wireOp",EDGE,"E21"),sQuery(id+"F0.wireOp",EDGE,"E22"),sQuery(id+"F0.wireOp",EDGE,"E23"),sQuery(id+"F0.wireOp",EDGE,"E24"),sQuery(id+"F0.wireOp",EDGE,"E25"),sQuery(id+"F0.wireOp",EDGE,"E26"),sQuery(id+"F0.wireOp",EDGE,"E27"),sQuery(id+"F0.wireOp",EDGE,"E28"),sQuery(id+"F0.wireOp",EDGE,"E29"),sQuery(id+"F0.wireOp",EDGE,"E30"),sQuery(id+"F0.wireOp",EDGE,"E31"),sQuery(id+"F0.wireOp",EDGE,"E32"),sQuery(id+"F0.wireOp",EDGE,"E33"),sQuery(id+"F0.wireOp",EDGE,"E34"),sQuery(id+"F0.wireOp",EDGE,"E35"),sQuery(id+"F0.wireOp",EDGE,"E36"),sQuery(id+"F0.wireOp",EDGE,"E37"),sQuery(id+"F0.wireOp",EDGE,"E38"),sQuery(id+"F0.wireOp",EDGE,"E39"),sQuery(id+"F0.wireOp",EDGE,"E40"),sQuery(id+"F0.wireOp",EDGE,"E41"),sQuery(id+"F0.wireOp",EDGE,"E42"),sQuery(id+"F0.wireOp",EDGE,"E43"),sQuery(id+"F0.wireOp",EDGE,"E44"),sQuery(id+"F0.wireOp",EDGE,"E45"),sQuery(id+"F0.wireOp",EDGE,"E46"),sQuery(id+"F0.wireOp",EDGE,"E47"),sQuery(id+"F0.wireOp",EDGE,"E48"),sQuery(id+"F0.wireOp",EDGE,"E49"),sQuery(id+"F0.wireOp",EDGE,"E50"),sQuery(id+"F0.wireOp",EDGE,"E51"),sQuery(id+"F0.wireOp",EDGE,"E52"),sQuery(id+"F0.wireOp",EDGE,"E53"),sQuery(id+"F0.wireOp",EDGE,"E54"),sQuery(id+"F0.wireOp",EDGE,"E55"),sQuery(id+"F0.wireOp",EDGE,"E56"),sQuery(id+"F0.wireOp",EDGE,"E57"),sQuery(id+"F0.wireOp",EDGE,"E58"),sQuery(id+"F0.wireOp",EDGE,"E59"),sQuery(id+"F0.wireOp",EDGE,"E60"),sQuery(id+"F0.wireOp",EDGE,"E61"),sQuery(id+"F0.wireOp",EDGE,"E62"),sQuery(id+"F0.wireOp",EDGE,"E63"),sQuery(id+"F0.wireOp",EDGE,"E64"),sQuery(id+"F0.wireOp",EDGE,"E65"),sQuery(id+"F0.wireOp",EDGE,"E66"),sQuery(id+"F0.wireOp",EDGE,"E67"),sQuery(id+"F0.wireOp",EDGE,"E68"),sQuery(id+"F0.wireOp",EDGE,"E69"),sQuery(id+"F0.wireOp",EDGE,"E70"),sQuery(id+"F0.wireOp",EDGE,"E71"),sQuery(id+"F0.wireOp",EDGE,"E72"),sQuery(id+"F0.wireOp",EDGE,"E73"),sQuery(id+"F0.wireOp",EDGE,"E74"),sQuery(id+"F0.wireOp",EDGE,"E75"),sQuery(id+"F0.wireOp",EDGE,"E76"),sQuery(id+"F0.wireOp",EDGE,"E77"),sQuery(id+"F0.wireOp",EDGE,"E78"),sQuery(id+"F0.wireOp",EDGE,"E79"),sQuery(id+"F0.wireOp",EDGE,"E80"),sQuery(id+"F0.wireOp",EDGE,"E81"),sQuery(id+"F0.wireOp",EDGE,"E82"),sQuery(id+"F0.wireOp",EDGE,"E83"),sQuery(id+"F0.wireOp",EDGE,"E84"),sQuery(id+"F0.wireOp",EDGE,"E85"),sQuery(id+"F0.wireOp",EDGE,"E86"),sQuery(id+"F0.wireOp",EDGE,"E87"),sQuery(id+"F0.wireOp",EDGE,"E88"),sQuery(id+"F0.wireOp",EDGE,"E89"),sQuery(id+"F0.wireOp",EDGE,"E90"),sQuery(id+"F0.wireOp",EDGE,"E91"),sQuery(id+"F0.wireOp",EDGE,"E92"),sQuery(id+"F0.wireOp",EDGE,"E93"),sQuery(id+"F0.wireOp",EDGE,"E94"),sQuery(id+"F0.wireOp",EDGE,"E95"),sQuery(id+"F0.wireOp",EDGE,"E96"),sQuery(id+"F0.wireOp",EDGE,"E97"),sQuery(id+"F0.wireOp",EDGE,"E98"),sQuery(id+"F0.wireOp",EDGE,"E99"),sQuery(id+"F0.wireOp",EDGE,"E100"),sQuery(id+"F0.wireOp",EDGE,"E101"),sQuery(id+"F0.wireOp",EDGE,"E102"),sQuery(id+"F0.wireOp",EDGE,"E103"),sQuery(id+"F0.wireOp",EDGE,"E104"),sQuery(id+"F0.wireOp",EDGE,"E105"),sQuery(id+"F0.wireOp",EDGE,"E106"),sQuery(id+"F0.wireOp",EDGE,"E107"),sQuery(id+"F0.wireOp",EDGE,"E108"),sQuery(id+"F0.wireOp",EDGE,"E109"),sQuery(id+"F0.wireOp",EDGE,"E110"),sQuery(id+"F0.wireOp",EDGE,"E111"),sQuery(id+"F0.wireOp",EDGE,"E112"),sQuery(id+"F0.wireOp",EDGE,"E113"),sQuery(id+"F0.wireOp",EDGE,"E114"),sQuery(id+"F0.wireOp",EDGE,"E115"),sQuery(id+"F0.wireOp",EDGE,"E116"),sQuery(id+"F0.wireOp",EDGE,"E117"),sQuery(id+"F0.wireOp",EDGE,"E118"),sQuery(id+"F0.wireOp",EDGE,"E119"),sQuery(id+"F0.wireOp",EDGE,"E120"),sQuery(id+"F0.wireOp",EDGE,"E121"),sQuery(id+"F0.wireOp",EDGE,"E122"),sQuery(id+"F0.wireOp",EDGE,"E123"),sQuery(id+"F0.wireOp",EDGE,"E124"),sQuery(id+"F0.wireOp",EDGE,"E125"),sQuery(id+"F0.wireOp",EDGE,"E126"),sQuery(id+"F0.wireOp",EDGE,"E127"),sQuery(id+"F0.wireOp",EDGE,"E128"),sQuery(id+"F0.wireOp",EDGE,"E129"),sQuery(id+"F0.wireOp",EDGE,"E130"),sQuery(id+"F0.wireOp",EDGE,"E131"),sQuery(id+"F0.wireOp",EDGE,"E132"),sQuery(id+"F0.wireOp",EDGE,"E133"),sQuery(id+"F0.wireOp",EDGE,"E134"),sQuery(id+"F0.wireOp",EDGE,"E135"),sQuery(id+"F0.wireOp",EDGE,"E136"),sQuery(id+"F0.wireOp",EDGE,"E137"),sQuery(id+"F0.wireOp",EDGE,"E138"),sQuery(id+"F0.wireOp",EDGE,"E139"),sQuery(id+"F0.wireOp",EDGE,"E140"),sQuery(id+"F0.wireOp",EDGE,"E141"),sQuery(id+"F0.wireOp",EDGE,"E142"),sQuery(id+"F0.wireOp",EDGE,"E143"),sQuery(id+"F0.wireOp",EDGE,"E144"),sQuery(id+"F0.wireOp",EDGE,"E145"),sQuery(id+"F0.wireOp",EDGE,"E146"),sQuery(id+"F0.wireOp",EDGE,"E147"),sQuery(id+"F0.wireOp",EDGE,"E148"),sQuery(id+"F0.wireOp",EDGE,"E149"),sQuery(id+"F0.wireOp",EDGE,"E150"),sQuery(id+"F0.wireOp",EDGE,"E151"),sQuery(id+"F0.wireOp",EDGE,"E152"),sQuery(id+"F0.wireOp",EDGE,"E153"),sQuery(id+"F0.wireOp",EDGE,"E154"),sQuery(id+"F0.wireOp",EDGE,"E155"),sQuery(id+"F0.wireOp",EDGE,"E156"),sQuery(id+"F0.wireOp",EDGE,"E157"),sQuery(id+"F0.wireOp",EDGE,"E158"),sQuery(id+"F0.wireOp",EDGE,"E159"),sQuery(id+"F0.wireOp",EDGE,"E160"),sQuery(id+"F0.wireOp",EDGE,"E161"),sQuery(id+"F0.wireOp",EDGE,"E162"),sQuery(id+"F0.wireOp",EDGE,"E163"),sQuery(id+"F0.wireOp",EDGE,"E164"),sQuery(id+"F0.wireOp",EDGE,"E165"),sQuery(id+"F0.wireOp",EDGE,"E166"),sQuery(id+"F0.wireOp",EDGE,"E167"),sQuery(id+"F0.wireOp",EDGE,"E168"),sQuery(id+"F0.wireOp",EDGE,"E169"),sQuery(id+"F0.wireOp",EDGE,"E170"),sQuery(id+"F0.wireOp",EDGE,"E171"),sQuery(id+"F0.wireOp",EDGE,"E172"),sQuery(id+"F0.wireOp",EDGE,"E173"),sQuery(id+"F0.wireOp",EDGE,"E174"),sQuery(id+"F0.wireOp",EDGE,"E175"),sQuery(id+"F0.wireOp",EDGE,"E176"),sQuery(id+"F0.wireOp",EDGE,"E177"),sQuery(id+"F0.wireOp",EDGE,"E178"),sQuery(id+"F0.wireOp",EDGE,"E179"),sQuery(id+"F0.wireOp",EDGE,"E180"),sQuery(id+"F0.wireOp",EDGE,"E181"),sQuery(id+"F0.wireOp",EDGE,"E182"),sQuery(id+"F0.wireOp",EDGE,"E183"),sQuery(id+"F0.wireOp",EDGE,"E184"),sQuery(id+"F0.wireOp",EDGE,"E185"),sQuery(id+"F0.wireOp",EDGE,"E186"),sQuery(id+"F0.wireOp",EDGE,"E187"),sQuery(id+"F0.wireOp",EDGE,"E188"),sQuery(id+"F0.wireOp",EDGE,"E189"),sQuery(id+"F0.wireOp",EDGE,"E190"),sQuery(id+"F0.wireOp",EDGE,"E191"),sQuery(id+"F0.wireOp",EDGE,"E192"),sQuery(id+"F0.wireOp",EDGE,"E193"),sQuery(id+"F0.wireOp",EDGE,"E194"),sQuery(id+"F0.wireOp",EDGE,"E195"),sQuery(id+"F0.wireOp",EDGE,"E196"),sQuery(id+"F0.wireOp",EDGE,"E197"),sQuery(id+"F0.wireOp",EDGE,"E198"),sQuery(id+"F0.wireOp",EDGE,"E199"),sQuery(id+"F0.wireOp",EDGE,"E200"),sQuery(id+"F0.wireOp",EDGE,"E201"),sQuery(id+"F0.wireOp",EDGE,"E202"),sQuery(id+"F0.wireOp",EDGE,"E203"),sQuery(id+"F0.wireOp",EDGE,"E204"),sQuery(id+"F0.wireOp",EDGE,"E205"),sQuery(id+"F0.wireOp",EDGE,"E206"),sQuery(id+"F0.wireOp",EDGE,"E207"),sQuery(id+"F0.wireOp",EDGE,"E208"),sQuery(id+"F0.wireOp",EDGE,"E209"),sQuery(id+"F0.wireOp",EDGE,"E210"),sQuery(id+"F0.wireOp",EDGE,"E211"),sQuery(id+"F0.wireOp",EDGE,"E212"),sQuery(id+"F0.wireOp",EDGE,"E213"),sQuery(id+"F0.wireOp",EDGE,"E214"),sQuery(id+"F0.wireOp",EDGE,"E215"),sQuery(id+"F0.wireOp",EDGE,"E216"),sQuery(id+"F0.wireOp",EDGE,"E217"),sQuery(id+"F0.wireOp",EDGE,"E218"),sQuery(id+"F0.wireOp",EDGE,"E219"),sQuery(id+"F0.wireOp",EDGE,"E220"),sQuery(id+"F0.wireOp",EDGE,"E221"),sQuery(id+"F0.wireOp",EDGE,"E222"),sQuery(id+"F0.wireOp",EDGE,"E223"),sQuery(id+"F0.wireOp",EDGE,"E224"),sQuery(id+"F0.wireOp",EDGE,"E225"),sQuery(id+"F0.wireOp",EDGE,"E226"),sQuery(id+"F0.wireOp",EDGE,"E227"),sQuery(id+"F0.wireOp",EDGE,"E228"),sQuery(id+"F0.wireOp",EDGE,"E229"),sQuery(id+"F0.wireOp",EDGE,"E230"),sQuery(id+"F0.wireOp",EDGE,"E231"),sQuery(id+"F0.wireOp",EDGE,"E232"),sQuery(id+"F0.wireOp",EDGE,"E234"),sQuery(id+"F0.wireOp",EDGE,"E235"),sQuery(id+"F0.wireOp",EDGE,"E236"),sQuery(id+"F0.wireOp",EDGE,"E238"),sQuery(id+"F0.wireOp",EDGE,"E239"),sQuery(id+"F0.wireOp",EDGE,"E240"),sQuery(id+"F0.wireOp",EDGE,"E242"),sQuery(id+"F0.wireOp",EDGE,"E243"),sQuery(id+"F0.wireOp",EDGE,"E244"),sQuery(id+"F0.wireOp",EDGE,"E246"),sQuery(id+"F0.wireOp",EDGE,"E247"),sQuery(id+"F0.wireOp",EDGE,"E248"),sQuery(id+"F0.wireOp",EDGE,"E250"),sQuery(id+"F0.wireOp",EDGE,"E251"),sQuery(id+"F0.wireOp",EDGE,"E252"),sQuery(id+"F0.wireOp",EDGE,"E254"),sQuery(id+"F0.wireOp",EDGE,"E255"),sQuery(id+"F0.wireOp",EDGE,"E256"),sQuery(id+"F0.wireOp",EDGE,"E258"),sQuery(id+"F0.wireOp",EDGE,"E259"),sQuery(id+"F0.wireOp",EDGE,"E260"),sQuery(id+"F0.wireOp",EDGE,"E262"),sQuery(id+"F0.wireOp",EDGE,"E263"),sQuery(id+"F0.wireOp",EDGE,"E264"),sQuery(id+"F0.wireOp",EDGE,"E266"),sQuery(id+"F0.wireOp",EDGE,"E267"),sQuery(id+"F0.wireOp",EDGE,"E268"),sQuery(id+"F0.wireOp",EDGE,"E270"),sQuery(id+"F0.wireOp",EDGE,"E271"),sQuery(id+"F0.wireOp",EDGE,"E272"),sQuery(id+"F0.wireOp",EDGE,"E274"),sQuery(id+"F0.wireOp",EDGE,"E275"),sQuery(id+"F0.wireOp",EDGE,"E276"),sQuery(id+"F0.wireOp",EDGE,"E278"),sQuery(id+"F0.wireOp",EDGE,"E279"),sQuery(id+"F0.wireOp",EDGE,"E280"),sQuery(id+"F0.wireOp",EDGE,"E282"),sQuery(id+"F0.wireOp",EDGE,"E283"),sQuery(id+"F0.wireOp",EDGE,"E284"),sQuery(id+"F0.wireOp",EDGE,"E286"),sQuery(id+"F0.wireOp",EDGE,"E287"),sQuery(id+"F0.wireOp",EDGE,"E288"),sQuery(id+"F0.wireOp",EDGE,"E290"),sQuery(id+"F0.wireOp",EDGE,"E291"),sQuery(id+"F0.wireOp",EDGE,"E292"),sQuery(id+"F0.wireOp",EDGE,"E294"),sQuery(id+"F0.wireOp",EDGE,"E295"),sQuery(id+"F0.wireOp",EDGE,"E296"),sQuery(id+"F0.wireOp",EDGE,"E298"),sQuery(id+"F0.wireOp",EDGE,"E299"),sQuery(id+"F0.wireOp",EDGE,"E300"),sQuery(id+"F0.wireOp",EDGE,"E302"),sQuery(id+"F0.wireOp",EDGE,"E303"),sQuery(id+"F0.wireOp",EDGE,"E304"),sQuery(id+"F0.wireOp",EDGE,"E306"),sQuery(id+"F0.wireOp",EDGE,"E307"),sQuery(id+"F0.wireOp",EDGE,"E308"),sQuery(id+"F0.wireOp",EDGE,"E310"),sQuery(id+"F0.wireOp",EDGE,"E311"),sQuery(id+"F0.wireOp",EDGE,"E312"),sQuery(id+"F0.wireOp",EDGE,"E314"),sQuery(id+"F0.wireOp",EDGE,"E315"),sQuery(id+"F0.wireOp",EDGE,"E316"),sQuery(id+"F0.wireOp",EDGE,"E318"),sQuery(id+"F0.wireOp",EDGE,"E319"),sQuery(id+"F0.wireOp",EDGE,"E320"),sQuery(id+"F0.wireOp",EDGE,"E322"),sQuery(id+"F0.wireOp",EDGE,"E323"),sQuery(id+"F0.wireOp",EDGE,"E324"),sQuery(id+"F0.wireOp",EDGE,"E326"),sQuery(id+"F0.wireOp",EDGE,"E327"),sQuery(id+"F0.wireOp",EDGE,"E328"),sQuery(id+"F0.wireOp",EDGE,"E330"),sQuery(id+"F0.wireOp",EDGE,"E331"),sQuery(id+"F0.wireOp",EDGE,"E332"),sQuery(id+"F0.wireOp",EDGE,"E333"),sQuery(id+"F0.wireOp",EDGE,"E334"),sQuery(id+"F0.wireOp",EDGE,"E335"),sQuery(id+"F0.wireOp",EDGE,"E336"),sQuery(id+"F0.wireOp",EDGE,"E337"),sQuery(id+"F0.wireOp",EDGE,"E338"),sQuery(id+"F0.wireOp",EDGE,"E339"),sQuery(id+"F0.wireOp",EDGE,"E340"),sQuery(id+"F0.wireOp",EDGE,"E341"),sQuery(id+"F0.wireOp",EDGE,"E342"),sQuery(id+"F0.wireOp",EDGE,"E343"),sQuery(id+"F0.wireOp",EDGE,"E344"),sQuery(id+"F0.wireOp",EDGE,"E345"),sQuery(id+"F0.wireOp",EDGE,"E346"),sQuery(id+"F0.wireOp",EDGE,"E347"),sQuery(id+"F0.wireOp",EDGE,"E348"),sQuery(id+"F0.wireOp",EDGE,"E349"),sQuery(id+"F0.wireOp",EDGE,"E350"),sQuery(id+"F0.wireOp",EDGE,"E351"),sQuery(id+"F0.wireOp",EDGE,"E352"),sQuery(id+"F0.wireOp",EDGE,"E353"),sQuery(id+"F0.wireOp",EDGE,"E354"),sQuery(id+"F0.wireOp",EDGE,"E355"),sQuery(id+"F0.wireOp",EDGE,"E356"),sQuery(id+"F0.wireOp",EDGE,"E357"),sQuery(id+"F0.wireOp",EDGE,"E358"),sQuery(id+"F0.wireOp",EDGE,"E359"),sQuery(id+"F0.wireOp",EDGE,"E360"),sQuery(id+"F0.wireOp",EDGE,"E361"),sQuery(id+"F0.wireOp",EDGE,"E362"),sQuery(id+"F0.wireOp",EDGE,"E363"),sQuery(id+"F0.wireOp",EDGE,"E364"),sQuery(id+"F0.wireOp",EDGE,"E365"),sQuery(id+"F0.wireOp",EDGE,"E366"),sQuery(id+"F0.wireOp",EDGE,"E367"),sQuery(id+"F0.wireOp",EDGE,"E368"),sQuery(id+"F0.wireOp",EDGE,"E369"),sQuery(id+"F0.wireOp",EDGE,"E370"),sQuery(id+"F0.wireOp",EDGE,"E371"),sQuery(id+"F0.wireOp",EDGE,"E372"),sQuery(id+"F0.wireOp",EDGE,"E373"),sQuery(id+"F0.wireOp",EDGE,"E374"),sQuery(id+"F0.wireOp",EDGE,"E375"),sQuery(id+"F0.wireOp",EDGE,"E376"),sQuery(id+"F0.wireOp",EDGE,"E377"),sQuery(id+"F0.wireOp",EDGE,"E378"),sQuery(id+"F0.wireOp",EDGE,"E379"),sQuery(id+"F0.wireOp",EDGE,"E380"),sQuery(id+"F0.wireOp",EDGE,"E381"),sQuery(id+"F0.wireOp",EDGE,"E382"),sQuery(id+"F0.wireOp",EDGE,"E383"),sQuery(id+"F0.wireOp",EDGE,"E384"),sQuery(id+"F0.wireOp",EDGE,"E385"),sQuery(id+"F0.wireOp",EDGE,"E386"),sQuery(id+"F0.wireOp",EDGE,"E387"),sQuery(id+"F0.wireOp",EDGE,"E388"),sQuery(id+"F0.wireOp",EDGE,"E389"),sQuery(id+"F0.wireOp",EDGE,"E390"),sQuery(id+"F0.wireOp",EDGE,"E391"),sQuery(id+"F0.wireOp",EDGE,"E392"),sQuery(id+"F0.wireOp",EDGE,"E393"),sQuery(id+"F0.wireOp",EDGE,"E394"),sQuery(id+"F0.wireOp",EDGE,"E395"),sQuery(id+"F0.wireOp",EDGE,"E396"),sQuery(id+"F0.wireOp",EDGE,"E397"),sQuery(id+"F0.wireOp",EDGE,"E398"),sQuery(id+"F0.wireOp",EDGE,"E399"),sQuery(id+"F0.wireOp",EDGE,"E400"),sQuery(id+"F0.wireOp",EDGE,"E401"),sQuery(id+"F0.wireOp",EDGE,"E402"),sQuery(id+"F0.wireOp",EDGE,"E403"),sQuery(id+"F0.wireOp",EDGE,"E404"),sQuery(id+"F0.wireOp",EDGE,"E405"),sQuery(id+"F0.wireOp",EDGE,"E406"),sQuery(id+"F0.wireOp",EDGE,"E407"),sQuery(id+"F0.wireOp",EDGE,"E408"),sQuery(id+"F0.wireOp",EDGE,"E409"),sQuery(id+"F0.wireOp",EDGE,"E410"),sQuery(id+"F0.wireOp",EDGE,"E411"),sQuery(id+"F0.wireOp",EDGE,"E412"),sQuery(id+"F0.wireOp",EDGE,"E413"),sQuery(id+"F0.wireOp",EDGE,"E414"),sQuery(id+"F0.wireOp",EDGE,"E415"),sQuery(id+"F0.wireOp",EDGE,"E416"),sQuery(id+"F0.wireOp",EDGE,"E417"),sQuery(id+"F0.wireOp",EDGE,"E418"),sQuery(id+"F0.wireOp",EDGE,"E419"),sQuery(id+"F0.wireOp",EDGE,"E420"),sQuery(id+"F0.wireOp",EDGE,"E421"),sQuery(id+"F0.wireOp",EDGE,"E422"),sQuery(id+"F0.wireOp",EDGE,"E423"),sQuery(id+"F0.wireOp",EDGE,"E424"),sQuery(id+"F0.wireOp",EDGE,"E425"),sQuery(id+"F0.wireOp",EDGE,"E426"),sQuery(id+"F0.wireOp",EDGE,"E427"),sQuery(id+"F0.wireOp",EDGE,"E428"),sQuery(id+"F0.wireOp",EDGE,"E429"),sQuery(id+"F0.wireOp",EDGE,"E430"),sQuery(id+"F0.wireOp",EDGE,"E431"),sQuery(id+"F0.wireOp",EDGE,"E432"),sQuery(id+"F0.wireOp",EDGE,"E433"),sQuery(id+"F0.wireOp",EDGE,"E434"),sQuery(id+"F0.wireOp",EDGE,"E435"),sQuery(id+"F0.wireOp",EDGE,"E436"),sQuery(id+"F0.wireOp",EDGE,"E437"),sQuery(id+"F0.wireOp",EDGE,"E438"),sQuery(id+"F0.wireOp",EDGE,"E439"),sQuery(id+"F0.wireOp",EDGE,"E440"),sQuery(id+"F0.wireOp",EDGE,"E441"),sQuery(id+"F0.wireOp",EDGE,"E442"),sQuery(id+"F0.wireOp",EDGE,"E443"),sQuery(id+"F0.wireOp",EDGE,"E444"),sQuery(id+"F0.wireOp",EDGE,"E445"),sQuery(id+"F0.wireOp",EDGE,"E446"),sQuery(id+"F0.wireOp",EDGE,"E447"),sQuery(id+"F0.wireOp",EDGE,"E448"),sQuery(id+"F0.wireOp",EDGE,"E449"),sQuery(id+"F0.wireOp",EDGE,"E450"),sQuery(id+"F0.wireOp",EDGE,"E451"),sQuery(id+"F0.wireOp",EDGE,"E452"),sQuery(id+"F0.wireOp",EDGE,"E453"),sQuery(id+"F0.wireOp",EDGE,"E454"),sQuery(id+"F0.wireOp",EDGE,"E455"),sQuery(id+"F0.wireOp",EDGE,"E456"),sQuery(id+"F0.wireOp",EDGE,"E457"),sQuery(id+"F0.wireOp",EDGE,"E458"),sQuery(id+"F0.wireOp",EDGE,"E459"),sQuery(id+"F0.wireOp",EDGE,"E460"),sQuery(id+"F0.wireOp",EDGE,"E461"),sQuery(id+"F0.wireOp",EDGE,"E462"),sQuery(id+"F0.wireOp",EDGE,"E463"),sQuery(id+"F0.wireOp",EDGE,"E464"),sQuery(id+"F0.wireOp",EDGE,"E465"),sQuery(id+"F0.wireOp",EDGE,"E466"),sQuery(id+"F0.wireOp",EDGE,"E467"),sQuery(id+"F0.wireOp",EDGE,"E468"),sQuery(id+"F0.wireOp",EDGE,"E469"),sQuery(id+"F0.wireOp",EDGE,"E470"),sQuery(id+"F0.wireOp",EDGE,"E471"),sQuery(id+"F0.wireOp",EDGE,"E472"),sQuery(id+"F0.wireOp",EDGE,"E473"),sQuery(id+"F0.wireOp",EDGE,"E474"),sQuery(id+"F0.wireOp",EDGE,"E475"),sQuery(id+"F0.wireOp",EDGE,"E476"),sQuery(id+"F0.wireOp",EDGE,"E477"),sQuery(id+"F0.wireOp",EDGE,"E478"),sQuery(id+"F0.wireOp",EDGE,"E479"),sQuery(id+"F0.wireOp",EDGE,"E480"),sQuery(id+"F0.wireOp",EDGE,"E481"),sQuery(id+"F0.wireOp",EDGE,"E482"),sQuery(id+"F0.wireOp",EDGE,"E483"),sQuery(id+"F0.wireOp",EDGE,"E484"),sQuery(id+"F0.wireOp",EDGE,"E485"),sQuery(id+"F0.wireOp",EDGE,"E486"),sQuery(id+"F0.wireOp",EDGE,"E487"),sQuery(id+"F0.wireOp",EDGE,"E488"),sQuery(id+"F0.wireOp",EDGE,"E489"),sQuery(id+"F0.wireOp",EDGE,"E490"),sQuery(id+"F0.wireOp",EDGE,"E491"),sQuery(id+"F0.wireOp",EDGE,"E492"),sQuery(id+"F0.wireOp",EDGE,"E493"),sQuery(id+"F0.wireOp",EDGE,"E494"),sQuery(id+"F0.wireOp",EDGE,"E495"),sQuery(id+"F0.wireOp",EDGE,"E496"),sQuery(id+"F0.wireOp",EDGE,"E497"),sQuery(id+"F0.wireOp",EDGE,"E498"),sQuery(id+"F0.wireOp",EDGE,"E499"),sQuery(id+"F0.wireOp",EDGE,"E500"),sQuery(id+"F0.wireOp",EDGE,"E501"),sQuery(id+"F0.wireOp",EDGE,"E502"),sQuery(id+"F0.wireOp",EDGE,"E503"),sQuery(id+"F0.wireOp",EDGE,"E504"),sQuery(id+"F0.wireOp",EDGE,"E505"),sQuery(id+"F0.wireOp",EDGE,"E506"),sQuery(id+"F0.wireOp",EDGE,"E507"),sQuery(id+"F0.wireOp",EDGE,"E508"),sQuery(id+"F0.wireOp",EDGE,"E509"),sQuery(id+"F0.wireOp",EDGE,"E510"),sQuery(id+"F0.wireOp",EDGE,"E511"),sQuery(id+"F0.wireOp",EDGE,"E512"),sQuery(id+"F0.wireOp",EDGE,"E513"),sQuery(id+"F0.wireOp",EDGE,"E514"),sQuery(id+"F0.wireOp",EDGE,"E515"),sQuery(id+"F0.wireOp",EDGE,"E516"),sQuery(id+"F0.wireOp",EDGE,"E517"),sQuery(id+"F0.wireOp",EDGE,"E518"),sQuery(id+"F0.wireOp",EDGE,"E519"),sQuery(id+"F0.wireOp",EDGE,"E520"),sQuery(id+"F0.wireOp",EDGE,"E521"),sQuery(id+"F0.wireOp",EDGE,"E522"),sQuery(id+"F0.wireOp",EDGE,"E523"),sQuery(id+"F0.wireOp",EDGE,"E524"),sQuery(id+"F0.wireOp",EDGE,"E525"),sQuery(id+"F0.wireOp",EDGE,"E526"),sQuery(id+"F0.wireOp",EDGE,"E527"),sQuery(id+"F0.wireOp",EDGE,"E528"),sQuery(id+"F0.wireOp",EDGE,"E529"),sQuery(id+"F0.wireOp",EDGE,"E530"),sQuery(id+"F0.wireOp",EDGE,"E531"),sQuery(id+"F0.wireOp",EDGE,"E532"),sQuery(id+"F0.wireOp",EDGE,"E533"),sQuery(id+"F0.wireOp",EDGE,"E534"),sQuery(id+"F0.wireOp",EDGE,"E535"),sQuery(id+"F0.wireOp",EDGE,"E536"),sQuery(id+"F0.wireOp",EDGE,"E537"),sQuery(id+"F0.wireOp",EDGE,"E538"),sQuery(id+"F0.wireOp",EDGE,"E539"),sQuery(id+"F0.wireOp",EDGE,"E540"),sQuery(id+"F0.wireOp",EDGE,"E541"),sQuery(id+"F0.wireOp",EDGE,"E542"),sQuery(id+"F0.wireOp",EDGE,"E543"),sQuery(id+"F0.wireOp",EDGE,"E544"),sQuery(id+"F0.wireOp",EDGE,"E545"),sQuery(id+"F0.wireOp",EDGE,"E546"),sQuery(id+"F0.wireOp",EDGE,"E547"),sQuery(id+"F0.wireOp",EDGE,"E548"),sQuery(id+"F0.wireOp",EDGE,"E549"),sQuery(id+"F0.wireOp",EDGE,"E550"),sQuery(id+"F0.wireOp",EDGE,"E551"),sQuery(id+"F0.wireOp",EDGE,"E552"),sQuery(id+"F0.wireOp",EDGE,"E553"),sQuery(id+"F0.wireOp",EDGE,"E554"),sQuery(id+"F0.wireOp",EDGE,"E555"),sQuery(id+"F0.wireOp",EDGE,"E556"),sQuery(id+"F0.wireOp",EDGE,"E557"),sQuery(id+"F0.wireOp",EDGE,"E558"),sQuery(id+"F0.wireOp",EDGE,"E559"),sQuery(id+"F0.wireOp",EDGE,"E560"),sQuery(id+"F0.wireOp",EDGE,"E561"),sQuery(id+"F0.wireOp",EDGE,"E562"),sQuery(id+"F0.wireOp",EDGE,"E563"),sQuery(id+"F0.wireOp",EDGE,"E564"),sQuery(id+"F0.wireOp",EDGE,"E565"),sQuery(id+"F0.wireOp",EDGE,"E566"),sQuery(id+"F0.wireOp",EDGE,"E567"),sQuery(id+"F0.wireOp",EDGE,"E568"),sQuery(id+"F0.wireOp",EDGE,"E569"),sQuery(id+"F0.wireOp",EDGE,"E570"),sQuery(id+"F0.wireOp",EDGE,"E571"),sQuery(id+"F0.wireOp",EDGE,"E572"),sQuery(id+"F0.wireOp",EDGE,"E573"),sQuery(id+"F0.wireOp",EDGE,"E574"),sQuery(id+"F0.wireOp",EDGE,"E575"),sQuery(id+"F0.wireOp",EDGE,"E576"),sQuery(id+"F0.wireOp",EDGE,"E577"),sQuery(id+"F0.wireOp",EDGE,"E578"),sQuery(id+"F0.wireOp",EDGE,"E579"),sQuery(id+"F0.wireOp",EDGE,"E580"),sQuery(id+"F0.wireOp",EDGE,"E581"),sQuery(id+"F0.wireOp",EDGE,"E582"),sQuery(id+"F0.wireOp",EDGE,"E583"),sQuery(id+"F0.wireOp",EDGE,"E584"),sQuery(id+"F0.wireOp",EDGE,"E585"),sQuery(id+"F0.wireOp",EDGE,"E586"),sQuery(id+"F0.wireOp",EDGE,"E587"),sQuery(id+"F0.wireOp",EDGE,"E588"),sQuery(id+"F0.wireOp",EDGE,"E589"),sQuery(id+"F0.wireOp",EDGE,"E590"),sQuery(id+"F0.wireOp",EDGE,"E591"),sQuery(id+"F0.wireOp",EDGE,"E592"),sQuery(id+"F0.wireOp",EDGE,"E593"),sQuery(id+"F0.wireOp",EDGE,"E594"),sQuery(id+"F0.wireOp",EDGE,"E595"),sQuery(id+"F0.wireOp",EDGE,"E596"),sQuery(id+"F0.wireOp",EDGE,"E597"),sQuery(id+"F0.wireOp",EDGE,"E598"),sQuery(id+"F0.wireOp",EDGE,"E599"),sQuery(id+"F0.wireOp",EDGE,"E600"),sQuery(id+"F0.wireOp",EDGE,"E601"),sQuery(id+"F0.wireOp",EDGE,"E602"),sQuery(id+"F0.wireOp",EDGE,"E603"),sQuery(id+"F0.wireOp",EDGE,"E604"),sQuery(id+"F0.wireOp",EDGE,"E605"),sQuery(id+"F0.wireOp",EDGE,"E606"),sQuery(id+"F0.wireOp",EDGE,"E607"),sQuery(id+"F0.wireOp",EDGE,"E608"),sQuery(id+"F0.wireOp",EDGE,"E609"),sQuery(id+"F0.wireOp",EDGE,"E610"),sQuery(id+"F0.wireOp",EDGE,"E611"),sQuery(id+"F0.wireOp",EDGE,"E612"),sQuery(id+"F0.wireOp",EDGE,"E613"),sQuery(id+"F0.wireOp",EDGE,"E614"),sQuery(id+"F0.wireOp",EDGE,"E615"),sQuery(id+"F0.wireOp",EDGE,"E616"),sQuery(id+"F0.wireOp",EDGE,"E617"),sQuery(id+"F0.wireOp",EDGE,"E618"),sQuery(id+"F0.wireOp",EDGE,"E619"),sQuery(id+"F0.wireOp",EDGE,"E620"),sQuery(id+"F0.wireOp",EDGE,"E621"),sQuery(id+"F0.wireOp",EDGE,"E622"),sQuery(id+"F0.wireOp",EDGE,"E623"),sQuery(id+"F0.wireOp",EDGE,"E624"),sQuery(id+"F0.wireOp",EDGE,"E625"),sQuery(id+"F0.wireOp",EDGE,"E626"),sQuery(id+"F0.wireOp",EDGE,"E627"),sQuery(id+"F0.wireOp",EDGE,"E628"),sQuery(id+"F0.wireOp",EDGE,"E629"),sQuery(id+"F0.wireOp",EDGE,"E630"),sQuery(id+"F0.wireOp",EDGE,"E631"),sQuery(id+"F0.wireOp",EDGE,"E632"),sQuery(id+"F0.wireOp",EDGE,"E633"),sQuery(id+"F0.wireOp",EDGE,"E634"),sQuery(id+"F0.wireOp",EDGE,"E635"),sQuery(id+"F0.wireOp",EDGE,"E636"),sQuery(id+"F0.wireOp",EDGE,"E637"),sQuery(id+"F0.wireOp",EDGE,"E638"),sQuery(id+"F0.wireOp",EDGE,"E639"),sQuery(id+"F0.wireOp",EDGE,"E640"),sQuery(id+"F0.wireOp",EDGE,"E641"),sQuery(id+"F0.wireOp",EDGE,"E642"),sQuery(id+"F0.wireOp",EDGE,"E643"),sQuery(id+"F0.wireOp",EDGE,"E644"),sQuery(id+"F0.wireOp",EDGE,"E645"),sQuery(id+"F0.wireOp",EDGE,"E646"),sQuery(id+"F0.wireOp",EDGE,"E647"),sQuery(id+"F0.wireOp",EDGE,"E648"),sQuery(id+"F0.wireOp",EDGE,"E649"),sQuery(id+"F0.wireOp",EDGE,"E650"),sQuery(id+"F0.wireOp",EDGE,"E651"),sQuery(id+"F0.wireOp",EDGE,"E652"),sQuery(id+"F0.wireOp",EDGE,"E653"),sQuery(id+"F0.wireOp",EDGE,"E654"),sQuery(id+"F0.wireOp",EDGE,"E655"),sQuery(id+"F0.wireOp",EDGE,"E656"),sQuery(id+"F0.wireOp",EDGE,"E657"),sQuery(id+"F0.wireOp",EDGE,"E658"),sQuery(id+"F0.wireOp",EDGE,"E659"),sQuery(id+"F0.wireOp",EDGE,"E660"),sQuery(id+"F0.wireOp",EDGE,"E661"),sQuery(id+"F0.wireOp",EDGE,"E662"),sQuery(id+"F0.wireOp",EDGE,"E663"),sQuery(id+"F0.wireOp",EDGE,"E664"),sQuery(id+"F0.wireOp",EDGE,"E665"),sQuery(id+"F0.wireOp",EDGE,"E666"),sQuery(id+"F0.wireOp",EDGE,"E667"),sQuery(id+"F0.wireOp",EDGE,"E668"),sQuery(id+"F0.wireOp",EDGE,"E669"),sQuery(id+"F0.wireOp",EDGE,"E670"),sQuery(id+"F0.wireOp",EDGE,"E671"),sQuery(id+"F0.wireOp",EDGE,"E672"),sQuery(id+"F0.wireOp",EDGE,"E673"),sQuery(id+"F0.wireOp",EDGE,"E674"),sQuery(id+"F0.wireOp",EDGE,"E675"),sQuery(id+"F0.wireOp",EDGE,"E676"),sQuery(id+"F0.wireOp",EDGE,"E677"),sQuery(id+"F0.wireOp",EDGE,"E678"),sQuery(id+"F0.wireOp",EDGE,"E679"),sQuery(id+"F0.wireOp",EDGE,"E680"),sQuery(id+"F0.wireOp",EDGE,"E681"),sQuery(id+"F0.wireOp",EDGE,"E682"),sQuery(id+"F0.wireOp",EDGE,"E683"),sQuery(id+"F0.wireOp",EDGE,"E684"),sQuery(id+"F0.wireOp",EDGE,"E685"),sQuery(id+"F0.wireOp",EDGE,"E686"),sQuery(id+"F0.wireOp",EDGE,"E687"),sQuery(id+"F0.wireOp",EDGE,"E688"),sQuery(id+"F0.wireOp",EDGE,"E689"),sQuery(id+"F0.wireOp",EDGE,"E690"),sQuery(id+"F0.wireOp",EDGE,"E691"),sQuery(id+"F0.wireOp",EDGE,"E692"),sQuery(id+"F0.wireOp",EDGE,"E693"),sQuery(id+"F0.wireOp",EDGE,"E694"),sQuery(id+"F0.wireOp",EDGE,"E695"),sQuery(id+"F0.wireOp",EDGE,"E696"),sQuery(id+"F0.wireOp",EDGE,"E697"),sQuery(id+"F0.wireOp",EDGE,"E698"),sQuery(id+"F0.wireOp",EDGE,"E699"),sQuery(id+"F0.wireOp",EDGE,"E700"),sQuery(id+"F0.wireOp",EDGE,"E701"),sQuery(id+"F0.wireOp",EDGE,"E702"),sQuery(id+"F0.wireOp",EDGE,"E703"),sQuery(id+"F0.wireOp",EDGE,"E704"),sQuery(id+"F0.wireOp",EDGE,"E705"),sQuery(id+"F0.wireOp",EDGE,"E706"),sQuery(id+"F0.wireOp",EDGE,"E707"),sQuery(id+"F0.wireOp",EDGE,"E708"),sQuery(id+"F0.wireOp",EDGE,"E709"),sQuery(id+"F0.wireOp",EDGE,"E710"),sQuery(id+"F0.wireOp",EDGE,"E711"),sQuery(id+"F0.wireOp",EDGE,"E712"),sQuery(id+"F0.wireOp",EDGE,"E713"),sQuery(id+"F0.wireOp",EDGE,"E714"),sQuery(id+"F0.wireOp",EDGE,"E715"),sQuery(id+"F0.wireOp",EDGE,"E716"),sQuery(id+"F0.wireOp",EDGE,"E717"),sQuery(id+"F0.wireOp",EDGE,"E718"),sQuery(id+"F0.wireOp",EDGE,"E719"),sQuery(id+"F0.wireOp",EDGE,"E720"),sQuery(id+"F0.wireOp",EDGE,"E721"),sQuery(id+"F0.wireOp",EDGE,"E722"),sQuery(id+"F0.wireOp",EDGE,"E723"),sQuery(id+"F0.wireOp",EDGE,"E724"),sQuery(id+"F0.wireOp",EDGE,"E725"),sQuery(id+"F0.wireOp",EDGE,"E726"),sQuery(id+"F0.wireOp",EDGE,"E727"),sQuery(id+"F0.wireOp",EDGE,"E728"),sQuery(id+"F0.wireOp",EDGE,"E729"),sQuery(id+"F0.wireOp",EDGE,"E730"),sQuery(id+"F0.wireOp",EDGE,"E731"),sQuery(id+"F0.wireOp",EDGE,"E732"),sQuery(id+"F0.wireOp",EDGE,"E733"),sQuery(id+"F0.wireOp",EDGE,"E734"),sQuery(id+"F0.wireOp",EDGE,"E735"),sQuery(id+"F0.wireOp",EDGE,"E736"),sQuery(id+"F0.wireOp",EDGE,"E737"),sQuery(id+"F0.wireOp",EDGE,"E738"),sQuery(id+"F0.wireOp",EDGE,"E739"),sQuery(id+"F0.wireOp",EDGE,"E740"),sQuery(id+"F0.wireOp",EDGE,"E741"),sQuery(id+"F0.wireOp",EDGE,"E742"),sQuery(id+"F0.wireOp",EDGE,"E743"),sQuery(id+"F0.wireOp",EDGE,"E744"),sQuery(id+"F0.wireOp",EDGE,"E745"),sQuery(id+"F0.wireOp",EDGE,"E746"),sQuery(id+"F0.wireOp",EDGE,"E747"),sQuery(id+"F0.wireOp",EDGE,"E748"),sQuery(id+"F0.wireOp",EDGE,"E749"),sQuery(id+"F0.wireOp",EDGE,"E750"),sQuery(id+"F0.wireOp",EDGE,"E751"),sQuery(id+"F0.wireOp",EDGE,"E752"),sQuery(id+"F0.wireOp",EDGE,"E753"),sQuery(id+"F0.wireOp",EDGE,"E754"),sQuery(id+"F0.wireOp",EDGE,"E755"),sQuery(id+"F0.wireOp",EDGE,"E756"),sQuery(id+"F0.wireOp",EDGE,"E757"),sQuery(id+"F0.wireOp",EDGE,"E758"),sQuery(id+"F0.wireOp",EDGE,"E759"),sQuery(id+"F0.wireOp",EDGE,"E760"),sQuery(id+"F0.wireOp",EDGE,"E761"),sQuery(id+"F0.wireOp",EDGE,"E762"),sQuery(id+"F0.wireOp",EDGE,"E763"),sQuery(id+"F0.wireOp",EDGE,"E764"),sQuery(id+"F0.wireOp",EDGE,"E765"),sQuery(id+"F0.wireOp",EDGE,"E766"),sQuery(id+"F0.wireOp",EDGE,"E767"),sQuery(id+"F0.wireOp",EDGE,"E768"),sQuery(id+"F0.wireOp",EDGE,"E769"),sQuery(id+"F0.wireOp",EDGE,"E770"),sQuery(id+"F0.wireOp",EDGE,"E771"),sQuery(id+"F0.wireOp",EDGE,"E772"),sQuery(id+"F0.wireOp",EDGE,"E773"),sQuery(id+"F0.wireOp",EDGE,"E774"),sQuery(id+"F0.wireOp",EDGE,"E775"),sQuery(id+"F0.wireOp",EDGE,"E776"),sQuery(id+"F0.wireOp",EDGE,"E777"),sQuery(id+"F0.wireOp",EDGE,"E778"),sQuery(id+"F0.wireOp",EDGE,"E779"),sQuery(id+"F0.wireOp",EDGE,"E780"),sQuery(id+"F0.wireOp",EDGE,"E781"),sQuery(id+"F0.wireOp",EDGE,"E782"),sQuery(id+"F0.wireOp",EDGE,"E783"),sQuery(id+"F0.wireOp",EDGE,"E784"),sQuery(id+"F0.wireOp",EDGE,"E785"),sQuery(id+"F0.wireOp",EDGE,"E786"),sQuery(id+"F0.wireOp",EDGE,"E787"),sQuery(id+"F0.wireOp",EDGE,"E788"),sQuery(id+"F0.wireOp",EDGE,"E789"),sQuery(id+"F0.wireOp",EDGE,"E790"),sQuery(id+"F0.wireOp",EDGE,"E791"),sQuery(id+"F0.wireOp",EDGE,"E792"),sQuery(id+"F0.wireOp",EDGE,"E793"),sQuery(id+"F0.wireOp",EDGE,"E794"),sQuery(id+"F0.wireOp",EDGE,"E795"),sQuery(id+"F0.wireOp",EDGE,"E796"),sQuery(id+"F0.wireOp",EDGE,"E797"),sQuery(id+"F0.wireOp",EDGE,"E798"),sQuery(id+"F0.wireOp",EDGE,"E799"),sQuery(id+"F0.wireOp",EDGE,"E800"),sQuery(id+"F0.wireOp",EDGE,"E801"),sQuery(id+"F0.wireOp",EDGE,"E802"),sQuery(id+"F0.wireOp",EDGE,"E803"),sQuery(id+"F0.wireOp",EDGE,"E804"),sQuery(id+"F0.wireOp",EDGE,"E805"),sQuery(id+"F0.wireOp",EDGE,"E806"),sQuery(id+"F0.wireOp",EDGE,"E807"),sQuery(id+"F0.wireOp",EDGE,"E808"),sQuery(id+"F0.wireOp",EDGE,"E809"),sQuery(id+"F0.wireOp",EDGE,"E810"),sQuery(id+"F0.wireOp",EDGE,"E811"),sQuery(id+"F0.wireOp",EDGE,"E812"),sQuery(id+"F0.wireOp",EDGE,"E813"),sQuery(id+"F0.wireOp",EDGE,"E814"),sQuery(id+"F0.wireOp",EDGE,"E815"),sQuery(id+"F0.wireOp",EDGE,"E816"),sQuery(id+"F0.wireOp",EDGE,"E817"),sQuery(id+"F0.wireOp",EDGE,"E818"),sQuery(id+"F0.wireOp",EDGE,"E819"),sQuery(id+"F0.wireOp",EDGE,"E820"),sQuery(id+"F0.wireOp",EDGE,"E821"),sQuery(id+"F0.wireOp",EDGE,"E822"),sQuery(id+"F0.wireOp",EDGE,"E823"),sQuery(id+"F0.wireOp",EDGE,"E824"),sQuery(id+"F0.wireOp",EDGE,"E825"),sQuery(id+"F0.wireOp",EDGE,"E826"),sQuery(id+"F0.wireOp",EDGE,"E827"),sQuery(id+"F0.wireOp",EDGE,"E828"),sQuery(id+"F0.wireOp",EDGE,"E829"),sQuery(id+"F0.wireOp",EDGE,"E830"),sQuery(id+"F0.wireOp",EDGE,"E831"),sQuery(id+"F0.wireOp",EDGE,"E832"),sQuery(id+"F0.wireOp",EDGE,"E833"),sQuery(id+"F0.wireOp",EDGE,"E834"),sQuery(id+"F0.wireOp",EDGE,"E835"),sQuery(id+"F0.wireOp",EDGE,"E836"),sQuery(id+"F0.wireOp",EDGE,"E837"),sQuery(id+"F0.wireOp",EDGE,"E838"),sQuery(id+"F0.wireOp",EDGE,"E839"),sQuery(id+"F0.wireOp",EDGE,"E840"),sQuery(id+"F0.wireOp",EDGE,"E841"),sQuery(id+"F0.wireOp",EDGE,"E842"),sQuery(id+"F0.wireOp",EDGE,"E843"),sQuery(id+"F0.wireOp",EDGE,"E844"),sQuery(id+"F0.wireOp",EDGE,"E845"),sQuery(id+"F0.wireOp",EDGE,"E846"),sQuery(id+"F0.wireOp",EDGE,"E847"),sQuery(id+"F0.wireOp",EDGE,"E848"),sQuery(id+"F0.wireOp",EDGE,"E849"),sQuery(id+"F0.wireOp",EDGE,"E850"),sQuery(id+"F0.wireOp",EDGE,"E851"),sQuery(id+"F0.wireOp",EDGE,"E852"),sQuery(id+"F0.wireOp",EDGE,"E853"),sQuery(id+"F0.wireOp",EDGE,"E854"),sQuery(id+"F0.wireOp",EDGE,"E855"),sQuery(id+"F0.wireOp",EDGE,"E856"),sQuery(id+"F0.wireOp",EDGE,"E857"),sQuery(id+"F0.wireOp",EDGE,"E858"),sQuery(id+"F0.wireOp",EDGE,"E859"),sQuery(id+"F0.wireOp",EDGE,"E860"),sQuery(id+"F0.wireOp",EDGE,"E861"),sQuery(id+"F0.wireOp",EDGE,"E862"),sQuery(id+"F0.wireOp",EDGE,"E863"),sQuery(id+"F0.wireOp",EDGE,"E864"),sQuery(id+"F0.wireOp",EDGE,"E865"),sQuery(id+"F0.wireOp",EDGE,"E866"),sQuery(id+"F0.wireOp",EDGE,"E867"),sQuery(id+"F0.wireOp",EDGE,"E868"),sQuery(id+"F0.wireOp",EDGE,"E869"),sQuery(id+"F0.wireOp",EDGE,"E870"),sQuery(id+"F0.wireOp",EDGE,"E871"),sQuery(id+"F0.wireOp",EDGE,"E872"),sQuery(id+"F0.wireOp",EDGE,"E873"),sQuery(id+"F0.wireOp",EDGE,"E874"),sQuery(id+"F0.wireOp",EDGE,"E875"),sQuery(id+"F0.wireOp",EDGE,"E876"),sQuery(id+"F0.wireOp",EDGE,"E877"),sQuery(id+"F0.wireOp",EDGE,"E878"),sQuery(id+"F0.wireOp",EDGE,"E879"),sQuery(id+"F0.wireOp",EDGE,"E880"),sQuery(id+"F0.wireOp",EDGE,"E881"),sQuery(id+"F0.wireOp",EDGE,"E882"),sQuery(id+"F0.wireOp",EDGE,"E883"),sQuery(id+"F0.wireOp",EDGE,"E884"),sQuery(id+"F0.wireOp",EDGE,"E885"),sQuery(id+"F0.wireOp",EDGE,"E886"),sQuery(id+"F0.wireOp",EDGE,"E887"),sQuery(id+"F0.wireOp",EDGE,"E888"),sQuery(id+"F0.wireOp",EDGE,"E889"),sQuery(id+"F0.wireOp",EDGE,"E890"),sQuery(id+"F0.wireOp",EDGE,"E891"),sQuery(id+"F0.wireOp",EDGE,"E892"),sQuery(id+"F0.wireOp",EDGE,"E893"),sQuery(id+"F0.wireOp",EDGE,"E894"),sQuery(id+"F0.wireOp",EDGE,"E895"),sQuery(id+"F0.wireOp",EDGE,"E896"),sQuery(id+"F0.wireOp",EDGE,"E897"),sQuery(id+"F0.wireOp",EDGE,"E898"),sQuery(id+"F0.wireOp",EDGE,"E899"),sQuery(id+"F0.wireOp",EDGE,"E900"),sQuery(id+"F0.wireOp",EDGE,"E901"),sQuery(id+"F0.wireOp",EDGE,"E902"),sQuery(id+"F0.wireOp",EDGE,"E903"),sQuery(id+"F0.wireOp",EDGE,"E904"),sQuery(id+"F0.wireOp",EDGE,"E905"),sQuery(id+"F0.wireOp",EDGE,"E906"),sQuery(id+"F0.wireOp",EDGE,"E907"),sQuery(id+"F0.wireOp",EDGE,"E908"),sQuery(id+"F0.wireOp",EDGE,"E909"),sQuery(id+"F0.wireOp",EDGE,"E910"),sQuery(id+"F0.wireOp",EDGE,"E911"),sQuery(id+"F0.wireOp",EDGE,"E912"),sQuery(id+"F0.wireOp",EDGE,"E913"),sQuery(id+"F0.wireOp",EDGE,"E914"),sQuery(id+"F0.wireOp",EDGE,"E915"),sQuery(id+"F0.wireOp",EDGE,"E916"),sQuery(id+"F0.wireOp",EDGE,"E917"),sQuery(id+"F0.wireOp",EDGE,"E918"),sQuery(id+"F0.wireOp",EDGE,"E919"),sQuery(id+"F0.wireOp",EDGE,"E920"),sQuery(id+"F0.wireOp",EDGE,"E921"),sQuery(id+"F0.wireOp",EDGE,"E922"),sQuery(id+"F0.wireOp",EDGE,"E923"),sQuery(id+"F0.wireOp",EDGE,"E924"),sQuery(id+"F0.wireOp",EDGE,"E925"),sQuery(id+"F0.wireOp",EDGE,"E926"),sQuery(id+"F0.wireOp",EDGE,"E927"),sQuery(id+"F0.wireOp",EDGE,"E928"),sQuery(id+"F0.wireOp",EDGE,"E929"),sQuery(id+"F0.wireOp",EDGE,"E930"),sQuery(id+"F0.wireOp",EDGE,"E931"),sQuery(id+"F0.wireOp",EDGE,"E932"),sQuery(id+"F0.wireOp",EDGE,"E933"),sQuery(id+"F0.wireOp",EDGE,"E934"),sQuery(id+"F0.wireOp",EDGE,"E935"),sQuery(id+"F0.wireOp",EDGE,"E936"),sQuery(id+"F0.wireOp",EDGE,"E937"),sQuery(id+"F0.wireOp",EDGE,"E938"),sQuery(id+"F0.wireOp",EDGE,"E939"),sQuery(id+"F0.wireOp",EDGE,"E940"),sQuery(id+"F0.wireOp",EDGE,"E941"),sQuery(id+"F0.wireOp",EDGE,"E942"),sQuery(id+"F0.wireOp",EDGE,"E943"),sQuery(id+"F0.wireOp",EDGE,"E944"),sQuery(id+"F0.wireOp",EDGE,"E945"),sQuery(id+"F0.wireOp",EDGE,"E946"),sQuery(id+"F0.wireOp",EDGE,"E947"),sQuery(id+"F0.wireOp",EDGE,"E948"),sQuery(id+"F0.wireOp",EDGE,"E949"),sQuery(id+"F0.wireOp",EDGE,"E950"),sQuery(id+"F0.wireOp",EDGE,"E951"),sQuery(id+"F0.wireOp",EDGE,"E952"),sQuery(id+"F0.wireOp",EDGE,"E953"),sQuery(id+"F0.wireOp",EDGE,"E954"),sQuery(id+"F0.wireOp",EDGE,"E955"),sQuery(id+"F0.wireOp",EDGE,"E956"),sQuery(id+"F0.wireOp",EDGE,"E957"),sQuery(id+"F0.wireOp",EDGE,"E958"),sQuery(id+"F0.wireOp",EDGE,"E959"),sQuery(id+"F0.wireOp",EDGE,"E960"),sQuery(id+"F0.wireOp",EDGE,"E961"),sQuery(id+"F0.wireOp",EDGE,"E962"),sQuery(id+"F0.wireOp",EDGE,"E963"),sQuery(id+"F0.wireOp",EDGE,"E964"),sQuery(id+"F0.wireOp",EDGE,"E965"),sQuery(id+"F0.wireOp",EDGE,"E966"),sQuery(id+"F0.wireOp",EDGE,"E967"),sQuery(id+"F0.wireOp",EDGE,"E968"),sQuery(id+"F0.wireOp",EDGE,"E969"),sQuery(id+"F0.wireOp",EDGE,"E970"),sQuery(id+"F0.wireOp",EDGE,"E971"),sQuery(id+"F0.wireOp",EDGE,"E972"),sQuery(id+"F0.wireOp",EDGE,"E973"),sQuery(id+"F0.wireOp",EDGE,"E974"),sQuery(id+"F0.wireOp",EDGE,"E975"),sQuery(id+"F0.wireOp",EDGE,"E976"),sQuery(id+"F0.wireOp",EDGE,"E977"),sQuery(id+"F0.wireOp",EDGE,"E978"),sQuery(id+"F0.wireOp",EDGE,"E979"),sQuery(id+"F0.wireOp",EDGE,"E980"),sQuery(id+"F0.wireOp",EDGE,"E981"),sQuery(id+"F0.wireOp",EDGE,"E982"),sQuery(id+"F0.wireOp",EDGE,"E983"),sQuery(id+"F0.wireOp",EDGE,"E984"),sQuery(id+"F0.wireOp",EDGE,"E985"),sQuery(id+"F0.wireOp",EDGE,"E986"),sQuery(id+"F0.wireOp",EDGE,"E987"),sQuery(id+"F0.wireOp",EDGE,"E988"),sQuery(id+"F0.wireOp",EDGE,"E989"),sQuery(id+"F0.wireOp",EDGE,"E990"),sQuery(id+"F0.wireOp",EDGE,"E991"),sQuery(id+"F0.wireOp",EDGE,"E992"),sQuery(id+"F0.wireOp",EDGE,"E993"),sQuery(id+"F0.wireOp",EDGE,"E994"),sQuery(id+"F0.wireOp",EDGE,"E995"),sQuery(id+"F0.wireOp",EDGE,"E996"),sQuery(id+"F0.wireOp",EDGE,"E997"),sQuery(id+"F0.wireOp",EDGE,"E998"),sQuery(id+"F0.wireOp",EDGE,"E999"),sQuery(id+"F0.wireOp",EDGE,"E1000"),sQuery(id+"F0.wireOp",EDGE,"E1001"),sQuery(id+"F0.wireOp",EDGE,"E1002"),sQuery(id+"F0.wireOp",EDGE,"E1003"),sQuery(id+"F0.wireOp",EDGE,"E1004"),sQuery(id+"F0.wireOp",EDGE,"E1005"),sQuery(id+"F0.wireOp",EDGE,"E1006"),sQuery(id+"F0.wireOp",EDGE,"E1007"),sQuery(id+"F0.wireOp",EDGE,"E1008"),sQuery(id+"F0.wireOp",EDGE,"E1009"),sQuery(id+"F0.wireOp",EDGE,"E1010"),sQuery(id+"F0.wireOp",EDGE,"E1011"),sQuery(id+"F0.wireOp",EDGE,"E1012"),sQuery(id+"F0.wireOp",EDGE,"E1013"),sQuery(id+"F0.wireOp",EDGE,"E1014"),sQuery(id+"F0.wireOp",EDGE,"E1015"),sQuery(id+"F0.wireOp",EDGE,"E1016"),sQuery(id+"F0.wireOp",EDGE,"E1017"),sQuery(id+"F0.wireOp",EDGE,"E1018"),sQuery(id+"F0.wireOp",EDGE,"E1019"),sQuery(id+"F0.wireOp",EDGE,"E1020"),sQuery(id+"F0.wireOp",EDGE,"E1021"),sQuery(id+"F0.wireOp",EDGE,"E1022"),sQuery(id+"F0.wireOp",EDGE,"E1023"),sQuery(id+"F0.wireOp",EDGE,"E1024"),sQuery(id+"F0.wireOp",EDGE,"E1025"),sQuery(id+"F0.wireOp",EDGE,"E1026"),sQuery(id+"F0.wireOp",EDGE,"E1027"),sQuery(id+"F0.wireOp",EDGE,"E1028"),sQuery(id+"F0.wireOp",EDGE,"E1029"),sQuery(id+"F0.wireOp",EDGE,"E1030"),sQuery(id+"F0.wireOp",EDGE,"E1031"),sQuery(id+"F0.wireOp",EDGE,"E1032"),sQuery(id+"F0.wireOp",EDGE,"E1033"),sQuery(id+"F0.wireOp",EDGE,"E1034"),sQuery(id+"F0.wireOp",EDGE,"E1035"),sQuery(id+"F0.wireOp",EDGE,"E1036"),sQuery(id+"F0.wireOp",EDGE,"E1037"),sQuery(id+"F0.wireOp",EDGE,"E1038"),sQuery(id+"F0.wireOp",EDGE,"E1039"),sQuery(id+"F0.wireOp",EDGE,"E1040"),sQuery(id+"F0.wireOp",EDGE,"E1041"),sQuery(id+"F0.wireOp",EDGE,"E1042"),sQuery(id+"F0.wireOp",EDGE,"E1043"),sQuery(id+"F0.wireOp",EDGE,"E1044"),sQuery(id+"F0.wireOp",EDGE,"E1045"),sQuery(id+"F0.wireOp",EDGE,"E1046"),sQuery(id+"F0.wireOp",EDGE,"E1047"),sQuery(id+"F0.wireOp",EDGE,"E1048"),sQuery(id+"F0.wireOp",EDGE,"E1049"),sQuery(id+"F0.wireOp",EDGE,"E1050"),sQuery(id+"F0.wireOp",EDGE,"E1051"),sQuery(id+"F0.wireOp",EDGE,"E1052"),sQuery(id+"F0.wireOp",EDGE,"E1053"),sQuery(id+"F0.wireOp",EDGE,"E1054"),sQuery(id+"F0.wireOp",EDGE,"E1055"),sQuery(id+"F0.wireOp",EDGE,"E1056"),sQuery(id+"F0.wireOp",EDGE,"E1057"),sQuery(id+"F0.wireOp",EDGE,"E1058"),sQuery(id+"F0.wireOp",EDGE,"E1059"),sQuery(id+"F0.wireOp",EDGE,"E1060"),sQuery(id+"F0.wireOp",EDGE,"E1061"),sQuery(id+"F0.wireOp",EDGE,"E1062"),sQuery(id+"F0.wireOp",EDGE,"E1063"),sQuery(id+"F0.wireOp",EDGE,"E1064"),sQuery(id+"F0.wireOp",EDGE,"E1065"),sQuery(id+"F0.wireOp",EDGE,"E1066"),sQuery(id+"F0.wireOp",EDGE,"E1067"),sQuery(id+"F0.wireOp",EDGE,"E1068"),sQuery(id+"F0.wireOp",EDGE,"E1069"),sQuery(id+"F0.wireOp",EDGE,"E1070"),sQuery(id+"F0.wireOp",EDGE,"E1071"),sQuery(id+"F0.wireOp",EDGE,"E1072"),sQuery(id+"F0.wireOp",EDGE,"E1073"),sQuery(id+"F0.wireOp",EDGE,"E1074"),sQuery(id+"F0.wireOp",EDGE,"E1075"),sQuery(id+"F0.wireOp",EDGE,"E1076"),sQuery(id+"F0.wireOp",EDGE,"E1077"),sQuery(id+"F0.wireOp",EDGE,"E1078"),sQuery(id+"F0.wireOp",EDGE,"E1079"),sQuery(id+"F0.wireOp",EDGE,"E1080"),sQuery(id+"F0.wireOp",EDGE,"E1081"),sQuery(id+"F0.wireOp",EDGE,"E1082"),sQuery(id+"F0.wireOp",EDGE,"E1083"),sQuery(id+"F0.wireOp",EDGE,"E1084"),sQuery(id+"F0.wireOp",EDGE,"E1085"),sQuery(id+"F0.wireOp",EDGE,"E1086"),sQuery(id+"F0.wireOp",EDGE,"E1087"),sQuery(id+"F0.wireOp",EDGE,"E1088"),sQuery(id+"F0.wireOp",EDGE,"E1089"),sQuery(id+"F0.wireOp",EDGE,"E1090"),sQuery(id+"F0.wireOp",EDGE,"E1091"),sQuery(id+"F0.wireOp",EDGE,"E1092"),sQuery(id+"F0.wireOp",EDGE,"E1093"),sQuery(id+"F0.wireOp",EDGE,"E1094"),sQuery(id+"F0.wireOp",EDGE,"E1095"),sQuery(id+"F0.wireOp",EDGE,"E1096"),sQuery(id+"F0.wireOp",EDGE,"E1097"),sQuery(id+"F0.wireOp",EDGE,"E1098"),sQuery(id+"F0.wireOp",EDGE,"E1099"),sQuery(id+"F0.wireOp",EDGE,"E1100"),sQuery(id+"F0.wireOp",EDGE,"E1101"),sQuery(id+"F0.wireOp",EDGE,"E1102"),sQuery(id+"F0.wireOp",EDGE,"E1103"),sQuery(id+"F0.wireOp",EDGE,"E1104"),sQuery(id+"F0.wireOp",EDGE,"E1105"),sQuery(id+"F0.wireOp",EDGE,"E1106"),sQuery(id+"F0.wireOp",EDGE,"E1107"),sQuery(id+"F0.wireOp",EDGE,"E1108"),sQuery(id+"F0.wireOp",EDGE,"E1109"),sQuery(id+"F0.wireOp",EDGE,"E1110"),sQuery(id+"F0.wireOp",EDGE,"E1111"),sQuery(id+"F0.wireOp",EDGE,"E1112"),sQuery(id+"F0.wireOp",EDGE,"E1113"),sQuery(id+"F0.wireOp",EDGE,"E1114"),sQuery(id+"F0.wireOp",EDGE,"E1115"),sQuery(id+"F0.wireOp",EDGE,"E1116"),sQuery(id+"F0.wireOp",EDGE,"E1117"),sQuery(id+"F0.wireOp",EDGE,"E1118"),sQuery(id+"F0.wireOp",EDGE,"E1119"),sQuery(id+"F0.wireOp",EDGE,"E1120"),sQuery(id+"F0.wireOp",EDGE,"E1121"),sQuery(id+"F0.wireOp",EDGE,"E1122"),sQuery(id+"F0.wireOp",EDGE,"E1123"),sQuery(id+"F0.wireOp",EDGE,"E1124"),sQuery(id+"F0.wireOp",EDGE,"E1125"),sQuery(id+"F0.wireOp",EDGE,"E1126"),sQuery(id+"F0.wireOp",EDGE,"E1127"),sQuery(id+"F0.wireOp",EDGE,"E1128"),sQuery(id+"F0.wireOp",EDGE,"E1129"),sQuery(id+"F0.wireOp",EDGE,"E1130"),sQuery(id+"F0.wireOp",EDGE,"E1131"),sQuery(id+"F0.wireOp",EDGE,"E1132"),sQuery(id+"F0.wireOp",EDGE,"E1133"),sQuery(id+"F0.wireOp",EDGE,"E1134"),sQuery(id+"F0.wireOp",EDGE,"E1135"),sQuery(id+"F0.wireOp",EDGE,"E1136"),sQuery(id+"F0.wireOp",EDGE,"E1137"),sQuery(id+"F0.wireOp",EDGE,"E1138"),sQuery(id+"F0.wireOp",EDGE,"E1139"),sQuery(id+"F0.wireOp",EDGE,"E1140"),sQuery(id+"F0.wireOp",EDGE,"E1141"),sQuery(id+"F0.wireOp",EDGE,"E1142"),sQuery(id+"F0.wireOp",EDGE,"E1143"),sQuery(id+"F0.wireOp",EDGE,"E1144"),sQuery(id+"F0.wireOp",EDGE,"E1145"),sQuery(id+"F0.wireOp",EDGE,"E1146"),sQuery(id+"F0.wireOp",EDGE,"E1147"),sQuery(id+"F0.wireOp",EDGE,"E1148"),sQuery(id+"F0.wireOp",EDGE,"E1149"),sQuery(id+"F0.wireOp",EDGE,"E1150"),sQuery(id+"F0.wireOp",EDGE,"E1151"),sQuery(id+"F0.wireOp",EDGE,"E1152"),sQuery(id+"F0.wireOp",EDGE,"E1153"),sQuery(id+"F0.wireOp",EDGE,"E1154"),sQuery(id+"F0.wireOp",EDGE,"E1155"),sQuery(id+"F0.wireOp",EDGE,"E1156"),sQuery(id+"F0.wireOp",EDGE,"E1157"),sQuery(id+"F0.wireOp",EDGE,"E1158"),sQuery(id+"F0.wireOp",EDGE,"E1159"),sQuery(id+"F0.wireOp",EDGE,"E1160"),sQuery(id+"F0.wireOp",EDGE,"E1161"),sQuery(id+"F0.wireOp",EDGE,"E1162"),sQuery(id+"F0.wireOp",EDGE,"E1163"),sQuery(id+"F0.wireOp",EDGE,"E1164"),sQuery(id+"F0.wireOp",EDGE,"E1165"),sQuery(id+"F0.wireOp",EDGE,"E1166"),sQuery(id+"F0.wireOp",EDGE,"E1167"),sQuery(id+"F0.wireOp",EDGE,"E1168"),sQuery(id+"F0.wireOp",EDGE,"E1169"),sQuery(id+"F0.wireOp",EDGE,"E1170"),sQuery(id+"F0.wireOp",EDGE,"E1171"),sQuery(id+"F0.wireOp",EDGE,"E1172"),sQuery(id+"F0.wireOp",EDGE,"E1173"),sQuery(id+"F0.wireOp",EDGE,"E1174"),sQuery(id+"F0.wireOp",EDGE,"E1175"),sQuery(id+"F0.wireOp",EDGE,"E1176"),sQuery(id+"F0.wireOp",EDGE,"E1177"),sQuery(id+"F0.wireOp",EDGE,"E1178"),sQuery(id+"F0.wireOp",EDGE,"E1179"),sQuery(id+"F0.wireOp",EDGE,"E1180"),sQuery(id+"F0.wireOp",EDGE,"E1181"),sQuery(id+"F0.wireOp",EDGE,"E1182"),sQuery(id+"F0.wireOp",EDGE,"E1183"),sQuery(id+"F0.wireOp",EDGE,"E1184"),sQuery(id+"F0.wireOp",EDGE,"E1185"),sQuery(id+"F0.wireOp",EDGE,"E1186"),sQuery(id+"F0.wireOp",EDGE,"E1187"),sQuery(id+"F0.wireOp",EDGE,"E1188"),sQuery(id+"F0.wireOp",EDGE,"E1189"),sQuery(id+"F0.wireOp",EDGE,"E1190"),sQuery(id+"F0.wireOp",EDGE,"E1191"),sQuery(id+"F0.wireOp",EDGE,"E1192"),sQuery(id+"F0.wireOp",EDGE,"E1193"),sQuery(id+"F0.wireOp",EDGE,"E1194"),sQuery(id+"F0.wireOp",EDGE,"E1195"),sQuery(id+"F0.wireOp",EDGE,"E1196"),sQuery(id+"F0.wireOp",EDGE,"E1197"),sQuery(id+"F0.wireOp",EDGE,"E1198"),sQuery(id+"F0.wireOp",EDGE,"E1199"),sQuery(id+"F0.wireOp",EDGE,"E1200"),sQuery(id+"F0.wireOp",EDGE,"E1201"),sQuery(id+"F0.wireOp",EDGE,"E1202"),sQuery(id+"F0.wireOp",EDGE,"E1203"),sQuery(id+"F0.wireOp",EDGE,"E1204"),sQuery(id+"F0.wireOp",EDGE,"E1205"),sQuery(id+"F0.wireOp",EDGE,"E1206"),sQuery(id+"F0.wireOp",EDGE,"E1207"),sQuery(id+"F0.wireOp",EDGE,"E1208"),sQuery(id+"F0.wireOp",EDGE,"E1209"),sQuery(id+"F0.wireOp",EDGE,"E1210"),sQuery(id+"F0.wireOp",EDGE,"E1211"),sQuery(id+"F0.wireOp",EDGE,"E1212"),sQuery(id+"F0.wireOp",EDGE,"E1213"),sQuery(id+"F0.wireOp",EDGE,"E1214"),sQuery(id+"F0.wireOp",EDGE,"E1215"),sQuery(id+"F0.wireOp",EDGE,"E1216"),sQuery(id+"F0.wireOp",EDGE,"E1217"),sQuery(id+"F0.wireOp",EDGE,"E1218"),sQuery(id+"F0.wireOp",EDGE,"E1219"),sQuery(id+"F0.wireOp",EDGE,"E1220"),sQuery(id+"F0.wireOp",EDGE,"E1221"),sQuery(id+"F0.wireOp",EDGE,"E1222"),sQuery(id+"F0.wireOp",EDGE,"E1224"),sQuery(id+"F0.wireOp",EDGE,"E1225"),sQuery(id+"F0.wireOp",EDGE,"E1226"),sQuery(id+"F0.wireOp",EDGE,"E1228"),sQuery(id+"F0.wireOp",EDGE,"E1229"),sQuery(id+"F0.wireOp",EDGE,"E1230"),sQuery(id+"F0.wireOp",EDGE,"E1232"),sQuery(id+"F0.wireOp",EDGE,"E1233"),sQuery(id+"F0.wireOp",EDGE,"E1234"),sQuery(id+"F0.wireOp",EDGE,"E1236"),sQuery(id+"F0.wireOp",EDGE,"E1237"),sQuery(id+"F0.wireOp",EDGE,"E1238"),sQuery(id+"F0.wireOp",EDGE,"E1240"),sQuery(id+"F0.wireOp",EDGE,"E1241"),sQuery(id+"F0.wireOp",EDGE,"E1242"),sQuery(id+"F0.wireOp",EDGE,"E1244"),sQuery(id+"F0.wireOp",EDGE,"E1245"),sQuery(id+"F0.wireOp",EDGE,"E1246"),sQuery(id+"F0.wireOp",EDGE,"E1248"),sQuery(id+"F0.wireOp",EDGE,"E1249"),sQuery(id+"F0.wireOp",EDGE,"E1250"),sQuery(id+"F0.wireOp",EDGE,"E1252"),sQuery(id+"F0.wireOp",EDGE,"E1253"),sQuery(id+"F0.wireOp",EDGE,"E1254"),sQuery(id+"F0.wireOp",EDGE,"E1256"),sQuery(id+"F0.wireOp",EDGE,"E1257"),sQuery(id+"F0.wireOp",EDGE,"E1258"),sQuery(id+"F0.wireOp",EDGE,"E1260"),sQuery(id+"F0.wireOp",EDGE,"E1261"),sQuery(id+"F0.wireOp",EDGE,"E1262"),sQuery(id+"F0.wireOp",EDGE,"E1264"),sQuery(id+"F0.wireOp",EDGE,"E1265"),sQuery(id+"F0.wireOp",EDGE,"E1266"),sQuery(id+"F0.wireOp",EDGE,"E1268"),sQuery(id+"F0.wireOp",EDGE,"E1269"),sQuery(id+"F0.wireOp",EDGE,"E1270"),sQuery(id+"F0.wireOp",EDGE,"E1272"),sQuery(id+"F0.wireOp",EDGE,"E1273"),sQuery(id+"F0.wireOp",EDGE,"E1274"),sQuery(id+"F0.wireOp",EDGE,"E1276"),sQuery(id+"F0.wireOp",EDGE,"E1277"),sQuery(id+"F0.wireOp",EDGE,"E1278"),sQuery(id+"F0.wireOp",EDGE,"E1280"),sQuery(id+"F0.wireOp",EDGE,"E1281"),sQuery(id+"F0.wireOp",EDGE,"E1282"),sQuery(id+"F0.wireOp",EDGE,"E1284"),sQuery(id+"F0.wireOp",EDGE,"E1285"),sQuery(id+"F0.wireOp",EDGE,"E1286"),sQuery(id+"F0.wireOp",EDGE,"E1288"),sQuery(id+"F0.wireOp",EDGE,"E1289"),sQuery(id+"F0.wireOp",EDGE,"E1290"),sQuery(id+"F0.wireOp",EDGE,"E1292"),sQuery(id+"F0.wireOp",EDGE,"E1293"),sQuery(id+"F0.wireOp",EDGE,"E1294"),sQuery(id+"F0.wireOp",EDGE,"E1296"),sQuery(id+"F0.wireOp",EDGE,"E1297"),sQuery(id+"F0.wireOp",EDGE,"E1298"),sQuery(id+"F0.wireOp",EDGE,"E1300"),sQuery(id+"F0.wireOp",EDGE,"E1301"),sQuery(id+"F0.wireOp",EDGE,"E1302"),sQuery(id+"F0.wireOp",EDGE,"E1304"),sQuery(id+"F0.wireOp",EDGE,"E1305"),sQuery(id+"F0.wireOp",EDGE,"E1306"),sQuery(id+"F0.wireOp",EDGE,"E1308"),sQuery(id+"F0.wireOp",EDGE,"E1309"),sQuery(id+"F0.wireOp",EDGE,"E1310"),sQuery(id+"F0.wireOp",EDGE,"E1312"),sQuery(id+"F0.wireOp",EDGE,"E1313"),sQuery(id+"F0.wireOp",EDGE,"E1314"),sQuery(id+"F0.wireOp",EDGE,"E1316"),sQuery(id+"F0.wireOp",EDGE,"E1317"),sQuery(id+"F0.wireOp",EDGE,"E1318")])],"isStart":true});
            var sketch = newSketch(context, id + "F2", { "sketchPlane" : qUnion([Q0])});
            skLineSegment(sketch, "E2712.bottom", {"start": v(-1175, 286.06) * mm, "end": v(-20, 286.06) * mm});
            skLineSegment(sketch, "E2712.top", {"start": v(-1175, -173.94) * mm, "end": v(-20, -173.94) * mm});
            skLineSegment(sketch, "E2712.left", {"start": v(-1175, 286.06) * mm, "end": v(-1175, -173.94) * mm});
            skLineSegment(sketch, "E2712.right", {"start": v(-20, 286.06) * mm, "end": v(-20, -173.94) * mm});
            skSolve(sketch);
        }
        {
            var Q0;
            Q0=qSketchRegion(id+"F2",true);
            extrude(context, id + "F3", {"entities" : qUnion([Q0]), "operationType" : NewBodyOperationType.REMOVE, "oppositeDirection" : true, "depth" : 6 * mm, "offsetDistance" : 25 * mm});
        }
        {
            var Q0;
            Q0=qCreatedBy(makeId("Front.planeOp"),FACE);
            var sketch = newSketch(context, id + "F4", { "sketchPlane" : qUnion([Q0])});
            skLineSegment(sketch, "E2713.bottom", {"start": v(1175, 286.06) * mm, "end": v(1075, 286.06) * mm});
            skLineSegment(sketch, "E2713.top", {"start": v(1175, 186.06) * mm, "end": v(1075, 186.06) * mm});
            skLineSegment(sketch, "E2713.left", {"start": v(1175, 286.06) * mm, "end": v(1175, 186.06) * mm});
            skLineSegment(sketch, "E2713.right", {"start": v(1075, 286.06) * mm, "end": v(1075, 186.06) * mm});
            skLineSegment(sketch, "E2714", {"start": v(1075, 186.06) * mm, "end": v(1175, 286.06) * mm, "construction": true});
            skLineSegment(sketch, "E2715", {"start": v(1357.58, 56.06) * mm, "end": v(-144.52, 56.06) * mm, "construction": true});
            skLineSegment(sketch, "E2716", {"start": v(607.5, 411.88) * mm, "end": v(607.5, -215.96) * mm, "construction": true});
            skLineSegment(sketch, "E2717.bottom", {"start": v(1175, -173.94) * mm, "end": v(1075, -173.94) * mm});
            skLineSegment(sketch, "E2717.top", {"start": v(1175, -73.94) * mm, "end": v(1075, -73.94) * mm});
            skLineSegment(sketch, "E2717.left", {"start": v(1175, -173.94) * mm, "end": v(1175, -73.94) * mm});
            skLineSegment(sketch, "E2717.right", {"start": v(1075, -173.94) * mm, "end": v(1075, -73.94) * mm});
            skLineSegment(sketch, "E2718.bottom", {"start": v(20, 286.06) * mm, "end": v(120, 286.06) * mm});
            skLineSegment(sketch, "E2718.top", {"start": v(20, 186.06) * mm, "end": v(120, 186.06) * mm});
            skLineSegment(sketch, "E2718.left", {"start": v(20, 286.06) * mm, "end": v(20, 186.06) * mm});
            skLineSegment(sketch, "E2718.right", {"start": v(120, 286.06) * mm, "end": v(120, 186.06) * mm});
            skLineSegment(sketch, "E2719.bottom", {"start": v(20, -173.94) * mm, "end": v(120, -173.94) * mm});
            skLineSegment(sketch, "E2719.top", {"start": v(20, -73.94) * mm, "end": v(120, -73.94) * mm});
            skLineSegment(sketch, "E2719.left", {"start": v(20, -173.94) * mm, "end": v(20, -73.94) * mm});
            skLineSegment(sketch, "E2719.right", {"start": v(120, -173.94) * mm, "end": v(120, -73.94) * mm});
            skLineSegment(sketch, "E2720", {"start": v(120, 186.06) * mm, "end": v(20, 286.06) * mm, "construction": true});
            skLineSegment(sketch, "E2721", {"start": v(20, -173.94) * mm, "end": v(120, -73.94) * mm, "construction": true});
            skLineSegment(sketch, "E2722", {"start": v(1175, -173.94) * mm, "end": v(1075, -73.94) * mm, "construction": true});
            skLineSegment(sketch, "E2723", {"start": v(1095, 206.06) * mm, "end": v(1095, -144.87) * mm, "construction": true});
            skLineSegment(sketch, "E2724", {"start": v(1095, -93.94) * mm, "end": v(84.7, -93.94) * mm, "construction": true});
            skLineSegment(sketch, "E2725", {"start": v(100, -93.94) * mm, "end": v(100, 218.26) * mm, "construction": true});
            skSolve(sketch);
        }
        {
            var Q0;
            Q0=qSketchRegion(id+"F4",true);
            extrude(context, id + "F5", {"entities" : qUnion([Q0]), "operationType" : NewBodyOperationType.ADD, "depth" : 6 * mm, "offsetDistance" : 25 * mm});
        }
        {
            var Q0;
            Q0=makeQuery(id+"F5.opExtrude","SWEPT_EDGE",EDGE,{"disambiguationData":[OSD([sQuery(id+"F4.wireOp",EDGE,"E2718.top"),sQuery(id+"F4.wireOp",EDGE,"E2718.right")])]});
            var Q1;
            Q1=makeQuery(id+"F5.opExtrude","SWEPT_EDGE",EDGE,{"disambiguationData":[OSD([sQuery(id+"F4.wireOp",EDGE,"E2718.top"),sQuery(id+"F4.wireOp",EDGE,"E2718.left")])]});
            var Q2;
            Q2=makeQuery(id+"F5.opExtrude","SWEPT_EDGE",EDGE,{"disambiguationData":[OSD([sQuery(id+"F4.wireOp",EDGE,"E2718.bottom"),sQuery(id+"F4.wireOp",EDGE,"E2718.right")])]});
            var Q3;
            Q3=makeQuery(id+"F5.opExtrude","SWEPT_EDGE",EDGE,{"disambiguationData":[OSD([sQuery(id+"F4.wireOp",EDGE,"E2719.bottom"),sQuery(id+"F4.wireOp",EDGE,"E2719.right")])]});
            var Q4;
            Q4=makeQuery(id+"F5.opExtrude","SWEPT_EDGE",EDGE,{"disambiguationData":[OSD([sQuery(id+"F4.wireOp",EDGE,"E2719.top"),sQuery(id+"F4.wireOp",EDGE,"E2719.right")])]});
            var Q5;
            Q5=makeQuery(id+"F5.opExtrude","SWEPT_EDGE",EDGE,{"disambiguationData":[OSD([sQuery(id+"F4.wireOp",EDGE,"E2719.top"),sQuery(id+"F4.wireOp",EDGE,"E2719.left")])]});
            var Q6;
            Q6=makeQuery(id+"F5.opExtrude","SWEPT_EDGE",EDGE,{"disambiguationData":[OSD([sQuery(id+"F4.wireOp",EDGE,"E2713.right"),sQuery(id+"F4.wireOp",EDGE,"E2713.bottom")])]});
            var Q7;
            Q7=makeQuery(id+"F5.opExtrude","SWEPT_EDGE",EDGE,{"disambiguationData":[OSD([sQuery(id+"F4.wireOp",EDGE,"E2713.top"),sQuery(id+"F4.wireOp",EDGE,"E2713.right")])]});
            var Q8;
            Q8=makeQuery(id+"F5.opExtrude","SWEPT_EDGE",EDGE,{"disambiguationData":[OSD([sQuery(id+"F4.wireOp",EDGE,"E2713.top"),sQuery(id+"F4.wireOp",EDGE,"E2713.left")])]});
            var Q9;
            Q9=makeQuery(id+"F5.opExtrude","SWEPT_EDGE",EDGE,{"disambiguationData":[OSD([sQuery(id+"F4.wireOp",EDGE,"E2717.top"),sQuery(id+"F4.wireOp",EDGE,"E2717.left")])]});
            var Q10;
            Q10=makeQuery(id+"F5.opExtrude","SWEPT_EDGE",EDGE,{"disambiguationData":[OSD([sQuery(id+"F4.wireOp",EDGE,"E2717.top"),sQuery(id+"F4.wireOp",EDGE,"E2717.right")])]});
            var Q11;
            Q11=makeQuery(id+"F5.opExtrude","SWEPT_EDGE",EDGE,{"disambiguationData":[OSD([sQuery(id+"F4.wireOp",EDGE,"E2717.bottom"),sQuery(id+"F4.wireOp",EDGE,"E2717.right")])]});
            fillet(context, id + "F6", {"entities" : qUnion([Q0, Q1, Q2, Q3, Q4, Q5, Q6, Q7, Q8, Q9, Q10, Q11]), "radius" : 5 * mm, "tangentPropagation" : true, "allowEdgeOverflow" : false});
        }
        {
            var Q0;
            Q0=makeQuery(id+"F5.boolean.opBoolean","MERGE",FACE,{"derivedFrom":[makeQuery(id+"F1.opExtrude","CAP_FACE",FACE,{"disambiguationData":[OSD([sQuery(id+"F0.wireOp",EDGE,"E0"),sQuery(id+"F0.wireOp",EDGE,"E1"),sQuery(id+"F0.wireOp",EDGE,"E2"),sQuery(id+"F0.wireOp",EDGE,"E3"),sQuery(id+"F0.wireOp",EDGE,"E4"),sQuery(id+"F0.wireOp",EDGE,"E5"),sQuery(id+"F0.wireOp",EDGE,"E6"),sQuery(id+"F0.wireOp",EDGE,"E7"),sQuery(id+"F0.wireOp",EDGE,"E8"),sQuery(id+"F0.wireOp",EDGE,"E9"),sQuery(id+"F0.wireOp",EDGE,"E10"),sQuery(id+"F0.wireOp",EDGE,"E11"),sQuery(id+"F0.wireOp",EDGE,"E12"),sQuery(id+"F0.wireOp",EDGE,"E13"),sQuery(id+"F0.wireOp",EDGE,"E14"),sQuery(id+"F0.wireOp",EDGE,"E15"),sQuery(id+"F0.wireOp",EDGE,"E16"),sQuery(id+"F0.wireOp",EDGE,"E17"),sQuery(id+"F0.wireOp",EDGE,"E18"),sQuery(id+"F0.wireOp",EDGE,"E19"),sQuery(id+"F0.wireOp",EDGE,"E20"),sQuery(id+"F0.wireOp",EDGE,"E21"),sQuery(id+"F0.wireOp",EDGE,"E22"),sQuery(id+"F0.wireOp",EDGE,"E23"),sQuery(id+"F0.wireOp",EDGE,"E24"),sQuery(id+"F0.wireOp",EDGE,"E25"),sQuery(id+"F0.wireOp",EDGE,"E26"),sQuery(id+"F0.wireOp",EDGE,"E27"),sQuery(id+"F0.wireOp",EDGE,"E28"),sQuery(id+"F0.wireOp",EDGE,"E29"),sQuery(id+"F0.wireOp",EDGE,"E30"),sQuery(id+"F0.wireOp",EDGE,"E31"),sQuery(id+"F0.wireOp",EDGE,"E32"),sQuery(id+"F0.wireOp",EDGE,"E33"),sQuery(id+"F0.wireOp",EDGE,"E34"),sQuery(id+"F0.wireOp",EDGE,"E35"),sQuery(id+"F0.wireOp",EDGE,"E36"),sQuery(id+"F0.wireOp",EDGE,"E37"),sQuery(id+"F0.wireOp",EDGE,"E38"),sQuery(id+"F0.wireOp",EDGE,"E39"),sQuery(id+"F0.wireOp",EDGE,"E40"),sQuery(id+"F0.wireOp",EDGE,"E41"),sQuery(id+"F0.wireOp",EDGE,"E42"),sQuery(id+"F0.wireOp",EDGE,"E43"),sQuery(id+"F0.wireOp",EDGE,"E44"),sQuery(id+"F0.wireOp",EDGE,"E45"),sQuery(id+"F0.wireOp",EDGE,"E46"),sQuery(id+"F0.wireOp",EDGE,"E47"),sQuery(id+"F0.wireOp",EDGE,"E48"),sQuery(id+"F0.wireOp",EDGE,"E49"),sQuery(id+"F0.wireOp",EDGE,"E50"),sQuery(id+"F0.wireOp",EDGE,"E51"),sQuery(id+"F0.wireOp",EDGE,"E52"),sQuery(id+"F0.wireOp",EDGE,"E53"),sQuery(id+"F0.wireOp",EDGE,"E54"),sQuery(id+"F0.wireOp",EDGE,"E55"),sQuery(id+"F0.wireOp",EDGE,"E56"),sQuery(id+"F0.wireOp",EDGE,"E57"),sQuery(id+"F0.wireOp",EDGE,"E58"),sQuery(id+"F0.wireOp",EDGE,"E59"),sQuery(id+"F0.wireOp",EDGE,"E60"),sQuery(id+"F0.wireOp",EDGE,"E61"),sQuery(id+"F0.wireOp",EDGE,"E62"),sQuery(id+"F0.wireOp",EDGE,"E63"),sQuery(id+"F0.wireOp",EDGE,"E64"),sQuery(id+"F0.wireOp",EDGE,"E65"),sQuery(id+"F0.wireOp",EDGE,"E66"),sQuery(id+"F0.wireOp",EDGE,"E67"),sQuery(id+"F0.wireOp",EDGE,"E68"),sQuery(id+"F0.wireOp",EDGE,"E69"),sQuery(id+"F0.wireOp",EDGE,"E70"),sQuery(id+"F0.wireOp",EDGE,"E71"),sQuery(id+"F0.wireOp",EDGE,"E72"),sQuery(id+"F0.wireOp",EDGE,"E73"),sQuery(id+"F0.wireOp",EDGE,"E74"),sQuery(id+"F0.wireOp",EDGE,"E75"),sQuery(id+"F0.wireOp",EDGE,"E76"),sQuery(id+"F0.wireOp",EDGE,"E77"),sQuery(id+"F0.wireOp",EDGE,"E78"),sQuery(id+"F0.wireOp",EDGE,"E79"),sQuery(id+"F0.wireOp",EDGE,"E80"),sQuery(id+"F0.wireOp",EDGE,"E81"),sQuery(id+"F0.wireOp",EDGE,"E82"),sQuery(id+"F0.wireOp",EDGE,"E83"),sQuery(id+"F0.wireOp",EDGE,"E84"),sQuery(id+"F0.wireOp",EDGE,"E85"),sQuery(id+"F0.wireOp",EDGE,"E86"),sQuery(id+"F0.wireOp",EDGE,"E87"),sQuery(id+"F0.wireOp",EDGE,"E88"),sQuery(id+"F0.wireOp",EDGE,"E89"),sQuery(id+"F0.wireOp",EDGE,"E90"),sQuery(id+"F0.wireOp",EDGE,"E91"),sQuery(id+"F0.wireOp",EDGE,"E92"),sQuery(id+"F0.wireOp",EDGE,"E93"),sQuery(id+"F0.wireOp",EDGE,"E94"),sQuery(id+"F0.wireOp",EDGE,"E95"),sQuery(id+"F0.wireOp",EDGE,"E96"),sQuery(id+"F0.wireOp",EDGE,"E97"),sQuery(id+"F0.wireOp",EDGE,"E98"),sQuery(id+"F0.wireOp",EDGE,"E99"),sQuery(id+"F0.wireOp",EDGE,"E100"),sQuery(id+"F0.wireOp",EDGE,"E101"),sQuery(id+"F0.wireOp",EDGE,"E102"),sQuery(id+"F0.wireOp",EDGE,"E103"),sQuery(id+"F0.wireOp",EDGE,"E104"),sQuery(id+"F0.wireOp",EDGE,"E105"),sQuery(id+"F0.wireOp",EDGE,"E106"),sQuery(id+"F0.wireOp",EDGE,"E107"),sQuery(id+"F0.wireOp",EDGE,"E108"),sQuery(id+"F0.wireOp",EDGE,"E109"),sQuery(id+"F0.wireOp",EDGE,"E110"),sQuery(id+"F0.wireOp",EDGE,"E111"),sQuery(id+"F0.wireOp",EDGE,"E112"),sQuery(id+"F0.wireOp",EDGE,"E113"),sQuery(id+"F0.wireOp",EDGE,"E114"),sQuery(id+"F0.wireOp",EDGE,"E115"),sQuery(id+"F0.wireOp",EDGE,"E116"),sQuery(id+"F0.wireOp",EDGE,"E117"),sQuery(id+"F0.wireOp",EDGE,"E118"),sQuery(id+"F0.wireOp",EDGE,"E119"),sQuery(id+"F0.wireOp",EDGE,"E120"),sQuery(id+"F0.wireOp",EDGE,"E121"),sQuery(id+"F0.wireOp",EDGE,"E122"),sQuery(id+"F0.wireOp",EDGE,"E123"),sQuery(id+"F0.wireOp",EDGE,"E124"),sQuery(id+"F0.wireOp",EDGE,"E125"),sQuery(id+"F0.wireOp",EDGE,"E126"),sQuery(id+"F0.wireOp",EDGE,"E127"),sQuery(id+"F0.wireOp",EDGE,"E128"),sQuery(id+"F0.wireOp",EDGE,"E129"),sQuery(id+"F0.wireOp",EDGE,"E130"),sQuery(id+"F0.wireOp",EDGE,"E131"),sQuery(id+"F0.wireOp",EDGE,"E132"),sQuery(id+"F0.wireOp",EDGE,"E133"),sQuery(id+"F0.wireOp",EDGE,"E134"),sQuery(id+"F0.wireOp",EDGE,"E135"),sQuery(id+"F0.wireOp",EDGE,"E136"),sQuery(id+"F0.wireOp",EDGE,"E137"),sQuery(id+"F0.wireOp",EDGE,"E138"),sQuery(id+"F0.wireOp",EDGE,"E139"),sQuery(id+"F0.wireOp",EDGE,"E140"),sQuery(id+"F0.wireOp",EDGE,"E141"),sQuery(id+"F0.wireOp",EDGE,"E142"),sQuery(id+"F0.wireOp",EDGE,"E143"),sQuery(id+"F0.wireOp",EDGE,"E144"),sQuery(id+"F0.wireOp",EDGE,"E145"),sQuery(id+"F0.wireOp",EDGE,"E146"),sQuery(id+"F0.wireOp",EDGE,"E147"),sQuery(id+"F0.wireOp",EDGE,"E148"),sQuery(id+"F0.wireOp",EDGE,"E149"),sQuery(id+"F0.wireOp",EDGE,"E150"),sQuery(id+"F0.wireOp",EDGE,"E151"),sQuery(id+"F0.wireOp",EDGE,"E152"),sQuery(id+"F0.wireOp",EDGE,"E153"),sQuery(id+"F0.wireOp",EDGE,"E154"),sQuery(id+"F0.wireOp",EDGE,"E155"),sQuery(id+"F0.wireOp",EDGE,"E156"),sQuery(id+"F0.wireOp",EDGE,"E157"),sQuery(id+"F0.wireOp",EDGE,"E158"),sQuery(id+"F0.wireOp",EDGE,"E159"),sQuery(id+"F0.wireOp",EDGE,"E160"),sQuery(id+"F0.wireOp",EDGE,"E161"),sQuery(id+"F0.wireOp",EDGE,"E162"),sQuery(id+"F0.wireOp",EDGE,"E163"),sQuery(id+"F0.wireOp",EDGE,"E164"),sQuery(id+"F0.wireOp",EDGE,"E165"),sQuery(id+"F0.wireOp",EDGE,"E166"),sQuery(id+"F0.wireOp",EDGE,"E167"),sQuery(id+"F0.wireOp",EDGE,"E168"),sQuery(id+"F0.wireOp",EDGE,"E169"),sQuery(id+"F0.wireOp",EDGE,"E170"),sQuery(id+"F0.wireOp",EDGE,"E171"),sQuery(id+"F0.wireOp",EDGE,"E172"),sQuery(id+"F0.wireOp",EDGE,"E173"),sQuery(id+"F0.wireOp",EDGE,"E174"),sQuery(id+"F0.wireOp",EDGE,"E175"),sQuery(id+"F0.wireOp",EDGE,"E176"),sQuery(id+"F0.wireOp",EDGE,"E177"),sQuery(id+"F0.wireOp",EDGE,"E178"),sQuery(id+"F0.wireOp",EDGE,"E179"),sQuery(id+"F0.wireOp",EDGE,"E180"),sQuery(id+"F0.wireOp",EDGE,"E181"),sQuery(id+"F0.wireOp",EDGE,"E182"),sQuery(id+"F0.wireOp",EDGE,"E183"),sQuery(id+"F0.wireOp",EDGE,"E184"),sQuery(id+"F0.wireOp",EDGE,"E185"),sQuery(id+"F0.wireOp",EDGE,"E186"),sQuery(id+"F0.wireOp",EDGE,"E187"),sQuery(id+"F0.wireOp",EDGE,"E188"),sQuery(id+"F0.wireOp",EDGE,"E189"),sQuery(id+"F0.wireOp",EDGE,"E190"),sQuery(id+"F0.wireOp",EDGE,"E191"),sQuery(id+"F0.wireOp",EDGE,"E192"),sQuery(id+"F0.wireOp",EDGE,"E193"),sQuery(id+"F0.wireOp",EDGE,"E194"),sQuery(id+"F0.wireOp",EDGE,"E195"),sQuery(id+"F0.wireOp",EDGE,"E196"),sQuery(id+"F0.wireOp",EDGE,"E197"),sQuery(id+"F0.wireOp",EDGE,"E198"),sQuery(id+"F0.wireOp",EDGE,"E199"),sQuery(id+"F0.wireOp",EDGE,"E200"),sQuery(id+"F0.wireOp",EDGE,"E201"),sQuery(id+"F0.wireOp",EDGE,"E202"),sQuery(id+"F0.wireOp",EDGE,"E203"),sQuery(id+"F0.wireOp",EDGE,"E204"),sQuery(id+"F0.wireOp",EDGE,"E205"),sQuery(id+"F0.wireOp",EDGE,"E206"),sQuery(id+"F0.wireOp",EDGE,"E207"),sQuery(id+"F0.wireOp",EDGE,"E208"),sQuery(id+"F0.wireOp",EDGE,"E209"),sQuery(id+"F0.wireOp",EDGE,"E210"),sQuery(id+"F0.wireOp",EDGE,"E211"),sQuery(id+"F0.wireOp",EDGE,"E212"),sQuery(id+"F0.wireOp",EDGE,"E213"),sQuery(id+"F0.wireOp",EDGE,"E214"),sQuery(id+"F0.wireOp",EDGE,"E215"),sQuery(id+"F0.wireOp",EDGE,"E216"),sQuery(id+"F0.wireOp",EDGE,"E217"),sQuery(id+"F0.wireOp",EDGE,"E218"),sQuery(id+"F0.wireOp",EDGE,"E219"),sQuery(id+"F0.wireOp",EDGE,"E220"),sQuery(id+"F0.wireOp",EDGE,"E221"),sQuery(id+"F0.wireOp",EDGE,"E222"),sQuery(id+"F0.wireOp",EDGE,"E223"),sQuery(id+"F0.wireOp",EDGE,"E224"),sQuery(id+"F0.wireOp",EDGE,"E225"),sQuery(id+"F0.wireOp",EDGE,"E226"),sQuery(id+"F0.wireOp",EDGE,"E227"),sQuery(id+"F0.wireOp",EDGE,"E228"),sQuery(id+"F0.wireOp",EDGE,"E229"),sQuery(id+"F0.wireOp",EDGE,"E230"),sQuery(id+"F0.wireOp",EDGE,"E231"),sQuery(id+"F0.wireOp",EDGE,"E232"),sQuery(id+"F0.wireOp",EDGE,"E234"),sQuery(id+"F0.wireOp",EDGE,"E235"),sQuery(id+"F0.wireOp",EDGE,"E236"),sQuery(id+"F0.wireOp",EDGE,"E238"),sQuery(id+"F0.wireOp",EDGE,"E239"),sQuery(id+"F0.wireOp",EDGE,"E240"),sQuery(id+"F0.wireOp",EDGE,"E242"),sQuery(id+"F0.wireOp",EDGE,"E243"),sQuery(id+"F0.wireOp",EDGE,"E244"),sQuery(id+"F0.wireOp",EDGE,"E246"),sQuery(id+"F0.wireOp",EDGE,"E247"),sQuery(id+"F0.wireOp",EDGE,"E248"),sQuery(id+"F0.wireOp",EDGE,"E250"),sQuery(id+"F0.wireOp",EDGE,"E251"),sQuery(id+"F0.wireOp",EDGE,"E252"),sQuery(id+"F0.wireOp",EDGE,"E254"),sQuery(id+"F0.wireOp",EDGE,"E255"),sQuery(id+"F0.wireOp",EDGE,"E256"),sQuery(id+"F0.wireOp",EDGE,"E258"),sQuery(id+"F0.wireOp",EDGE,"E259"),sQuery(id+"F0.wireOp",EDGE,"E260"),sQuery(id+"F0.wireOp",EDGE,"E262"),sQuery(id+"F0.wireOp",EDGE,"E263"),sQuery(id+"F0.wireOp",EDGE,"E264"),sQuery(id+"F0.wireOp",EDGE,"E266"),sQuery(id+"F0.wireOp",EDGE,"E267"),sQuery(id+"F0.wireOp",EDGE,"E268"),sQuery(id+"F0.wireOp",EDGE,"E270"),sQuery(id+"F0.wireOp",EDGE,"E271"),sQuery(id+"F0.wireOp",EDGE,"E272"),sQuery(id+"F0.wireOp",EDGE,"E274"),sQuery(id+"F0.wireOp",EDGE,"E275"),sQuery(id+"F0.wireOp",EDGE,"E276"),sQuery(id+"F0.wireOp",EDGE,"E278"),sQuery(id+"F0.wireOp",EDGE,"E279"),sQuery(id+"F0.wireOp",EDGE,"E280"),sQuery(id+"F0.wireOp",EDGE,"E282"),sQuery(id+"F0.wireOp",EDGE,"E283"),sQuery(id+"F0.wireOp",EDGE,"E284"),sQuery(id+"F0.wireOp",EDGE,"E286"),sQuery(id+"F0.wireOp",EDGE,"E287"),sQuery(id+"F0.wireOp",EDGE,"E288"),sQuery(id+"F0.wireOp",EDGE,"E290"),sQuery(id+"F0.wireOp",EDGE,"E291"),sQuery(id+"F0.wireOp",EDGE,"E292"),sQuery(id+"F0.wireOp",EDGE,"E294"),sQuery(id+"F0.wireOp",EDGE,"E295"),sQuery(id+"F0.wireOp",EDGE,"E296"),sQuery(id+"F0.wireOp",EDGE,"E298"),sQuery(id+"F0.wireOp",EDGE,"E299"),sQuery(id+"F0.wireOp",EDGE,"E300"),sQuery(id+"F0.wireOp",EDGE,"E302"),sQuery(id+"F0.wireOp",EDGE,"E303"),sQuery(id+"F0.wireOp",EDGE,"E304"),sQuery(id+"F0.wireOp",EDGE,"E306"),sQuery(id+"F0.wireOp",EDGE,"E307"),sQuery(id+"F0.wireOp",EDGE,"E308"),sQuery(id+"F0.wireOp",EDGE,"E310"),sQuery(id+"F0.wireOp",EDGE,"E311"),sQuery(id+"F0.wireOp",EDGE,"E312"),sQuery(id+"F0.wireOp",EDGE,"E314"),sQuery(id+"F0.wireOp",EDGE,"E315"),sQuery(id+"F0.wireOp",EDGE,"E316"),sQuery(id+"F0.wireOp",EDGE,"E318"),sQuery(id+"F0.wireOp",EDGE,"E319"),sQuery(id+"F0.wireOp",EDGE,"E320"),sQuery(id+"F0.wireOp",EDGE,"E322"),sQuery(id+"F0.wireOp",EDGE,"E323"),sQuery(id+"F0.wireOp",EDGE,"E324"),sQuery(id+"F0.wireOp",EDGE,"E326"),sQuery(id+"F0.wireOp",EDGE,"E327"),sQuery(id+"F0.wireOp",EDGE,"E328"),sQuery(id+"F0.wireOp",EDGE,"E330"),sQuery(id+"F0.wireOp",EDGE,"E331"),sQuery(id+"F0.wireOp",EDGE,"E332"),sQuery(id+"F0.wireOp",EDGE,"E333"),sQuery(id+"F0.wireOp",EDGE,"E334"),sQuery(id+"F0.wireOp",EDGE,"E335"),sQuery(id+"F0.wireOp",EDGE,"E336"),sQuery(id+"F0.wireOp",EDGE,"E337"),sQuery(id+"F0.wireOp",EDGE,"E338"),sQuery(id+"F0.wireOp",EDGE,"E339"),sQuery(id+"F0.wireOp",EDGE,"E340"),sQuery(id+"F0.wireOp",EDGE,"E341"),sQuery(id+"F0.wireOp",EDGE,"E342"),sQuery(id+"F0.wireOp",EDGE,"E343"),sQuery(id+"F0.wireOp",EDGE,"E344"),sQuery(id+"F0.wireOp",EDGE,"E345"),sQuery(id+"F0.wireOp",EDGE,"E346"),sQuery(id+"F0.wireOp",EDGE,"E347"),sQuery(id+"F0.wireOp",EDGE,"E348"),sQuery(id+"F0.wireOp",EDGE,"E349"),sQuery(id+"F0.wireOp",EDGE,"E350"),sQuery(id+"F0.wireOp",EDGE,"E351"),sQuery(id+"F0.wireOp",EDGE,"E352"),sQuery(id+"F0.wireOp",EDGE,"E353"),sQuery(id+"F0.wireOp",EDGE,"E354"),sQuery(id+"F0.wireOp",EDGE,"E355"),sQuery(id+"F0.wireOp",EDGE,"E356"),sQuery(id+"F0.wireOp",EDGE,"E357"),sQuery(id+"F0.wireOp",EDGE,"E358"),sQuery(id+"F0.wireOp",EDGE,"E359"),sQuery(id+"F0.wireOp",EDGE,"E360"),sQuery(id+"F0.wireOp",EDGE,"E361"),sQuery(id+"F0.wireOp",EDGE,"E362"),sQuery(id+"F0.wireOp",EDGE,"E363"),sQuery(id+"F0.wireOp",EDGE,"E364"),sQuery(id+"F0.wireOp",EDGE,"E365"),sQuery(id+"F0.wireOp",EDGE,"E366"),sQuery(id+"F0.wireOp",EDGE,"E367"),sQuery(id+"F0.wireOp",EDGE,"E368"),sQuery(id+"F0.wireOp",EDGE,"E369"),sQuery(id+"F0.wireOp",EDGE,"E370"),sQuery(id+"F0.wireOp",EDGE,"E371"),sQuery(id+"F0.wireOp",EDGE,"E372"),sQuery(id+"F0.wireOp",EDGE,"E373"),sQuery(id+"F0.wireOp",EDGE,"E374"),sQuery(id+"F0.wireOp",EDGE,"E375"),sQuery(id+"F0.wireOp",EDGE,"E376"),sQuery(id+"F0.wireOp",EDGE,"E377"),sQuery(id+"F0.wireOp",EDGE,"E378"),sQuery(id+"F0.wireOp",EDGE,"E379"),sQuery(id+"F0.wireOp",EDGE,"E380"),sQuery(id+"F0.wireOp",EDGE,"E381"),sQuery(id+"F0.wireOp",EDGE,"E382"),sQuery(id+"F0.wireOp",EDGE,"E383"),sQuery(id+"F0.wireOp",EDGE,"E384"),sQuery(id+"F0.wireOp",EDGE,"E385"),sQuery(id+"F0.wireOp",EDGE,"E386"),sQuery(id+"F0.wireOp",EDGE,"E387"),sQuery(id+"F0.wireOp",EDGE,"E388"),sQuery(id+"F0.wireOp",EDGE,"E389"),sQuery(id+"F0.wireOp",EDGE,"E390"),sQuery(id+"F0.wireOp",EDGE,"E391"),sQuery(id+"F0.wireOp",EDGE,"E392"),sQuery(id+"F0.wireOp",EDGE,"E393"),sQuery(id+"F0.wireOp",EDGE,"E394"),sQuery(id+"F0.wireOp",EDGE,"E395"),sQuery(id+"F0.wireOp",EDGE,"E396"),sQuery(id+"F0.wireOp",EDGE,"E397"),sQuery(id+"F0.wireOp",EDGE,"E398"),sQuery(id+"F0.wireOp",EDGE,"E399"),sQuery(id+"F0.wireOp",EDGE,"E400"),sQuery(id+"F0.wireOp",EDGE,"E401"),sQuery(id+"F0.wireOp",EDGE,"E402"),sQuery(id+"F0.wireOp",EDGE,"E403"),sQuery(id+"F0.wireOp",EDGE,"E404"),sQuery(id+"F0.wireOp",EDGE,"E405"),sQuery(id+"F0.wireOp",EDGE,"E406"),sQuery(id+"F0.wireOp",EDGE,"E407"),sQuery(id+"F0.wireOp",EDGE,"E408"),sQuery(id+"F0.wireOp",EDGE,"E409"),sQuery(id+"F0.wireOp",EDGE,"E410"),sQuery(id+"F0.wireOp",EDGE,"E411"),sQuery(id+"F0.wireOp",EDGE,"E412"),sQuery(id+"F0.wireOp",EDGE,"E413"),sQuery(id+"F0.wireOp",EDGE,"E414"),sQuery(id+"F0.wireOp",EDGE,"E415"),sQuery(id+"F0.wireOp",EDGE,"E416"),sQuery(id+"F0.wireOp",EDGE,"E417"),sQuery(id+"F0.wireOp",EDGE,"E418"),sQuery(id+"F0.wireOp",EDGE,"E419"),sQuery(id+"F0.wireOp",EDGE,"E420"),sQuery(id+"F0.wireOp",EDGE,"E421"),sQuery(id+"F0.wireOp",EDGE,"E422"),sQuery(id+"F0.wireOp",EDGE,"E423"),sQuery(id+"F0.wireOp",EDGE,"E424"),sQuery(id+"F0.wireOp",EDGE,"E425"),sQuery(id+"F0.wireOp",EDGE,"E426"),sQuery(id+"F0.wireOp",EDGE,"E427"),sQuery(id+"F0.wireOp",EDGE,"E428"),sQuery(id+"F0.wireOp",EDGE,"E429"),sQuery(id+"F0.wireOp",EDGE,"E430"),sQuery(id+"F0.wireOp",EDGE,"E431"),sQuery(id+"F0.wireOp",EDGE,"E432"),sQuery(id+"F0.wireOp",EDGE,"E433"),sQuery(id+"F0.wireOp",EDGE,"E434"),sQuery(id+"F0.wireOp",EDGE,"E435"),sQuery(id+"F0.wireOp",EDGE,"E436"),sQuery(id+"F0.wireOp",EDGE,"E437"),sQuery(id+"F0.wireOp",EDGE,"E438"),sQuery(id+"F0.wireOp",EDGE,"E439"),sQuery(id+"F0.wireOp",EDGE,"E440"),sQuery(id+"F0.wireOp",EDGE,"E441"),sQuery(id+"F0.wireOp",EDGE,"E442"),sQuery(id+"F0.wireOp",EDGE,"E443"),sQuery(id+"F0.wireOp",EDGE,"E444"),sQuery(id+"F0.wireOp",EDGE,"E445"),sQuery(id+"F0.wireOp",EDGE,"E446"),sQuery(id+"F0.wireOp",EDGE,"E447"),sQuery(id+"F0.wireOp",EDGE,"E448"),sQuery(id+"F0.wireOp",EDGE,"E449"),sQuery(id+"F0.wireOp",EDGE,"E450"),sQuery(id+"F0.wireOp",EDGE,"E451"),sQuery(id+"F0.wireOp",EDGE,"E452"),sQuery(id+"F0.wireOp",EDGE,"E453"),sQuery(id+"F0.wireOp",EDGE,"E454"),sQuery(id+"F0.wireOp",EDGE,"E455"),sQuery(id+"F0.wireOp",EDGE,"E456"),sQuery(id+"F0.wireOp",EDGE,"E457"),sQuery(id+"F0.wireOp",EDGE,"E458"),sQuery(id+"F0.wireOp",EDGE,"E459"),sQuery(id+"F0.wireOp",EDGE,"E460"),sQuery(id+"F0.wireOp",EDGE,"E461"),sQuery(id+"F0.wireOp",EDGE,"E462"),sQuery(id+"F0.wireOp",EDGE,"E463"),sQuery(id+"F0.wireOp",EDGE,"E464"),sQuery(id+"F0.wireOp",EDGE,"E465"),sQuery(id+"F0.wireOp",EDGE,"E466"),sQuery(id+"F0.wireOp",EDGE,"E467"),sQuery(id+"F0.wireOp",EDGE,"E468"),sQuery(id+"F0.wireOp",EDGE,"E469"),sQuery(id+"F0.wireOp",EDGE,"E470"),sQuery(id+"F0.wireOp",EDGE,"E471"),sQuery(id+"F0.wireOp",EDGE,"E472"),sQuery(id+"F0.wireOp",EDGE,"E473"),sQuery(id+"F0.wireOp",EDGE,"E474"),sQuery(id+"F0.wireOp",EDGE,"E475"),sQuery(id+"F0.wireOp",EDGE,"E476"),sQuery(id+"F0.wireOp",EDGE,"E477"),sQuery(id+"F0.wireOp",EDGE,"E478"),sQuery(id+"F0.wireOp",EDGE,"E479"),sQuery(id+"F0.wireOp",EDGE,"E480"),sQuery(id+"F0.wireOp",EDGE,"E481"),sQuery(id+"F0.wireOp",EDGE,"E482"),sQuery(id+"F0.wireOp",EDGE,"E483"),sQuery(id+"F0.wireOp",EDGE,"E484"),sQuery(id+"F0.wireOp",EDGE,"E485"),sQuery(id+"F0.wireOp",EDGE,"E486"),sQuery(id+"F0.wireOp",EDGE,"E487"),sQuery(id+"F0.wireOp",EDGE,"E488"),sQuery(id+"F0.wireOp",EDGE,"E489"),sQuery(id+"F0.wireOp",EDGE,"E490"),sQuery(id+"F0.wireOp",EDGE,"E491"),sQuery(id+"F0.wireOp",EDGE,"E492"),sQuery(id+"F0.wireOp",EDGE,"E493"),sQuery(id+"F0.wireOp",EDGE,"E494"),sQuery(id+"F0.wireOp",EDGE,"E495"),sQuery(id+"F0.wireOp",EDGE,"E496"),sQuery(id+"F0.wireOp",EDGE,"E497"),sQuery(id+"F0.wireOp",EDGE,"E498"),sQuery(id+"F0.wireOp",EDGE,"E499"),sQuery(id+"F0.wireOp",EDGE,"E500"),sQuery(id+"F0.wireOp",EDGE,"E501"),sQuery(id+"F0.wireOp",EDGE,"E502"),sQuery(id+"F0.wireOp",EDGE,"E503"),sQuery(id+"F0.wireOp",EDGE,"E504"),sQuery(id+"F0.wireOp",EDGE,"E505"),sQuery(id+"F0.wireOp",EDGE,"E506"),sQuery(id+"F0.wireOp",EDGE,"E507"),sQuery(id+"F0.wireOp",EDGE,"E508"),sQuery(id+"F0.wireOp",EDGE,"E509"),sQuery(id+"F0.wireOp",EDGE,"E510"),sQuery(id+"F0.wireOp",EDGE,"E511"),sQuery(id+"F0.wireOp",EDGE,"E512"),sQuery(id+"F0.wireOp",EDGE,"E513"),sQuery(id+"F0.wireOp",EDGE,"E514"),sQuery(id+"F0.wireOp",EDGE,"E515"),sQuery(id+"F0.wireOp",EDGE,"E516"),sQuery(id+"F0.wireOp",EDGE,"E517"),sQuery(id+"F0.wireOp",EDGE,"E518"),sQuery(id+"F0.wireOp",EDGE,"E519"),sQuery(id+"F0.wireOp",EDGE,"E520"),sQuery(id+"F0.wireOp",EDGE,"E521"),sQuery(id+"F0.wireOp",EDGE,"E522"),sQuery(id+"F0.wireOp",EDGE,"E523"),sQuery(id+"F0.wireOp",EDGE,"E524"),sQuery(id+"F0.wireOp",EDGE,"E525"),sQuery(id+"F0.wireOp",EDGE,"E526"),sQuery(id+"F0.wireOp",EDGE,"E527"),sQuery(id+"F0.wireOp",EDGE,"E528"),sQuery(id+"F0.wireOp",EDGE,"E529"),sQuery(id+"F0.wireOp",EDGE,"E530"),sQuery(id+"F0.wireOp",EDGE,"E531"),sQuery(id+"F0.wireOp",EDGE,"E532"),sQuery(id+"F0.wireOp",EDGE,"E533"),sQuery(id+"F0.wireOp",EDGE,"E534"),sQuery(id+"F0.wireOp",EDGE,"E535"),sQuery(id+"F0.wireOp",EDGE,"E536"),sQuery(id+"F0.wireOp",EDGE,"E537"),sQuery(id+"F0.wireOp",EDGE,"E538"),sQuery(id+"F0.wireOp",EDGE,"E539"),sQuery(id+"F0.wireOp",EDGE,"E540"),sQuery(id+"F0.wireOp",EDGE,"E541"),sQuery(id+"F0.wireOp",EDGE,"E542"),sQuery(id+"F0.wireOp",EDGE,"E543"),sQuery(id+"F0.wireOp",EDGE,"E544"),sQuery(id+"F0.wireOp",EDGE,"E545"),sQuery(id+"F0.wireOp",EDGE,"E546"),sQuery(id+"F0.wireOp",EDGE,"E547"),sQuery(id+"F0.wireOp",EDGE,"E548"),sQuery(id+"F0.wireOp",EDGE,"E549"),sQuery(id+"F0.wireOp",EDGE,"E550"),sQuery(id+"F0.wireOp",EDGE,"E551"),sQuery(id+"F0.wireOp",EDGE,"E552"),sQuery(id+"F0.wireOp",EDGE,"E553"),sQuery(id+"F0.wireOp",EDGE,"E554"),sQuery(id+"F0.wireOp",EDGE,"E555"),sQuery(id+"F0.wireOp",EDGE,"E556"),sQuery(id+"F0.wireOp",EDGE,"E557"),sQuery(id+"F0.wireOp",EDGE,"E558"),sQuery(id+"F0.wireOp",EDGE,"E559"),sQuery(id+"F0.wireOp",EDGE,"E560"),sQuery(id+"F0.wireOp",EDGE,"E561"),sQuery(id+"F0.wireOp",EDGE,"E562"),sQuery(id+"F0.wireOp",EDGE,"E563"),sQuery(id+"F0.wireOp",EDGE,"E564"),sQuery(id+"F0.wireOp",EDGE,"E565"),sQuery(id+"F0.wireOp",EDGE,"E566"),sQuery(id+"F0.wireOp",EDGE,"E567"),sQuery(id+"F0.wireOp",EDGE,"E568"),sQuery(id+"F0.wireOp",EDGE,"E569"),sQuery(id+"F0.wireOp",EDGE,"E570"),sQuery(id+"F0.wireOp",EDGE,"E571"),sQuery(id+"F0.wireOp",EDGE,"E572"),sQuery(id+"F0.wireOp",EDGE,"E573"),sQuery(id+"F0.wireOp",EDGE,"E574"),sQuery(id+"F0.wireOp",EDGE,"E575"),sQuery(id+"F0.wireOp",EDGE,"E576"),sQuery(id+"F0.wireOp",EDGE,"E577"),sQuery(id+"F0.wireOp",EDGE,"E578"),sQuery(id+"F0.wireOp",EDGE,"E579"),sQuery(id+"F0.wireOp",EDGE,"E580"),sQuery(id+"F0.wireOp",EDGE,"E581"),sQuery(id+"F0.wireOp",EDGE,"E582"),sQuery(id+"F0.wireOp",EDGE,"E583"),sQuery(id+"F0.wireOp",EDGE,"E584"),sQuery(id+"F0.wireOp",EDGE,"E585"),sQuery(id+"F0.wireOp",EDGE,"E586"),sQuery(id+"F0.wireOp",EDGE,"E587"),sQuery(id+"F0.wireOp",EDGE,"E588"),sQuery(id+"F0.wireOp",EDGE,"E589"),sQuery(id+"F0.wireOp",EDGE,"E590"),sQuery(id+"F0.wireOp",EDGE,"E591"),sQuery(id+"F0.wireOp",EDGE,"E592"),sQuery(id+"F0.wireOp",EDGE,"E593"),sQuery(id+"F0.wireOp",EDGE,"E594"),sQuery(id+"F0.wireOp",EDGE,"E595"),sQuery(id+"F0.wireOp",EDGE,"E596"),sQuery(id+"F0.wireOp",EDGE,"E597"),sQuery(id+"F0.wireOp",EDGE,"E598"),sQuery(id+"F0.wireOp",EDGE,"E599"),sQuery(id+"F0.wireOp",EDGE,"E600"),sQuery(id+"F0.wireOp",EDGE,"E601"),sQuery(id+"F0.wireOp",EDGE,"E602"),sQuery(id+"F0.wireOp",EDGE,"E603"),sQuery(id+"F0.wireOp",EDGE,"E604"),sQuery(id+"F0.wireOp",EDGE,"E605"),sQuery(id+"F0.wireOp",EDGE,"E606"),sQuery(id+"F0.wireOp",EDGE,"E607"),sQuery(id+"F0.wireOp",EDGE,"E608"),sQuery(id+"F0.wireOp",EDGE,"E609"),sQuery(id+"F0.wireOp",EDGE,"E610"),sQuery(id+"F0.wireOp",EDGE,"E611"),sQuery(id+"F0.wireOp",EDGE,"E612"),sQuery(id+"F0.wireOp",EDGE,"E613"),sQuery(id+"F0.wireOp",EDGE,"E614"),sQuery(id+"F0.wireOp",EDGE,"E615"),sQuery(id+"F0.wireOp",EDGE,"E616"),sQuery(id+"F0.wireOp",EDGE,"E617"),sQuery(id+"F0.wireOp",EDGE,"E618"),sQuery(id+"F0.wireOp",EDGE,"E619"),sQuery(id+"F0.wireOp",EDGE,"E620"),sQuery(id+"F0.wireOp",EDGE,"E621"),sQuery(id+"F0.wireOp",EDGE,"E622"),sQuery(id+"F0.wireOp",EDGE,"E623"),sQuery(id+"F0.wireOp",EDGE,"E624"),sQuery(id+"F0.wireOp",EDGE,"E625"),sQuery(id+"F0.wireOp",EDGE,"E626"),sQuery(id+"F0.wireOp",EDGE,"E627"),sQuery(id+"F0.wireOp",EDGE,"E628"),sQuery(id+"F0.wireOp",EDGE,"E629"),sQuery(id+"F0.wireOp",EDGE,"E630"),sQuery(id+"F0.wireOp",EDGE,"E631"),sQuery(id+"F0.wireOp",EDGE,"E632"),sQuery(id+"F0.wireOp",EDGE,"E633"),sQuery(id+"F0.wireOp",EDGE,"E634"),sQuery(id+"F0.wireOp",EDGE,"E635"),sQuery(id+"F0.wireOp",EDGE,"E636"),sQuery(id+"F0.wireOp",EDGE,"E637"),sQuery(id+"F0.wireOp",EDGE,"E638"),sQuery(id+"F0.wireOp",EDGE,"E639"),sQuery(id+"F0.wireOp",EDGE,"E640"),sQuery(id+"F0.wireOp",EDGE,"E641"),sQuery(id+"F0.wireOp",EDGE,"E642"),sQuery(id+"F0.wireOp",EDGE,"E643"),sQuery(id+"F0.wireOp",EDGE,"E644"),sQuery(id+"F0.wireOp",EDGE,"E645"),sQuery(id+"F0.wireOp",EDGE,"E646"),sQuery(id+"F0.wireOp",EDGE,"E647"),sQuery(id+"F0.wireOp",EDGE,"E648"),sQuery(id+"F0.wireOp",EDGE,"E649"),sQuery(id+"F0.wireOp",EDGE,"E650"),sQuery(id+"F0.wireOp",EDGE,"E651"),sQuery(id+"F0.wireOp",EDGE,"E652"),sQuery(id+"F0.wireOp",EDGE,"E653"),sQuery(id+"F0.wireOp",EDGE,"E654"),sQuery(id+"F0.wireOp",EDGE,"E655"),sQuery(id+"F0.wireOp",EDGE,"E656"),sQuery(id+"F0.wireOp",EDGE,"E657"),sQuery(id+"F0.wireOp",EDGE,"E658"),sQuery(id+"F0.wireOp",EDGE,"E659"),sQuery(id+"F0.wireOp",EDGE,"E660"),sQuery(id+"F0.wireOp",EDGE,"E661"),sQuery(id+"F0.wireOp",EDGE,"E662"),sQuery(id+"F0.wireOp",EDGE,"E663"),sQuery(id+"F0.wireOp",EDGE,"E664"),sQuery(id+"F0.wireOp",EDGE,"E665"),sQuery(id+"F0.wireOp",EDGE,"E666"),sQuery(id+"F0.wireOp",EDGE,"E667"),sQuery(id+"F0.wireOp",EDGE,"E668"),sQuery(id+"F0.wireOp",EDGE,"E669"),sQuery(id+"F0.wireOp",EDGE,"E670"),sQuery(id+"F0.wireOp",EDGE,"E671"),sQuery(id+"F0.wireOp",EDGE,"E672"),sQuery(id+"F0.wireOp",EDGE,"E673"),sQuery(id+"F0.wireOp",EDGE,"E674"),sQuery(id+"F0.wireOp",EDGE,"E675"),sQuery(id+"F0.wireOp",EDGE,"E676"),sQuery(id+"F0.wireOp",EDGE,"E677"),sQuery(id+"F0.wireOp",EDGE,"E678"),sQuery(id+"F0.wireOp",EDGE,"E679"),sQuery(id+"F0.wireOp",EDGE,"E680"),sQuery(id+"F0.wireOp",EDGE,"E681"),sQuery(id+"F0.wireOp",EDGE,"E682"),sQuery(id+"F0.wireOp",EDGE,"E683"),sQuery(id+"F0.wireOp",EDGE,"E684"),sQuery(id+"F0.wireOp",EDGE,"E685"),sQuery(id+"F0.wireOp",EDGE,"E686"),sQuery(id+"F0.wireOp",EDGE,"E687"),sQuery(id+"F0.wireOp",EDGE,"E688"),sQuery(id+"F0.wireOp",EDGE,"E689"),sQuery(id+"F0.wireOp",EDGE,"E690"),sQuery(id+"F0.wireOp",EDGE,"E691"),sQuery(id+"F0.wireOp",EDGE,"E692"),sQuery(id+"F0.wireOp",EDGE,"E693"),sQuery(id+"F0.wireOp",EDGE,"E694"),sQuery(id+"F0.wireOp",EDGE,"E695"),sQuery(id+"F0.wireOp",EDGE,"E696"),sQuery(id+"F0.wireOp",EDGE,"E697"),sQuery(id+"F0.wireOp",EDGE,"E698"),sQuery(id+"F0.wireOp",EDGE,"E699"),sQuery(id+"F0.wireOp",EDGE,"E700"),sQuery(id+"F0.wireOp",EDGE,"E701"),sQuery(id+"F0.wireOp",EDGE,"E702"),sQuery(id+"F0.wireOp",EDGE,"E703"),sQuery(id+"F0.wireOp",EDGE,"E704"),sQuery(id+"F0.wireOp",EDGE,"E705"),sQuery(id+"F0.wireOp",EDGE,"E706"),sQuery(id+"F0.wireOp",EDGE,"E707"),sQuery(id+"F0.wireOp",EDGE,"E708"),sQuery(id+"F0.wireOp",EDGE,"E709"),sQuery(id+"F0.wireOp",EDGE,"E710"),sQuery(id+"F0.wireOp",EDGE,"E711"),sQuery(id+"F0.wireOp",EDGE,"E712"),sQuery(id+"F0.wireOp",EDGE,"E713"),sQuery(id+"F0.wireOp",EDGE,"E714"),sQuery(id+"F0.wireOp",EDGE,"E715"),sQuery(id+"F0.wireOp",EDGE,"E716"),sQuery(id+"F0.wireOp",EDGE,"E717"),sQuery(id+"F0.wireOp",EDGE,"E718"),sQuery(id+"F0.wireOp",EDGE,"E719"),sQuery(id+"F0.wireOp",EDGE,"E720"),sQuery(id+"F0.wireOp",EDGE,"E721"),sQuery(id+"F0.wireOp",EDGE,"E722"),sQuery(id+"F0.wireOp",EDGE,"E723"),sQuery(id+"F0.wireOp",EDGE,"E724"),sQuery(id+"F0.wireOp",EDGE,"E725"),sQuery(id+"F0.wireOp",EDGE,"E726"),sQuery(id+"F0.wireOp",EDGE,"E727"),sQuery(id+"F0.wireOp",EDGE,"E728"),sQuery(id+"F0.wireOp",EDGE,"E729"),sQuery(id+"F0.wireOp",EDGE,"E730"),sQuery(id+"F0.wireOp",EDGE,"E731"),sQuery(id+"F0.wireOp",EDGE,"E732"),sQuery(id+"F0.wireOp",EDGE,"E733"),sQuery(id+"F0.wireOp",EDGE,"E734"),sQuery(id+"F0.wireOp",EDGE,"E735"),sQuery(id+"F0.wireOp",EDGE,"E736"),sQuery(id+"F0.wireOp",EDGE,"E737"),sQuery(id+"F0.wireOp",EDGE,"E738"),sQuery(id+"F0.wireOp",EDGE,"E739"),sQuery(id+"F0.wireOp",EDGE,"E740"),sQuery(id+"F0.wireOp",EDGE,"E741"),sQuery(id+"F0.wireOp",EDGE,"E742"),sQuery(id+"F0.wireOp",EDGE,"E743"),sQuery(id+"F0.wireOp",EDGE,"E744"),sQuery(id+"F0.wireOp",EDGE,"E745"),sQuery(id+"F0.wireOp",EDGE,"E746"),sQuery(id+"F0.wireOp",EDGE,"E747"),sQuery(id+"F0.wireOp",EDGE,"E748"),sQuery(id+"F0.wireOp",EDGE,"E749"),sQuery(id+"F0.wireOp",EDGE,"E750"),sQuery(id+"F0.wireOp",EDGE,"E751"),sQuery(id+"F0.wireOp",EDGE,"E752"),sQuery(id+"F0.wireOp",EDGE,"E753"),sQuery(id+"F0.wireOp",EDGE,"E754"),sQuery(id+"F0.wireOp",EDGE,"E755"),sQuery(id+"F0.wireOp",EDGE,"E756"),sQuery(id+"F0.wireOp",EDGE,"E757"),sQuery(id+"F0.wireOp",EDGE,"E758"),sQuery(id+"F0.wireOp",EDGE,"E759"),sQuery(id+"F0.wireOp",EDGE,"E760"),sQuery(id+"F0.wireOp",EDGE,"E761"),sQuery(id+"F0.wireOp",EDGE,"E762"),sQuery(id+"F0.wireOp",EDGE,"E763"),sQuery(id+"F0.wireOp",EDGE,"E764"),sQuery(id+"F0.wireOp",EDGE,"E765"),sQuery(id+"F0.wireOp",EDGE,"E766"),sQuery(id+"F0.wireOp",EDGE,"E767"),sQuery(id+"F0.wireOp",EDGE,"E768"),sQuery(id+"F0.wireOp",EDGE,"E769"),sQuery(id+"F0.wireOp",EDGE,"E770"),sQuery(id+"F0.wireOp",EDGE,"E771"),sQuery(id+"F0.wireOp",EDGE,"E772"),sQuery(id+"F0.wireOp",EDGE,"E773"),sQuery(id+"F0.wireOp",EDGE,"E774"),sQuery(id+"F0.wireOp",EDGE,"E775"),sQuery(id+"F0.wireOp",EDGE,"E776"),sQuery(id+"F0.wireOp",EDGE,"E777"),sQuery(id+"F0.wireOp",EDGE,"E778"),sQuery(id+"F0.wireOp",EDGE,"E779"),sQuery(id+"F0.wireOp",EDGE,"E780"),sQuery(id+"F0.wireOp",EDGE,"E781"),sQuery(id+"F0.wireOp",EDGE,"E782"),sQuery(id+"F0.wireOp",EDGE,"E783"),sQuery(id+"F0.wireOp",EDGE,"E784"),sQuery(id+"F0.wireOp",EDGE,"E785"),sQuery(id+"F0.wireOp",EDGE,"E786"),sQuery(id+"F0.wireOp",EDGE,"E787"),sQuery(id+"F0.wireOp",EDGE,"E788"),sQuery(id+"F0.wireOp",EDGE,"E789"),sQuery(id+"F0.wireOp",EDGE,"E790"),sQuery(id+"F0.wireOp",EDGE,"E791"),sQuery(id+"F0.wireOp",EDGE,"E792"),sQuery(id+"F0.wireOp",EDGE,"E793"),sQuery(id+"F0.wireOp",EDGE,"E794"),sQuery(id+"F0.wireOp",EDGE,"E795"),sQuery(id+"F0.wireOp",EDGE,"E796"),sQuery(id+"F0.wireOp",EDGE,"E797"),sQuery(id+"F0.wireOp",EDGE,"E798"),sQuery(id+"F0.wireOp",EDGE,"E799"),sQuery(id+"F0.wireOp",EDGE,"E800"),sQuery(id+"F0.wireOp",EDGE,"E801"),sQuery(id+"F0.wireOp",EDGE,"E802"),sQuery(id+"F0.wireOp",EDGE,"E803"),sQuery(id+"F0.wireOp",EDGE,"E804"),sQuery(id+"F0.wireOp",EDGE,"E805"),sQuery(id+"F0.wireOp",EDGE,"E806"),sQuery(id+"F0.wireOp",EDGE,"E807"),sQuery(id+"F0.wireOp",EDGE,"E808"),sQuery(id+"F0.wireOp",EDGE,"E809"),sQuery(id+"F0.wireOp",EDGE,"E810"),sQuery(id+"F0.wireOp",EDGE,"E811"),sQuery(id+"F0.wireOp",EDGE,"E812"),sQuery(id+"F0.wireOp",EDGE,"E813"),sQuery(id+"F0.wireOp",EDGE,"E814"),sQuery(id+"F0.wireOp",EDGE,"E815"),sQuery(id+"F0.wireOp",EDGE,"E816"),sQuery(id+"F0.wireOp",EDGE,"E817"),sQuery(id+"F0.wireOp",EDGE,"E818"),sQuery(id+"F0.wireOp",EDGE,"E819"),sQuery(id+"F0.wireOp",EDGE,"E820"),sQuery(id+"F0.wireOp",EDGE,"E821"),sQuery(id+"F0.wireOp",EDGE,"E822"),sQuery(id+"F0.wireOp",EDGE,"E823"),sQuery(id+"F0.wireOp",EDGE,"E824"),sQuery(id+"F0.wireOp",EDGE,"E825"),sQuery(id+"F0.wireOp",EDGE,"E826"),sQuery(id+"F0.wireOp",EDGE,"E827"),sQuery(id+"F0.wireOp",EDGE,"E828"),sQuery(id+"F0.wireOp",EDGE,"E829"),sQuery(id+"F0.wireOp",EDGE,"E830"),sQuery(id+"F0.wireOp",EDGE,"E831"),sQuery(id+"F0.wireOp",EDGE,"E832"),sQuery(id+"F0.wireOp",EDGE,"E833"),sQuery(id+"F0.wireOp",EDGE,"E834"),sQuery(id+"F0.wireOp",EDGE,"E835"),sQuery(id+"F0.wireOp",EDGE,"E836"),sQuery(id+"F0.wireOp",EDGE,"E837"),sQuery(id+"F0.wireOp",EDGE,"E838"),sQuery(id+"F0.wireOp",EDGE,"E839"),sQuery(id+"F0.wireOp",EDGE,"E840"),sQuery(id+"F0.wireOp",EDGE,"E841"),sQuery(id+"F0.wireOp",EDGE,"E842"),sQuery(id+"F0.wireOp",EDGE,"E843"),sQuery(id+"F0.wireOp",EDGE,"E844"),sQuery(id+"F0.wireOp",EDGE,"E845"),sQuery(id+"F0.wireOp",EDGE,"E846"),sQuery(id+"F0.wireOp",EDGE,"E847"),sQuery(id+"F0.wireOp",EDGE,"E848"),sQuery(id+"F0.wireOp",EDGE,"E849"),sQuery(id+"F0.wireOp",EDGE,"E850"),sQuery(id+"F0.wireOp",EDGE,"E851"),sQuery(id+"F0.wireOp",EDGE,"E852"),sQuery(id+"F0.wireOp",EDGE,"E853"),sQuery(id+"F0.wireOp",EDGE,"E854"),sQuery(id+"F0.wireOp",EDGE,"E855"),sQuery(id+"F0.wireOp",EDGE,"E856"),sQuery(id+"F0.wireOp",EDGE,"E857"),sQuery(id+"F0.wireOp",EDGE,"E858"),sQuery(id+"F0.wireOp",EDGE,"E859"),sQuery(id+"F0.wireOp",EDGE,"E860"),sQuery(id+"F0.wireOp",EDGE,"E861"),sQuery(id+"F0.wireOp",EDGE,"E862"),sQuery(id+"F0.wireOp",EDGE,"E863"),sQuery(id+"F0.wireOp",EDGE,"E864"),sQuery(id+"F0.wireOp",EDGE,"E865"),sQuery(id+"F0.wireOp",EDGE,"E866"),sQuery(id+"F0.wireOp",EDGE,"E867"),sQuery(id+"F0.wireOp",EDGE,"E868"),sQuery(id+"F0.wireOp",EDGE,"E869"),sQuery(id+"F0.wireOp",EDGE,"E870"),sQuery(id+"F0.wireOp",EDGE,"E871"),sQuery(id+"F0.wireOp",EDGE,"E872"),sQuery(id+"F0.wireOp",EDGE,"E873"),sQuery(id+"F0.wireOp",EDGE,"E874"),sQuery(id+"F0.wireOp",EDGE,"E875"),sQuery(id+"F0.wireOp",EDGE,"E876"),sQuery(id+"F0.wireOp",EDGE,"E877"),sQuery(id+"F0.wireOp",EDGE,"E878"),sQuery(id+"F0.wireOp",EDGE,"E879"),sQuery(id+"F0.wireOp",EDGE,"E880"),sQuery(id+"F0.wireOp",EDGE,"E881"),sQuery(id+"F0.wireOp",EDGE,"E882"),sQuery(id+"F0.wireOp",EDGE,"E883"),sQuery(id+"F0.wireOp",EDGE,"E884"),sQuery(id+"F0.wireOp",EDGE,"E885"),sQuery(id+"F0.wireOp",EDGE,"E886"),sQuery(id+"F0.wireOp",EDGE,"E887"),sQuery(id+"F0.wireOp",EDGE,"E888"),sQuery(id+"F0.wireOp",EDGE,"E889"),sQuery(id+"F0.wireOp",EDGE,"E890"),sQuery(id+"F0.wireOp",EDGE,"E891"),sQuery(id+"F0.wireOp",EDGE,"E892"),sQuery(id+"F0.wireOp",EDGE,"E893"),sQuery(id+"F0.wireOp",EDGE,"E894"),sQuery(id+"F0.wireOp",EDGE,"E895"),sQuery(id+"F0.wireOp",EDGE,"E896"),sQuery(id+"F0.wireOp",EDGE,"E897"),sQuery(id+"F0.wireOp",EDGE,"E898"),sQuery(id+"F0.wireOp",EDGE,"E899"),sQuery(id+"F0.wireOp",EDGE,"E900"),sQuery(id+"F0.wireOp",EDGE,"E901"),sQuery(id+"F0.wireOp",EDGE,"E902"),sQuery(id+"F0.wireOp",EDGE,"E903"),sQuery(id+"F0.wireOp",EDGE,"E904"),sQuery(id+"F0.wireOp",EDGE,"E905"),sQuery(id+"F0.wireOp",EDGE,"E906"),sQuery(id+"F0.wireOp",EDGE,"E907"),sQuery(id+"F0.wireOp",EDGE,"E908"),sQuery(id+"F0.wireOp",EDGE,"E909"),sQuery(id+"F0.wireOp",EDGE,"E910"),sQuery(id+"F0.wireOp",EDGE,"E911"),sQuery(id+"F0.wireOp",EDGE,"E912"),sQuery(id+"F0.wireOp",EDGE,"E913"),sQuery(id+"F0.wireOp",EDGE,"E914"),sQuery(id+"F0.wireOp",EDGE,"E915"),sQuery(id+"F0.wireOp",EDGE,"E916"),sQuery(id+"F0.wireOp",EDGE,"E917"),sQuery(id+"F0.wireOp",EDGE,"E918"),sQuery(id+"F0.wireOp",EDGE,"E919"),sQuery(id+"F0.wireOp",EDGE,"E920"),sQuery(id+"F0.wireOp",EDGE,"E921"),sQuery(id+"F0.wireOp",EDGE,"E922"),sQuery(id+"F0.wireOp",EDGE,"E923"),sQuery(id+"F0.wireOp",EDGE,"E924"),sQuery(id+"F0.wireOp",EDGE,"E925"),sQuery(id+"F0.wireOp",EDGE,"E926"),sQuery(id+"F0.wireOp",EDGE,"E927"),sQuery(id+"F0.wireOp",EDGE,"E928"),sQuery(id+"F0.wireOp",EDGE,"E929"),sQuery(id+"F0.wireOp",EDGE,"E930"),sQuery(id+"F0.wireOp",EDGE,"E931"),sQuery(id+"F0.wireOp",EDGE,"E932"),sQuery(id+"F0.wireOp",EDGE,"E933"),sQuery(id+"F0.wireOp",EDGE,"E934"),sQuery(id+"F0.wireOp",EDGE,"E935"),sQuery(id+"F0.wireOp",EDGE,"E936"),sQuery(id+"F0.wireOp",EDGE,"E937"),sQuery(id+"F0.wireOp",EDGE,"E938"),sQuery(id+"F0.wireOp",EDGE,"E939"),sQuery(id+"F0.wireOp",EDGE,"E940"),sQuery(id+"F0.wireOp",EDGE,"E941"),sQuery(id+"F0.wireOp",EDGE,"E942"),sQuery(id+"F0.wireOp",EDGE,"E943"),sQuery(id+"F0.wireOp",EDGE,"E944"),sQuery(id+"F0.wireOp",EDGE,"E945"),sQuery(id+"F0.wireOp",EDGE,"E946"),sQuery(id+"F0.wireOp",EDGE,"E947"),sQuery(id+"F0.wireOp",EDGE,"E948"),sQuery(id+"F0.wireOp",EDGE,"E949"),sQuery(id+"F0.wireOp",EDGE,"E950"),sQuery(id+"F0.wireOp",EDGE,"E951"),sQuery(id+"F0.wireOp",EDGE,"E952"),sQuery(id+"F0.wireOp",EDGE,"E953"),sQuery(id+"F0.wireOp",EDGE,"E954"),sQuery(id+"F0.wireOp",EDGE,"E955"),sQuery(id+"F0.wireOp",EDGE,"E956"),sQuery(id+"F0.wireOp",EDGE,"E957"),sQuery(id+"F0.wireOp",EDGE,"E958"),sQuery(id+"F0.wireOp",EDGE,"E959"),sQuery(id+"F0.wireOp",EDGE,"E960"),sQuery(id+"F0.wireOp",EDGE,"E961"),sQuery(id+"F0.wireOp",EDGE,"E962"),sQuery(id+"F0.wireOp",EDGE,"E963"),sQuery(id+"F0.wireOp",EDGE,"E964"),sQuery(id+"F0.wireOp",EDGE,"E965"),sQuery(id+"F0.wireOp",EDGE,"E966"),sQuery(id+"F0.wireOp",EDGE,"E967"),sQuery(id+"F0.wireOp",EDGE,"E968"),sQuery(id+"F0.wireOp",EDGE,"E969"),sQuery(id+"F0.wireOp",EDGE,"E970"),sQuery(id+"F0.wireOp",EDGE,"E971"),sQuery(id+"F0.wireOp",EDGE,"E972"),sQuery(id+"F0.wireOp",EDGE,"E973"),sQuery(id+"F0.wireOp",EDGE,"E974"),sQuery(id+"F0.wireOp",EDGE,"E975"),sQuery(id+"F0.wireOp",EDGE,"E976"),sQuery(id+"F0.wireOp",EDGE,"E977"),sQuery(id+"F0.wireOp",EDGE,"E978"),sQuery(id+"F0.wireOp",EDGE,"E979"),sQuery(id+"F0.wireOp",EDGE,"E980"),sQuery(id+"F0.wireOp",EDGE,"E981"),sQuery(id+"F0.wireOp",EDGE,"E982"),sQuery(id+"F0.wireOp",EDGE,"E983"),sQuery(id+"F0.wireOp",EDGE,"E984"),sQuery(id+"F0.wireOp",EDGE,"E985"),sQuery(id+"F0.wireOp",EDGE,"E986"),sQuery(id+"F0.wireOp",EDGE,"E987"),sQuery(id+"F0.wireOp",EDGE,"E988"),sQuery(id+"F0.wireOp",EDGE,"E989"),sQuery(id+"F0.wireOp",EDGE,"E990"),sQuery(id+"F0.wireOp",EDGE,"E991"),sQuery(id+"F0.wireOp",EDGE,"E992"),sQuery(id+"F0.wireOp",EDGE,"E993"),sQuery(id+"F0.wireOp",EDGE,"E994"),sQuery(id+"F0.wireOp",EDGE,"E995"),sQuery(id+"F0.wireOp",EDGE,"E996"),sQuery(id+"F0.wireOp",EDGE,"E997"),sQuery(id+"F0.wireOp",EDGE,"E998"),sQuery(id+"F0.wireOp",EDGE,"E999"),sQuery(id+"F0.wireOp",EDGE,"E1000"),sQuery(id+"F0.wireOp",EDGE,"E1001"),sQuery(id+"F0.wireOp",EDGE,"E1002"),sQuery(id+"F0.wireOp",EDGE,"E1003"),sQuery(id+"F0.wireOp",EDGE,"E1004"),sQuery(id+"F0.wireOp",EDGE,"E1005"),sQuery(id+"F0.wireOp",EDGE,"E1006"),sQuery(id+"F0.wireOp",EDGE,"E1007"),sQuery(id+"F0.wireOp",EDGE,"E1008"),sQuery(id+"F0.wireOp",EDGE,"E1009"),sQuery(id+"F0.wireOp",EDGE,"E1010"),sQuery(id+"F0.wireOp",EDGE,"E1011"),sQuery(id+"F0.wireOp",EDGE,"E1012"),sQuery(id+"F0.wireOp",EDGE,"E1013"),sQuery(id+"F0.wireOp",EDGE,"E1014"),sQuery(id+"F0.wireOp",EDGE,"E1015"),sQuery(id+"F0.wireOp",EDGE,"E1016"),sQuery(id+"F0.wireOp",EDGE,"E1017"),sQuery(id+"F0.wireOp",EDGE,"E1018"),sQuery(id+"F0.wireOp",EDGE,"E1019"),sQuery(id+"F0.wireOp",EDGE,"E1020"),sQuery(id+"F0.wireOp",EDGE,"E1021"),sQuery(id+"F0.wireOp",EDGE,"E1022"),sQuery(id+"F0.wireOp",EDGE,"E1023"),sQuery(id+"F0.wireOp",EDGE,"E1024"),sQuery(id+"F0.wireOp",EDGE,"E1025"),sQuery(id+"F0.wireOp",EDGE,"E1026"),sQuery(id+"F0.wireOp",EDGE,"E1027"),sQuery(id+"F0.wireOp",EDGE,"E1028"),sQuery(id+"F0.wireOp",EDGE,"E1029"),sQuery(id+"F0.wireOp",EDGE,"E1030"),sQuery(id+"F0.wireOp",EDGE,"E1031"),sQuery(id+"F0.wireOp",EDGE,"E1032"),sQuery(id+"F0.wireOp",EDGE,"E1033"),sQuery(id+"F0.wireOp",EDGE,"E1034"),sQuery(id+"F0.wireOp",EDGE,"E1035"),sQuery(id+"F0.wireOp",EDGE,"E1036"),sQuery(id+"F0.wireOp",EDGE,"E1037"),sQuery(id+"F0.wireOp",EDGE,"E1038"),sQuery(id+"F0.wireOp",EDGE,"E1039"),sQuery(id+"F0.wireOp",EDGE,"E1040"),sQuery(id+"F0.wireOp",EDGE,"E1041"),sQuery(id+"F0.wireOp",EDGE,"E1042"),sQuery(id+"F0.wireOp",EDGE,"E1043"),sQuery(id+"F0.wireOp",EDGE,"E1044"),sQuery(id+"F0.wireOp",EDGE,"E1045"),sQuery(id+"F0.wireOp",EDGE,"E1046"),sQuery(id+"F0.wireOp",EDGE,"E1047"),sQuery(id+"F0.wireOp",EDGE,"E1048"),sQuery(id+"F0.wireOp",EDGE,"E1049"),sQuery(id+"F0.wireOp",EDGE,"E1050"),sQuery(id+"F0.wireOp",EDGE,"E1051"),sQuery(id+"F0.wireOp",EDGE,"E1052"),sQuery(id+"F0.wireOp",EDGE,"E1053"),sQuery(id+"F0.wireOp",EDGE,"E1054"),sQuery(id+"F0.wireOp",EDGE,"E1055"),sQuery(id+"F0.wireOp",EDGE,"E1056"),sQuery(id+"F0.wireOp",EDGE,"E1057"),sQuery(id+"F0.wireOp",EDGE,"E1058"),sQuery(id+"F0.wireOp",EDGE,"E1059"),sQuery(id+"F0.wireOp",EDGE,"E1060"),sQuery(id+"F0.wireOp",EDGE,"E1061"),sQuery(id+"F0.wireOp",EDGE,"E1062"),sQuery(id+"F0.wireOp",EDGE,"E1063"),sQuery(id+"F0.wireOp",EDGE,"E1064"),sQuery(id+"F0.wireOp",EDGE,"E1065"),sQuery(id+"F0.wireOp",EDGE,"E1066"),sQuery(id+"F0.wireOp",EDGE,"E1067"),sQuery(id+"F0.wireOp",EDGE,"E1068"),sQuery(id+"F0.wireOp",EDGE,"E1069"),sQuery(id+"F0.wireOp",EDGE,"E1070"),sQuery(id+"F0.wireOp",EDGE,"E1071"),sQuery(id+"F0.wireOp",EDGE,"E1072"),sQuery(id+"F0.wireOp",EDGE,"E1073"),sQuery(id+"F0.wireOp",EDGE,"E1074"),sQuery(id+"F0.wireOp",EDGE,"E1075"),sQuery(id+"F0.wireOp",EDGE,"E1076"),sQuery(id+"F0.wireOp",EDGE,"E1077"),sQuery(id+"F0.wireOp",EDGE,"E1078"),sQuery(id+"F0.wireOp",EDGE,"E1079"),sQuery(id+"F0.wireOp",EDGE,"E1080"),sQuery(id+"F0.wireOp",EDGE,"E1081"),sQuery(id+"F0.wireOp",EDGE,"E1082"),sQuery(id+"F0.wireOp",EDGE,"E1083"),sQuery(id+"F0.wireOp",EDGE,"E1084"),sQuery(id+"F0.wireOp",EDGE,"E1085"),sQuery(id+"F0.wireOp",EDGE,"E1086"),sQuery(id+"F0.wireOp",EDGE,"E1087"),sQuery(id+"F0.wireOp",EDGE,"E1088"),sQuery(id+"F0.wireOp",EDGE,"E1089"),sQuery(id+"F0.wireOp",EDGE,"E1090"),sQuery(id+"F0.wireOp",EDGE,"E1091"),sQuery(id+"F0.wireOp",EDGE,"E1092"),sQuery(id+"F0.wireOp",EDGE,"E1093"),sQuery(id+"F0.wireOp",EDGE,"E1094"),sQuery(id+"F0.wireOp",EDGE,"E1095"),sQuery(id+"F0.wireOp",EDGE,"E1096"),sQuery(id+"F0.wireOp",EDGE,"E1097"),sQuery(id+"F0.wireOp",EDGE,"E1098"),sQuery(id+"F0.wireOp",EDGE,"E1099"),sQuery(id+"F0.wireOp",EDGE,"E1100"),sQuery(id+"F0.wireOp",EDGE,"E1101"),sQuery(id+"F0.wireOp",EDGE,"E1102"),sQuery(id+"F0.wireOp",EDGE,"E1103"),sQuery(id+"F0.wireOp",EDGE,"E1104"),sQuery(id+"F0.wireOp",EDGE,"E1105"),sQuery(id+"F0.wireOp",EDGE,"E1106"),sQuery(id+"F0.wireOp",EDGE,"E1107"),sQuery(id+"F0.wireOp",EDGE,"E1108"),sQuery(id+"F0.wireOp",EDGE,"E1109"),sQuery(id+"F0.wireOp",EDGE,"E1110"),sQuery(id+"F0.wireOp",EDGE,"E1111"),sQuery(id+"F0.wireOp",EDGE,"E1112"),sQuery(id+"F0.wireOp",EDGE,"E1113"),sQuery(id+"F0.wireOp",EDGE,"E1114"),sQuery(id+"F0.wireOp",EDGE,"E1115"),sQuery(id+"F0.wireOp",EDGE,"E1116"),sQuery(id+"F0.wireOp",EDGE,"E1117"),sQuery(id+"F0.wireOp",EDGE,"E1118"),sQuery(id+"F0.wireOp",EDGE,"E1119"),sQuery(id+"F0.wireOp",EDGE,"E1120"),sQuery(id+"F0.wireOp",EDGE,"E1121"),sQuery(id+"F0.wireOp",EDGE,"E1122"),sQuery(id+"F0.wireOp",EDGE,"E1123"),sQuery(id+"F0.wireOp",EDGE,"E1124"),sQuery(id+"F0.wireOp",EDGE,"E1125"),sQuery(id+"F0.wireOp",EDGE,"E1126"),sQuery(id+"F0.wireOp",EDGE,"E1127"),sQuery(id+"F0.wireOp",EDGE,"E1128"),sQuery(id+"F0.wireOp",EDGE,"E1129"),sQuery(id+"F0.wireOp",EDGE,"E1130"),sQuery(id+"F0.wireOp",EDGE,"E1131"),sQuery(id+"F0.wireOp",EDGE,"E1132"),sQuery(id+"F0.wireOp",EDGE,"E1133"),sQuery(id+"F0.wireOp",EDGE,"E1134"),sQuery(id+"F0.wireOp",EDGE,"E1135"),sQuery(id+"F0.wireOp",EDGE,"E1136"),sQuery(id+"F0.wireOp",EDGE,"E1137"),sQuery(id+"F0.wireOp",EDGE,"E1138"),sQuery(id+"F0.wireOp",EDGE,"E1139"),sQuery(id+"F0.wireOp",EDGE,"E1140"),sQuery(id+"F0.wireOp",EDGE,"E1141"),sQuery(id+"F0.wireOp",EDGE,"E1142"),sQuery(id+"F0.wireOp",EDGE,"E1143"),sQuery(id+"F0.wireOp",EDGE,"E1144"),sQuery(id+"F0.wireOp",EDGE,"E1145"),sQuery(id+"F0.wireOp",EDGE,"E1146"),sQuery(id+"F0.wireOp",EDGE,"E1147"),sQuery(id+"F0.wireOp",EDGE,"E1148"),sQuery(id+"F0.wireOp",EDGE,"E1149"),sQuery(id+"F0.wireOp",EDGE,"E1150"),sQuery(id+"F0.wireOp",EDGE,"E1151"),sQuery(id+"F0.wireOp",EDGE,"E1152"),sQuery(id+"F0.wireOp",EDGE,"E1153"),sQuery(id+"F0.wireOp",EDGE,"E1154"),sQuery(id+"F0.wireOp",EDGE,"E1155"),sQuery(id+"F0.wireOp",EDGE,"E1156"),sQuery(id+"F0.wireOp",EDGE,"E1157"),sQuery(id+"F0.wireOp",EDGE,"E1158"),sQuery(id+"F0.wireOp",EDGE,"E1159"),sQuery(id+"F0.wireOp",EDGE,"E1160"),sQuery(id+"F0.wireOp",EDGE,"E1161"),sQuery(id+"F0.wireOp",EDGE,"E1162"),sQuery(id+"F0.wireOp",EDGE,"E1163"),sQuery(id+"F0.wireOp",EDGE,"E1164"),sQuery(id+"F0.wireOp",EDGE,"E1165"),sQuery(id+"F0.wireOp",EDGE,"E1166"),sQuery(id+"F0.wireOp",EDGE,"E1167"),sQuery(id+"F0.wireOp",EDGE,"E1168"),sQuery(id+"F0.wireOp",EDGE,"E1169"),sQuery(id+"F0.wireOp",EDGE,"E1170"),sQuery(id+"F0.wireOp",EDGE,"E1171"),sQuery(id+"F0.wireOp",EDGE,"E1172"),sQuery(id+"F0.wireOp",EDGE,"E1173"),sQuery(id+"F0.wireOp",EDGE,"E1174"),sQuery(id+"F0.wireOp",EDGE,"E1175"),sQuery(id+"F0.wireOp",EDGE,"E1176"),sQuery(id+"F0.wireOp",EDGE,"E1177"),sQuery(id+"F0.wireOp",EDGE,"E1178"),sQuery(id+"F0.wireOp",EDGE,"E1179"),sQuery(id+"F0.wireOp",EDGE,"E1180"),sQuery(id+"F0.wireOp",EDGE,"E1181"),sQuery(id+"F0.wireOp",EDGE,"E1182"),sQuery(id+"F0.wireOp",EDGE,"E1183"),sQuery(id+"F0.wireOp",EDGE,"E1184"),sQuery(id+"F0.wireOp",EDGE,"E1185"),sQuery(id+"F0.wireOp",EDGE,"E1186"),sQuery(id+"F0.wireOp",EDGE,"E1187"),sQuery(id+"F0.wireOp",EDGE,"E1188"),sQuery(id+"F0.wireOp",EDGE,"E1189"),sQuery(id+"F0.wireOp",EDGE,"E1190"),sQuery(id+"F0.wireOp",EDGE,"E1191"),sQuery(id+"F0.wireOp",EDGE,"E1192"),sQuery(id+"F0.wireOp",EDGE,"E1193"),sQuery(id+"F0.wireOp",EDGE,"E1194"),sQuery(id+"F0.wireOp",EDGE,"E1195"),sQuery(id+"F0.wireOp",EDGE,"E1196"),sQuery(id+"F0.wireOp",EDGE,"E1197"),sQuery(id+"F0.wireOp",EDGE,"E1198"),sQuery(id+"F0.wireOp",EDGE,"E1199"),sQuery(id+"F0.wireOp",EDGE,"E1200"),sQuery(id+"F0.wireOp",EDGE,"E1201"),sQuery(id+"F0.wireOp",EDGE,"E1202"),sQuery(id+"F0.wireOp",EDGE,"E1203"),sQuery(id+"F0.wireOp",EDGE,"E1204"),sQuery(id+"F0.wireOp",EDGE,"E1205"),sQuery(id+"F0.wireOp",EDGE,"E1206"),sQuery(id+"F0.wireOp",EDGE,"E1207"),sQuery(id+"F0.wireOp",EDGE,"E1208"),sQuery(id+"F0.wireOp",EDGE,"E1209"),sQuery(id+"F0.wireOp",EDGE,"E1210"),sQuery(id+"F0.wireOp",EDGE,"E1211"),sQuery(id+"F0.wireOp",EDGE,"E1212"),sQuery(id+"F0.wireOp",EDGE,"E1213"),sQuery(id+"F0.wireOp",EDGE,"E1214"),sQuery(id+"F0.wireOp",EDGE,"E1215"),sQuery(id+"F0.wireOp",EDGE,"E1216"),sQuery(id+"F0.wireOp",EDGE,"E1217"),sQuery(id+"F0.wireOp",EDGE,"E1218"),sQuery(id+"F0.wireOp",EDGE,"E1219"),sQuery(id+"F0.wireOp",EDGE,"E1220"),sQuery(id+"F0.wireOp",EDGE,"E1221"),sQuery(id+"F0.wireOp",EDGE,"E1222"),sQuery(id+"F0.wireOp",EDGE,"E1224"),sQuery(id+"F0.wireOp",EDGE,"E1225"),sQuery(id+"F0.wireOp",EDGE,"E1226"),sQuery(id+"F0.wireOp",EDGE,"E1228"),sQuery(id+"F0.wireOp",EDGE,"E1229"),sQuery(id+"F0.wireOp",EDGE,"E1230"),sQuery(id+"F0.wireOp",EDGE,"E1232"),sQuery(id+"F0.wireOp",EDGE,"E1233"),sQuery(id+"F0.wireOp",EDGE,"E1234"),sQuery(id+"F0.wireOp",EDGE,"E1236"),sQuery(id+"F0.wireOp",EDGE,"E1237"),sQuery(id+"F0.wireOp",EDGE,"E1238"),sQuery(id+"F0.wireOp",EDGE,"E1240"),sQuery(id+"F0.wireOp",EDGE,"E1241"),sQuery(id+"F0.wireOp",EDGE,"E1242"),sQuery(id+"F0.wireOp",EDGE,"E1244"),sQuery(id+"F0.wireOp",EDGE,"E1245"),sQuery(id+"F0.wireOp",EDGE,"E1246"),sQuery(id+"F0.wireOp",EDGE,"E1248"),sQuery(id+"F0.wireOp",EDGE,"E1249"),sQuery(id+"F0.wireOp",EDGE,"E1250"),sQuery(id+"F0.wireOp",EDGE,"E1252"),sQuery(id+"F0.wireOp",EDGE,"E1253"),sQuery(id+"F0.wireOp",EDGE,"E1254"),sQuery(id+"F0.wireOp",EDGE,"E1256"),sQuery(id+"F0.wireOp",EDGE,"E1257"),sQuery(id+"F0.wireOp",EDGE,"E1258"),sQuery(id+"F0.wireOp",EDGE,"E1260"),sQuery(id+"F0.wireOp",EDGE,"E1261"),sQuery(id+"F0.wireOp",EDGE,"E1262"),sQuery(id+"F0.wireOp",EDGE,"E1264"),sQuery(id+"F0.wireOp",EDGE,"E1265"),sQuery(id+"F0.wireOp",EDGE,"E1266"),sQuery(id+"F0.wireOp",EDGE,"E1268"),sQuery(id+"F0.wireOp",EDGE,"E1269"),sQuery(id+"F0.wireOp",EDGE,"E1270"),sQuery(id+"F0.wireOp",EDGE,"E1272"),sQuery(id+"F0.wireOp",EDGE,"E1273"),sQuery(id+"F0.wireOp",EDGE,"E1274"),sQuery(id+"F0.wireOp",EDGE,"E1276"),sQuery(id+"F0.wireOp",EDGE,"E1277"),sQuery(id+"F0.wireOp",EDGE,"E1278"),sQuery(id+"F0.wireOp",EDGE,"E1280"),sQuery(id+"F0.wireOp",EDGE,"E1281"),sQuery(id+"F0.wireOp",EDGE,"E1282"),sQuery(id+"F0.wireOp",EDGE,"E1284"),sQuery(id+"F0.wireOp",EDGE,"E1285"),sQuery(id+"F0.wireOp",EDGE,"E1286"),sQuery(id+"F0.wireOp",EDGE,"E1288"),sQuery(id+"F0.wireOp",EDGE,"E1289"),sQuery(id+"F0.wireOp",EDGE,"E1290"),sQuery(id+"F0.wireOp",EDGE,"E1292"),sQuery(id+"F0.wireOp",EDGE,"E1293"),sQuery(id+"F0.wireOp",EDGE,"E1294"),sQuery(id+"F0.wireOp",EDGE,"E1296"),sQuery(id+"F0.wireOp",EDGE,"E1297"),sQuery(id+"F0.wireOp",EDGE,"E1298"),sQuery(id+"F0.wireOp",EDGE,"E1300"),sQuery(id+"F0.wireOp",EDGE,"E1301"),sQuery(id+"F0.wireOp",EDGE,"E1302"),sQuery(id+"F0.wireOp",EDGE,"E1304"),sQuery(id+"F0.wireOp",EDGE,"E1305"),sQuery(id+"F0.wireOp",EDGE,"E1306"),sQuery(id+"F0.wireOp",EDGE,"E1308"),sQuery(id+"F0.wireOp",EDGE,"E1309"),sQuery(id+"F0.wireOp",EDGE,"E1310"),sQuery(id+"F0.wireOp",EDGE,"E1312"),sQuery(id+"F0.wireOp",EDGE,"E1313"),sQuery(id+"F0.wireOp",EDGE,"E1314"),sQuery(id+"F0.wireOp",EDGE,"E1316"),sQuery(id+"F0.wireOp",EDGE,"E1317"),sQuery(id+"F0.wireOp",EDGE,"E1318")])],"isStart":true}),makeQuery(id+"F5.opExtrude","CAP_FACE",FACE,{"disambiguationData":[OSD([sQuery(id+"F4.wireOp",EDGE,"E2713.top"),sQuery(id+"F4.wireOp",EDGE,"E2713.left"),sQuery(id+"F4.wireOp",EDGE,"E2713.right"),sQuery(id+"F4.wireOp",EDGE,"E2713.bottom")])],"isStart":true}),makeQuery(id+"F5.opExtrude","CAP_FACE",FACE,{"disambiguationData":[OSD([sQuery(id+"F4.wireOp",EDGE,"E2717.bottom"),sQuery(id+"F4.wireOp",EDGE,"E2717.top"),sQuery(id+"F4.wireOp",EDGE,"E2717.left"),sQuery(id+"F4.wireOp",EDGE,"E2717.right")])],"isStart":true}),makeQuery(id+"F5.opExtrude","CAP_FACE",FACE,{"disambiguationData":[OSD([sQuery(id+"F4.wireOp",EDGE,"E2718.bottom"),sQuery(id+"F4.wireOp",EDGE,"E2718.top"),sQuery(id+"F4.wireOp",EDGE,"E2718.left"),sQuery(id+"F4.wireOp",EDGE,"E2718.right")])],"isStart":true}),makeQuery(id+"F5.opExtrude","CAP_FACE",FACE,{"disambiguationData":[OSD([sQuery(id+"F4.wireOp",EDGE,"E2719.bottom"),sQuery(id+"F4.wireOp",EDGE,"E2719.top"),sQuery(id+"F4.wireOp",EDGE,"E2719.left"),sQuery(id+"F4.wireOp",EDGE,"E2719.right")])],"isStart":true})]});
            var sketch = newSketch(context, id + "F7", { "sketchPlane" : qUnion([Q0])});
            skPoint(sketch, "E2726", {"position": v(-1100, 271.06) * mm});
            skPoint(sketch, "E2727", {"position": v(-1160, 271.06) * mm});
            skLineSegment(sketch, "E2728", {"start": v(-1175, 56.06) * mm, "end": v(111.03, 56.06) * mm, "construction": true});
            skLineSegment(sketch, "E2729", {"start": v(-597.5, 422.21) * mm, "end": v(-597.5, -293.1) * mm, "construction": true});
            skPoint(sketch, "E2730.MirrorP", {"position": v(-35, 271.06) * mm});
            skPoint(sketch, "E2731.MirrorP", {"position": v(-95, 271.06) * mm});
            skLineSegment(sketch, "E2732.MirrorCS", {"start": v(-20, 56.06) * mm, "end": v(-1306.03, 56.06) * mm, "construction": true});
            skPoint(sketch, "E2733.MirrorP", {"position": v(-1100, -158.94) * mm});
            skPoint(sketch, "E2734.MirrorP", {"position": v(-1160, -158.94) * mm});
            skPoint(sketch, "E2735.MirrorP", {"position": v(-35, -158.94) * mm});
            skPoint(sketch, "E2736.MirrorP", {"position": v(-95, -158.94) * mm});
            skSolve(sketch);
        }
        {
            var Q0;
            Q0=sQuery(id+"F7.wireOp",VERTEX,"E2733.MirrorP");
            var Q1;
            Q1=sQuery(id+"F7.wireOp",VERTEX,"E2734.MirrorP");
            var Q2;
            Q2=sQuery(id+"F7.wireOp",VERTEX,"E2730.MirrorP");
            var Q3;
            Q3=sQuery(id+"F7.wireOp",VERTEX,"E2731.MirrorP");
            var Q4;
            Q4=sQuery(id+"F7.wireOp",VERTEX,"E2735.MirrorP");
            var Q5;
            Q5=sQuery(id+"F7.wireOp",VERTEX,"E2726");
            var Q6;
            Q6=sQuery(id+"F7.wireOp",VERTEX,"E2736.MirrorP");
            var Q7;
            Q7=sQuery(id+"F7.wireOp",VERTEX,"E2727");
            var Q8;
            Q8=makeQuery(id+"F1.opExtrude","SWEPT_BODY",BODY,{"disambiguationData":[OSD([sQuery(id+"F0.wireOp",EDGE,"E0"),sQuery(id+"F0.wireOp",EDGE,"E1"),sQuery(id+"F0.wireOp",EDGE,"E2"),sQuery(id+"F0.wireOp",EDGE,"E3"),sQuery(id+"F0.wireOp",EDGE,"E4"),sQuery(id+"F0.wireOp",EDGE,"E5"),sQuery(id+"F0.wireOp",EDGE,"E6"),sQuery(id+"F0.wireOp",EDGE,"E7"),sQuery(id+"F0.wireOp",EDGE,"E8"),sQuery(id+"F0.wireOp",EDGE,"E9"),sQuery(id+"F0.wireOp",EDGE,"E10"),sQuery(id+"F0.wireOp",EDGE,"E11"),sQuery(id+"F0.wireOp",EDGE,"E12"),sQuery(id+"F0.wireOp",EDGE,"E13"),sQuery(id+"F0.wireOp",EDGE,"E14"),sQuery(id+"F0.wireOp",EDGE,"E15"),sQuery(id+"F0.wireOp",EDGE,"E16"),sQuery(id+"F0.wireOp",EDGE,"E17"),sQuery(id+"F0.wireOp",EDGE,"E18"),sQuery(id+"F0.wireOp",EDGE,"E19"),sQuery(id+"F0.wireOp",EDGE,"E20"),sQuery(id+"F0.wireOp",EDGE,"E21"),sQuery(id+"F0.wireOp",EDGE,"E22"),sQuery(id+"F0.wireOp",EDGE,"E23"),sQuery(id+"F0.wireOp",EDGE,"E24"),sQuery(id+"F0.wireOp",EDGE,"E25"),sQuery(id+"F0.wireOp",EDGE,"E26"),sQuery(id+"F0.wireOp",EDGE,"E27"),sQuery(id+"F0.wireOp",EDGE,"E28"),sQuery(id+"F0.wireOp",EDGE,"E29"),sQuery(id+"F0.wireOp",EDGE,"E30"),sQuery(id+"F0.wireOp",EDGE,"E31"),sQuery(id+"F0.wireOp",EDGE,"E32"),sQuery(id+"F0.wireOp",EDGE,"E33"),sQuery(id+"F0.wireOp",EDGE,"E34"),sQuery(id+"F0.wireOp",EDGE,"E35"),sQuery(id+"F0.wireOp",EDGE,"E36"),sQuery(id+"F0.wireOp",EDGE,"E37"),sQuery(id+"F0.wireOp",EDGE,"E38"),sQuery(id+"F0.wireOp",EDGE,"E39"),sQuery(id+"F0.wireOp",EDGE,"E40"),sQuery(id+"F0.wireOp",EDGE,"E41"),sQuery(id+"F0.wireOp",EDGE,"E42"),sQuery(id+"F0.wireOp",EDGE,"E43"),sQuery(id+"F0.wireOp",EDGE,"E44"),sQuery(id+"F0.wireOp",EDGE,"E45"),sQuery(id+"F0.wireOp",EDGE,"E46"),sQuery(id+"F0.wireOp",EDGE,"E47"),sQuery(id+"F0.wireOp",EDGE,"E48"),sQuery(id+"F0.wireOp",EDGE,"E49"),sQuery(id+"F0.wireOp",EDGE,"E50"),sQuery(id+"F0.wireOp",EDGE,"E51"),sQuery(id+"F0.wireOp",EDGE,"E52"),sQuery(id+"F0.wireOp",EDGE,"E53"),sQuery(id+"F0.wireOp",EDGE,"E54"),sQuery(id+"F0.wireOp",EDGE,"E55"),sQuery(id+"F0.wireOp",EDGE,"E56"),sQuery(id+"F0.wireOp",EDGE,"E57"),sQuery(id+"F0.wireOp",EDGE,"E58"),sQuery(id+"F0.wireOp",EDGE,"E59"),sQuery(id+"F0.wireOp",EDGE,"E60"),sQuery(id+"F0.wireOp",EDGE,"E61"),sQuery(id+"F0.wireOp",EDGE,"E62"),sQuery(id+"F0.wireOp",EDGE,"E63"),sQuery(id+"F0.wireOp",EDGE,"E64"),sQuery(id+"F0.wireOp",EDGE,"E65"),sQuery(id+"F0.wireOp",EDGE,"E66"),sQuery(id+"F0.wireOp",EDGE,"E67"),sQuery(id+"F0.wireOp",EDGE,"E68"),sQuery(id+"F0.wireOp",EDGE,"E69"),sQuery(id+"F0.wireOp",EDGE,"E70"),sQuery(id+"F0.wireOp",EDGE,"E71"),sQuery(id+"F0.wireOp",EDGE,"E72"),sQuery(id+"F0.wireOp",EDGE,"E73"),sQuery(id+"F0.wireOp",EDGE,"E74"),sQuery(id+"F0.wireOp",EDGE,"E75"),sQuery(id+"F0.wireOp",EDGE,"E76"),sQuery(id+"F0.wireOp",EDGE,"E77"),sQuery(id+"F0.wireOp",EDGE,"E78"),sQuery(id+"F0.wireOp",EDGE,"E79"),sQuery(id+"F0.wireOp",EDGE,"E80"),sQuery(id+"F0.wireOp",EDGE,"E81"),sQuery(id+"F0.wireOp",EDGE,"E82"),sQuery(id+"F0.wireOp",EDGE,"E83"),sQuery(id+"F0.wireOp",EDGE,"E84"),sQuery(id+"F0.wireOp",EDGE,"E85"),sQuery(id+"F0.wireOp",EDGE,"E86"),sQuery(id+"F0.wireOp",EDGE,"E87"),sQuery(id+"F0.wireOp",EDGE,"E88"),sQuery(id+"F0.wireOp",EDGE,"E89"),sQuery(id+"F0.wireOp",EDGE,"E90"),sQuery(id+"F0.wireOp",EDGE,"E91"),sQuery(id+"F0.wireOp",EDGE,"E92"),sQuery(id+"F0.wireOp",EDGE,"E93"),sQuery(id+"F0.wireOp",EDGE,"E94"),sQuery(id+"F0.wireOp",EDGE,"E95"),sQuery(id+"F0.wireOp",EDGE,"E96"),sQuery(id+"F0.wireOp",EDGE,"E97"),sQuery(id+"F0.wireOp",EDGE,"E98"),sQuery(id+"F0.wireOp",EDGE,"E99"),sQuery(id+"F0.wireOp",EDGE,"E100"),sQuery(id+"F0.wireOp",EDGE,"E101"),sQuery(id+"F0.wireOp",EDGE,"E102"),sQuery(id+"F0.wireOp",EDGE,"E103"),sQuery(id+"F0.wireOp",EDGE,"E104"),sQuery(id+"F0.wireOp",EDGE,"E105"),sQuery(id+"F0.wireOp",EDGE,"E106"),sQuery(id+"F0.wireOp",EDGE,"E107"),sQuery(id+"F0.wireOp",EDGE,"E108"),sQuery(id+"F0.wireOp",EDGE,"E109"),sQuery(id+"F0.wireOp",EDGE,"E110"),sQuery(id+"F0.wireOp",EDGE,"E111"),sQuery(id+"F0.wireOp",EDGE,"E112"),sQuery(id+"F0.wireOp",EDGE,"E113"),sQuery(id+"F0.wireOp",EDGE,"E114"),sQuery(id+"F0.wireOp",EDGE,"E115"),sQuery(id+"F0.wireOp",EDGE,"E116"),sQuery(id+"F0.wireOp",EDGE,"E117"),sQuery(id+"F0.wireOp",EDGE,"E118"),sQuery(id+"F0.wireOp",EDGE,"E119"),sQuery(id+"F0.wireOp",EDGE,"E120"),sQuery(id+"F0.wireOp",EDGE,"E121"),sQuery(id+"F0.wireOp",EDGE,"E122"),sQuery(id+"F0.wireOp",EDGE,"E123"),sQuery(id+"F0.wireOp",EDGE,"E124"),sQuery(id+"F0.wireOp",EDGE,"E125"),sQuery(id+"F0.wireOp",EDGE,"E126"),sQuery(id+"F0.wireOp",EDGE,"E127"),sQuery(id+"F0.wireOp",EDGE,"E128"),sQuery(id+"F0.wireOp",EDGE,"E129"),sQuery(id+"F0.wireOp",EDGE,"E130"),sQuery(id+"F0.wireOp",EDGE,"E131"),sQuery(id+"F0.wireOp",EDGE,"E132"),sQuery(id+"F0.wireOp",EDGE,"E133"),sQuery(id+"F0.wireOp",EDGE,"E134"),sQuery(id+"F0.wireOp",EDGE,"E135"),sQuery(id+"F0.wireOp",EDGE,"E136"),sQuery(id+"F0.wireOp",EDGE,"E137"),sQuery(id+"F0.wireOp",EDGE,"E138"),sQuery(id+"F0.wireOp",EDGE,"E139"),sQuery(id+"F0.wireOp",EDGE,"E140"),sQuery(id+"F0.wireOp",EDGE,"E141"),sQuery(id+"F0.wireOp",EDGE,"E142"),sQuery(id+"F0.wireOp",EDGE,"E143"),sQuery(id+"F0.wireOp",EDGE,"E144"),sQuery(id+"F0.wireOp",EDGE,"E145"),sQuery(id+"F0.wireOp",EDGE,"E146"),sQuery(id+"F0.wireOp",EDGE,"E147"),sQuery(id+"F0.wireOp",EDGE,"E148"),sQuery(id+"F0.wireOp",EDGE,"E149"),sQuery(id+"F0.wireOp",EDGE,"E150"),sQuery(id+"F0.wireOp",EDGE,"E151"),sQuery(id+"F0.wireOp",EDGE,"E152"),sQuery(id+"F0.wireOp",EDGE,"E153"),sQuery(id+"F0.wireOp",EDGE,"E154"),sQuery(id+"F0.wireOp",EDGE,"E155"),sQuery(id+"F0.wireOp",EDGE,"E156"),sQuery(id+"F0.wireOp",EDGE,"E157"),sQuery(id+"F0.wireOp",EDGE,"E158"),sQuery(id+"F0.wireOp",EDGE,"E159"),sQuery(id+"F0.wireOp",EDGE,"E160"),sQuery(id+"F0.wireOp",EDGE,"E161"),sQuery(id+"F0.wireOp",EDGE,"E162"),sQuery(id+"F0.wireOp",EDGE,"E163"),sQuery(id+"F0.wireOp",EDGE,"E164"),sQuery(id+"F0.wireOp",EDGE,"E165"),sQuery(id+"F0.wireOp",EDGE,"E166"),sQuery(id+"F0.wireOp",EDGE,"E167"),sQuery(id+"F0.wireOp",EDGE,"E168"),sQuery(id+"F0.wireOp",EDGE,"E169"),sQuery(id+"F0.wireOp",EDGE,"E170"),sQuery(id+"F0.wireOp",EDGE,"E171"),sQuery(id+"F0.wireOp",EDGE,"E172"),sQuery(id+"F0.wireOp",EDGE,"E173"),sQuery(id+"F0.wireOp",EDGE,"E174"),sQuery(id+"F0.wireOp",EDGE,"E175"),sQuery(id+"F0.wireOp",EDGE,"E176"),sQuery(id+"F0.wireOp",EDGE,"E177"),sQuery(id+"F0.wireOp",EDGE,"E178"),sQuery(id+"F0.wireOp",EDGE,"E179"),sQuery(id+"F0.wireOp",EDGE,"E180"),sQuery(id+"F0.wireOp",EDGE,"E181"),sQuery(id+"F0.wireOp",EDGE,"E182"),sQuery(id+"F0.wireOp",EDGE,"E183"),sQuery(id+"F0.wireOp",EDGE,"E184"),sQuery(id+"F0.wireOp",EDGE,"E185"),sQuery(id+"F0.wireOp",EDGE,"E186"),sQuery(id+"F0.wireOp",EDGE,"E187"),sQuery(id+"F0.wireOp",EDGE,"E188"),sQuery(id+"F0.wireOp",EDGE,"E189"),sQuery(id+"F0.wireOp",EDGE,"E190"),sQuery(id+"F0.wireOp",EDGE,"E191"),sQuery(id+"F0.wireOp",EDGE,"E192"),sQuery(id+"F0.wireOp",EDGE,"E193"),sQuery(id+"F0.wireOp",EDGE,"E194"),sQuery(id+"F0.wireOp",EDGE,"E195"),sQuery(id+"F0.wireOp",EDGE,"E196"),sQuery(id+"F0.wireOp",EDGE,"E197"),sQuery(id+"F0.wireOp",EDGE,"E198"),sQuery(id+"F0.wireOp",EDGE,"E199"),sQuery(id+"F0.wireOp",EDGE,"E200"),sQuery(id+"F0.wireOp",EDGE,"E201"),sQuery(id+"F0.wireOp",EDGE,"E202"),sQuery(id+"F0.wireOp",EDGE,"E203"),sQuery(id+"F0.wireOp",EDGE,"E204"),sQuery(id+"F0.wireOp",EDGE,"E205"),sQuery(id+"F0.wireOp",EDGE,"E206"),sQuery(id+"F0.wireOp",EDGE,"E207"),sQuery(id+"F0.wireOp",EDGE,"E208"),sQuery(id+"F0.wireOp",EDGE,"E209"),sQuery(id+"F0.wireOp",EDGE,"E210"),sQuery(id+"F0.wireOp",EDGE,"E211"),sQuery(id+"F0.wireOp",EDGE,"E212"),sQuery(id+"F0.wireOp",EDGE,"E213"),sQuery(id+"F0.wireOp",EDGE,"E214"),sQuery(id+"F0.wireOp",EDGE,"E215"),sQuery(id+"F0.wireOp",EDGE,"E216"),sQuery(id+"F0.wireOp",EDGE,"E217"),sQuery(id+"F0.wireOp",EDGE,"E218"),sQuery(id+"F0.wireOp",EDGE,"E219"),sQuery(id+"F0.wireOp",EDGE,"E220"),sQuery(id+"F0.wireOp",EDGE,"E221"),sQuery(id+"F0.wireOp",EDGE,"E222"),sQuery(id+"F0.wireOp",EDGE,"E223"),sQuery(id+"F0.wireOp",EDGE,"E224"),sQuery(id+"F0.wireOp",EDGE,"E225"),sQuery(id+"F0.wireOp",EDGE,"E226"),sQuery(id+"F0.wireOp",EDGE,"E227"),sQuery(id+"F0.wireOp",EDGE,"E228"),sQuery(id+"F0.wireOp",EDGE,"E229"),sQuery(id+"F0.wireOp",EDGE,"E230"),sQuery(id+"F0.wireOp",EDGE,"E231"),sQuery(id+"F0.wireOp",EDGE,"E232"),sQuery(id+"F0.wireOp",EDGE,"E234"),sQuery(id+"F0.wireOp",EDGE,"E235"),sQuery(id+"F0.wireOp",EDGE,"E236"),sQuery(id+"F0.wireOp",EDGE,"E238"),sQuery(id+"F0.wireOp",EDGE,"E239"),sQuery(id+"F0.wireOp",EDGE,"E240"),sQuery(id+"F0.wireOp",EDGE,"E242"),sQuery(id+"F0.wireOp",EDGE,"E243"),sQuery(id+"F0.wireOp",EDGE,"E244"),sQuery(id+"F0.wireOp",EDGE,"E246"),sQuery(id+"F0.wireOp",EDGE,"E247"),sQuery(id+"F0.wireOp",EDGE,"E248"),sQuery(id+"F0.wireOp",EDGE,"E250"),sQuery(id+"F0.wireOp",EDGE,"E251"),sQuery(id+"F0.wireOp",EDGE,"E252"),sQuery(id+"F0.wireOp",EDGE,"E254"),sQuery(id+"F0.wireOp",EDGE,"E255"),sQuery(id+"F0.wireOp",EDGE,"E256"),sQuery(id+"F0.wireOp",EDGE,"E258"),sQuery(id+"F0.wireOp",EDGE,"E259"),sQuery(id+"F0.wireOp",EDGE,"E260"),sQuery(id+"F0.wireOp",EDGE,"E262"),sQuery(id+"F0.wireOp",EDGE,"E263"),sQuery(id+"F0.wireOp",EDGE,"E264"),sQuery(id+"F0.wireOp",EDGE,"E266"),sQuery(id+"F0.wireOp",EDGE,"E267"),sQuery(id+"F0.wireOp",EDGE,"E268"),sQuery(id+"F0.wireOp",EDGE,"E270"),sQuery(id+"F0.wireOp",EDGE,"E271"),sQuery(id+"F0.wireOp",EDGE,"E272"),sQuery(id+"F0.wireOp",EDGE,"E274"),sQuery(id+"F0.wireOp",EDGE,"E275"),sQuery(id+"F0.wireOp",EDGE,"E276"),sQuery(id+"F0.wireOp",EDGE,"E278"),sQuery(id+"F0.wireOp",EDGE,"E279"),sQuery(id+"F0.wireOp",EDGE,"E280"),sQuery(id+"F0.wireOp",EDGE,"E282"),sQuery(id+"F0.wireOp",EDGE,"E283"),sQuery(id+"F0.wireOp",EDGE,"E284"),sQuery(id+"F0.wireOp",EDGE,"E286"),sQuery(id+"F0.wireOp",EDGE,"E287"),sQuery(id+"F0.wireOp",EDGE,"E288"),sQuery(id+"F0.wireOp",EDGE,"E290"),sQuery(id+"F0.wireOp",EDGE,"E291"),sQuery(id+"F0.wireOp",EDGE,"E292"),sQuery(id+"F0.wireOp",EDGE,"E294"),sQuery(id+"F0.wireOp",EDGE,"E295"),sQuery(id+"F0.wireOp",EDGE,"E296"),sQuery(id+"F0.wireOp",EDGE,"E298"),sQuery(id+"F0.wireOp",EDGE,"E299"),sQuery(id+"F0.wireOp",EDGE,"E300"),sQuery(id+"F0.wireOp",EDGE,"E302"),sQuery(id+"F0.wireOp",EDGE,"E303"),sQuery(id+"F0.wireOp",EDGE,"E304"),sQuery(id+"F0.wireOp",EDGE,"E306"),sQuery(id+"F0.wireOp",EDGE,"E307"),sQuery(id+"F0.wireOp",EDGE,"E308"),sQuery(id+"F0.wireOp",EDGE,"E310"),sQuery(id+"F0.wireOp",EDGE,"E311"),sQuery(id+"F0.wireOp",EDGE,"E312"),sQuery(id+"F0.wireOp",EDGE,"E314"),sQuery(id+"F0.wireOp",EDGE,"E315"),sQuery(id+"F0.wireOp",EDGE,"E316"),sQuery(id+"F0.wireOp",EDGE,"E318"),sQuery(id+"F0.wireOp",EDGE,"E319"),sQuery(id+"F0.wireOp",EDGE,"E320"),sQuery(id+"F0.wireOp",EDGE,"E322"),sQuery(id+"F0.wireOp",EDGE,"E323"),sQuery(id+"F0.wireOp",EDGE,"E324"),sQuery(id+"F0.wireOp",EDGE,"E326"),sQuery(id+"F0.wireOp",EDGE,"E327"),sQuery(id+"F0.wireOp",EDGE,"E328"),sQuery(id+"F0.wireOp",EDGE,"E330"),sQuery(id+"F0.wireOp",EDGE,"E331"),sQuery(id+"F0.wireOp",EDGE,"E332"),sQuery(id+"F0.wireOp",EDGE,"E333"),sQuery(id+"F0.wireOp",EDGE,"E334"),sQuery(id+"F0.wireOp",EDGE,"E335"),sQuery(id+"F0.wireOp",EDGE,"E336"),sQuery(id+"F0.wireOp",EDGE,"E337"),sQuery(id+"F0.wireOp",EDGE,"E338"),sQuery(id+"F0.wireOp",EDGE,"E339"),sQuery(id+"F0.wireOp",EDGE,"E340"),sQuery(id+"F0.wireOp",EDGE,"E341"),sQuery(id+"F0.wireOp",EDGE,"E342"),sQuery(id+"F0.wireOp",EDGE,"E343"),sQuery(id+"F0.wireOp",EDGE,"E344"),sQuery(id+"F0.wireOp",EDGE,"E345"),sQuery(id+"F0.wireOp",EDGE,"E346"),sQuery(id+"F0.wireOp",EDGE,"E347"),sQuery(id+"F0.wireOp",EDGE,"E348"),sQuery(id+"F0.wireOp",EDGE,"E349"),sQuery(id+"F0.wireOp",EDGE,"E350"),sQuery(id+"F0.wireOp",EDGE,"E351"),sQuery(id+"F0.wireOp",EDGE,"E352"),sQuery(id+"F0.wireOp",EDGE,"E353"),sQuery(id+"F0.wireOp",EDGE,"E354"),sQuery(id+"F0.wireOp",EDGE,"E355"),sQuery(id+"F0.wireOp",EDGE,"E356"),sQuery(id+"F0.wireOp",EDGE,"E357"),sQuery(id+"F0.wireOp",EDGE,"E358"),sQuery(id+"F0.wireOp",EDGE,"E359"),sQuery(id+"F0.wireOp",EDGE,"E360"),sQuery(id+"F0.wireOp",EDGE,"E361"),sQuery(id+"F0.wireOp",EDGE,"E362"),sQuery(id+"F0.wireOp",EDGE,"E363"),sQuery(id+"F0.wireOp",EDGE,"E364"),sQuery(id+"F0.wireOp",EDGE,"E365"),sQuery(id+"F0.wireOp",EDGE,"E366"),sQuery(id+"F0.wireOp",EDGE,"E367"),sQuery(id+"F0.wireOp",EDGE,"E368"),sQuery(id+"F0.wireOp",EDGE,"E369"),sQuery(id+"F0.wireOp",EDGE,"E370"),sQuery(id+"F0.wireOp",EDGE,"E371"),sQuery(id+"F0.wireOp",EDGE,"E372"),sQuery(id+"F0.wireOp",EDGE,"E373"),sQuery(id+"F0.wireOp",EDGE,"E374"),sQuery(id+"F0.wireOp",EDGE,"E375"),sQuery(id+"F0.wireOp",EDGE,"E376"),sQuery(id+"F0.wireOp",EDGE,"E377"),sQuery(id+"F0.wireOp",EDGE,"E378"),sQuery(id+"F0.wireOp",EDGE,"E379"),sQuery(id+"F0.wireOp",EDGE,"E380"),sQuery(id+"F0.wireOp",EDGE,"E381"),sQuery(id+"F0.wireOp",EDGE,"E382"),sQuery(id+"F0.wireOp",EDGE,"E383"),sQuery(id+"F0.wireOp",EDGE,"E384"),sQuery(id+"F0.wireOp",EDGE,"E385"),sQuery(id+"F0.wireOp",EDGE,"E386"),sQuery(id+"F0.wireOp",EDGE,"E387"),sQuery(id+"F0.wireOp",EDGE,"E388"),sQuery(id+"F0.wireOp",EDGE,"E389"),sQuery(id+"F0.wireOp",EDGE,"E390"),sQuery(id+"F0.wireOp",EDGE,"E391"),sQuery(id+"F0.wireOp",EDGE,"E392"),sQuery(id+"F0.wireOp",EDGE,"E393"),sQuery(id+"F0.wireOp",EDGE,"E394"),sQuery(id+"F0.wireOp",EDGE,"E395"),sQuery(id+"F0.wireOp",EDGE,"E396"),sQuery(id+"F0.wireOp",EDGE,"E397"),sQuery(id+"F0.wireOp",EDGE,"E398"),sQuery(id+"F0.wireOp",EDGE,"E399"),sQuery(id+"F0.wireOp",EDGE,"E400"),sQuery(id+"F0.wireOp",EDGE,"E401"),sQuery(id+"F0.wireOp",EDGE,"E402"),sQuery(id+"F0.wireOp",EDGE,"E403"),sQuery(id+"F0.wireOp",EDGE,"E404"),sQuery(id+"F0.wireOp",EDGE,"E405"),sQuery(id+"F0.wireOp",EDGE,"E406"),sQuery(id+"F0.wireOp",EDGE,"E407"),sQuery(id+"F0.wireOp",EDGE,"E408"),sQuery(id+"F0.wireOp",EDGE,"E409"),sQuery(id+"F0.wireOp",EDGE,"E410"),sQuery(id+"F0.wireOp",EDGE,"E411"),sQuery(id+"F0.wireOp",EDGE,"E412"),sQuery(id+"F0.wireOp",EDGE,"E413"),sQuery(id+"F0.wireOp",EDGE,"E414"),sQuery(id+"F0.wireOp",EDGE,"E415"),sQuery(id+"F0.wireOp",EDGE,"E416"),sQuery(id+"F0.wireOp",EDGE,"E417"),sQuery(id+"F0.wireOp",EDGE,"E418"),sQuery(id+"F0.wireOp",EDGE,"E419"),sQuery(id+"F0.wireOp",EDGE,"E420"),sQuery(id+"F0.wireOp",EDGE,"E421"),sQuery(id+"F0.wireOp",EDGE,"E422"),sQuery(id+"F0.wireOp",EDGE,"E423"),sQuery(id+"F0.wireOp",EDGE,"E424"),sQuery(id+"F0.wireOp",EDGE,"E425"),sQuery(id+"F0.wireOp",EDGE,"E426"),sQuery(id+"F0.wireOp",EDGE,"E427"),sQuery(id+"F0.wireOp",EDGE,"E428"),sQuery(id+"F0.wireOp",EDGE,"E429"),sQuery(id+"F0.wireOp",EDGE,"E430"),sQuery(id+"F0.wireOp",EDGE,"E431"),sQuery(id+"F0.wireOp",EDGE,"E432"),sQuery(id+"F0.wireOp",EDGE,"E433"),sQuery(id+"F0.wireOp",EDGE,"E434"),sQuery(id+"F0.wireOp",EDGE,"E435"),sQuery(id+"F0.wireOp",EDGE,"E436"),sQuery(id+"F0.wireOp",EDGE,"E437"),sQuery(id+"F0.wireOp",EDGE,"E438"),sQuery(id+"F0.wireOp",EDGE,"E439"),sQuery(id+"F0.wireOp",EDGE,"E440"),sQuery(id+"F0.wireOp",EDGE,"E441"),sQuery(id+"F0.wireOp",EDGE,"E442"),sQuery(id+"F0.wireOp",EDGE,"E443"),sQuery(id+"F0.wireOp",EDGE,"E444"),sQuery(id+"F0.wireOp",EDGE,"E445"),sQuery(id+"F0.wireOp",EDGE,"E446"),sQuery(id+"F0.wireOp",EDGE,"E447"),sQuery(id+"F0.wireOp",EDGE,"E448"),sQuery(id+"F0.wireOp",EDGE,"E449"),sQuery(id+"F0.wireOp",EDGE,"E450"),sQuery(id+"F0.wireOp",EDGE,"E451"),sQuery(id+"F0.wireOp",EDGE,"E452"),sQuery(id+"F0.wireOp",EDGE,"E453"),sQuery(id+"F0.wireOp",EDGE,"E454"),sQuery(id+"F0.wireOp",EDGE,"E455"),sQuery(id+"F0.wireOp",EDGE,"E456"),sQuery(id+"F0.wireOp",EDGE,"E457"),sQuery(id+"F0.wireOp",EDGE,"E458"),sQuery(id+"F0.wireOp",EDGE,"E459"),sQuery(id+"F0.wireOp",EDGE,"E460"),sQuery(id+"F0.wireOp",EDGE,"E461"),sQuery(id+"F0.wireOp",EDGE,"E462"),sQuery(id+"F0.wireOp",EDGE,"E463"),sQuery(id+"F0.wireOp",EDGE,"E464"),sQuery(id+"F0.wireOp",EDGE,"E465"),sQuery(id+"F0.wireOp",EDGE,"E466"),sQuery(id+"F0.wireOp",EDGE,"E467"),sQuery(id+"F0.wireOp",EDGE,"E468"),sQuery(id+"F0.wireOp",EDGE,"E469"),sQuery(id+"F0.wireOp",EDGE,"E470"),sQuery(id+"F0.wireOp",EDGE,"E471"),sQuery(id+"F0.wireOp",EDGE,"E472"),sQuery(id+"F0.wireOp",EDGE,"E473"),sQuery(id+"F0.wireOp",EDGE,"E474"),sQuery(id+"F0.wireOp",EDGE,"E475"),sQuery(id+"F0.wireOp",EDGE,"E476"),sQuery(id+"F0.wireOp",EDGE,"E477"),sQuery(id+"F0.wireOp",EDGE,"E478"),sQuery(id+"F0.wireOp",EDGE,"E479"),sQuery(id+"F0.wireOp",EDGE,"E480"),sQuery(id+"F0.wireOp",EDGE,"E481"),sQuery(id+"F0.wireOp",EDGE,"E482"),sQuery(id+"F0.wireOp",EDGE,"E483"),sQuery(id+"F0.wireOp",EDGE,"E484"),sQuery(id+"F0.wireOp",EDGE,"E485"),sQuery(id+"F0.wireOp",EDGE,"E486"),sQuery(id+"F0.wireOp",EDGE,"E487"),sQuery(id+"F0.wireOp",EDGE,"E488"),sQuery(id+"F0.wireOp",EDGE,"E489"),sQuery(id+"F0.wireOp",EDGE,"E490"),sQuery(id+"F0.wireOp",EDGE,"E491"),sQuery(id+"F0.wireOp",EDGE,"E492"),sQuery(id+"F0.wireOp",EDGE,"E493"),sQuery(id+"F0.wireOp",EDGE,"E494"),sQuery(id+"F0.wireOp",EDGE,"E495"),sQuery(id+"F0.wireOp",EDGE,"E496"),sQuery(id+"F0.wireOp",EDGE,"E497"),sQuery(id+"F0.wireOp",EDGE,"E498"),sQuery(id+"F0.wireOp",EDGE,"E499"),sQuery(id+"F0.wireOp",EDGE,"E500"),sQuery(id+"F0.wireOp",EDGE,"E501"),sQuery(id+"F0.wireOp",EDGE,"E502"),sQuery(id+"F0.wireOp",EDGE,"E503"),sQuery(id+"F0.wireOp",EDGE,"E504"),sQuery(id+"F0.wireOp",EDGE,"E505"),sQuery(id+"F0.wireOp",EDGE,"E506"),sQuery(id+"F0.wireOp",EDGE,"E507"),sQuery(id+"F0.wireOp",EDGE,"E508"),sQuery(id+"F0.wireOp",EDGE,"E509"),sQuery(id+"F0.wireOp",EDGE,"E510"),sQuery(id+"F0.wireOp",EDGE,"E511"),sQuery(id+"F0.wireOp",EDGE,"E512"),sQuery(id+"F0.wireOp",EDGE,"E513"),sQuery(id+"F0.wireOp",EDGE,"E514"),sQuery(id+"F0.wireOp",EDGE,"E515"),sQuery(id+"F0.wireOp",EDGE,"E516"),sQuery(id+"F0.wireOp",EDGE,"E517"),sQuery(id+"F0.wireOp",EDGE,"E518"),sQuery(id+"F0.wireOp",EDGE,"E519"),sQuery(id+"F0.wireOp",EDGE,"E520"),sQuery(id+"F0.wireOp",EDGE,"E521"),sQuery(id+"F0.wireOp",EDGE,"E522"),sQuery(id+"F0.wireOp",EDGE,"E523"),sQuery(id+"F0.wireOp",EDGE,"E524"),sQuery(id+"F0.wireOp",EDGE,"E525"),sQuery(id+"F0.wireOp",EDGE,"E526"),sQuery(id+"F0.wireOp",EDGE,"E527"),sQuery(id+"F0.wireOp",EDGE,"E528"),sQuery(id+"F0.wireOp",EDGE,"E529"),sQuery(id+"F0.wireOp",EDGE,"E530"),sQuery(id+"F0.wireOp",EDGE,"E531"),sQuery(id+"F0.wireOp",EDGE,"E532"),sQuery(id+"F0.wireOp",EDGE,"E533"),sQuery(id+"F0.wireOp",EDGE,"E534"),sQuery(id+"F0.wireOp",EDGE,"E535"),sQuery(id+"F0.wireOp",EDGE,"E536"),sQuery(id+"F0.wireOp",EDGE,"E537"),sQuery(id+"F0.wireOp",EDGE,"E538"),sQuery(id+"F0.wireOp",EDGE,"E539"),sQuery(id+"F0.wireOp",EDGE,"E540"),sQuery(id+"F0.wireOp",EDGE,"E541"),sQuery(id+"F0.wireOp",EDGE,"E542"),sQuery(id+"F0.wireOp",EDGE,"E543"),sQuery(id+"F0.wireOp",EDGE,"E544"),sQuery(id+"F0.wireOp",EDGE,"E545"),sQuery(id+"F0.wireOp",EDGE,"E546"),sQuery(id+"F0.wireOp",EDGE,"E547"),sQuery(id+"F0.wireOp",EDGE,"E548"),sQuery(id+"F0.wireOp",EDGE,"E549"),sQuery(id+"F0.wireOp",EDGE,"E550"),sQuery(id+"F0.wireOp",EDGE,"E551"),sQuery(id+"F0.wireOp",EDGE,"E552"),sQuery(id+"F0.wireOp",EDGE,"E553"),sQuery(id+"F0.wireOp",EDGE,"E554"),sQuery(id+"F0.wireOp",EDGE,"E555"),sQuery(id+"F0.wireOp",EDGE,"E556"),sQuery(id+"F0.wireOp",EDGE,"E557"),sQuery(id+"F0.wireOp",EDGE,"E558"),sQuery(id+"F0.wireOp",EDGE,"E559"),sQuery(id+"F0.wireOp",EDGE,"E560"),sQuery(id+"F0.wireOp",EDGE,"E561"),sQuery(id+"F0.wireOp",EDGE,"E562"),sQuery(id+"F0.wireOp",EDGE,"E563"),sQuery(id+"F0.wireOp",EDGE,"E564"),sQuery(id+"F0.wireOp",EDGE,"E565"),sQuery(id+"F0.wireOp",EDGE,"E566"),sQuery(id+"F0.wireOp",EDGE,"E567"),sQuery(id+"F0.wireOp",EDGE,"E568"),sQuery(id+"F0.wireOp",EDGE,"E569"),sQuery(id+"F0.wireOp",EDGE,"E570"),sQuery(id+"F0.wireOp",EDGE,"E571"),sQuery(id+"F0.wireOp",EDGE,"E572"),sQuery(id+"F0.wireOp",EDGE,"E573"),sQuery(id+"F0.wireOp",EDGE,"E574"),sQuery(id+"F0.wireOp",EDGE,"E575"),sQuery(id+"F0.wireOp",EDGE,"E576"),sQuery(id+"F0.wireOp",EDGE,"E577"),sQuery(id+"F0.wireOp",EDGE,"E578"),sQuery(id+"F0.wireOp",EDGE,"E579"),sQuery(id+"F0.wireOp",EDGE,"E580"),sQuery(id+"F0.wireOp",EDGE,"E581"),sQuery(id+"F0.wireOp",EDGE,"E582"),sQuery(id+"F0.wireOp",EDGE,"E583"),sQuery(id+"F0.wireOp",EDGE,"E584"),sQuery(id+"F0.wireOp",EDGE,"E585"),sQuery(id+"F0.wireOp",EDGE,"E586"),sQuery(id+"F0.wireOp",EDGE,"E587"),sQuery(id+"F0.wireOp",EDGE,"E588"),sQuery(id+"F0.wireOp",EDGE,"E589"),sQuery(id+"F0.wireOp",EDGE,"E590"),sQuery(id+"F0.wireOp",EDGE,"E591"),sQuery(id+"F0.wireOp",EDGE,"E592"),sQuery(id+"F0.wireOp",EDGE,"E593"),sQuery(id+"F0.wireOp",EDGE,"E594"),sQuery(id+"F0.wireOp",EDGE,"E595"),sQuery(id+"F0.wireOp",EDGE,"E596"),sQuery(id+"F0.wireOp",EDGE,"E597"),sQuery(id+"F0.wireOp",EDGE,"E598"),sQuery(id+"F0.wireOp",EDGE,"E599"),sQuery(id+"F0.wireOp",EDGE,"E600"),sQuery(id+"F0.wireOp",EDGE,"E601"),sQuery(id+"F0.wireOp",EDGE,"E602"),sQuery(id+"F0.wireOp",EDGE,"E603"),sQuery(id+"F0.wireOp",EDGE,"E604"),sQuery(id+"F0.wireOp",EDGE,"E605"),sQuery(id+"F0.wireOp",EDGE,"E606"),sQuery(id+"F0.wireOp",EDGE,"E607"),sQuery(id+"F0.wireOp",EDGE,"E608"),sQuery(id+"F0.wireOp",EDGE,"E609"),sQuery(id+"F0.wireOp",EDGE,"E610"),sQuery(id+"F0.wireOp",EDGE,"E611"),sQuery(id+"F0.wireOp",EDGE,"E612"),sQuery(id+"F0.wireOp",EDGE,"E613"),sQuery(id+"F0.wireOp",EDGE,"E614"),sQuery(id+"F0.wireOp",EDGE,"E615"),sQuery(id+"F0.wireOp",EDGE,"E616"),sQuery(id+"F0.wireOp",EDGE,"E617"),sQuery(id+"F0.wireOp",EDGE,"E618"),sQuery(id+"F0.wireOp",EDGE,"E619"),sQuery(id+"F0.wireOp",EDGE,"E620"),sQuery(id+"F0.wireOp",EDGE,"E621"),sQuery(id+"F0.wireOp",EDGE,"E622"),sQuery(id+"F0.wireOp",EDGE,"E623"),sQuery(id+"F0.wireOp",EDGE,"E624"),sQuery(id+"F0.wireOp",EDGE,"E625"),sQuery(id+"F0.wireOp",EDGE,"E626"),sQuery(id+"F0.wireOp",EDGE,"E627"),sQuery(id+"F0.wireOp",EDGE,"E628"),sQuery(id+"F0.wireOp",EDGE,"E629"),sQuery(id+"F0.wireOp",EDGE,"E630"),sQuery(id+"F0.wireOp",EDGE,"E631"),sQuery(id+"F0.wireOp",EDGE,"E632"),sQuery(id+"F0.wireOp",EDGE,"E633"),sQuery(id+"F0.wireOp",EDGE,"E634"),sQuery(id+"F0.wireOp",EDGE,"E635"),sQuery(id+"F0.wireOp",EDGE,"E636"),sQuery(id+"F0.wireOp",EDGE,"E637"),sQuery(id+"F0.wireOp",EDGE,"E638"),sQuery(id+"F0.wireOp",EDGE,"E639"),sQuery(id+"F0.wireOp",EDGE,"E640"),sQuery(id+"F0.wireOp",EDGE,"E641"),sQuery(id+"F0.wireOp",EDGE,"E642"),sQuery(id+"F0.wireOp",EDGE,"E643"),sQuery(id+"F0.wireOp",EDGE,"E644"),sQuery(id+"F0.wireOp",EDGE,"E645"),sQuery(id+"F0.wireOp",EDGE,"E646"),sQuery(id+"F0.wireOp",EDGE,"E647"),sQuery(id+"F0.wireOp",EDGE,"E648"),sQuery(id+"F0.wireOp",EDGE,"E649"),sQuery(id+"F0.wireOp",EDGE,"E650"),sQuery(id+"F0.wireOp",EDGE,"E651"),sQuery(id+"F0.wireOp",EDGE,"E652"),sQuery(id+"F0.wireOp",EDGE,"E653"),sQuery(id+"F0.wireOp",EDGE,"E654"),sQuery(id+"F0.wireOp",EDGE,"E655"),sQuery(id+"F0.wireOp",EDGE,"E656"),sQuery(id+"F0.wireOp",EDGE,"E657"),sQuery(id+"F0.wireOp",EDGE,"E658"),sQuery(id+"F0.wireOp",EDGE,"E659"),sQuery(id+"F0.wireOp",EDGE,"E660"),sQuery(id+"F0.wireOp",EDGE,"E661"),sQuery(id+"F0.wireOp",EDGE,"E662"),sQuery(id+"F0.wireOp",EDGE,"E663"),sQuery(id+"F0.wireOp",EDGE,"E664"),sQuery(id+"F0.wireOp",EDGE,"E665"),sQuery(id+"F0.wireOp",EDGE,"E666"),sQuery(id+"F0.wireOp",EDGE,"E667"),sQuery(id+"F0.wireOp",EDGE,"E668"),sQuery(id+"F0.wireOp",EDGE,"E669"),sQuery(id+"F0.wireOp",EDGE,"E670"),sQuery(id+"F0.wireOp",EDGE,"E671"),sQuery(id+"F0.wireOp",EDGE,"E672"),sQuery(id+"F0.wireOp",EDGE,"E673"),sQuery(id+"F0.wireOp",EDGE,"E674"),sQuery(id+"F0.wireOp",EDGE,"E675"),sQuery(id+"F0.wireOp",EDGE,"E676"),sQuery(id+"F0.wireOp",EDGE,"E677"),sQuery(id+"F0.wireOp",EDGE,"E678"),sQuery(id+"F0.wireOp",EDGE,"E679"),sQuery(id+"F0.wireOp",EDGE,"E680"),sQuery(id+"F0.wireOp",EDGE,"E681"),sQuery(id+"F0.wireOp",EDGE,"E682"),sQuery(id+"F0.wireOp",EDGE,"E683"),sQuery(id+"F0.wireOp",EDGE,"E684"),sQuery(id+"F0.wireOp",EDGE,"E685"),sQuery(id+"F0.wireOp",EDGE,"E686"),sQuery(id+"F0.wireOp",EDGE,"E687"),sQuery(id+"F0.wireOp",EDGE,"E688"),sQuery(id+"F0.wireOp",EDGE,"E689"),sQuery(id+"F0.wireOp",EDGE,"E690"),sQuery(id+"F0.wireOp",EDGE,"E691"),sQuery(id+"F0.wireOp",EDGE,"E692"),sQuery(id+"F0.wireOp",EDGE,"E693"),sQuery(id+"F0.wireOp",EDGE,"E694"),sQuery(id+"F0.wireOp",EDGE,"E695"),sQuery(id+"F0.wireOp",EDGE,"E696"),sQuery(id+"F0.wireOp",EDGE,"E697"),sQuery(id+"F0.wireOp",EDGE,"E698"),sQuery(id+"F0.wireOp",EDGE,"E699"),sQuery(id+"F0.wireOp",EDGE,"E700"),sQuery(id+"F0.wireOp",EDGE,"E701"),sQuery(id+"F0.wireOp",EDGE,"E702"),sQuery(id+"F0.wireOp",EDGE,"E703"),sQuery(id+"F0.wireOp",EDGE,"E704"),sQuery(id+"F0.wireOp",EDGE,"E705"),sQuery(id+"F0.wireOp",EDGE,"E706"),sQuery(id+"F0.wireOp",EDGE,"E707"),sQuery(id+"F0.wireOp",EDGE,"E708"),sQuery(id+"F0.wireOp",EDGE,"E709"),sQuery(id+"F0.wireOp",EDGE,"E710"),sQuery(id+"F0.wireOp",EDGE,"E711"),sQuery(id+"F0.wireOp",EDGE,"E712"),sQuery(id+"F0.wireOp",EDGE,"E713"),sQuery(id+"F0.wireOp",EDGE,"E714"),sQuery(id+"F0.wireOp",EDGE,"E715"),sQuery(id+"F0.wireOp",EDGE,"E716"),sQuery(id+"F0.wireOp",EDGE,"E717"),sQuery(id+"F0.wireOp",EDGE,"E718"),sQuery(id+"F0.wireOp",EDGE,"E719"),sQuery(id+"F0.wireOp",EDGE,"E720"),sQuery(id+"F0.wireOp",EDGE,"E721"),sQuery(id+"F0.wireOp",EDGE,"E722"),sQuery(id+"F0.wireOp",EDGE,"E723"),sQuery(id+"F0.wireOp",EDGE,"E724"),sQuery(id+"F0.wireOp",EDGE,"E725"),sQuery(id+"F0.wireOp",EDGE,"E726"),sQuery(id+"F0.wireOp",EDGE,"E727"),sQuery(id+"F0.wireOp",EDGE,"E728"),sQuery(id+"F0.wireOp",EDGE,"E729"),sQuery(id+"F0.wireOp",EDGE,"E730"),sQuery(id+"F0.wireOp",EDGE,"E731"),sQuery(id+"F0.wireOp",EDGE,"E732"),sQuery(id+"F0.wireOp",EDGE,"E733"),sQuery(id+"F0.wireOp",EDGE,"E734"),sQuery(id+"F0.wireOp",EDGE,"E735"),sQuery(id+"F0.wireOp",EDGE,"E736"),sQuery(id+"F0.wireOp",EDGE,"E737"),sQuery(id+"F0.wireOp",EDGE,"E738"),sQuery(id+"F0.wireOp",EDGE,"E739"),sQuery(id+"F0.wireOp",EDGE,"E740"),sQuery(id+"F0.wireOp",EDGE,"E741"),sQuery(id+"F0.wireOp",EDGE,"E742"),sQuery(id+"F0.wireOp",EDGE,"E743"),sQuery(id+"F0.wireOp",EDGE,"E744"),sQuery(id+"F0.wireOp",EDGE,"E745"),sQuery(id+"F0.wireOp",EDGE,"E746"),sQuery(id+"F0.wireOp",EDGE,"E747"),sQuery(id+"F0.wireOp",EDGE,"E748"),sQuery(id+"F0.wireOp",EDGE,"E749"),sQuery(id+"F0.wireOp",EDGE,"E750"),sQuery(id+"F0.wireOp",EDGE,"E751"),sQuery(id+"F0.wireOp",EDGE,"E752"),sQuery(id+"F0.wireOp",EDGE,"E753"),sQuery(id+"F0.wireOp",EDGE,"E754"),sQuery(id+"F0.wireOp",EDGE,"E755"),sQuery(id+"F0.wireOp",EDGE,"E756"),sQuery(id+"F0.wireOp",EDGE,"E757"),sQuery(id+"F0.wireOp",EDGE,"E758"),sQuery(id+"F0.wireOp",EDGE,"E759"),sQuery(id+"F0.wireOp",EDGE,"E760"),sQuery(id+"F0.wireOp",EDGE,"E761"),sQuery(id+"F0.wireOp",EDGE,"E762"),sQuery(id+"F0.wireOp",EDGE,"E763"),sQuery(id+"F0.wireOp",EDGE,"E764"),sQuery(id+"F0.wireOp",EDGE,"E765"),sQuery(id+"F0.wireOp",EDGE,"E766"),sQuery(id+"F0.wireOp",EDGE,"E767"),sQuery(id+"F0.wireOp",EDGE,"E768"),sQuery(id+"F0.wireOp",EDGE,"E769"),sQuery(id+"F0.wireOp",EDGE,"E770"),sQuery(id+"F0.wireOp",EDGE,"E771"),sQuery(id+"F0.wireOp",EDGE,"E772"),sQuery(id+"F0.wireOp",EDGE,"E773"),sQuery(id+"F0.wireOp",EDGE,"E774"),sQuery(id+"F0.wireOp",EDGE,"E775"),sQuery(id+"F0.wireOp",EDGE,"E776"),sQuery(id+"F0.wireOp",EDGE,"E777"),sQuery(id+"F0.wireOp",EDGE,"E778"),sQuery(id+"F0.wireOp",EDGE,"E779"),sQuery(id+"F0.wireOp",EDGE,"E780"),sQuery(id+"F0.wireOp",EDGE,"E781"),sQuery(id+"F0.wireOp",EDGE,"E782"),sQuery(id+"F0.wireOp",EDGE,"E783"),sQuery(id+"F0.wireOp",EDGE,"E784"),sQuery(id+"F0.wireOp",EDGE,"E785"),sQuery(id+"F0.wireOp",EDGE,"E786"),sQuery(id+"F0.wireOp",EDGE,"E787"),sQuery(id+"F0.wireOp",EDGE,"E788"),sQuery(id+"F0.wireOp",EDGE,"E789"),sQuery(id+"F0.wireOp",EDGE,"E790"),sQuery(id+"F0.wireOp",EDGE,"E791"),sQuery(id+"F0.wireOp",EDGE,"E792"),sQuery(id+"F0.wireOp",EDGE,"E793"),sQuery(id+"F0.wireOp",EDGE,"E794"),sQuery(id+"F0.wireOp",EDGE,"E795"),sQuery(id+"F0.wireOp",EDGE,"E796"),sQuery(id+"F0.wireOp",EDGE,"E797"),sQuery(id+"F0.wireOp",EDGE,"E798"),sQuery(id+"F0.wireOp",EDGE,"E799"),sQuery(id+"F0.wireOp",EDGE,"E800"),sQuery(id+"F0.wireOp",EDGE,"E801"),sQuery(id+"F0.wireOp",EDGE,"E802"),sQuery(id+"F0.wireOp",EDGE,"E803"),sQuery(id+"F0.wireOp",EDGE,"E804"),sQuery(id+"F0.wireOp",EDGE,"E805"),sQuery(id+"F0.wireOp",EDGE,"E806"),sQuery(id+"F0.wireOp",EDGE,"E807"),sQuery(id+"F0.wireOp",EDGE,"E808"),sQuery(id+"F0.wireOp",EDGE,"E809"),sQuery(id+"F0.wireOp",EDGE,"E810"),sQuery(id+"F0.wireOp",EDGE,"E811"),sQuery(id+"F0.wireOp",EDGE,"E812"),sQuery(id+"F0.wireOp",EDGE,"E813"),sQuery(id+"F0.wireOp",EDGE,"E814"),sQuery(id+"F0.wireOp",EDGE,"E815"),sQuery(id+"F0.wireOp",EDGE,"E816"),sQuery(id+"F0.wireOp",EDGE,"E817"),sQuery(id+"F0.wireOp",EDGE,"E818"),sQuery(id+"F0.wireOp",EDGE,"E819"),sQuery(id+"F0.wireOp",EDGE,"E820"),sQuery(id+"F0.wireOp",EDGE,"E821"),sQuery(id+"F0.wireOp",EDGE,"E822"),sQuery(id+"F0.wireOp",EDGE,"E823"),sQuery(id+"F0.wireOp",EDGE,"E824"),sQuery(id+"F0.wireOp",EDGE,"E825"),sQuery(id+"F0.wireOp",EDGE,"E826"),sQuery(id+"F0.wireOp",EDGE,"E827"),sQuery(id+"F0.wireOp",EDGE,"E828"),sQuery(id+"F0.wireOp",EDGE,"E829"),sQuery(id+"F0.wireOp",EDGE,"E830"),sQuery(id+"F0.wireOp",EDGE,"E831"),sQuery(id+"F0.wireOp",EDGE,"E832"),sQuery(id+"F0.wireOp",EDGE,"E833"),sQuery(id+"F0.wireOp",EDGE,"E834"),sQuery(id+"F0.wireOp",EDGE,"E835"),sQuery(id+"F0.wireOp",EDGE,"E836"),sQuery(id+"F0.wireOp",EDGE,"E837"),sQuery(id+"F0.wireOp",EDGE,"E838"),sQuery(id+"F0.wireOp",EDGE,"E839"),sQuery(id+"F0.wireOp",EDGE,"E840"),sQuery(id+"F0.wireOp",EDGE,"E841"),sQuery(id+"F0.wireOp",EDGE,"E842"),sQuery(id+"F0.wireOp",EDGE,"E843"),sQuery(id+"F0.wireOp",EDGE,"E844"),sQuery(id+"F0.wireOp",EDGE,"E845"),sQuery(id+"F0.wireOp",EDGE,"E846"),sQuery(id+"F0.wireOp",EDGE,"E847"),sQuery(id+"F0.wireOp",EDGE,"E848"),sQuery(id+"F0.wireOp",EDGE,"E849"),sQuery(id+"F0.wireOp",EDGE,"E850"),sQuery(id+"F0.wireOp",EDGE,"E851"),sQuery(id+"F0.wireOp",EDGE,"E852"),sQuery(id+"F0.wireOp",EDGE,"E853"),sQuery(id+"F0.wireOp",EDGE,"E854"),sQuery(id+"F0.wireOp",EDGE,"E855"),sQuery(id+"F0.wireOp",EDGE,"E856"),sQuery(id+"F0.wireOp",EDGE,"E857"),sQuery(id+"F0.wireOp",EDGE,"E858"),sQuery(id+"F0.wireOp",EDGE,"E859"),sQuery(id+"F0.wireOp",EDGE,"E860"),sQuery(id+"F0.wireOp",EDGE,"E861"),sQuery(id+"F0.wireOp",EDGE,"E862"),sQuery(id+"F0.wireOp",EDGE,"E863"),sQuery(id+"F0.wireOp",EDGE,"E864"),sQuery(id+"F0.wireOp",EDGE,"E865"),sQuery(id+"F0.wireOp",EDGE,"E866"),sQuery(id+"F0.wireOp",EDGE,"E867"),sQuery(id+"F0.wireOp",EDGE,"E868"),sQuery(id+"F0.wireOp",EDGE,"E869"),sQuery(id+"F0.wireOp",EDGE,"E870"),sQuery(id+"F0.wireOp",EDGE,"E871"),sQuery(id+"F0.wireOp",EDGE,"E872"),sQuery(id+"F0.wireOp",EDGE,"E873"),sQuery(id+"F0.wireOp",EDGE,"E874"),sQuery(id+"F0.wireOp",EDGE,"E875"),sQuery(id+"F0.wireOp",EDGE,"E876"),sQuery(id+"F0.wireOp",EDGE,"E877"),sQuery(id+"F0.wireOp",EDGE,"E878"),sQuery(id+"F0.wireOp",EDGE,"E879"),sQuery(id+"F0.wireOp",EDGE,"E880"),sQuery(id+"F0.wireOp",EDGE,"E881"),sQuery(id+"F0.wireOp",EDGE,"E882"),sQuery(id+"F0.wireOp",EDGE,"E883"),sQuery(id+"F0.wireOp",EDGE,"E884"),sQuery(id+"F0.wireOp",EDGE,"E885"),sQuery(id+"F0.wireOp",EDGE,"E886"),sQuery(id+"F0.wireOp",EDGE,"E887"),sQuery(id+"F0.wireOp",EDGE,"E888"),sQuery(id+"F0.wireOp",EDGE,"E889"),sQuery(id+"F0.wireOp",EDGE,"E890"),sQuery(id+"F0.wireOp",EDGE,"E891"),sQuery(id+"F0.wireOp",EDGE,"E892"),sQuery(id+"F0.wireOp",EDGE,"E893"),sQuery(id+"F0.wireOp",EDGE,"E894"),sQuery(id+"F0.wireOp",EDGE,"E895"),sQuery(id+"F0.wireOp",EDGE,"E896"),sQuery(id+"F0.wireOp",EDGE,"E897"),sQuery(id+"F0.wireOp",EDGE,"E898"),sQuery(id+"F0.wireOp",EDGE,"E899"),sQuery(id+"F0.wireOp",EDGE,"E900"),sQuery(id+"F0.wireOp",EDGE,"E901"),sQuery(id+"F0.wireOp",EDGE,"E902"),sQuery(id+"F0.wireOp",EDGE,"E903"),sQuery(id+"F0.wireOp",EDGE,"E904"),sQuery(id+"F0.wireOp",EDGE,"E905"),sQuery(id+"F0.wireOp",EDGE,"E906"),sQuery(id+"F0.wireOp",EDGE,"E907"),sQuery(id+"F0.wireOp",EDGE,"E908"),sQuery(id+"F0.wireOp",EDGE,"E909"),sQuery(id+"F0.wireOp",EDGE,"E910"),sQuery(id+"F0.wireOp",EDGE,"E911"),sQuery(id+"F0.wireOp",EDGE,"E912"),sQuery(id+"F0.wireOp",EDGE,"E913"),sQuery(id+"F0.wireOp",EDGE,"E914"),sQuery(id+"F0.wireOp",EDGE,"E915"),sQuery(id+"F0.wireOp",EDGE,"E916"),sQuery(id+"F0.wireOp",EDGE,"E917"),sQuery(id+"F0.wireOp",EDGE,"E918"),sQuery(id+"F0.wireOp",EDGE,"E919"),sQuery(id+"F0.wireOp",EDGE,"E920"),sQuery(id+"F0.wireOp",EDGE,"E921"),sQuery(id+"F0.wireOp",EDGE,"E922"),sQuery(id+"F0.wireOp",EDGE,"E923"),sQuery(id+"F0.wireOp",EDGE,"E924"),sQuery(id+"F0.wireOp",EDGE,"E925"),sQuery(id+"F0.wireOp",EDGE,"E926"),sQuery(id+"F0.wireOp",EDGE,"E927"),sQuery(id+"F0.wireOp",EDGE,"E928"),sQuery(id+"F0.wireOp",EDGE,"E929"),sQuery(id+"F0.wireOp",EDGE,"E930"),sQuery(id+"F0.wireOp",EDGE,"E931"),sQuery(id+"F0.wireOp",EDGE,"E932"),sQuery(id+"F0.wireOp",EDGE,"E933"),sQuery(id+"F0.wireOp",EDGE,"E934"),sQuery(id+"F0.wireOp",EDGE,"E935"),sQuery(id+"F0.wireOp",EDGE,"E936"),sQuery(id+"F0.wireOp",EDGE,"E937"),sQuery(id+"F0.wireOp",EDGE,"E938"),sQuery(id+"F0.wireOp",EDGE,"E939"),sQuery(id+"F0.wireOp",EDGE,"E940"),sQuery(id+"F0.wireOp",EDGE,"E941"),sQuery(id+"F0.wireOp",EDGE,"E942"),sQuery(id+"F0.wireOp",EDGE,"E943"),sQuery(id+"F0.wireOp",EDGE,"E944"),sQuery(id+"F0.wireOp",EDGE,"E945"),sQuery(id+"F0.wireOp",EDGE,"E946"),sQuery(id+"F0.wireOp",EDGE,"E947"),sQuery(id+"F0.wireOp",EDGE,"E948"),sQuery(id+"F0.wireOp",EDGE,"E949"),sQuery(id+"F0.wireOp",EDGE,"E950"),sQuery(id+"F0.wireOp",EDGE,"E951"),sQuery(id+"F0.wireOp",EDGE,"E952"),sQuery(id+"F0.wireOp",EDGE,"E953"),sQuery(id+"F0.wireOp",EDGE,"E954"),sQuery(id+"F0.wireOp",EDGE,"E955"),sQuery(id+"F0.wireOp",EDGE,"E956"),sQuery(id+"F0.wireOp",EDGE,"E957"),sQuery(id+"F0.wireOp",EDGE,"E958"),sQuery(id+"F0.wireOp",EDGE,"E959"),sQuery(id+"F0.wireOp",EDGE,"E960"),sQuery(id+"F0.wireOp",EDGE,"E961"),sQuery(id+"F0.wireOp",EDGE,"E962"),sQuery(id+"F0.wireOp",EDGE,"E963"),sQuery(id+"F0.wireOp",EDGE,"E964"),sQuery(id+"F0.wireOp",EDGE,"E965"),sQuery(id+"F0.wireOp",EDGE,"E966"),sQuery(id+"F0.wireOp",EDGE,"E967"),sQuery(id+"F0.wireOp",EDGE,"E968"),sQuery(id+"F0.wireOp",EDGE,"E969"),sQuery(id+"F0.wireOp",EDGE,"E970"),sQuery(id+"F0.wireOp",EDGE,"E971"),sQuery(id+"F0.wireOp",EDGE,"E972"),sQuery(id+"F0.wireOp",EDGE,"E973"),sQuery(id+"F0.wireOp",EDGE,"E974"),sQuery(id+"F0.wireOp",EDGE,"E975"),sQuery(id+"F0.wireOp",EDGE,"E976"),sQuery(id+"F0.wireOp",EDGE,"E977"),sQuery(id+"F0.wireOp",EDGE,"E978"),sQuery(id+"F0.wireOp",EDGE,"E979"),sQuery(id+"F0.wireOp",EDGE,"E980"),sQuery(id+"F0.wireOp",EDGE,"E981"),sQuery(id+"F0.wireOp",EDGE,"E982"),sQuery(id+"F0.wireOp",EDGE,"E983"),sQuery(id+"F0.wireOp",EDGE,"E984"),sQuery(id+"F0.wireOp",EDGE,"E985"),sQuery(id+"F0.wireOp",EDGE,"E986"),sQuery(id+"F0.wireOp",EDGE,"E987"),sQuery(id+"F0.wireOp",EDGE,"E988"),sQuery(id+"F0.wireOp",EDGE,"E989"),sQuery(id+"F0.wireOp",EDGE,"E990"),sQuery(id+"F0.wireOp",EDGE,"E991"),sQuery(id+"F0.wireOp",EDGE,"E992"),sQuery(id+"F0.wireOp",EDGE,"E993"),sQuery(id+"F0.wireOp",EDGE,"E994"),sQuery(id+"F0.wireOp",EDGE,"E995"),sQuery(id+"F0.wireOp",EDGE,"E996"),sQuery(id+"F0.wireOp",EDGE,"E997"),sQuery(id+"F0.wireOp",EDGE,"E998"),sQuery(id+"F0.wireOp",EDGE,"E999"),sQuery(id+"F0.wireOp",EDGE,"E1000"),sQuery(id+"F0.wireOp",EDGE,"E1001"),sQuery(id+"F0.wireOp",EDGE,"E1002"),sQuery(id+"F0.wireOp",EDGE,"E1003"),sQuery(id+"F0.wireOp",EDGE,"E1004"),sQuery(id+"F0.wireOp",EDGE,"E1005"),sQuery(id+"F0.wireOp",EDGE,"E1006"),sQuery(id+"F0.wireOp",EDGE,"E1007"),sQuery(id+"F0.wireOp",EDGE,"E1008"),sQuery(id+"F0.wireOp",EDGE,"E1009"),sQuery(id+"F0.wireOp",EDGE,"E1010"),sQuery(id+"F0.wireOp",EDGE,"E1011"),sQuery(id+"F0.wireOp",EDGE,"E1012"),sQuery(id+"F0.wireOp",EDGE,"E1013"),sQuery(id+"F0.wireOp",EDGE,"E1014"),sQuery(id+"F0.wireOp",EDGE,"E1015"),sQuery(id+"F0.wireOp",EDGE,"E1016"),sQuery(id+"F0.wireOp",EDGE,"E1017"),sQuery(id+"F0.wireOp",EDGE,"E1018"),sQuery(id+"F0.wireOp",EDGE,"E1019"),sQuery(id+"F0.wireOp",EDGE,"E1020"),sQuery(id+"F0.wireOp",EDGE,"E1021"),sQuery(id+"F0.wireOp",EDGE,"E1022"),sQuery(id+"F0.wireOp",EDGE,"E1023"),sQuery(id+"F0.wireOp",EDGE,"E1024"),sQuery(id+"F0.wireOp",EDGE,"E1025"),sQuery(id+"F0.wireOp",EDGE,"E1026"),sQuery(id+"F0.wireOp",EDGE,"E1027"),sQuery(id+"F0.wireOp",EDGE,"E1028"),sQuery(id+"F0.wireOp",EDGE,"E1029"),sQuery(id+"F0.wireOp",EDGE,"E1030"),sQuery(id+"F0.wireOp",EDGE,"E1031"),sQuery(id+"F0.wireOp",EDGE,"E1032"),sQuery(id+"F0.wireOp",EDGE,"E1033"),sQuery(id+"F0.wireOp",EDGE,"E1034"),sQuery(id+"F0.wireOp",EDGE,"E1035"),sQuery(id+"F0.wireOp",EDGE,"E1036"),sQuery(id+"F0.wireOp",EDGE,"E1037"),sQuery(id+"F0.wireOp",EDGE,"E1038"),sQuery(id+"F0.wireOp",EDGE,"E1039"),sQuery(id+"F0.wireOp",EDGE,"E1040"),sQuery(id+"F0.wireOp",EDGE,"E1041"),sQuery(id+"F0.wireOp",EDGE,"E1042"),sQuery(id+"F0.wireOp",EDGE,"E1043"),sQuery(id+"F0.wireOp",EDGE,"E1044"),sQuery(id+"F0.wireOp",EDGE,"E1045"),sQuery(id+"F0.wireOp",EDGE,"E1046"),sQuery(id+"F0.wireOp",EDGE,"E1047"),sQuery(id+"F0.wireOp",EDGE,"E1048"),sQuery(id+"F0.wireOp",EDGE,"E1049"),sQuery(id+"F0.wireOp",EDGE,"E1050"),sQuery(id+"F0.wireOp",EDGE,"E1051"),sQuery(id+"F0.wireOp",EDGE,"E1052"),sQuery(id+"F0.wireOp",EDGE,"E1053"),sQuery(id+"F0.wireOp",EDGE,"E1054"),sQuery(id+"F0.wireOp",EDGE,"E1055"),sQuery(id+"F0.wireOp",EDGE,"E1056"),sQuery(id+"F0.wireOp",EDGE,"E1057"),sQuery(id+"F0.wireOp",EDGE,"E1058"),sQuery(id+"F0.wireOp",EDGE,"E1059"),sQuery(id+"F0.wireOp",EDGE,"E1060"),sQuery(id+"F0.wireOp",EDGE,"E1061"),sQuery(id+"F0.wireOp",EDGE,"E1062"),sQuery(id+"F0.wireOp",EDGE,"E1063"),sQuery(id+"F0.wireOp",EDGE,"E1064"),sQuery(id+"F0.wireOp",EDGE,"E1065"),sQuery(id+"F0.wireOp",EDGE,"E1066"),sQuery(id+"F0.wireOp",EDGE,"E1067"),sQuery(id+"F0.wireOp",EDGE,"E1068"),sQuery(id+"F0.wireOp",EDGE,"E1069"),sQuery(id+"F0.wireOp",EDGE,"E1070"),sQuery(id+"F0.wireOp",EDGE,"E1071"),sQuery(id+"F0.wireOp",EDGE,"E1072"),sQuery(id+"F0.wireOp",EDGE,"E1073"),sQuery(id+"F0.wireOp",EDGE,"E1074"),sQuery(id+"F0.wireOp",EDGE,"E1075"),sQuery(id+"F0.wireOp",EDGE,"E1076"),sQuery(id+"F0.wireOp",EDGE,"E1077"),sQuery(id+"F0.wireOp",EDGE,"E1078"),sQuery(id+"F0.wireOp",EDGE,"E1079"),sQuery(id+"F0.wireOp",EDGE,"E1080"),sQuery(id+"F0.wireOp",EDGE,"E1081"),sQuery(id+"F0.wireOp",EDGE,"E1082"),sQuery(id+"F0.wireOp",EDGE,"E1083"),sQuery(id+"F0.wireOp",EDGE,"E1084"),sQuery(id+"F0.wireOp",EDGE,"E1085"),sQuery(id+"F0.wireOp",EDGE,"E1086"),sQuery(id+"F0.wireOp",EDGE,"E1087"),sQuery(id+"F0.wireOp",EDGE,"E1088"),sQuery(id+"F0.wireOp",EDGE,"E1089"),sQuery(id+"F0.wireOp",EDGE,"E1090"),sQuery(id+"F0.wireOp",EDGE,"E1091"),sQuery(id+"F0.wireOp",EDGE,"E1092"),sQuery(id+"F0.wireOp",EDGE,"E1093"),sQuery(id+"F0.wireOp",EDGE,"E1094"),sQuery(id+"F0.wireOp",EDGE,"E1095"),sQuery(id+"F0.wireOp",EDGE,"E1096"),sQuery(id+"F0.wireOp",EDGE,"E1097"),sQuery(id+"F0.wireOp",EDGE,"E1098"),sQuery(id+"F0.wireOp",EDGE,"E1099"),sQuery(id+"F0.wireOp",EDGE,"E1100"),sQuery(id+"F0.wireOp",EDGE,"E1101"),sQuery(id+"F0.wireOp",EDGE,"E1102"),sQuery(id+"F0.wireOp",EDGE,"E1103"),sQuery(id+"F0.wireOp",EDGE,"E1104"),sQuery(id+"F0.wireOp",EDGE,"E1105"),sQuery(id+"F0.wireOp",EDGE,"E1106"),sQuery(id+"F0.wireOp",EDGE,"E1107"),sQuery(id+"F0.wireOp",EDGE,"E1108"),sQuery(id+"F0.wireOp",EDGE,"E1109"),sQuery(id+"F0.wireOp",EDGE,"E1110"),sQuery(id+"F0.wireOp",EDGE,"E1111"),sQuery(id+"F0.wireOp",EDGE,"E1112"),sQuery(id+"F0.wireOp",EDGE,"E1113"),sQuery(id+"F0.wireOp",EDGE,"E1114"),sQuery(id+"F0.wireOp",EDGE,"E1115"),sQuery(id+"F0.wireOp",EDGE,"E1116"),sQuery(id+"F0.wireOp",EDGE,"E1117"),sQuery(id+"F0.wireOp",EDGE,"E1118"),sQuery(id+"F0.wireOp",EDGE,"E1119"),sQuery(id+"F0.wireOp",EDGE,"E1120"),sQuery(id+"F0.wireOp",EDGE,"E1121"),sQuery(id+"F0.wireOp",EDGE,"E1122"),sQuery(id+"F0.wireOp",EDGE,"E1123"),sQuery(id+"F0.wireOp",EDGE,"E1124"),sQuery(id+"F0.wireOp",EDGE,"E1125"),sQuery(id+"F0.wireOp",EDGE,"E1126"),sQuery(id+"F0.wireOp",EDGE,"E1127"),sQuery(id+"F0.wireOp",EDGE,"E1128"),sQuery(id+"F0.wireOp",EDGE,"E1129"),sQuery(id+"F0.wireOp",EDGE,"E1130"),sQuery(id+"F0.wireOp",EDGE,"E1131"),sQuery(id+"F0.wireOp",EDGE,"E1132"),sQuery(id+"F0.wireOp",EDGE,"E1133"),sQuery(id+"F0.wireOp",EDGE,"E1134"),sQuery(id+"F0.wireOp",EDGE,"E1135"),sQuery(id+"F0.wireOp",EDGE,"E1136"),sQuery(id+"F0.wireOp",EDGE,"E1137"),sQuery(id+"F0.wireOp",EDGE,"E1138"),sQuery(id+"F0.wireOp",EDGE,"E1139"),sQuery(id+"F0.wireOp",EDGE,"E1140"),sQuery(id+"F0.wireOp",EDGE,"E1141"),sQuery(id+"F0.wireOp",EDGE,"E1142"),sQuery(id+"F0.wireOp",EDGE,"E1143"),sQuery(id+"F0.wireOp",EDGE,"E1144"),sQuery(id+"F0.wireOp",EDGE,"E1145"),sQuery(id+"F0.wireOp",EDGE,"E1146"),sQuery(id+"F0.wireOp",EDGE,"E1147"),sQuery(id+"F0.wireOp",EDGE,"E1148"),sQuery(id+"F0.wireOp",EDGE,"E1149"),sQuery(id+"F0.wireOp",EDGE,"E1150"),sQuery(id+"F0.wireOp",EDGE,"E1151"),sQuery(id+"F0.wireOp",EDGE,"E1152"),sQuery(id+"F0.wireOp",EDGE,"E1153"),sQuery(id+"F0.wireOp",EDGE,"E1154"),sQuery(id+"F0.wireOp",EDGE,"E1155"),sQuery(id+"F0.wireOp",EDGE,"E1156"),sQuery(id+"F0.wireOp",EDGE,"E1157"),sQuery(id+"F0.wireOp",EDGE,"E1158"),sQuery(id+"F0.wireOp",EDGE,"E1159"),sQuery(id+"F0.wireOp",EDGE,"E1160"),sQuery(id+"F0.wireOp",EDGE,"E1161"),sQuery(id+"F0.wireOp",EDGE,"E1162"),sQuery(id+"F0.wireOp",EDGE,"E1163"),sQuery(id+"F0.wireOp",EDGE,"E1164"),sQuery(id+"F0.wireOp",EDGE,"E1165"),sQuery(id+"F0.wireOp",EDGE,"E1166"),sQuery(id+"F0.wireOp",EDGE,"E1167"),sQuery(id+"F0.wireOp",EDGE,"E1168"),sQuery(id+"F0.wireOp",EDGE,"E1169"),sQuery(id+"F0.wireOp",EDGE,"E1170"),sQuery(id+"F0.wireOp",EDGE,"E1171"),sQuery(id+"F0.wireOp",EDGE,"E1172"),sQuery(id+"F0.wireOp",EDGE,"E1173"),sQuery(id+"F0.wireOp",EDGE,"E1174"),sQuery(id+"F0.wireOp",EDGE,"E1175"),sQuery(id+"F0.wireOp",EDGE,"E1176"),sQuery(id+"F0.wireOp",EDGE,"E1177"),sQuery(id+"F0.wireOp",EDGE,"E1178"),sQuery(id+"F0.wireOp",EDGE,"E1179"),sQuery(id+"F0.wireOp",EDGE,"E1180"),sQuery(id+"F0.wireOp",EDGE,"E1181"),sQuery(id+"F0.wireOp",EDGE,"E1182"),sQuery(id+"F0.wireOp",EDGE,"E1183"),sQuery(id+"F0.wireOp",EDGE,"E1184"),sQuery(id+"F0.wireOp",EDGE,"E1185"),sQuery(id+"F0.wireOp",EDGE,"E1186"),sQuery(id+"F0.wireOp",EDGE,"E1187"),sQuery(id+"F0.wireOp",EDGE,"E1188"),sQuery(id+"F0.wireOp",EDGE,"E1189"),sQuery(id+"F0.wireOp",EDGE,"E1190"),sQuery(id+"F0.wireOp",EDGE,"E1191"),sQuery(id+"F0.wireOp",EDGE,"E1192"),sQuery(id+"F0.wireOp",EDGE,"E1193"),sQuery(id+"F0.wireOp",EDGE,"E1194"),sQuery(id+"F0.wireOp",EDGE,"E1195"),sQuery(id+"F0.wireOp",EDGE,"E1196"),sQuery(id+"F0.wireOp",EDGE,"E1197"),sQuery(id+"F0.wireOp",EDGE,"E1198"),sQuery(id+"F0.wireOp",EDGE,"E1199"),sQuery(id+"F0.wireOp",EDGE,"E1200"),sQuery(id+"F0.wireOp",EDGE,"E1201"),sQuery(id+"F0.wireOp",EDGE,"E1202"),sQuery(id+"F0.wireOp",EDGE,"E1203"),sQuery(id+"F0.wireOp",EDGE,"E1204"),sQuery(id+"F0.wireOp",EDGE,"E1205"),sQuery(id+"F0.wireOp",EDGE,"E1206"),sQuery(id+"F0.wireOp",EDGE,"E1207"),sQuery(id+"F0.wireOp",EDGE,"E1208"),sQuery(id+"F0.wireOp",EDGE,"E1209"),sQuery(id+"F0.wireOp",EDGE,"E1210"),sQuery(id+"F0.wireOp",EDGE,"E1211"),sQuery(id+"F0.wireOp",EDGE,"E1212"),sQuery(id+"F0.wireOp",EDGE,"E1213"),sQuery(id+"F0.wireOp",EDGE,"E1214"),sQuery(id+"F0.wireOp",EDGE,"E1215"),sQuery(id+"F0.wireOp",EDGE,"E1216"),sQuery(id+"F0.wireOp",EDGE,"E1217"),sQuery(id+"F0.wireOp",EDGE,"E1218"),sQuery(id+"F0.wireOp",EDGE,"E1219"),sQuery(id+"F0.wireOp",EDGE,"E1220"),sQuery(id+"F0.wireOp",EDGE,"E1221"),sQuery(id+"F0.wireOp",EDGE,"E1222"),sQuery(id+"F0.wireOp",EDGE,"E1224"),sQuery(id+"F0.wireOp",EDGE,"E1225"),sQuery(id+"F0.wireOp",EDGE,"E1226"),sQuery(id+"F0.wireOp",EDGE,"E1228"),sQuery(id+"F0.wireOp",EDGE,"E1229"),sQuery(id+"F0.wireOp",EDGE,"E1230"),sQuery(id+"F0.wireOp",EDGE,"E1232"),sQuery(id+"F0.wireOp",EDGE,"E1233"),sQuery(id+"F0.wireOp",EDGE,"E1234"),sQuery(id+"F0.wireOp",EDGE,"E1236"),sQuery(id+"F0.wireOp",EDGE,"E1237"),sQuery(id+"F0.wireOp",EDGE,"E1238"),sQuery(id+"F0.wireOp",EDGE,"E1240"),sQuery(id+"F0.wireOp",EDGE,"E1241"),sQuery(id+"F0.wireOp",EDGE,"E1242"),sQuery(id+"F0.wireOp",EDGE,"E1244"),sQuery(id+"F0.wireOp",EDGE,"E1245"),sQuery(id+"F0.wireOp",EDGE,"E1246"),sQuery(id+"F0.wireOp",EDGE,"E1248"),sQuery(id+"F0.wireOp",EDGE,"E1249"),sQuery(id+"F0.wireOp",EDGE,"E1250"),sQuery(id+"F0.wireOp",EDGE,"E1252"),sQuery(id+"F0.wireOp",EDGE,"E1253"),sQuery(id+"F0.wireOp",EDGE,"E1254"),sQuery(id+"F0.wireOp",EDGE,"E1256"),sQuery(id+"F0.wireOp",EDGE,"E1257"),sQuery(id+"F0.wireOp",EDGE,"E1258"),sQuery(id+"F0.wireOp",EDGE,"E1260"),sQuery(id+"F0.wireOp",EDGE,"E1261"),sQuery(id+"F0.wireOp",EDGE,"E1262"),sQuery(id+"F0.wireOp",EDGE,"E1264"),sQuery(id+"F0.wireOp",EDGE,"E1265"),sQuery(id+"F0.wireOp",EDGE,"E1266"),sQuery(id+"F0.wireOp",EDGE,"E1268"),sQuery(id+"F0.wireOp",EDGE,"E1269"),sQuery(id+"F0.wireOp",EDGE,"E1270"),sQuery(id+"F0.wireOp",EDGE,"E1272"),sQuery(id+"F0.wireOp",EDGE,"E1273"),sQuery(id+"F0.wireOp",EDGE,"E1274"),sQuery(id+"F0.wireOp",EDGE,"E1276"),sQuery(id+"F0.wireOp",EDGE,"E1277"),sQuery(id+"F0.wireOp",EDGE,"E1278"),sQuery(id+"F0.wireOp",EDGE,"E1280"),sQuery(id+"F0.wireOp",EDGE,"E1281"),sQuery(id+"F0.wireOp",EDGE,"E1282"),sQuery(id+"F0.wireOp",EDGE,"E1284"),sQuery(id+"F0.wireOp",EDGE,"E1285"),sQuery(id+"F0.wireOp",EDGE,"E1286"),sQuery(id+"F0.wireOp",EDGE,"E1288"),sQuery(id+"F0.wireOp",EDGE,"E1289"),sQuery(id+"F0.wireOp",EDGE,"E1290"),sQuery(id+"F0.wireOp",EDGE,"E1292"),sQuery(id+"F0.wireOp",EDGE,"E1293"),sQuery(id+"F0.wireOp",EDGE,"E1294"),sQuery(id+"F0.wireOp",EDGE,"E1296"),sQuery(id+"F0.wireOp",EDGE,"E1297"),sQuery(id+"F0.wireOp",EDGE,"E1298"),sQuery(id+"F0.wireOp",EDGE,"E1300"),sQuery(id+"F0.wireOp",EDGE,"E1301"),sQuery(id+"F0.wireOp",EDGE,"E1302"),sQuery(id+"F0.wireOp",EDGE,"E1304"),sQuery(id+"F0.wireOp",EDGE,"E1305"),sQuery(id+"F0.wireOp",EDGE,"E1306"),sQuery(id+"F0.wireOp",EDGE,"E1308"),sQuery(id+"F0.wireOp",EDGE,"E1309"),sQuery(id+"F0.wireOp",EDGE,"E1310"),sQuery(id+"F0.wireOp",EDGE,"E1312"),sQuery(id+"F0.wireOp",EDGE,"E1313"),sQuery(id+"F0.wireOp",EDGE,"E1314"),sQuery(id+"F0.wireOp",EDGE,"E1316"),sQuery(id+"F0.wireOp",EDGE,"E1317"),sQuery(id+"F0.wireOp",EDGE,"E1318")])]});
            hole(context, id + "F8", {"style" : HoleStyle.SIMPLE, "endStyle" : HoleEndStyle.THROUGH, "holeDiameter" : 8 * mm, "majorDiameter" : 5 * mm, "isTappedThrough" : true, "tappedDepth" : 12 * mm, "tapClearance" : 3, "startFromSketch" : true, "locations" : qUnion([Q0, Q1, Q2, Q3, Q4, Q5, Q6, Q7]), "scope" : qUnion([Q8])});
        }
    });
